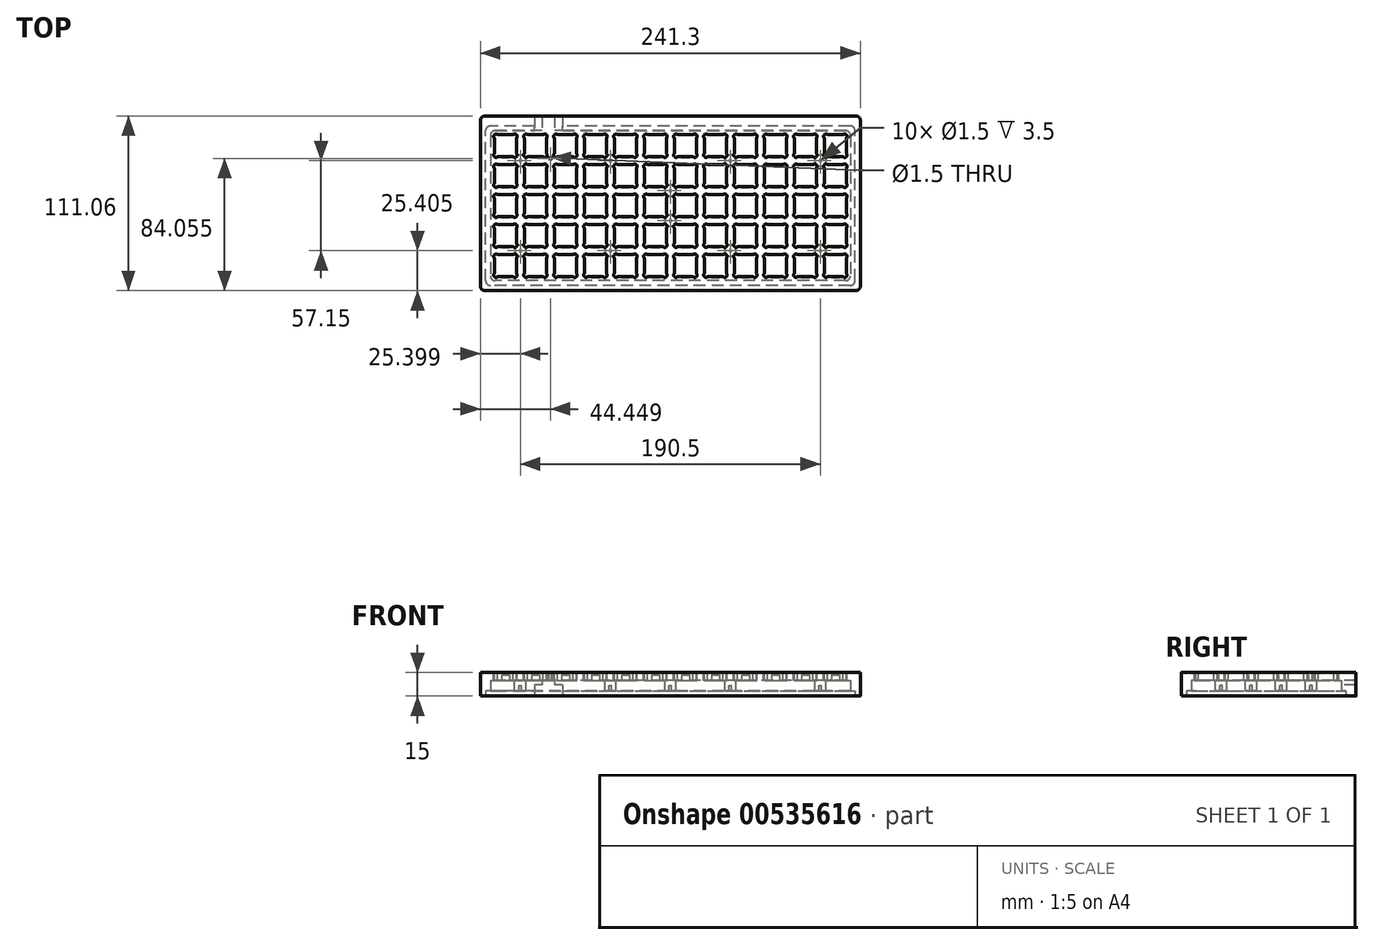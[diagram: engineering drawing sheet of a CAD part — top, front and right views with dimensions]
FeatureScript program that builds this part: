
annotation { "Feature Type Name" : "Feature", "Feature Type Description" : "" }
export const myFeature = defineFeature(function(context is Context, id is Id, definition is map)
    precondition{}
    {
        {
            var Q0;
            Q0=qCreatedBy(makeId("Top.planeOp"),FACE);
            var sketch = newSketch(context, id + "F0", { "sketchPlane" : qUnion([Q0])});
            skLineSegment(sketch, "E0", {"start": v(-120.65, 55.53) * mm, "end": v(120.65, 55.53) * mm});
            skLineSegment(sketch, "E1", {"start": v(120.65, 55.53) * mm, "end": v(120.65, -55.53) * mm});
            skLineSegment(sketch, "E2", {"start": v(120.65, -55.53) * mm, "end": v(-120.65, -55.53) * mm});
            skLineSegment(sketch, "E3", {"start": v(-120.65, -55.53) * mm, "end": v(-120.65, 55.53) * mm});
            skLineSegment(sketch, "E4", {"start": v(-111.78, -32.65) * mm, "end": v(-97.78, -32.65) * mm});
            skLineSegment(sketch, "E5", {"start": v(-97.78, -32.65) * mm, "end": v(-97.78, -46.65) * mm});
            skLineSegment(sketch, "E6", {"start": v(-97.78, -46.65) * mm, "end": v(-111.78, -46.65) * mm});
            skLineSegment(sketch, "E7", {"start": v(-111.78, -46.65) * mm, "end": v(-111.78, -32.65) * mm});
            skLineSegment(sketch, "E8", {"start": v(-92.73, -32.65) * mm, "end": v(-78.73, -32.65) * mm});
            skLineSegment(sketch, "E9", {"start": v(-78.73, -32.65) * mm, "end": v(-78.73, -46.65) * mm});
            skLineSegment(sketch, "E10", {"start": v(-78.73, -46.65) * mm, "end": v(-92.73, -46.65) * mm});
            skLineSegment(sketch, "E11", {"start": v(-92.73, -46.65) * mm, "end": v(-92.73, -32.65) * mm});
            skLineSegment(sketch, "E12", {"start": v(-73.68, -32.65) * mm, "end": v(-59.68, -32.65) * mm});
            skLineSegment(sketch, "E13", {"start": v(-59.68, -32.65) * mm, "end": v(-59.68, -46.65) * mm});
            skLineSegment(sketch, "E14", {"start": v(-59.68, -46.65) * mm, "end": v(-73.68, -46.65) * mm});
            skLineSegment(sketch, "E15", {"start": v(-73.68, -46.65) * mm, "end": v(-73.68, -32.65) * mm});
            skLineSegment(sketch, "E16", {"start": v(-54.63, -32.65) * mm, "end": v(-40.63, -32.65) * mm});
            skLineSegment(sketch, "E17", {"start": v(-40.63, -32.65) * mm, "end": v(-40.63, -46.65) * mm});
            skLineSegment(sketch, "E18", {"start": v(-40.63, -46.65) * mm, "end": v(-54.63, -46.65) * mm});
            skLineSegment(sketch, "E19", {"start": v(-54.63, -46.65) * mm, "end": v(-54.63, -32.65) * mm});
            skLineSegment(sketch, "E20", {"start": v(-35.58, -32.65) * mm, "end": v(-21.58, -32.65) * mm});
            skLineSegment(sketch, "E21", {"start": v(-21.58, -32.65) * mm, "end": v(-21.58, -46.65) * mm});
            skLineSegment(sketch, "E22", {"start": v(-21.58, -46.65) * mm, "end": v(-35.58, -46.65) * mm});
            skLineSegment(sketch, "E23", {"start": v(-35.58, -46.65) * mm, "end": v(-35.58, -32.65) * mm});
            skLineSegment(sketch, "E24", {"start": v(-16.53, -32.65) * mm, "end": v(-2.53, -32.65) * mm});
            skLineSegment(sketch, "E25", {"start": v(-2.53, -32.65) * mm, "end": v(-2.53, -46.65) * mm});
            skLineSegment(sketch, "E26", {"start": v(-2.53, -46.65) * mm, "end": v(-16.53, -46.65) * mm});
            skLineSegment(sketch, "E27", {"start": v(-16.53, -46.65) * mm, "end": v(-16.53, -32.65) * mm});
            skLineSegment(sketch, "E28", {"start": v(2.52, -32.65) * mm, "end": v(16.52, -32.65) * mm});
            skLineSegment(sketch, "E29", {"start": v(16.52, -32.65) * mm, "end": v(16.52, -46.65) * mm});
            skLineSegment(sketch, "E30", {"start": v(16.52, -46.65) * mm, "end": v(2.52, -46.65) * mm});
            skLineSegment(sketch, "E31", {"start": v(2.52, -46.65) * mm, "end": v(2.52, -32.65) * mm});
            skLineSegment(sketch, "E32", {"start": v(21.57, -32.65) * mm, "end": v(35.57, -32.65) * mm});
            skLineSegment(sketch, "E33", {"start": v(35.57, -32.65) * mm, "end": v(35.57, -46.65) * mm});
            skLineSegment(sketch, "E34", {"start": v(35.57, -46.65) * mm, "end": v(21.57, -46.65) * mm});
            skLineSegment(sketch, "E35", {"start": v(21.57, -46.65) * mm, "end": v(21.57, -32.65) * mm});
            skLineSegment(sketch, "E36", {"start": v(40.62, -32.65) * mm, "end": v(54.62, -32.65) * mm});
            skLineSegment(sketch, "E37", {"start": v(54.62, -32.65) * mm, "end": v(54.62, -46.65) * mm});
            skLineSegment(sketch, "E38", {"start": v(54.62, -46.65) * mm, "end": v(40.62, -46.65) * mm});
            skLineSegment(sketch, "E39", {"start": v(40.62, -46.65) * mm, "end": v(40.62, -32.65) * mm});
            skLineSegment(sketch, "E40", {"start": v(59.67, -32.65) * mm, "end": v(73.67, -32.65) * mm});
            skLineSegment(sketch, "E41", {"start": v(73.67, -32.65) * mm, "end": v(73.67, -46.65) * mm});
            skLineSegment(sketch, "E42", {"start": v(73.67, -46.65) * mm, "end": v(59.67, -46.65) * mm});
            skLineSegment(sketch, "E43", {"start": v(59.67, -46.65) * mm, "end": v(59.67, -32.65) * mm});
            skLineSegment(sketch, "E44", {"start": v(78.72, -32.65) * mm, "end": v(92.72, -32.65) * mm});
            skLineSegment(sketch, "E45", {"start": v(92.72, -32.65) * mm, "end": v(92.72, -46.65) * mm});
            skLineSegment(sketch, "E46", {"start": v(92.72, -46.65) * mm, "end": v(78.72, -46.65) * mm});
            skLineSegment(sketch, "E47", {"start": v(78.72, -46.65) * mm, "end": v(78.72, -32.65) * mm});
            skLineSegment(sketch, "E48", {"start": v(97.77, -32.65) * mm, "end": v(111.77, -32.65) * mm});
            skLineSegment(sketch, "E49", {"start": v(111.77, -32.65) * mm, "end": v(111.77, -46.65) * mm});
            skLineSegment(sketch, "E50", {"start": v(111.77, -46.65) * mm, "end": v(97.77, -46.65) * mm});
            skLineSegment(sketch, "E51", {"start": v(97.77, -46.65) * mm, "end": v(97.77, -32.65) * mm});
            skLineSegment(sketch, "E52", {"start": v(-111.78, -13.6) * mm, "end": v(-97.78, -13.6) * mm});
            skLineSegment(sketch, "E53", {"start": v(-97.78, -13.6) * mm, "end": v(-97.78, -27.6) * mm});
            skLineSegment(sketch, "E54", {"start": v(-97.78, -27.6) * mm, "end": v(-111.78, -27.6) * mm});
            skLineSegment(sketch, "E55", {"start": v(-111.78, -27.6) * mm, "end": v(-111.78, -13.6) * mm});
            skLineSegment(sketch, "E56", {"start": v(-92.73, -13.6) * mm, "end": v(-78.73, -13.6) * mm});
            skLineSegment(sketch, "E57", {"start": v(-78.73, -13.6) * mm, "end": v(-78.73, -27.6) * mm});
            skLineSegment(sketch, "E58", {"start": v(-78.73, -27.6) * mm, "end": v(-92.73, -27.6) * mm});
            skLineSegment(sketch, "E59", {"start": v(-92.73, -27.6) * mm, "end": v(-92.73, -13.6) * mm});
            skLineSegment(sketch, "E60", {"start": v(-73.68, -13.6) * mm, "end": v(-59.68, -13.6) * mm});
            skLineSegment(sketch, "E61", {"start": v(-59.68, -13.6) * mm, "end": v(-59.68, -27.6) * mm});
            skLineSegment(sketch, "E62", {"start": v(-59.68, -27.6) * mm, "end": v(-73.68, -27.6) * mm});
            skLineSegment(sketch, "E63", {"start": v(-73.68, -27.6) * mm, "end": v(-73.68, -13.6) * mm});
            skLineSegment(sketch, "E64", {"start": v(-54.63, -13.6) * mm, "end": v(-40.63, -13.6) * mm});
            skLineSegment(sketch, "E65", {"start": v(-40.63, -13.6) * mm, "end": v(-40.63, -27.6) * mm});
            skLineSegment(sketch, "E66", {"start": v(-40.63, -27.6) * mm, "end": v(-54.63, -27.6) * mm});
            skLineSegment(sketch, "E67", {"start": v(-54.63, -27.6) * mm, "end": v(-54.63, -13.6) * mm});
            skLineSegment(sketch, "E68", {"start": v(-35.58, -13.6) * mm, "end": v(-21.58, -13.6) * mm});
            skLineSegment(sketch, "E69", {"start": v(-21.58, -13.6) * mm, "end": v(-21.58, -27.6) * mm});
            skLineSegment(sketch, "E70", {"start": v(-21.58, -27.6) * mm, "end": v(-35.58, -27.6) * mm});
            skLineSegment(sketch, "E71", {"start": v(-35.58, -27.6) * mm, "end": v(-35.58, -13.6) * mm});
            skLineSegment(sketch, "E72", {"start": v(-16.53, -13.6) * mm, "end": v(-2.53, -13.6) * mm});
            skLineSegment(sketch, "E73", {"start": v(-2.53, -13.6) * mm, "end": v(-2.53, -27.6) * mm});
            skLineSegment(sketch, "E74", {"start": v(-2.53, -27.6) * mm, "end": v(-16.53, -27.6) * mm});
            skLineSegment(sketch, "E75", {"start": v(-16.53, -27.6) * mm, "end": v(-16.53, -13.6) * mm});
            skLineSegment(sketch, "E76", {"start": v(2.52, -13.6) * mm, "end": v(16.52, -13.6) * mm});
            skLineSegment(sketch, "E77", {"start": v(16.52, -13.6) * mm, "end": v(16.52, -27.6) * mm});
            skLineSegment(sketch, "E78", {"start": v(16.52, -27.6) * mm, "end": v(2.52, -27.6) * mm});
            skLineSegment(sketch, "E79", {"start": v(2.52, -27.6) * mm, "end": v(2.52, -13.6) * mm});
            skLineSegment(sketch, "E80", {"start": v(21.57, -13.6) * mm, "end": v(35.57, -13.6) * mm});
            skLineSegment(sketch, "E81", {"start": v(35.57, -13.6) * mm, "end": v(35.57, -27.6) * mm});
            skLineSegment(sketch, "E82", {"start": v(35.57, -27.6) * mm, "end": v(21.57, -27.6) * mm});
            skLineSegment(sketch, "E83", {"start": v(21.57, -27.6) * mm, "end": v(21.57, -13.6) * mm});
            skLineSegment(sketch, "E84", {"start": v(40.62, -13.6) * mm, "end": v(54.62, -13.6) * mm});
            skLineSegment(sketch, "E85", {"start": v(54.62, -13.6) * mm, "end": v(54.62, -27.6) * mm});
            skLineSegment(sketch, "E86", {"start": v(54.62, -27.6) * mm, "end": v(40.62, -27.6) * mm});
            skLineSegment(sketch, "E87", {"start": v(40.62, -27.6) * mm, "end": v(40.62, -13.6) * mm});
            skLineSegment(sketch, "E88", {"start": v(59.67, -13.6) * mm, "end": v(73.67, -13.6) * mm});
            skLineSegment(sketch, "E89", {"start": v(73.67, -13.6) * mm, "end": v(73.67, -27.6) * mm});
            skLineSegment(sketch, "E90", {"start": v(73.67, -27.6) * mm, "end": v(59.67, -27.6) * mm});
            skLineSegment(sketch, "E91", {"start": v(59.67, -27.6) * mm, "end": v(59.67, -13.6) * mm});
            skLineSegment(sketch, "E92", {"start": v(78.72, -13.6) * mm, "end": v(92.72, -13.6) * mm});
            skLineSegment(sketch, "E93", {"start": v(92.72, -13.6) * mm, "end": v(92.72, -27.6) * mm});
            skLineSegment(sketch, "E94", {"start": v(92.72, -27.6) * mm, "end": v(78.72, -27.6) * mm});
            skLineSegment(sketch, "E95", {"start": v(78.72, -27.6) * mm, "end": v(78.72, -13.6) * mm});
            skLineSegment(sketch, "E96", {"start": v(97.77, -13.6) * mm, "end": v(111.77, -13.6) * mm});
            skLineSegment(sketch, "E97", {"start": v(111.77, -13.6) * mm, "end": v(111.77, -27.6) * mm});
            skLineSegment(sketch, "E98", {"start": v(111.77, -27.6) * mm, "end": v(97.77, -27.6) * mm});
            skLineSegment(sketch, "E99", {"start": v(97.77, -27.6) * mm, "end": v(97.77, -13.6) * mm});
            skLineSegment(sketch, "E100", {"start": v(-111.78, 5.45) * mm, "end": v(-97.78, 5.45) * mm});
            skLineSegment(sketch, "E101", {"start": v(-97.78, 5.45) * mm, "end": v(-97.78, -8.55) * mm});
            skLineSegment(sketch, "E102", {"start": v(-97.78, -8.55) * mm, "end": v(-111.78, -8.55) * mm});
            skLineSegment(sketch, "E103", {"start": v(-111.78, -8.55) * mm, "end": v(-111.78, 5.45) * mm});
            skLineSegment(sketch, "E104", {"start": v(-92.73, 5.45) * mm, "end": v(-78.73, 5.45) * mm});
            skLineSegment(sketch, "E105", {"start": v(-78.73, 5.45) * mm, "end": v(-78.73, -8.55) * mm});
            skLineSegment(sketch, "E106", {"start": v(-78.73, -8.55) * mm, "end": v(-92.73, -8.55) * mm});
            skLineSegment(sketch, "E107", {"start": v(-92.73, -8.55) * mm, "end": v(-92.73, 5.45) * mm});
            skLineSegment(sketch, "E108", {"start": v(-73.68, 5.45) * mm, "end": v(-59.68, 5.45) * mm});
            skLineSegment(sketch, "E109", {"start": v(-59.68, 5.45) * mm, "end": v(-59.68, -8.55) * mm});
            skLineSegment(sketch, "E110", {"start": v(-59.68, -8.55) * mm, "end": v(-73.68, -8.55) * mm});
            skLineSegment(sketch, "E111", {"start": v(-73.68, -8.55) * mm, "end": v(-73.68, 5.45) * mm});
            skLineSegment(sketch, "E112", {"start": v(-54.63, 5.45) * mm, "end": v(-40.63, 5.45) * mm});
            skLineSegment(sketch, "E113", {"start": v(-40.63, 5.45) * mm, "end": v(-40.63, -8.55) * mm});
            skLineSegment(sketch, "E114", {"start": v(-40.63, -8.55) * mm, "end": v(-54.63, -8.55) * mm});
            skLineSegment(sketch, "E115", {"start": v(-54.63, -8.55) * mm, "end": v(-54.63, 5.45) * mm});
            skLineSegment(sketch, "E116", {"start": v(-35.58, 5.45) * mm, "end": v(-21.58, 5.45) * mm});
            skLineSegment(sketch, "E117", {"start": v(-21.58, 5.45) * mm, "end": v(-21.58, -8.55) * mm});
            skLineSegment(sketch, "E118", {"start": v(-21.58, -8.55) * mm, "end": v(-35.58, -8.55) * mm});
            skLineSegment(sketch, "E119", {"start": v(-35.58, -8.55) * mm, "end": v(-35.58, 5.45) * mm});
            skLineSegment(sketch, "E120", {"start": v(-16.53, 5.45) * mm, "end": v(-2.53, 5.45) * mm});
            skLineSegment(sketch, "E121", {"start": v(-2.53, 5.45) * mm, "end": v(-2.53, -8.55) * mm});
            skLineSegment(sketch, "E122", {"start": v(-2.53, -8.55) * mm, "end": v(-16.53, -8.55) * mm});
            skLineSegment(sketch, "E123", {"start": v(-16.53, -8.55) * mm, "end": v(-16.53, 5.45) * mm});
            skLineSegment(sketch, "E124", {"start": v(2.52, 5.45) * mm, "end": v(16.52, 5.45) * mm});
            skLineSegment(sketch, "E125", {"start": v(16.52, 5.45) * mm, "end": v(16.52, -8.55) * mm});
            skLineSegment(sketch, "E126", {"start": v(16.52, -8.55) * mm, "end": v(2.52, -8.55) * mm});
            skLineSegment(sketch, "E127", {"start": v(2.52, -8.55) * mm, "end": v(2.52, 5.45) * mm});
            skLineSegment(sketch, "E128", {"start": v(21.57, 5.45) * mm, "end": v(35.57, 5.45) * mm});
            skLineSegment(sketch, "E129", {"start": v(35.57, 5.45) * mm, "end": v(35.57, -8.55) * mm});
            skLineSegment(sketch, "E130", {"start": v(35.57, -8.55) * mm, "end": v(21.57, -8.55) * mm});
            skLineSegment(sketch, "E131", {"start": v(21.57, -8.55) * mm, "end": v(21.57, 5.45) * mm});
            skLineSegment(sketch, "E132", {"start": v(40.62, 5.45) * mm, "end": v(54.62, 5.45) * mm});
            skLineSegment(sketch, "E133", {"start": v(54.62, 5.45) * mm, "end": v(54.62, -8.55) * mm});
            skLineSegment(sketch, "E134", {"start": v(54.62, -8.55) * mm, "end": v(40.62, -8.55) * mm});
            skLineSegment(sketch, "E135", {"start": v(40.62, -8.55) * mm, "end": v(40.62, 5.45) * mm});
            skLineSegment(sketch, "E136", {"start": v(59.67, 5.45) * mm, "end": v(73.67, 5.45) * mm});
            skLineSegment(sketch, "E137", {"start": v(73.67, 5.45) * mm, "end": v(73.67, -8.55) * mm});
            skLineSegment(sketch, "E138", {"start": v(73.67, -8.55) * mm, "end": v(59.67, -8.55) * mm});
            skLineSegment(sketch, "E139", {"start": v(59.67, -8.55) * mm, "end": v(59.67, 5.45) * mm});
            skLineSegment(sketch, "E140", {"start": v(78.72, 5.45) * mm, "end": v(92.72, 5.45) * mm});
            skLineSegment(sketch, "E141", {"start": v(92.72, 5.45) * mm, "end": v(92.72, -8.55) * mm});
            skLineSegment(sketch, "E142", {"start": v(92.72, -8.55) * mm, "end": v(78.72, -8.55) * mm});
            skLineSegment(sketch, "E143", {"start": v(78.72, -8.55) * mm, "end": v(78.72, 5.45) * mm});
            skLineSegment(sketch, "E144", {"start": v(97.77, 5.45) * mm, "end": v(111.77, 5.45) * mm});
            skLineSegment(sketch, "E145", {"start": v(111.77, 5.45) * mm, "end": v(111.77, -8.55) * mm});
            skLineSegment(sketch, "E146", {"start": v(111.77, -8.55) * mm, "end": v(97.77, -8.55) * mm});
            skLineSegment(sketch, "E147", {"start": v(97.77, -8.55) * mm, "end": v(97.77, 5.45) * mm});
            skLineSegment(sketch, "E148", {"start": v(-111.78, 24.5) * mm, "end": v(-97.78, 24.5) * mm});
            skLineSegment(sketch, "E149", {"start": v(-97.78, 24.5) * mm, "end": v(-97.78, 10.5) * mm});
            skLineSegment(sketch, "E150", {"start": v(-97.78, 10.5) * mm, "end": v(-111.78, 10.5) * mm});
            skLineSegment(sketch, "E151", {"start": v(-111.78, 10.5) * mm, "end": v(-111.78, 24.5) * mm});
            skLineSegment(sketch, "E152", {"start": v(-92.73, 24.5) * mm, "end": v(-78.73, 24.5) * mm});
            skLineSegment(sketch, "E153", {"start": v(-78.73, 24.5) * mm, "end": v(-78.73, 10.5) * mm});
            skLineSegment(sketch, "E154", {"start": v(-78.73, 10.5) * mm, "end": v(-92.73, 10.5) * mm});
            skLineSegment(sketch, "E155", {"start": v(-92.73, 10.5) * mm, "end": v(-92.73, 24.5) * mm});
            skLineSegment(sketch, "E156", {"start": v(-73.68, 24.5) * mm, "end": v(-59.68, 24.5) * mm});
            skLineSegment(sketch, "E157", {"start": v(-59.68, 24.5) * mm, "end": v(-59.68, 10.5) * mm});
            skLineSegment(sketch, "E158", {"start": v(-59.68, 10.5) * mm, "end": v(-73.68, 10.5) * mm});
            skLineSegment(sketch, "E159", {"start": v(-73.68, 10.5) * mm, "end": v(-73.68, 24.5) * mm});
            skLineSegment(sketch, "E160", {"start": v(-54.63, 24.5) * mm, "end": v(-40.63, 24.5) * mm});
            skLineSegment(sketch, "E161", {"start": v(-40.63, 24.5) * mm, "end": v(-40.63, 10.5) * mm});
            skLineSegment(sketch, "E162", {"start": v(-40.63, 10.5) * mm, "end": v(-54.63, 10.5) * mm});
            skLineSegment(sketch, "E163", {"start": v(-54.63, 10.5) * mm, "end": v(-54.63, 24.5) * mm});
            skLineSegment(sketch, "E164", {"start": v(-35.58, 24.5) * mm, "end": v(-21.58, 24.5) * mm});
            skLineSegment(sketch, "E165", {"start": v(-21.58, 24.5) * mm, "end": v(-21.58, 10.5) * mm});
            skLineSegment(sketch, "E166", {"start": v(-21.58, 10.5) * mm, "end": v(-35.58, 10.5) * mm});
            skLineSegment(sketch, "E167", {"start": v(-35.58, 10.5) * mm, "end": v(-35.58, 24.5) * mm});
            skLineSegment(sketch, "E168", {"start": v(-16.53, 24.5) * mm, "end": v(-2.53, 24.5) * mm});
            skLineSegment(sketch, "E169", {"start": v(-2.53, 24.5) * mm, "end": v(-2.53, 10.5) * mm});
            skLineSegment(sketch, "E170", {"start": v(-2.53, 10.5) * mm, "end": v(-16.53, 10.5) * mm});
            skLineSegment(sketch, "E171", {"start": v(-16.53, 10.5) * mm, "end": v(-16.53, 24.5) * mm});
            skLineSegment(sketch, "E172", {"start": v(2.52, 24.5) * mm, "end": v(16.52, 24.5) * mm});
            skLineSegment(sketch, "E173", {"start": v(16.52, 24.5) * mm, "end": v(16.52, 10.5) * mm});
            skLineSegment(sketch, "E174", {"start": v(16.52, 10.5) * mm, "end": v(2.52, 10.5) * mm});
            skLineSegment(sketch, "E175", {"start": v(2.52, 10.5) * mm, "end": v(2.52, 24.5) * mm});
            skLineSegment(sketch, "E176", {"start": v(21.57, 24.5) * mm, "end": v(35.57, 24.5) * mm});
            skLineSegment(sketch, "E177", {"start": v(35.57, 24.5) * mm, "end": v(35.57, 10.5) * mm});
            skLineSegment(sketch, "E178", {"start": v(35.57, 10.5) * mm, "end": v(21.57, 10.5) * mm});
            skLineSegment(sketch, "E179", {"start": v(21.57, 10.5) * mm, "end": v(21.57, 24.5) * mm});
            skLineSegment(sketch, "E180", {"start": v(40.62, 24.5) * mm, "end": v(54.62, 24.5) * mm});
            skLineSegment(sketch, "E181", {"start": v(54.62, 24.5) * mm, "end": v(54.62, 10.5) * mm});
            skLineSegment(sketch, "E182", {"start": v(54.62, 10.5) * mm, "end": v(40.62, 10.5) * mm});
            skLineSegment(sketch, "E183", {"start": v(40.62, 10.5) * mm, "end": v(40.62, 24.5) * mm});
            skLineSegment(sketch, "E184", {"start": v(59.67, 24.5) * mm, "end": v(73.67, 24.5) * mm});
            skLineSegment(sketch, "E185", {"start": v(73.67, 24.5) * mm, "end": v(73.67, 10.5) * mm});
            skLineSegment(sketch, "E186", {"start": v(73.67, 10.5) * mm, "end": v(59.67, 10.5) * mm});
            skLineSegment(sketch, "E187", {"start": v(59.67, 10.5) * mm, "end": v(59.67, 24.5) * mm});
            skLineSegment(sketch, "E188", {"start": v(78.72, 24.5) * mm, "end": v(92.72, 24.5) * mm});
            skLineSegment(sketch, "E189", {"start": v(92.72, 24.5) * mm, "end": v(92.72, 10.5) * mm});
            skLineSegment(sketch, "E190", {"start": v(92.72, 10.5) * mm, "end": v(78.72, 10.5) * mm});
            skLineSegment(sketch, "E191", {"start": v(78.72, 10.5) * mm, "end": v(78.72, 24.5) * mm});
            skLineSegment(sketch, "E192", {"start": v(97.77, 24.5) * mm, "end": v(111.77, 24.5) * mm});
            skLineSegment(sketch, "E193", {"start": v(111.77, 24.5) * mm, "end": v(111.77, 10.5) * mm});
            skLineSegment(sketch, "E194", {"start": v(111.77, 10.5) * mm, "end": v(97.77, 10.5) * mm});
            skLineSegment(sketch, "E195", {"start": v(97.77, 10.5) * mm, "end": v(97.77, 24.5) * mm});
            skLineSegment(sketch, "E196", {"start": v(-111.78, 43.55) * mm, "end": v(-97.78, 43.55) * mm});
            skLineSegment(sketch, "E197", {"start": v(-97.78, 43.55) * mm, "end": v(-97.78, 29.55) * mm});
            skLineSegment(sketch, "E198", {"start": v(-97.78, 29.55) * mm, "end": v(-111.78, 29.55) * mm});
            skLineSegment(sketch, "E199", {"start": v(-111.78, 29.55) * mm, "end": v(-111.78, 43.55) * mm});
            skLineSegment(sketch, "E200", {"start": v(-92.73, 43.55) * mm, "end": v(-78.73, 43.55) * mm});
            skLineSegment(sketch, "E201", {"start": v(-78.73, 43.55) * mm, "end": v(-78.73, 29.55) * mm});
            skLineSegment(sketch, "E202", {"start": v(-78.73, 29.55) * mm, "end": v(-92.73, 29.55) * mm});
            skLineSegment(sketch, "E203", {"start": v(-92.73, 29.55) * mm, "end": v(-92.73, 43.55) * mm});
            skLineSegment(sketch, "E204", {"start": v(-73.68, 43.55) * mm, "end": v(-59.68, 43.55) * mm});
            skLineSegment(sketch, "E205", {"start": v(-59.68, 43.55) * mm, "end": v(-59.68, 29.55) * mm});
            skLineSegment(sketch, "E206", {"start": v(-59.68, 29.55) * mm, "end": v(-73.68, 29.55) * mm});
            skLineSegment(sketch, "E207", {"start": v(-73.68, 29.55) * mm, "end": v(-73.68, 43.55) * mm});
            skLineSegment(sketch, "E208", {"start": v(-54.63, 43.55) * mm, "end": v(-40.63, 43.55) * mm});
            skLineSegment(sketch, "E209", {"start": v(-40.63, 43.55) * mm, "end": v(-40.63, 29.55) * mm});
            skLineSegment(sketch, "E210", {"start": v(-40.63, 29.55) * mm, "end": v(-54.63, 29.55) * mm});
            skLineSegment(sketch, "E211", {"start": v(-54.63, 29.55) * mm, "end": v(-54.63, 43.55) * mm});
            skLineSegment(sketch, "E212", {"start": v(-35.58, 43.55) * mm, "end": v(-21.58, 43.55) * mm});
            skLineSegment(sketch, "E213", {"start": v(-21.58, 43.55) * mm, "end": v(-21.58, 29.55) * mm});
            skLineSegment(sketch, "E214", {"start": v(-21.58, 29.55) * mm, "end": v(-35.58, 29.55) * mm});
            skLineSegment(sketch, "E215", {"start": v(-35.58, 29.55) * mm, "end": v(-35.58, 43.55) * mm});
            skLineSegment(sketch, "E216", {"start": v(-16.53, 43.55) * mm, "end": v(-2.53, 43.55) * mm});
            skLineSegment(sketch, "E217", {"start": v(-2.53, 43.55) * mm, "end": v(-2.53, 29.55) * mm});
            skLineSegment(sketch, "E218", {"start": v(-2.53, 29.55) * mm, "end": v(-16.53, 29.55) * mm});
            skLineSegment(sketch, "E219", {"start": v(-16.53, 29.55) * mm, "end": v(-16.53, 43.55) * mm});
            skLineSegment(sketch, "E220", {"start": v(2.52, 43.55) * mm, "end": v(16.52, 43.55) * mm});
            skLineSegment(sketch, "E221", {"start": v(16.52, 43.55) * mm, "end": v(16.52, 29.55) * mm});
            skLineSegment(sketch, "E222", {"start": v(16.52, 29.55) * mm, "end": v(2.52, 29.55) * mm});
            skLineSegment(sketch, "E223", {"start": v(2.52, 29.55) * mm, "end": v(2.52, 43.55) * mm});
            skLineSegment(sketch, "E224", {"start": v(21.57, 43.55) * mm, "end": v(35.57, 43.55) * mm});
            skLineSegment(sketch, "E225", {"start": v(35.57, 43.55) * mm, "end": v(35.57, 29.55) * mm});
            skLineSegment(sketch, "E226", {"start": v(35.57, 29.55) * mm, "end": v(21.57, 29.55) * mm});
            skLineSegment(sketch, "E227", {"start": v(21.57, 29.55) * mm, "end": v(21.57, 43.55) * mm});
            skLineSegment(sketch, "E228", {"start": v(40.62, 43.55) * mm, "end": v(54.62, 43.55) * mm});
            skLineSegment(sketch, "E229", {"start": v(54.62, 43.55) * mm, "end": v(54.62, 29.55) * mm});
            skLineSegment(sketch, "E230", {"start": v(54.62, 29.55) * mm, "end": v(40.62, 29.55) * mm});
            skLineSegment(sketch, "E231", {"start": v(40.62, 29.55) * mm, "end": v(40.62, 43.55) * mm});
            skLineSegment(sketch, "E232", {"start": v(59.67, 43.55) * mm, "end": v(73.67, 43.55) * mm});
            skLineSegment(sketch, "E233", {"start": v(73.67, 43.55) * mm, "end": v(73.67, 29.55) * mm});
            skLineSegment(sketch, "E234", {"start": v(73.67, 29.55) * mm, "end": v(59.67, 29.55) * mm});
            skLineSegment(sketch, "E235", {"start": v(59.67, 29.55) * mm, "end": v(59.67, 43.55) * mm});
            skLineSegment(sketch, "E236", {"start": v(78.72, 43.55) * mm, "end": v(92.72, 43.55) * mm});
            skLineSegment(sketch, "E237", {"start": v(92.72, 43.55) * mm, "end": v(92.72, 29.55) * mm});
            skLineSegment(sketch, "E238", {"start": v(92.72, 29.55) * mm, "end": v(78.72, 29.55) * mm});
            skLineSegment(sketch, "E239", {"start": v(78.72, 29.55) * mm, "end": v(78.72, 43.55) * mm});
            skLineSegment(sketch, "E240", {"start": v(97.77, 43.55) * mm, "end": v(111.77, 43.55) * mm});
            skLineSegment(sketch, "E241", {"start": v(111.77, 43.55) * mm, "end": v(111.77, 29.55) * mm});
            skLineSegment(sketch, "E242", {"start": v(111.77, 29.55) * mm, "end": v(97.77, 29.55) * mm});
            skLineSegment(sketch, "E243", {"start": v(97.77, 29.55) * mm, "end": v(97.77, 43.55) * mm});
            skSolve(sketch);
        }
        {
            var Q0;
            Q0 = qSketchRegion(id + "F0", true);
            extrude(context, id + "F1", {"entities" : qUnion([Q0]), "oppositeDirection" : true, "depth" : 15 * mm, "offsetDistance" : 25 * mm});
        }
        {
            var Q0;
            Q0=makeQuery(id+"F1.opExtrude","SWEPT_EDGE",EDGE,{"disambiguationData":[OSD([sQuery(id+"F0.wireOp",EDGE,"E0"),sQuery(id+"F0.wireOp",EDGE,"E3")])]});
            var Q1;
            Q1=makeQuery(id+"F1.opExtrude","SWEPT_EDGE",EDGE,{"disambiguationData":[OSD([sQuery(id+"F0.wireOp",EDGE,"E2"),sQuery(id+"F0.wireOp",EDGE,"E3")])]});
            var Q2;
            Q2=makeQuery(id+"F1.opExtrude","SWEPT_EDGE",EDGE,{"disambiguationData":[OSD([sQuery(id+"F0.wireOp",EDGE,"E1"),sQuery(id+"F0.wireOp",EDGE,"E2")])]});
            var Q3;
            Q3=makeQuery(id+"F1.opExtrude","SWEPT_EDGE",EDGE,{"disambiguationData":[OSD([sQuery(id+"F0.wireOp",EDGE,"E0"),sQuery(id+"F0.wireOp",EDGE,"E1")])]});
            fillet(context, id + "F2", {"entities" : qUnion([Q0, Q1, Q2, Q3]), "radius" : 3 * mm, "tangentPropagation" : true, "allowEdgeOverflow" : false});
        }
        {
            var Q0;
            Q0=makeQuery(id+"F1.opExtrude","CAP_FACE",FACE,{"disambiguationData":[OSD([sQuery(id+"F0.wireOp",EDGE,"E0"),sQuery(id+"F0.wireOp",EDGE,"E1"),sQuery(id+"F0.wireOp",EDGE,"E2"),sQuery(id+"F0.wireOp",EDGE,"E3"),sQuery(id+"F0.wireOp",EDGE,"E4"),sQuery(id+"F0.wireOp",EDGE,"E5"),sQuery(id+"F0.wireOp",EDGE,"E6"),sQuery(id+"F0.wireOp",EDGE,"E7"),sQuery(id+"F0.wireOp",EDGE,"E8"),sQuery(id+"F0.wireOp",EDGE,"E9"),sQuery(id+"F0.wireOp",EDGE,"E10"),sQuery(id+"F0.wireOp",EDGE,"E11"),sQuery(id+"F0.wireOp",EDGE,"E12"),sQuery(id+"F0.wireOp",EDGE,"E13"),sQuery(id+"F0.wireOp",EDGE,"E14"),sQuery(id+"F0.wireOp",EDGE,"E15"),sQuery(id+"F0.wireOp",EDGE,"E16"),sQuery(id+"F0.wireOp",EDGE,"E17"),sQuery(id+"F0.wireOp",EDGE,"E18"),sQuery(id+"F0.wireOp",EDGE,"E19"),sQuery(id+"F0.wireOp",EDGE,"E20"),sQuery(id+"F0.wireOp",EDGE,"E21"),sQuery(id+"F0.wireOp",EDGE,"E22"),sQuery(id+"F0.wireOp",EDGE,"E23"),sQuery(id+"F0.wireOp",EDGE,"E24"),sQuery(id+"F0.wireOp",EDGE,"E25"),sQuery(id+"F0.wireOp",EDGE,"E26"),sQuery(id+"F0.wireOp",EDGE,"E27"),sQuery(id+"F0.wireOp",EDGE,"E28"),sQuery(id+"F0.wireOp",EDGE,"E29"),sQuery(id+"F0.wireOp",EDGE,"E30"),sQuery(id+"F0.wireOp",EDGE,"E31"),sQuery(id+"F0.wireOp",EDGE,"E32"),sQuery(id+"F0.wireOp",EDGE,"E33"),sQuery(id+"F0.wireOp",EDGE,"E34"),sQuery(id+"F0.wireOp",EDGE,"E35"),sQuery(id+"F0.wireOp",EDGE,"E36"),sQuery(id+"F0.wireOp",EDGE,"E37"),sQuery(id+"F0.wireOp",EDGE,"E38"),sQuery(id+"F0.wireOp",EDGE,"E39"),sQuery(id+"F0.wireOp",EDGE,"E40"),sQuery(id+"F0.wireOp",EDGE,"E41"),sQuery(id+"F0.wireOp",EDGE,"E42"),sQuery(id+"F0.wireOp",EDGE,"E43"),sQuery(id+"F0.wireOp",EDGE,"E44"),sQuery(id+"F0.wireOp",EDGE,"E45"),sQuery(id+"F0.wireOp",EDGE,"E46"),sQuery(id+"F0.wireOp",EDGE,"E47"),sQuery(id+"F0.wireOp",EDGE,"E48"),sQuery(id+"F0.wireOp",EDGE,"E49"),sQuery(id+"F0.wireOp",EDGE,"E50"),sQuery(id+"F0.wireOp",EDGE,"E51"),sQuery(id+"F0.wireOp",EDGE,"E52"),sQuery(id+"F0.wireOp",EDGE,"E53"),sQuery(id+"F0.wireOp",EDGE,"E54"),sQuery(id+"F0.wireOp",EDGE,"E55"),sQuery(id+"F0.wireOp",EDGE,"E56"),sQuery(id+"F0.wireOp",EDGE,"E57"),sQuery(id+"F0.wireOp",EDGE,"E58"),sQuery(id+"F0.wireOp",EDGE,"E59"),sQuery(id+"F0.wireOp",EDGE,"E60"),sQuery(id+"F0.wireOp",EDGE,"E61"),sQuery(id+"F0.wireOp",EDGE,"E62"),sQuery(id+"F0.wireOp",EDGE,"E63"),sQuery(id+"F0.wireOp",EDGE,"E64"),sQuery(id+"F0.wireOp",EDGE,"E65"),sQuery(id+"F0.wireOp",EDGE,"E66"),sQuery(id+"F0.wireOp",EDGE,"E67"),sQuery(id+"F0.wireOp",EDGE,"E68"),sQuery(id+"F0.wireOp",EDGE,"E69"),sQuery(id+"F0.wireOp",EDGE,"E70"),sQuery(id+"F0.wireOp",EDGE,"E71"),sQuery(id+"F0.wireOp",EDGE,"E72"),sQuery(id+"F0.wireOp",EDGE,"E73"),sQuery(id+"F0.wireOp",EDGE,"E74"),sQuery(id+"F0.wireOp",EDGE,"E75"),sQuery(id+"F0.wireOp",EDGE,"E76"),sQuery(id+"F0.wireOp",EDGE,"E77"),sQuery(id+"F0.wireOp",EDGE,"E78"),sQuery(id+"F0.wireOp",EDGE,"E79"),sQuery(id+"F0.wireOp",EDGE,"E80"),sQuery(id+"F0.wireOp",EDGE,"E81"),sQuery(id+"F0.wireOp",EDGE,"E82"),sQuery(id+"F0.wireOp",EDGE,"E83"),sQuery(id+"F0.wireOp",EDGE,"E84"),sQuery(id+"F0.wireOp",EDGE,"E85"),sQuery(id+"F0.wireOp",EDGE,"E86"),sQuery(id+"F0.wireOp",EDGE,"E87"),sQuery(id+"F0.wireOp",EDGE,"E88"),sQuery(id+"F0.wireOp",EDGE,"E89"),sQuery(id+"F0.wireOp",EDGE,"E90"),sQuery(id+"F0.wireOp",EDGE,"E91"),sQuery(id+"F0.wireOp",EDGE,"E92"),sQuery(id+"F0.wireOp",EDGE,"E93"),sQuery(id+"F0.wireOp",EDGE,"E94"),sQuery(id+"F0.wireOp",EDGE,"E95"),sQuery(id+"F0.wireOp",EDGE,"E96"),sQuery(id+"F0.wireOp",EDGE,"E97"),sQuery(id+"F0.wireOp",EDGE,"E98"),sQuery(id+"F0.wireOp",EDGE,"E99"),sQuery(id+"F0.wireOp",EDGE,"E100"),sQuery(id+"F0.wireOp",EDGE,"E101"),sQuery(id+"F0.wireOp",EDGE,"E102"),sQuery(id+"F0.wireOp",EDGE,"E103"),sQuery(id+"F0.wireOp",EDGE,"E104"),sQuery(id+"F0.wireOp",EDGE,"E105"),sQuery(id+"F0.wireOp",EDGE,"E106"),sQuery(id+"F0.wireOp",EDGE,"E107"),sQuery(id+"F0.wireOp",EDGE,"E108"),sQuery(id+"F0.wireOp",EDGE,"E109"),sQuery(id+"F0.wireOp",EDGE,"E110"),sQuery(id+"F0.wireOp",EDGE,"E111"),sQuery(id+"F0.wireOp",EDGE,"E112"),sQuery(id+"F0.wireOp",EDGE,"E113"),sQuery(id+"F0.wireOp",EDGE,"E114"),sQuery(id+"F0.wireOp",EDGE,"E115"),sQuery(id+"F0.wireOp",EDGE,"E116"),sQuery(id+"F0.wireOp",EDGE,"E117"),sQuery(id+"F0.wireOp",EDGE,"E118"),sQuery(id+"F0.wireOp",EDGE,"E119"),sQuery(id+"F0.wireOp",EDGE,"E120"),sQuery(id+"F0.wireOp",EDGE,"E121"),sQuery(id+"F0.wireOp",EDGE,"E122"),sQuery(id+"F0.wireOp",EDGE,"E123"),sQuery(id+"F0.wireOp",EDGE,"E124"),sQuery(id+"F0.wireOp",EDGE,"E125"),sQuery(id+"F0.wireOp",EDGE,"E126"),sQuery(id+"F0.wireOp",EDGE,"E127"),sQuery(id+"F0.wireOp",EDGE,"E128"),sQuery(id+"F0.wireOp",EDGE,"E129"),sQuery(id+"F0.wireOp",EDGE,"E130"),sQuery(id+"F0.wireOp",EDGE,"E131"),sQuery(id+"F0.wireOp",EDGE,"E132"),sQuery(id+"F0.wireOp",EDGE,"E133"),sQuery(id+"F0.wireOp",EDGE,"E134"),sQuery(id+"F0.wireOp",EDGE,"E135"),sQuery(id+"F0.wireOp",EDGE,"E136"),sQuery(id+"F0.wireOp",EDGE,"E137"),sQuery(id+"F0.wireOp",EDGE,"E138"),sQuery(id+"F0.wireOp",EDGE,"E139"),sQuery(id+"F0.wireOp",EDGE,"E140"),sQuery(id+"F0.wireOp",EDGE,"E141"),sQuery(id+"F0.wireOp",EDGE,"E142"),sQuery(id+"F0.wireOp",EDGE,"E143"),sQuery(id+"F0.wireOp",EDGE,"E144"),sQuery(id+"F0.wireOp",EDGE,"E145"),sQuery(id+"F0.wireOp",EDGE,"E146"),sQuery(id+"F0.wireOp",EDGE,"E147"),sQuery(id+"F0.wireOp",EDGE,"E148"),sQuery(id+"F0.wireOp",EDGE,"E149"),sQuery(id+"F0.wireOp",EDGE,"E150"),sQuery(id+"F0.wireOp",EDGE,"E151"),sQuery(id+"F0.wireOp",EDGE,"E152"),sQuery(id+"F0.wireOp",EDGE,"E153"),sQuery(id+"F0.wireOp",EDGE,"E154"),sQuery(id+"F0.wireOp",EDGE,"E155"),sQuery(id+"F0.wireOp",EDGE,"E156"),sQuery(id+"F0.wireOp",EDGE,"E157"),sQuery(id+"F0.wireOp",EDGE,"E158"),sQuery(id+"F0.wireOp",EDGE,"E159"),sQuery(id+"F0.wireOp",EDGE,"E160"),sQuery(id+"F0.wireOp",EDGE,"E161"),sQuery(id+"F0.wireOp",EDGE,"E162"),sQuery(id+"F0.wireOp",EDGE,"E163"),sQuery(id+"F0.wireOp",EDGE,"E164"),sQuery(id+"F0.wireOp",EDGE,"E165"),sQuery(id+"F0.wireOp",EDGE,"E166"),sQuery(id+"F0.wireOp",EDGE,"E167"),sQuery(id+"F0.wireOp",EDGE,"E168"),sQuery(id+"F0.wireOp",EDGE,"E169"),sQuery(id+"F0.wireOp",EDGE,"E170"),sQuery(id+"F0.wireOp",EDGE,"E171"),sQuery(id+"F0.wireOp",EDGE,"E172"),sQuery(id+"F0.wireOp",EDGE,"E173"),sQuery(id+"F0.wireOp",EDGE,"E174"),sQuery(id+"F0.wireOp",EDGE,"E175"),sQuery(id+"F0.wireOp",EDGE,"E176"),sQuery(id+"F0.wireOp",EDGE,"E177"),sQuery(id+"F0.wireOp",EDGE,"E178"),sQuery(id+"F0.wireOp",EDGE,"E179"),sQuery(id+"F0.wireOp",EDGE,"E180"),sQuery(id+"F0.wireOp",EDGE,"E181"),sQuery(id+"F0.wireOp",EDGE,"E182"),sQuery(id+"F0.wireOp",EDGE,"E183"),sQuery(id+"F0.wireOp",EDGE,"E184"),sQuery(id+"F0.wireOp",EDGE,"E185"),sQuery(id+"F0.wireOp",EDGE,"E186"),sQuery(id+"F0.wireOp",EDGE,"E187"),sQuery(id+"F0.wireOp",EDGE,"E188"),sQuery(id+"F0.wireOp",EDGE,"E189"),sQuery(id+"F0.wireOp",EDGE,"E190"),sQuery(id+"F0.wireOp",EDGE,"E191"),sQuery(id+"F0.wireOp",EDGE,"E192"),sQuery(id+"F0.wireOp",EDGE,"E193"),sQuery(id+"F0.wireOp",EDGE,"E194"),sQuery(id+"F0.wireOp",EDGE,"E195"),sQuery(id+"F0.wireOp",EDGE,"E196"),sQuery(id+"F0.wireOp",EDGE,"E197"),sQuery(id+"F0.wireOp",EDGE,"E198"),sQuery(id+"F0.wireOp",EDGE,"E199"),sQuery(id+"F0.wireOp",EDGE,"E200"),sQuery(id+"F0.wireOp",EDGE,"E201"),sQuery(id+"F0.wireOp",EDGE,"E202"),sQuery(id+"F0.wireOp",EDGE,"E203"),sQuery(id+"F0.wireOp",EDGE,"E204"),sQuery(id+"F0.wireOp",EDGE,"E205"),sQuery(id+"F0.wireOp",EDGE,"E206"),sQuery(id+"F0.wireOp",EDGE,"E207"),sQuery(id+"F0.wireOp",EDGE,"E208"),sQuery(id+"F0.wireOp",EDGE,"E209"),sQuery(id+"F0.wireOp",EDGE,"E210"),sQuery(id+"F0.wireOp",EDGE,"E211"),sQuery(id+"F0.wireOp",EDGE,"E212"),sQuery(id+"F0.wireOp",EDGE,"E213"),sQuery(id+"F0.wireOp",EDGE,"E214"),sQuery(id+"F0.wireOp",EDGE,"E215"),sQuery(id+"F0.wireOp",EDGE,"E216"),sQuery(id+"F0.wireOp",EDGE,"E217"),sQuery(id+"F0.wireOp",EDGE,"E218"),sQuery(id+"F0.wireOp",EDGE,"E219"),sQuery(id+"F0.wireOp",EDGE,"E220"),sQuery(id+"F0.wireOp",EDGE,"E221"),sQuery(id+"F0.wireOp",EDGE,"E222"),sQuery(id+"F0.wireOp",EDGE,"E223"),sQuery(id+"F0.wireOp",EDGE,"E224"),sQuery(id+"F0.wireOp",EDGE,"E225"),sQuery(id+"F0.wireOp",EDGE,"E226"),sQuery(id+"F0.wireOp",EDGE,"E227"),sQuery(id+"F0.wireOp",EDGE,"E228"),sQuery(id+"F0.wireOp",EDGE,"E229"),sQuery(id+"F0.wireOp",EDGE,"E230"),sQuery(id+"F0.wireOp",EDGE,"E231"),sQuery(id+"F0.wireOp",EDGE,"E232"),sQuery(id+"F0.wireOp",EDGE,"E233"),sQuery(id+"F0.wireOp",EDGE,"E234"),sQuery(id+"F0.wireOp",EDGE,"E235"),sQuery(id+"F0.wireOp",EDGE,"E236"),sQuery(id+"F0.wireOp",EDGE,"E237"),sQuery(id+"F0.wireOp",EDGE,"E238"),sQuery(id+"F0.wireOp",EDGE,"E239"),sQuery(id+"F0.wireOp",EDGE,"E240"),sQuery(id+"F0.wireOp",EDGE,"E241"),sQuery(id+"F0.wireOp",EDGE,"E242"),sQuery(id+"F0.wireOp",EDGE,"E243")])],"isStart":false});
            var sketch = newSketch(context, id + "F3", { "sketchPlane" : qUnion([Q0])});
            skLineSegment(sketch, "E244.bottom", {"start": v(111.3, -46.08) * mm, "end": v(-111.3, -46.08) * mm});
            skLineSegment(sketch, "E244.top", {"start": v(111.3, 49.18) * mm, "end": v(-111.3, 49.18) * mm});
            skLineSegment(sketch, "E244.left", {"start": v(114.3, -43.08) * mm, "end": v(114.3, 46.18) * mm});
            skLineSegment(sketch, "E244.right", {"start": v(-114.3, -43.08) * mm, "end": v(-114.3, 46.18) * mm});
            skPoint(sketch, "E245.visualSharp", {"position": v(114.3, -46.08) * mm});
            skArc(sketch, "E245.filletArc", {"start": v(111.3, -46.08) * mm, "mid": v(113.42, -45.2) * mm, "end": v(114.3, -43.08) * mm});
            skPoint(sketch, "E246.visualSharp", {"position": v(-114.3, -46.08) * mm});
            skArc(sketch, "E246.filletArc", {"start": v(-114.3, -43.08) * mm, "mid": v(-113.42, -45.2) * mm, "end": v(-111.3, -46.08) * mm});
            skPoint(sketch, "E247.visualSharp", {"position": v(-114.3, 49.18) * mm});
            skArc(sketch, "E247.filletArc", {"start": v(-111.3, 49.18) * mm, "mid": v(-113.42, 48.3) * mm, "end": v(-114.3, 46.18) * mm});
            skPoint(sketch, "E248.visualSharp", {"position": v(114.3, 49.18) * mm});
            skArc(sketch, "E248.filletArc", {"start": v(114.3, 46.18) * mm, "mid": v(113.42, 48.3) * mm, "end": v(111.3, 49.18) * mm});
            skSolve(sketch);
        }
        {
            var Q0;
            Q0=makeQuery(id+"F3.imprint","IMPRINT",FACE,{"disambiguationData":[TD([[makeQuery(id+"F3.imprint","IMPRINT",EDGE,{"derivedFrom":sQuery(id+"F3.wireOp",EDGE,"E244.bottom")}),-1.0]])]});
            extrude(context, id + "F4", {"entities" : qUnion([Q0]), "operationType" : NewBodyOperationType.REMOVE, "oppositeDirection" : true, "depth" : 10 * mm, "offsetDistance" : 25 * mm});
        }
        {
            var Q0;
            Q0=makeQuery(id+"F1.opExtrude","CAP_FACE",FACE,{"disambiguationData":[OSD([sQuery(id+"F0.wireOp",EDGE,"E0"),sQuery(id+"F0.wireOp",EDGE,"E1"),sQuery(id+"F0.wireOp",EDGE,"E2"),sQuery(id+"F0.wireOp",EDGE,"E3"),sQuery(id+"F0.wireOp",EDGE,"E4"),sQuery(id+"F0.wireOp",EDGE,"E5"),sQuery(id+"F0.wireOp",EDGE,"E6"),sQuery(id+"F0.wireOp",EDGE,"E7"),sQuery(id+"F0.wireOp",EDGE,"E8"),sQuery(id+"F0.wireOp",EDGE,"E9"),sQuery(id+"F0.wireOp",EDGE,"E10"),sQuery(id+"F0.wireOp",EDGE,"E11"),sQuery(id+"F0.wireOp",EDGE,"E12"),sQuery(id+"F0.wireOp",EDGE,"E13"),sQuery(id+"F0.wireOp",EDGE,"E14"),sQuery(id+"F0.wireOp",EDGE,"E15"),sQuery(id+"F0.wireOp",EDGE,"E16"),sQuery(id+"F0.wireOp",EDGE,"E17"),sQuery(id+"F0.wireOp",EDGE,"E18"),sQuery(id+"F0.wireOp",EDGE,"E19"),sQuery(id+"F0.wireOp",EDGE,"E20"),sQuery(id+"F0.wireOp",EDGE,"E21"),sQuery(id+"F0.wireOp",EDGE,"E22"),sQuery(id+"F0.wireOp",EDGE,"E23"),sQuery(id+"F0.wireOp",EDGE,"E24"),sQuery(id+"F0.wireOp",EDGE,"E25"),sQuery(id+"F0.wireOp",EDGE,"E26"),sQuery(id+"F0.wireOp",EDGE,"E27"),sQuery(id+"F0.wireOp",EDGE,"E28"),sQuery(id+"F0.wireOp",EDGE,"E29"),sQuery(id+"F0.wireOp",EDGE,"E30"),sQuery(id+"F0.wireOp",EDGE,"E31"),sQuery(id+"F0.wireOp",EDGE,"E32"),sQuery(id+"F0.wireOp",EDGE,"E33"),sQuery(id+"F0.wireOp",EDGE,"E34"),sQuery(id+"F0.wireOp",EDGE,"E35"),sQuery(id+"F0.wireOp",EDGE,"E36"),sQuery(id+"F0.wireOp",EDGE,"E37"),sQuery(id+"F0.wireOp",EDGE,"E38"),sQuery(id+"F0.wireOp",EDGE,"E39"),sQuery(id+"F0.wireOp",EDGE,"E40"),sQuery(id+"F0.wireOp",EDGE,"E41"),sQuery(id+"F0.wireOp",EDGE,"E42"),sQuery(id+"F0.wireOp",EDGE,"E43"),sQuery(id+"F0.wireOp",EDGE,"E44"),sQuery(id+"F0.wireOp",EDGE,"E45"),sQuery(id+"F0.wireOp",EDGE,"E46"),sQuery(id+"F0.wireOp",EDGE,"E47"),sQuery(id+"F0.wireOp",EDGE,"E48"),sQuery(id+"F0.wireOp",EDGE,"E49"),sQuery(id+"F0.wireOp",EDGE,"E50"),sQuery(id+"F0.wireOp",EDGE,"E51"),sQuery(id+"F0.wireOp",EDGE,"E52"),sQuery(id+"F0.wireOp",EDGE,"E53"),sQuery(id+"F0.wireOp",EDGE,"E54"),sQuery(id+"F0.wireOp",EDGE,"E55"),sQuery(id+"F0.wireOp",EDGE,"E56"),sQuery(id+"F0.wireOp",EDGE,"E57"),sQuery(id+"F0.wireOp",EDGE,"E58"),sQuery(id+"F0.wireOp",EDGE,"E59"),sQuery(id+"F0.wireOp",EDGE,"E60"),sQuery(id+"F0.wireOp",EDGE,"E61"),sQuery(id+"F0.wireOp",EDGE,"E62"),sQuery(id+"F0.wireOp",EDGE,"E63"),sQuery(id+"F0.wireOp",EDGE,"E64"),sQuery(id+"F0.wireOp",EDGE,"E65"),sQuery(id+"F0.wireOp",EDGE,"E66"),sQuery(id+"F0.wireOp",EDGE,"E67"),sQuery(id+"F0.wireOp",EDGE,"E68"),sQuery(id+"F0.wireOp",EDGE,"E69"),sQuery(id+"F0.wireOp",EDGE,"E70"),sQuery(id+"F0.wireOp",EDGE,"E71"),sQuery(id+"F0.wireOp",EDGE,"E72"),sQuery(id+"F0.wireOp",EDGE,"E73"),sQuery(id+"F0.wireOp",EDGE,"E74"),sQuery(id+"F0.wireOp",EDGE,"E75"),sQuery(id+"F0.wireOp",EDGE,"E76"),sQuery(id+"F0.wireOp",EDGE,"E77"),sQuery(id+"F0.wireOp",EDGE,"E78"),sQuery(id+"F0.wireOp",EDGE,"E79"),sQuery(id+"F0.wireOp",EDGE,"E80"),sQuery(id+"F0.wireOp",EDGE,"E81"),sQuery(id+"F0.wireOp",EDGE,"E82"),sQuery(id+"F0.wireOp",EDGE,"E83"),sQuery(id+"F0.wireOp",EDGE,"E84"),sQuery(id+"F0.wireOp",EDGE,"E85"),sQuery(id+"F0.wireOp",EDGE,"E86"),sQuery(id+"F0.wireOp",EDGE,"E87"),sQuery(id+"F0.wireOp",EDGE,"E88"),sQuery(id+"F0.wireOp",EDGE,"E89"),sQuery(id+"F0.wireOp",EDGE,"E90"),sQuery(id+"F0.wireOp",EDGE,"E91"),sQuery(id+"F0.wireOp",EDGE,"E92"),sQuery(id+"F0.wireOp",EDGE,"E93"),sQuery(id+"F0.wireOp",EDGE,"E94"),sQuery(id+"F0.wireOp",EDGE,"E95"),sQuery(id+"F0.wireOp",EDGE,"E96"),sQuery(id+"F0.wireOp",EDGE,"E97"),sQuery(id+"F0.wireOp",EDGE,"E98"),sQuery(id+"F0.wireOp",EDGE,"E99"),sQuery(id+"F0.wireOp",EDGE,"E100"),sQuery(id+"F0.wireOp",EDGE,"E101"),sQuery(id+"F0.wireOp",EDGE,"E102"),sQuery(id+"F0.wireOp",EDGE,"E103"),sQuery(id+"F0.wireOp",EDGE,"E104"),sQuery(id+"F0.wireOp",EDGE,"E105"),sQuery(id+"F0.wireOp",EDGE,"E106"),sQuery(id+"F0.wireOp",EDGE,"E107"),sQuery(id+"F0.wireOp",EDGE,"E108"),sQuery(id+"F0.wireOp",EDGE,"E109"),sQuery(id+"F0.wireOp",EDGE,"E110"),sQuery(id+"F0.wireOp",EDGE,"E111"),sQuery(id+"F0.wireOp",EDGE,"E112"),sQuery(id+"F0.wireOp",EDGE,"E113"),sQuery(id+"F0.wireOp",EDGE,"E114"),sQuery(id+"F0.wireOp",EDGE,"E115"),sQuery(id+"F0.wireOp",EDGE,"E116"),sQuery(id+"F0.wireOp",EDGE,"E117"),sQuery(id+"F0.wireOp",EDGE,"E118"),sQuery(id+"F0.wireOp",EDGE,"E119"),sQuery(id+"F0.wireOp",EDGE,"E120"),sQuery(id+"F0.wireOp",EDGE,"E121"),sQuery(id+"F0.wireOp",EDGE,"E122"),sQuery(id+"F0.wireOp",EDGE,"E123"),sQuery(id+"F0.wireOp",EDGE,"E124"),sQuery(id+"F0.wireOp",EDGE,"E125"),sQuery(id+"F0.wireOp",EDGE,"E126"),sQuery(id+"F0.wireOp",EDGE,"E127"),sQuery(id+"F0.wireOp",EDGE,"E128"),sQuery(id+"F0.wireOp",EDGE,"E129"),sQuery(id+"F0.wireOp",EDGE,"E130"),sQuery(id+"F0.wireOp",EDGE,"E131"),sQuery(id+"F0.wireOp",EDGE,"E132"),sQuery(id+"F0.wireOp",EDGE,"E133"),sQuery(id+"F0.wireOp",EDGE,"E134"),sQuery(id+"F0.wireOp",EDGE,"E135"),sQuery(id+"F0.wireOp",EDGE,"E136"),sQuery(id+"F0.wireOp",EDGE,"E137"),sQuery(id+"F0.wireOp",EDGE,"E138"),sQuery(id+"F0.wireOp",EDGE,"E139"),sQuery(id+"F0.wireOp",EDGE,"E140"),sQuery(id+"F0.wireOp",EDGE,"E141"),sQuery(id+"F0.wireOp",EDGE,"E142"),sQuery(id+"F0.wireOp",EDGE,"E143"),sQuery(id+"F0.wireOp",EDGE,"E144"),sQuery(id+"F0.wireOp",EDGE,"E145"),sQuery(id+"F0.wireOp",EDGE,"E146"),sQuery(id+"F0.wireOp",EDGE,"E147"),sQuery(id+"F0.wireOp",EDGE,"E148"),sQuery(id+"F0.wireOp",EDGE,"E149"),sQuery(id+"F0.wireOp",EDGE,"E150"),sQuery(id+"F0.wireOp",EDGE,"E151"),sQuery(id+"F0.wireOp",EDGE,"E152"),sQuery(id+"F0.wireOp",EDGE,"E153"),sQuery(id+"F0.wireOp",EDGE,"E154"),sQuery(id+"F0.wireOp",EDGE,"E155"),sQuery(id+"F0.wireOp",EDGE,"E156"),sQuery(id+"F0.wireOp",EDGE,"E157"),sQuery(id+"F0.wireOp",EDGE,"E158"),sQuery(id+"F0.wireOp",EDGE,"E159"),sQuery(id+"F0.wireOp",EDGE,"E160"),sQuery(id+"F0.wireOp",EDGE,"E161"),sQuery(id+"F0.wireOp",EDGE,"E162"),sQuery(id+"F0.wireOp",EDGE,"E163"),sQuery(id+"F0.wireOp",EDGE,"E164"),sQuery(id+"F0.wireOp",EDGE,"E165"),sQuery(id+"F0.wireOp",EDGE,"E166"),sQuery(id+"F0.wireOp",EDGE,"E167"),sQuery(id+"F0.wireOp",EDGE,"E168"),sQuery(id+"F0.wireOp",EDGE,"E169"),sQuery(id+"F0.wireOp",EDGE,"E170"),sQuery(id+"F0.wireOp",EDGE,"E171"),sQuery(id+"F0.wireOp",EDGE,"E172"),sQuery(id+"F0.wireOp",EDGE,"E173"),sQuery(id+"F0.wireOp",EDGE,"E174"),sQuery(id+"F0.wireOp",EDGE,"E175"),sQuery(id+"F0.wireOp",EDGE,"E176"),sQuery(id+"F0.wireOp",EDGE,"E177"),sQuery(id+"F0.wireOp",EDGE,"E178"),sQuery(id+"F0.wireOp",EDGE,"E179"),sQuery(id+"F0.wireOp",EDGE,"E180"),sQuery(id+"F0.wireOp",EDGE,"E181"),sQuery(id+"F0.wireOp",EDGE,"E182"),sQuery(id+"F0.wireOp",EDGE,"E183"),sQuery(id+"F0.wireOp",EDGE,"E184"),sQuery(id+"F0.wireOp",EDGE,"E185"),sQuery(id+"F0.wireOp",EDGE,"E186"),sQuery(id+"F0.wireOp",EDGE,"E187"),sQuery(id+"F0.wireOp",EDGE,"E188"),sQuery(id+"F0.wireOp",EDGE,"E189"),sQuery(id+"F0.wireOp",EDGE,"E190"),sQuery(id+"F0.wireOp",EDGE,"E191"),sQuery(id+"F0.wireOp",EDGE,"E192"),sQuery(id+"F0.wireOp",EDGE,"E193"),sQuery(id+"F0.wireOp",EDGE,"E194"),sQuery(id+"F0.wireOp",EDGE,"E195"),sQuery(id+"F0.wireOp",EDGE,"E196"),sQuery(id+"F0.wireOp",EDGE,"E197"),sQuery(id+"F0.wireOp",EDGE,"E198"),sQuery(id+"F0.wireOp",EDGE,"E199"),sQuery(id+"F0.wireOp",EDGE,"E200"),sQuery(id+"F0.wireOp",EDGE,"E201"),sQuery(id+"F0.wireOp",EDGE,"E202"),sQuery(id+"F0.wireOp",EDGE,"E203"),sQuery(id+"F0.wireOp",EDGE,"E204"),sQuery(id+"F0.wireOp",EDGE,"E205"),sQuery(id+"F0.wireOp",EDGE,"E206"),sQuery(id+"F0.wireOp",EDGE,"E207"),sQuery(id+"F0.wireOp",EDGE,"E208"),sQuery(id+"F0.wireOp",EDGE,"E209"),sQuery(id+"F0.wireOp",EDGE,"E210"),sQuery(id+"F0.wireOp",EDGE,"E211"),sQuery(id+"F0.wireOp",EDGE,"E212"),sQuery(id+"F0.wireOp",EDGE,"E213"),sQuery(id+"F0.wireOp",EDGE,"E214"),sQuery(id+"F0.wireOp",EDGE,"E215"),sQuery(id+"F0.wireOp",EDGE,"E216"),sQuery(id+"F0.wireOp",EDGE,"E217"),sQuery(id+"F0.wireOp",EDGE,"E218"),sQuery(id+"F0.wireOp",EDGE,"E219"),sQuery(id+"F0.wireOp",EDGE,"E220"),sQuery(id+"F0.wireOp",EDGE,"E221"),sQuery(id+"F0.wireOp",EDGE,"E222"),sQuery(id+"F0.wireOp",EDGE,"E223"),sQuery(id+"F0.wireOp",EDGE,"E224"),sQuery(id+"F0.wireOp",EDGE,"E225"),sQuery(id+"F0.wireOp",EDGE,"E226"),sQuery(id+"F0.wireOp",EDGE,"E227"),sQuery(id+"F0.wireOp",EDGE,"E228"),sQuery(id+"F0.wireOp",EDGE,"E229"),sQuery(id+"F0.wireOp",EDGE,"E230"),sQuery(id+"F0.wireOp",EDGE,"E231"),sQuery(id+"F0.wireOp",EDGE,"E232"),sQuery(id+"F0.wireOp",EDGE,"E233"),sQuery(id+"F0.wireOp",EDGE,"E234"),sQuery(id+"F0.wireOp",EDGE,"E235"),sQuery(id+"F0.wireOp",EDGE,"E236"),sQuery(id+"F0.wireOp",EDGE,"E237"),sQuery(id+"F0.wireOp",EDGE,"E238"),sQuery(id+"F0.wireOp",EDGE,"E239"),sQuery(id+"F0.wireOp",EDGE,"E240"),sQuery(id+"F0.wireOp",EDGE,"E241"),sQuery(id+"F0.wireOp",EDGE,"E242"),sQuery(id+"F0.wireOp",EDGE,"E243")])],"isStart":false});
            var sketch = newSketch(context, id + "F5", { "sketchPlane" : qUnion([Q0])});
            skLineSegment(sketch, "E249.bottom", {"start": v(-68.4, -55.53) * mm, "end": v(-86.44, -55.53) * mm});
            skLineSegment(sketch, "E249.top", {"start": v(-68.4, -46.08) * mm, "end": v(-86.44, -46.08) * mm});
            skLineSegment(sketch, "E249.left", {"start": v(-68.4, -55.53) * mm, "end": v(-68.4, -46.08) * mm});
            skLineSegment(sketch, "E249.right", {"start": v(-86.44, -55.53) * mm, "end": v(-86.44, -46.08) * mm});
            skSolve(sketch);
        }
        {
            var Q0;
            Q0 = qSketchRegion(id + "F5", true);
            extrude(context, id + "F6", {"entities" : qUnion([Q0]), "operationType" : NewBodyOperationType.REMOVE, "oppositeDirection" : true, "depth" : 7.02 * mm, "offsetDistance" : 25 * mm});
        }
        {
            var Q0;
            Q0=makeQuery(id+"F6.boolean.opBoolean","COPY",FACE,{"derivedFrom":makeQuery(id+"F6.opExtrude","CAP_FACE",FACE,{"disambiguationData":[OSD([sQuery(id+"F5.wireOp",EDGE,"E249.bottom"),sQuery(id+"F5.wireOp",EDGE,"E249.top"),sQuery(id+"F5.wireOp",EDGE,"E249.left"),sQuery(id+"F5.wireOp",EDGE,"E249.right")])],"isStart":false})});
            var sketch = newSketch(context, id + "F7", { "sketchPlane" : qUnion([Q0])});
            skLineSegment(sketch, "E250.bottom", {"start": v(-73.45, -55.53) * mm, "end": v(-81.4, -55.53) * mm});
            skLineSegment(sketch, "E250.top", {"start": v(-73.45, -46.08) * mm, "end": v(-81.4, -46.08) * mm});
            skLineSegment(sketch, "E250.left", {"start": v(-73.45, -55.53) * mm, "end": v(-73.45, -46.08) * mm});
            skLineSegment(sketch, "E250.right", {"start": v(-81.4, -55.53) * mm, "end": v(-81.4, -46.08) * mm});
            skPoint(sketch, "E251", {"position": v(-77.42, -55.53) * mm});
            skSolve(sketch);
        }
        {
            var Q0;
            Q0 = qSketchRegion(id + "F7", true);
            extrude(context, id + "F8", {"entities" : qUnion([Q0]), "operationType" : NewBodyOperationType.REMOVE, "oppositeDirection" : true, "depth" : 2.98 * mm, "offsetDistance" : 25 * mm});
        }
        {
            var Q0;
            Q0=makeQuery(id+"F1.opExtrude","CAP_FACE",FACE,{"disambiguationData":[OSD([sQuery(id+"F0.wireOp",EDGE,"E0"),sQuery(id+"F0.wireOp",EDGE,"E1"),sQuery(id+"F0.wireOp",EDGE,"E2"),sQuery(id+"F0.wireOp",EDGE,"E3"),sQuery(id+"F0.wireOp",EDGE,"E4"),sQuery(id+"F0.wireOp",EDGE,"E5"),sQuery(id+"F0.wireOp",EDGE,"E6"),sQuery(id+"F0.wireOp",EDGE,"E7"),sQuery(id+"F0.wireOp",EDGE,"E8"),sQuery(id+"F0.wireOp",EDGE,"E9"),sQuery(id+"F0.wireOp",EDGE,"E10"),sQuery(id+"F0.wireOp",EDGE,"E11"),sQuery(id+"F0.wireOp",EDGE,"E12"),sQuery(id+"F0.wireOp",EDGE,"E13"),sQuery(id+"F0.wireOp",EDGE,"E14"),sQuery(id+"F0.wireOp",EDGE,"E15"),sQuery(id+"F0.wireOp",EDGE,"E16"),sQuery(id+"F0.wireOp",EDGE,"E17"),sQuery(id+"F0.wireOp",EDGE,"E18"),sQuery(id+"F0.wireOp",EDGE,"E19"),sQuery(id+"F0.wireOp",EDGE,"E20"),sQuery(id+"F0.wireOp",EDGE,"E21"),sQuery(id+"F0.wireOp",EDGE,"E22"),sQuery(id+"F0.wireOp",EDGE,"E23"),sQuery(id+"F0.wireOp",EDGE,"E24"),sQuery(id+"F0.wireOp",EDGE,"E25"),sQuery(id+"F0.wireOp",EDGE,"E26"),sQuery(id+"F0.wireOp",EDGE,"E27"),sQuery(id+"F0.wireOp",EDGE,"E28"),sQuery(id+"F0.wireOp",EDGE,"E29"),sQuery(id+"F0.wireOp",EDGE,"E30"),sQuery(id+"F0.wireOp",EDGE,"E31"),sQuery(id+"F0.wireOp",EDGE,"E32"),sQuery(id+"F0.wireOp",EDGE,"E33"),sQuery(id+"F0.wireOp",EDGE,"E34"),sQuery(id+"F0.wireOp",EDGE,"E35"),sQuery(id+"F0.wireOp",EDGE,"E36"),sQuery(id+"F0.wireOp",EDGE,"E37"),sQuery(id+"F0.wireOp",EDGE,"E38"),sQuery(id+"F0.wireOp",EDGE,"E39"),sQuery(id+"F0.wireOp",EDGE,"E40"),sQuery(id+"F0.wireOp",EDGE,"E41"),sQuery(id+"F0.wireOp",EDGE,"E42"),sQuery(id+"F0.wireOp",EDGE,"E43"),sQuery(id+"F0.wireOp",EDGE,"E44"),sQuery(id+"F0.wireOp",EDGE,"E45"),sQuery(id+"F0.wireOp",EDGE,"E46"),sQuery(id+"F0.wireOp",EDGE,"E47"),sQuery(id+"F0.wireOp",EDGE,"E48"),sQuery(id+"F0.wireOp",EDGE,"E49"),sQuery(id+"F0.wireOp",EDGE,"E50"),sQuery(id+"F0.wireOp",EDGE,"E51"),sQuery(id+"F0.wireOp",EDGE,"E52"),sQuery(id+"F0.wireOp",EDGE,"E53"),sQuery(id+"F0.wireOp",EDGE,"E54"),sQuery(id+"F0.wireOp",EDGE,"E55"),sQuery(id+"F0.wireOp",EDGE,"E56"),sQuery(id+"F0.wireOp",EDGE,"E57"),sQuery(id+"F0.wireOp",EDGE,"E58"),sQuery(id+"F0.wireOp",EDGE,"E59"),sQuery(id+"F0.wireOp",EDGE,"E60"),sQuery(id+"F0.wireOp",EDGE,"E61"),sQuery(id+"F0.wireOp",EDGE,"E62"),sQuery(id+"F0.wireOp",EDGE,"E63"),sQuery(id+"F0.wireOp",EDGE,"E64"),sQuery(id+"F0.wireOp",EDGE,"E65"),sQuery(id+"F0.wireOp",EDGE,"E66"),sQuery(id+"F0.wireOp",EDGE,"E67"),sQuery(id+"F0.wireOp",EDGE,"E68"),sQuery(id+"F0.wireOp",EDGE,"E69"),sQuery(id+"F0.wireOp",EDGE,"E70"),sQuery(id+"F0.wireOp",EDGE,"E71"),sQuery(id+"F0.wireOp",EDGE,"E72"),sQuery(id+"F0.wireOp",EDGE,"E73"),sQuery(id+"F0.wireOp",EDGE,"E74"),sQuery(id+"F0.wireOp",EDGE,"E75"),sQuery(id+"F0.wireOp",EDGE,"E76"),sQuery(id+"F0.wireOp",EDGE,"E77"),sQuery(id+"F0.wireOp",EDGE,"E78"),sQuery(id+"F0.wireOp",EDGE,"E79"),sQuery(id+"F0.wireOp",EDGE,"E80"),sQuery(id+"F0.wireOp",EDGE,"E81"),sQuery(id+"F0.wireOp",EDGE,"E82"),sQuery(id+"F0.wireOp",EDGE,"E83"),sQuery(id+"F0.wireOp",EDGE,"E84"),sQuery(id+"F0.wireOp",EDGE,"E85"),sQuery(id+"F0.wireOp",EDGE,"E86"),sQuery(id+"F0.wireOp",EDGE,"E87"),sQuery(id+"F0.wireOp",EDGE,"E88"),sQuery(id+"F0.wireOp",EDGE,"E89"),sQuery(id+"F0.wireOp",EDGE,"E90"),sQuery(id+"F0.wireOp",EDGE,"E91"),sQuery(id+"F0.wireOp",EDGE,"E92"),sQuery(id+"F0.wireOp",EDGE,"E93"),sQuery(id+"F0.wireOp",EDGE,"E94"),sQuery(id+"F0.wireOp",EDGE,"E95"),sQuery(id+"F0.wireOp",EDGE,"E96"),sQuery(id+"F0.wireOp",EDGE,"E97"),sQuery(id+"F0.wireOp",EDGE,"E98"),sQuery(id+"F0.wireOp",EDGE,"E99"),sQuery(id+"F0.wireOp",EDGE,"E100"),sQuery(id+"F0.wireOp",EDGE,"E101"),sQuery(id+"F0.wireOp",EDGE,"E102"),sQuery(id+"F0.wireOp",EDGE,"E103"),sQuery(id+"F0.wireOp",EDGE,"E104"),sQuery(id+"F0.wireOp",EDGE,"E105"),sQuery(id+"F0.wireOp",EDGE,"E106"),sQuery(id+"F0.wireOp",EDGE,"E107"),sQuery(id+"F0.wireOp",EDGE,"E108"),sQuery(id+"F0.wireOp",EDGE,"E109"),sQuery(id+"F0.wireOp",EDGE,"E110"),sQuery(id+"F0.wireOp",EDGE,"E111"),sQuery(id+"F0.wireOp",EDGE,"E112"),sQuery(id+"F0.wireOp",EDGE,"E113"),sQuery(id+"F0.wireOp",EDGE,"E114"),sQuery(id+"F0.wireOp",EDGE,"E115"),sQuery(id+"F0.wireOp",EDGE,"E116"),sQuery(id+"F0.wireOp",EDGE,"E117"),sQuery(id+"F0.wireOp",EDGE,"E118"),sQuery(id+"F0.wireOp",EDGE,"E119"),sQuery(id+"F0.wireOp",EDGE,"E120"),sQuery(id+"F0.wireOp",EDGE,"E121"),sQuery(id+"F0.wireOp",EDGE,"E122"),sQuery(id+"F0.wireOp",EDGE,"E123"),sQuery(id+"F0.wireOp",EDGE,"E124"),sQuery(id+"F0.wireOp",EDGE,"E125"),sQuery(id+"F0.wireOp",EDGE,"E126"),sQuery(id+"F0.wireOp",EDGE,"E127"),sQuery(id+"F0.wireOp",EDGE,"E128"),sQuery(id+"F0.wireOp",EDGE,"E129"),sQuery(id+"F0.wireOp",EDGE,"E130"),sQuery(id+"F0.wireOp",EDGE,"E131"),sQuery(id+"F0.wireOp",EDGE,"E132"),sQuery(id+"F0.wireOp",EDGE,"E133"),sQuery(id+"F0.wireOp",EDGE,"E134"),sQuery(id+"F0.wireOp",EDGE,"E135"),sQuery(id+"F0.wireOp",EDGE,"E136"),sQuery(id+"F0.wireOp",EDGE,"E137"),sQuery(id+"F0.wireOp",EDGE,"E138"),sQuery(id+"F0.wireOp",EDGE,"E139"),sQuery(id+"F0.wireOp",EDGE,"E140"),sQuery(id+"F0.wireOp",EDGE,"E141"),sQuery(id+"F0.wireOp",EDGE,"E142"),sQuery(id+"F0.wireOp",EDGE,"E143"),sQuery(id+"F0.wireOp",EDGE,"E144"),sQuery(id+"F0.wireOp",EDGE,"E145"),sQuery(id+"F0.wireOp",EDGE,"E146"),sQuery(id+"F0.wireOp",EDGE,"E147"),sQuery(id+"F0.wireOp",EDGE,"E148"),sQuery(id+"F0.wireOp",EDGE,"E149"),sQuery(id+"F0.wireOp",EDGE,"E150"),sQuery(id+"F0.wireOp",EDGE,"E151"),sQuery(id+"F0.wireOp",EDGE,"E152"),sQuery(id+"F0.wireOp",EDGE,"E153"),sQuery(id+"F0.wireOp",EDGE,"E154"),sQuery(id+"F0.wireOp",EDGE,"E155"),sQuery(id+"F0.wireOp",EDGE,"E156"),sQuery(id+"F0.wireOp",EDGE,"E157"),sQuery(id+"F0.wireOp",EDGE,"E158"),sQuery(id+"F0.wireOp",EDGE,"E159"),sQuery(id+"F0.wireOp",EDGE,"E160"),sQuery(id+"F0.wireOp",EDGE,"E161"),sQuery(id+"F0.wireOp",EDGE,"E162"),sQuery(id+"F0.wireOp",EDGE,"E163"),sQuery(id+"F0.wireOp",EDGE,"E164"),sQuery(id+"F0.wireOp",EDGE,"E165"),sQuery(id+"F0.wireOp",EDGE,"E166"),sQuery(id+"F0.wireOp",EDGE,"E167"),sQuery(id+"F0.wireOp",EDGE,"E168"),sQuery(id+"F0.wireOp",EDGE,"E169"),sQuery(id+"F0.wireOp",EDGE,"E170"),sQuery(id+"F0.wireOp",EDGE,"E171"),sQuery(id+"F0.wireOp",EDGE,"E172"),sQuery(id+"F0.wireOp",EDGE,"E173"),sQuery(id+"F0.wireOp",EDGE,"E174"),sQuery(id+"F0.wireOp",EDGE,"E175"),sQuery(id+"F0.wireOp",EDGE,"E176"),sQuery(id+"F0.wireOp",EDGE,"E177"),sQuery(id+"F0.wireOp",EDGE,"E178"),sQuery(id+"F0.wireOp",EDGE,"E179"),sQuery(id+"F0.wireOp",EDGE,"E180"),sQuery(id+"F0.wireOp",EDGE,"E181"),sQuery(id+"F0.wireOp",EDGE,"E182"),sQuery(id+"F0.wireOp",EDGE,"E183"),sQuery(id+"F0.wireOp",EDGE,"E184"),sQuery(id+"F0.wireOp",EDGE,"E185"),sQuery(id+"F0.wireOp",EDGE,"E186"),sQuery(id+"F0.wireOp",EDGE,"E187"),sQuery(id+"F0.wireOp",EDGE,"E188"),sQuery(id+"F0.wireOp",EDGE,"E189"),sQuery(id+"F0.wireOp",EDGE,"E190"),sQuery(id+"F0.wireOp",EDGE,"E191"),sQuery(id+"F0.wireOp",EDGE,"E192"),sQuery(id+"F0.wireOp",EDGE,"E193"),sQuery(id+"F0.wireOp",EDGE,"E194"),sQuery(id+"F0.wireOp",EDGE,"E195"),sQuery(id+"F0.wireOp",EDGE,"E196"),sQuery(id+"F0.wireOp",EDGE,"E197"),sQuery(id+"F0.wireOp",EDGE,"E198"),sQuery(id+"F0.wireOp",EDGE,"E199"),sQuery(id+"F0.wireOp",EDGE,"E200"),sQuery(id+"F0.wireOp",EDGE,"E201"),sQuery(id+"F0.wireOp",EDGE,"E202"),sQuery(id+"F0.wireOp",EDGE,"E203"),sQuery(id+"F0.wireOp",EDGE,"E204"),sQuery(id+"F0.wireOp",EDGE,"E205"),sQuery(id+"F0.wireOp",EDGE,"E206"),sQuery(id+"F0.wireOp",EDGE,"E207"),sQuery(id+"F0.wireOp",EDGE,"E208"),sQuery(id+"F0.wireOp",EDGE,"E209"),sQuery(id+"F0.wireOp",EDGE,"E210"),sQuery(id+"F0.wireOp",EDGE,"E211"),sQuery(id+"F0.wireOp",EDGE,"E212"),sQuery(id+"F0.wireOp",EDGE,"E213"),sQuery(id+"F0.wireOp",EDGE,"E214"),sQuery(id+"F0.wireOp",EDGE,"E215"),sQuery(id+"F0.wireOp",EDGE,"E216"),sQuery(id+"F0.wireOp",EDGE,"E217"),sQuery(id+"F0.wireOp",EDGE,"E218"),sQuery(id+"F0.wireOp",EDGE,"E219"),sQuery(id+"F0.wireOp",EDGE,"E220"),sQuery(id+"F0.wireOp",EDGE,"E221"),sQuery(id+"F0.wireOp",EDGE,"E222"),sQuery(id+"F0.wireOp",EDGE,"E223"),sQuery(id+"F0.wireOp",EDGE,"E224"),sQuery(id+"F0.wireOp",EDGE,"E225"),sQuery(id+"F0.wireOp",EDGE,"E226"),sQuery(id+"F0.wireOp",EDGE,"E227"),sQuery(id+"F0.wireOp",EDGE,"E228"),sQuery(id+"F0.wireOp",EDGE,"E229"),sQuery(id+"F0.wireOp",EDGE,"E230"),sQuery(id+"F0.wireOp",EDGE,"E231"),sQuery(id+"F0.wireOp",EDGE,"E232"),sQuery(id+"F0.wireOp",EDGE,"E233"),sQuery(id+"F0.wireOp",EDGE,"E234"),sQuery(id+"F0.wireOp",EDGE,"E235"),sQuery(id+"F0.wireOp",EDGE,"E236"),sQuery(id+"F0.wireOp",EDGE,"E237"),sQuery(id+"F0.wireOp",EDGE,"E238"),sQuery(id+"F0.wireOp",EDGE,"E239"),sQuery(id+"F0.wireOp",EDGE,"E240"),sQuery(id+"F0.wireOp",EDGE,"E241"),sQuery(id+"F0.wireOp",EDGE,"E242"),sQuery(id+"F0.wireOp",EDGE,"E243")])],"isStart":false});
            var sketch = newSketch(context, id + "F9", { "sketchPlane" : qUnion([Q0])});
            skLineSegment(sketch, "E252.bottom", {"start": v(114.3, 52.18) * mm, "end": v(-114.3, 52.18) * mm});
            skLineSegment(sketch, "E252.top", {"start": v(114.3, -49.08) * mm, "end": v(-114.3, -49.08) * mm});
            skLineSegment(sketch, "E252.left", {"start": v(117.3, 49.18) * mm, "end": v(117.3, -46.08) * mm});
            skLineSegment(sketch, "E252.right", {"start": v(-117.3, 49.18) * mm, "end": v(-117.3, -46.08) * mm});
            skPoint(sketch, "E253.visualSharp", {"position": v(117.3, -49.08) * mm});
            skArc(sketch, "E253.filletArc", {"start": v(114.3, -49.08) * mm, "mid": v(116.42, -48.2) * mm, "end": v(117.3, -46.08) * mm});
            skPoint(sketch, "E254.visualSharp", {"position": v(-117.3, -49.08) * mm});
            skArc(sketch, "E254.filletArc", {"start": v(-117.3, -46.08) * mm, "mid": v(-116.42, -48.2) * mm, "end": v(-114.3, -49.08) * mm});
            skPoint(sketch, "E255.visualSharp", {"position": v(-117.3, 52.18) * mm});
            skArc(sketch, "E255.filletArc", {"start": v(-114.3, 52.18) * mm, "mid": v(-116.42, 51.3) * mm, "end": v(-117.3, 49.18) * mm});
            skPoint(sketch, "E256.visualSharp", {"position": v(117.3, 52.18) * mm});
            skArc(sketch, "E256.filletArc", {"start": v(117.3, 49.18) * mm, "mid": v(116.42, 51.3) * mm, "end": v(114.3, 52.18) * mm});
            skSolve(sketch);
        }
        {
            var Q0;
            Q0 = qSketchRegion(id + "F9", true);
            extrude(context, id + "F10", {"entities" : qUnion([Q0]), "operationType" : NewBodyOperationType.REMOVE, "oppositeDirection" : true, "depth" : 3.2 * mm, "offsetDistance" : 25 * mm});
        }
        {
            var Q0;
            Q0=makeQuery(id+"F4.boolean.opBoolean","COPY",FACE,{"derivedFrom":makeQuery(id+"F4.opExtrude","CAP_FACE",FACE,{"disambiguationData":[OSD([sQuery(id+"F0.wireOp",EDGE,"E4"),sQuery(id+"F0.wireOp",EDGE,"E5"),sQuery(id+"F0.wireOp",EDGE,"E6"),sQuery(id+"F0.wireOp",EDGE,"E7"),sQuery(id+"F0.wireOp",EDGE,"E8"),sQuery(id+"F0.wireOp",EDGE,"E9"),sQuery(id+"F0.wireOp",EDGE,"E10"),sQuery(id+"F0.wireOp",EDGE,"E11"),sQuery(id+"F0.wireOp",EDGE,"E12"),sQuery(id+"F0.wireOp",EDGE,"E13"),sQuery(id+"F0.wireOp",EDGE,"E14"),sQuery(id+"F0.wireOp",EDGE,"E15"),sQuery(id+"F0.wireOp",EDGE,"E16"),sQuery(id+"F0.wireOp",EDGE,"E17"),sQuery(id+"F0.wireOp",EDGE,"E18"),sQuery(id+"F0.wireOp",EDGE,"E19"),sQuery(id+"F0.wireOp",EDGE,"E20"),sQuery(id+"F0.wireOp",EDGE,"E21"),sQuery(id+"F0.wireOp",EDGE,"E22"),sQuery(id+"F0.wireOp",EDGE,"E23"),sQuery(id+"F0.wireOp",EDGE,"E24"),sQuery(id+"F0.wireOp",EDGE,"E25"),sQuery(id+"F0.wireOp",EDGE,"E26"),sQuery(id+"F0.wireOp",EDGE,"E27"),sQuery(id+"F0.wireOp",EDGE,"E28"),sQuery(id+"F0.wireOp",EDGE,"E29"),sQuery(id+"F0.wireOp",EDGE,"E30"),sQuery(id+"F0.wireOp",EDGE,"E31"),sQuery(id+"F0.wireOp",EDGE,"E32"),sQuery(id+"F0.wireOp",EDGE,"E33"),sQuery(id+"F0.wireOp",EDGE,"E34"),sQuery(id+"F0.wireOp",EDGE,"E35"),sQuery(id+"F0.wireOp",EDGE,"E36"),sQuery(id+"F0.wireOp",EDGE,"E37"),sQuery(id+"F0.wireOp",EDGE,"E38"),sQuery(id+"F0.wireOp",EDGE,"E39"),sQuery(id+"F0.wireOp",EDGE,"E40"),sQuery(id+"F0.wireOp",EDGE,"E41"),sQuery(id+"F0.wireOp",EDGE,"E42"),sQuery(id+"F0.wireOp",EDGE,"E43"),sQuery(id+"F0.wireOp",EDGE,"E44"),sQuery(id+"F0.wireOp",EDGE,"E45"),sQuery(id+"F0.wireOp",EDGE,"E46"),sQuery(id+"F0.wireOp",EDGE,"E47"),sQuery(id+"F0.wireOp",EDGE,"E48"),sQuery(id+"F0.wireOp",EDGE,"E49"),sQuery(id+"F0.wireOp",EDGE,"E50"),sQuery(id+"F0.wireOp",EDGE,"E51"),sQuery(id+"F0.wireOp",EDGE,"E52"),sQuery(id+"F0.wireOp",EDGE,"E53"),sQuery(id+"F0.wireOp",EDGE,"E54"),sQuery(id+"F0.wireOp",EDGE,"E55"),sQuery(id+"F0.wireOp",EDGE,"E56"),sQuery(id+"F0.wireOp",EDGE,"E57"),sQuery(id+"F0.wireOp",EDGE,"E58"),sQuery(id+"F0.wireOp",EDGE,"E59"),sQuery(id+"F0.wireOp",EDGE,"E60"),sQuery(id+"F0.wireOp",EDGE,"E61"),sQuery(id+"F0.wireOp",EDGE,"E62"),sQuery(id+"F0.wireOp",EDGE,"E63"),sQuery(id+"F0.wireOp",EDGE,"E64"),sQuery(id+"F0.wireOp",EDGE,"E65"),sQuery(id+"F0.wireOp",EDGE,"E66"),sQuery(id+"F0.wireOp",EDGE,"E67"),sQuery(id+"F0.wireOp",EDGE,"E68"),sQuery(id+"F0.wireOp",EDGE,"E69"),sQuery(id+"F0.wireOp",EDGE,"E70"),sQuery(id+"F0.wireOp",EDGE,"E71"),sQuery(id+"F0.wireOp",EDGE,"E72"),sQuery(id+"F0.wireOp",EDGE,"E73"),sQuery(id+"F0.wireOp",EDGE,"E74"),sQuery(id+"F0.wireOp",EDGE,"E75"),sQuery(id+"F0.wireOp",EDGE,"E76"),sQuery(id+"F0.wireOp",EDGE,"E77"),sQuery(id+"F0.wireOp",EDGE,"E78"),sQuery(id+"F0.wireOp",EDGE,"E79"),sQuery(id+"F0.wireOp",EDGE,"E80"),sQuery(id+"F0.wireOp",EDGE,"E81"),sQuery(id+"F0.wireOp",EDGE,"E82"),sQuery(id+"F0.wireOp",EDGE,"E83"),sQuery(id+"F0.wireOp",EDGE,"E84"),sQuery(id+"F0.wireOp",EDGE,"E85"),sQuery(id+"F0.wireOp",EDGE,"E86"),sQuery(id+"F0.wireOp",EDGE,"E87"),sQuery(id+"F0.wireOp",EDGE,"E88"),sQuery(id+"F0.wireOp",EDGE,"E89"),sQuery(id+"F0.wireOp",EDGE,"E90"),sQuery(id+"F0.wireOp",EDGE,"E91"),sQuery(id+"F0.wireOp",EDGE,"E92"),sQuery(id+"F0.wireOp",EDGE,"E93"),sQuery(id+"F0.wireOp",EDGE,"E94"),sQuery(id+"F0.wireOp",EDGE,"E95"),sQuery(id+"F0.wireOp",EDGE,"E96"),sQuery(id+"F0.wireOp",EDGE,"E97"),sQuery(id+"F0.wireOp",EDGE,"E98"),sQuery(id+"F0.wireOp",EDGE,"E99"),sQuery(id+"F0.wireOp",EDGE,"E100"),sQuery(id+"F0.wireOp",EDGE,"E101"),sQuery(id+"F0.wireOp",EDGE,"E102"),sQuery(id+"F0.wireOp",EDGE,"E103"),sQuery(id+"F0.wireOp",EDGE,"E104"),sQuery(id+"F0.wireOp",EDGE,"E105"),sQuery(id+"F0.wireOp",EDGE,"E106"),sQuery(id+"F0.wireOp",EDGE,"E107"),sQuery(id+"F0.wireOp",EDGE,"E108"),sQuery(id+"F0.wireOp",EDGE,"E109"),sQuery(id+"F0.wireOp",EDGE,"E110"),sQuery(id+"F0.wireOp",EDGE,"E111"),sQuery(id+"F0.wireOp",EDGE,"E112"),sQuery(id+"F0.wireOp",EDGE,"E113"),sQuery(id+"F0.wireOp",EDGE,"E114"),sQuery(id+"F0.wireOp",EDGE,"E115"),sQuery(id+"F0.wireOp",EDGE,"E116"),sQuery(id+"F0.wireOp",EDGE,"E117"),sQuery(id+"F0.wireOp",EDGE,"E118"),sQuery(id+"F0.wireOp",EDGE,"E119"),sQuery(id+"F0.wireOp",EDGE,"E120"),sQuery(id+"F0.wireOp",EDGE,"E121"),sQuery(id+"F0.wireOp",EDGE,"E122"),sQuery(id+"F0.wireOp",EDGE,"E123"),sQuery(id+"F0.wireOp",EDGE,"E124"),sQuery(id+"F0.wireOp",EDGE,"E125"),sQuery(id+"F0.wireOp",EDGE,"E126"),sQuery(id+"F0.wireOp",EDGE,"E127"),sQuery(id+"F0.wireOp",EDGE,"E128"),sQuery(id+"F0.wireOp",EDGE,"E129"),sQuery(id+"F0.wireOp",EDGE,"E130"),sQuery(id+"F0.wireOp",EDGE,"E131"),sQuery(id+"F0.wireOp",EDGE,"E132"),sQuery(id+"F0.wireOp",EDGE,"E133"),sQuery(id+"F0.wireOp",EDGE,"E134"),sQuery(id+"F0.wireOp",EDGE,"E135"),sQuery(id+"F0.wireOp",EDGE,"E136"),sQuery(id+"F0.wireOp",EDGE,"E137"),sQuery(id+"F0.wireOp",EDGE,"E138"),sQuery(id+"F0.wireOp",EDGE,"E139"),sQuery(id+"F0.wireOp",EDGE,"E140"),sQuery(id+"F0.wireOp",EDGE,"E141"),sQuery(id+"F0.wireOp",EDGE,"E142"),sQuery(id+"F0.wireOp",EDGE,"E143"),sQuery(id+"F0.wireOp",EDGE,"E144"),sQuery(id+"F0.wireOp",EDGE,"E145"),sQuery(id+"F0.wireOp",EDGE,"E146"),sQuery(id+"F0.wireOp",EDGE,"E147"),sQuery(id+"F0.wireOp",EDGE,"E148"),sQuery(id+"F0.wireOp",EDGE,"E149"),sQuery(id+"F0.wireOp",EDGE,"E150"),sQuery(id+"F0.wireOp",EDGE,"E151"),sQuery(id+"F0.wireOp",EDGE,"E152"),sQuery(id+"F0.wireOp",EDGE,"E153"),sQuery(id+"F0.wireOp",EDGE,"E154"),sQuery(id+"F0.wireOp",EDGE,"E155"),sQuery(id+"F0.wireOp",EDGE,"E156"),sQuery(id+"F0.wireOp",EDGE,"E157"),sQuery(id+"F0.wireOp",EDGE,"E158"),sQuery(id+"F0.wireOp",EDGE,"E159"),sQuery(id+"F0.wireOp",EDGE,"E160"),sQuery(id+"F0.wireOp",EDGE,"E161"),sQuery(id+"F0.wireOp",EDGE,"E162"),sQuery(id+"F0.wireOp",EDGE,"E163"),sQuery(id+"F0.wireOp",EDGE,"E164"),sQuery(id+"F0.wireOp",EDGE,"E165"),sQuery(id+"F0.wireOp",EDGE,"E166"),sQuery(id+"F0.wireOp",EDGE,"E167"),sQuery(id+"F0.wireOp",EDGE,"E168"),sQuery(id+"F0.wireOp",EDGE,"E169"),sQuery(id+"F0.wireOp",EDGE,"E170"),sQuery(id+"F0.wireOp",EDGE,"E171"),sQuery(id+"F0.wireOp",EDGE,"E172"),sQuery(id+"F0.wireOp",EDGE,"E173"),sQuery(id+"F0.wireOp",EDGE,"E174"),sQuery(id+"F0.wireOp",EDGE,"E175"),sQuery(id+"F0.wireOp",EDGE,"E176"),sQuery(id+"F0.wireOp",EDGE,"E177"),sQuery(id+"F0.wireOp",EDGE,"E178"),sQuery(id+"F0.wireOp",EDGE,"E179"),sQuery(id+"F0.wireOp",EDGE,"E180"),sQuery(id+"F0.wireOp",EDGE,"E181"),sQuery(id+"F0.wireOp",EDGE,"E182"),sQuery(id+"F0.wireOp",EDGE,"E183"),sQuery(id+"F0.wireOp",EDGE,"E184"),sQuery(id+"F0.wireOp",EDGE,"E185"),sQuery(id+"F0.wireOp",EDGE,"E186"),sQuery(id+"F0.wireOp",EDGE,"E187"),sQuery(id+"F0.wireOp",EDGE,"E188"),sQuery(id+"F0.wireOp",EDGE,"E189"),sQuery(id+"F0.wireOp",EDGE,"E190"),sQuery(id+"F0.wireOp",EDGE,"E191"),sQuery(id+"F0.wireOp",EDGE,"E192"),sQuery(id+"F0.wireOp",EDGE,"E193"),sQuery(id+"F0.wireOp",EDGE,"E194"),sQuery(id+"F0.wireOp",EDGE,"E195"),sQuery(id+"F0.wireOp",EDGE,"E196"),sQuery(id+"F0.wireOp",EDGE,"E197"),sQuery(id+"F0.wireOp",EDGE,"E198"),sQuery(id+"F0.wireOp",EDGE,"E199"),sQuery(id+"F0.wireOp",EDGE,"E200"),sQuery(id+"F0.wireOp",EDGE,"E201"),sQuery(id+"F0.wireOp",EDGE,"E202"),sQuery(id+"F0.wireOp",EDGE,"E203"),sQuery(id+"F0.wireOp",EDGE,"E204"),sQuery(id+"F0.wireOp",EDGE,"E205"),sQuery(id+"F0.wireOp",EDGE,"E206"),sQuery(id+"F0.wireOp",EDGE,"E207"),sQuery(id+"F0.wireOp",EDGE,"E208"),sQuery(id+"F0.wireOp",EDGE,"E209"),sQuery(id+"F0.wireOp",EDGE,"E210"),sQuery(id+"F0.wireOp",EDGE,"E211"),sQuery(id+"F0.wireOp",EDGE,"E212"),sQuery(id+"F0.wireOp",EDGE,"E213"),sQuery(id+"F0.wireOp",EDGE,"E214"),sQuery(id+"F0.wireOp",EDGE,"E215"),sQuery(id+"F0.wireOp",EDGE,"E216"),sQuery(id+"F0.wireOp",EDGE,"E217"),sQuery(id+"F0.wireOp",EDGE,"E218"),sQuery(id+"F0.wireOp",EDGE,"E219"),sQuery(id+"F0.wireOp",EDGE,"E220"),sQuery(id+"F0.wireOp",EDGE,"E221"),sQuery(id+"F0.wireOp",EDGE,"E222"),sQuery(id+"F0.wireOp",EDGE,"E223"),sQuery(id+"F0.wireOp",EDGE,"E224"),sQuery(id+"F0.wireOp",EDGE,"E225"),sQuery(id+"F0.wireOp",EDGE,"E226"),sQuery(id+"F0.wireOp",EDGE,"E227"),sQuery(id+"F0.wireOp",EDGE,"E228"),sQuery(id+"F0.wireOp",EDGE,"E229"),sQuery(id+"F0.wireOp",EDGE,"E230"),sQuery(id+"F0.wireOp",EDGE,"E231"),sQuery(id+"F0.wireOp",EDGE,"E232"),sQuery(id+"F0.wireOp",EDGE,"E233"),sQuery(id+"F0.wireOp",EDGE,"E234"),sQuery(id+"F0.wireOp",EDGE,"E235"),sQuery(id+"F0.wireOp",EDGE,"E236"),sQuery(id+"F0.wireOp",EDGE,"E237"),sQuery(id+"F0.wireOp",EDGE,"E238"),sQuery(id+"F0.wireOp",EDGE,"E239"),sQuery(id+"F0.wireOp",EDGE,"E240"),sQuery(id+"F0.wireOp",EDGE,"E241"),sQuery(id+"F0.wireOp",EDGE,"E242"),sQuery(id+"F0.wireOp",EDGE,"E243"),sQuery(id+"F3.wireOp",EDGE,"E244.bottom"),sQuery(id+"F3.wireOp",EDGE,"E244.top"),sQuery(id+"F3.wireOp",EDGE,"E244.left"),sQuery(id+"F3.wireOp",EDGE,"E244.right"),sQuery(id+"F3.wireOp",EDGE,"E245.filletArc"),sQuery(id+"F3.wireOp",EDGE,"E246.filletArc"),sQuery(id+"F3.wireOp",EDGE,"E247.filletArc"),sQuery(id+"F3.wireOp",EDGE,"E248.filletArc")])],"isStart":false})});
            var sketch = newSketch(context, id + "F11", { "sketchPlane" : qUnion([Q0])});
            skCircle(sketch, "E257", {"center": v(95.25, -27.03) * mm, "radius": 3.57 * mm});
            skPoint(sketch, "E257.first.point", {"position": v(97.77, -29.55) * mm});
            skPoint(sketch, "E257.second.point", {"position": v(92.72, -29.55) * mm});
            skPoint(sketch, "E257.third.point", {"position": v(92.72, -24.5) * mm});
            skCircle(sketch, "E258", {"center": v(95.25, 30.12) * mm, "radius": 3.57 * mm});
            skPoint(sketch, "E258.first.point", {"position": v(97.77, 27.6) * mm});
            skPoint(sketch, "E258.second.point", {"position": v(92.72, 27.6) * mm});
            skPoint(sketch, "E258.third.point", {"position": v(92.72, 32.65) * mm});
            skCircle(sketch, "E259", {"center": v(38.1, -27.03) * mm, "radius": 3.57 * mm});
            skPoint(sketch, "E259.first.point", {"position": v(40.62, -29.55) * mm});
            skPoint(sketch, "E259.second.point", {"position": v(35.57, -29.55) * mm});
            skPoint(sketch, "E259.third.point", {"position": v(35.57, -24.5) * mm});
            skCircle(sketch, "E260", {"center": v(38.1, 30.12) * mm, "radius": 3.57 * mm});
            skPoint(sketch, "E260.first.point", {"position": v(40.62, 27.6) * mm});
            skPoint(sketch, "E260.second.point", {"position": v(35.57, 27.6) * mm});
            skPoint(sketch, "E260.third.point", {"position": v(35.57, 32.65) * mm});
            skCircle(sketch, "E261", {"center": v(0, -7.98) * mm, "radius": 3.57 * mm});
            skPoint(sketch, "E261.first.point", {"position": v(2.52, -10.5) * mm});
            skPoint(sketch, "E261.second.point", {"position": v(-2.53, -10.5) * mm});
            skPoint(sketch, "E261.third.point", {"position": v(-2.53, -5.45) * mm});
            skCircle(sketch, "E262", {"center": v(0, 11.07) * mm, "radius": 3.57 * mm});
            skPoint(sketch, "E262.first.point", {"position": v(2.52, 8.55) * mm});
            skPoint(sketch, "E262.second.point", {"position": v(-2.53, 8.55) * mm});
            skPoint(sketch, "E262.third.point", {"position": v(-2.53, 13.6) * mm});
            skCircle(sketch, "E263", {"center": v(-38.1, -27.03) * mm, "radius": 3.57 * mm});
            skPoint(sketch, "E263.first.point", {"position": v(-35.58, -29.55) * mm});
            skPoint(sketch, "E263.second.point", {"position": v(-40.63, -29.55) * mm});
            skPoint(sketch, "E263.third.point", {"position": v(-40.63, -24.5) * mm});
            skCircle(sketch, "E264", {"center": v(-38.1, 30.12) * mm, "radius": 3.57 * mm});
            skPoint(sketch, "E264.first.point", {"position": v(-35.58, 27.6) * mm});
            skPoint(sketch, "E264.second.point", {"position": v(-40.63, 27.6) * mm});
            skPoint(sketch, "E264.third.point", {"position": v(-40.63, 32.65) * mm});
            skCircle(sketch, "E265", {"center": v(-95.25, -27.03) * mm, "radius": 3.57 * mm});
            skPoint(sketch, "E265.first.point", {"position": v(-92.73, -29.55) * mm});
            skPoint(sketch, "E265.second.point", {"position": v(-97.78, -29.55) * mm});
            skPoint(sketch, "E265.third.point", {"position": v(-97.78, -24.5) * mm});
            skCircle(sketch, "E266", {"center": v(-95.25, 30.12) * mm, "radius": 3.57 * mm});
            skPoint(sketch, "E266.first.point", {"position": v(-92.73, 27.6) * mm});
            skPoint(sketch, "E266.second.point", {"position": v(-97.78, 27.6) * mm});
            skPoint(sketch, "E266.third.point", {"position": v(-97.78, 32.65) * mm});
            skCircle(sketch, "E267", {"center": v(95.25, -27.03) * mm, "radius": 0.75 * mm});
            skCircle(sketch, "E268", {"center": v(95.25, 30.12) * mm, "radius": 0.75 * mm});
            skCircle(sketch, "E269", {"center": v(38.1, -27.03) * mm, "radius": 0.75 * mm});
            skCircle(sketch, "E270", {"center": v(38.1, 30.12) * mm, "radius": 0.75 * mm});
            skCircle(sketch, "E271", {"center": v(0, -7.98) * mm, "radius": 0.75 * mm});
            skCircle(sketch, "E272", {"center": v(0, 11.07) * mm, "radius": 0.75 * mm});
            skCircle(sketch, "E273", {"center": v(-38.1, 30.12) * mm, "radius": 0.75 * mm});
            skCircle(sketch, "E274", {"center": v(-38.1, -27.03) * mm, "radius": 0.75 * mm});
            skCircle(sketch, "E275", {"center": v(-95.25, -27.03) * mm, "radius": 0.75 * mm});
            skCircle(sketch, "E276", {"center": v(-95.25, 30.12) * mm, "radius": 0.75 * mm});
            skSolve(sketch);
        }
        {
            var Q0;
            Q0 = qSketchRegion(id + "F11", true);
            extrude(context, id + "F12", {"entities" : qUnion([Q0]), "operationType" : NewBodyOperationType.ADD, "depth" : 6.8 * mm, "offsetDistance" : 25 * mm});
        }
        {
            var Q0;
            Q0=makeQuery(id+"F12.boolean.opBoolean","SPLIT",FACE,{"disambiguationData":[TD([makeQuery(id+"F12.opExtrude","SWEPT_FACE",FACE,{"disambiguationData":[OSD([sQuery(id+"F11.wireOp",EDGE,"E267")])]})])],"derivedFrom":makeQuery(id+"F8.boolean.opBoolean","MERGE",FACE,{"derivedFrom":[makeQuery(id+"F4.boolean.opBoolean","COPY",FACE,{"derivedFrom":makeQuery(id+"F4.opExtrude","CAP_FACE",FACE,{"disambiguationData":[OSD([sQuery(id+"F0.wireOp",EDGE,"E4"),sQuery(id+"F0.wireOp",EDGE,"E5"),sQuery(id+"F0.wireOp",EDGE,"E6"),sQuery(id+"F0.wireOp",EDGE,"E7"),sQuery(id+"F0.wireOp",EDGE,"E8"),sQuery(id+"F0.wireOp",EDGE,"E9"),sQuery(id+"F0.wireOp",EDGE,"E10"),sQuery(id+"F0.wireOp",EDGE,"E11"),sQuery(id+"F0.wireOp",EDGE,"E12"),sQuery(id+"F0.wireOp",EDGE,"E13"),sQuery(id+"F0.wireOp",EDGE,"E14"),sQuery(id+"F0.wireOp",EDGE,"E15"),sQuery(id+"F0.wireOp",EDGE,"E16"),sQuery(id+"F0.wireOp",EDGE,"E17"),sQuery(id+"F0.wireOp",EDGE,"E18"),sQuery(id+"F0.wireOp",EDGE,"E19"),sQuery(id+"F0.wireOp",EDGE,"E20"),sQuery(id+"F0.wireOp",EDGE,"E21"),sQuery(id+"F0.wireOp",EDGE,"E22"),sQuery(id+"F0.wireOp",EDGE,"E23"),sQuery(id+"F0.wireOp",EDGE,"E24"),sQuery(id+"F0.wireOp",EDGE,"E25"),sQuery(id+"F0.wireOp",EDGE,"E26"),sQuery(id+"F0.wireOp",EDGE,"E27"),sQuery(id+"F0.wireOp",EDGE,"E28"),sQuery(id+"F0.wireOp",EDGE,"E29"),sQuery(id+"F0.wireOp",EDGE,"E30"),sQuery(id+"F0.wireOp",EDGE,"E31"),sQuery(id+"F0.wireOp",EDGE,"E32"),sQuery(id+"F0.wireOp",EDGE,"E33"),sQuery(id+"F0.wireOp",EDGE,"E34"),sQuery(id+"F0.wireOp",EDGE,"E35"),sQuery(id+"F0.wireOp",EDGE,"E36"),sQuery(id+"F0.wireOp",EDGE,"E37"),sQuery(id+"F0.wireOp",EDGE,"E38"),sQuery(id+"F0.wireOp",EDGE,"E39"),sQuery(id+"F0.wireOp",EDGE,"E40"),sQuery(id+"F0.wireOp",EDGE,"E41"),sQuery(id+"F0.wireOp",EDGE,"E42"),sQuery(id+"F0.wireOp",EDGE,"E43"),sQuery(id+"F0.wireOp",EDGE,"E44"),sQuery(id+"F0.wireOp",EDGE,"E45"),sQuery(id+"F0.wireOp",EDGE,"E46"),sQuery(id+"F0.wireOp",EDGE,"E47"),sQuery(id+"F0.wireOp",EDGE,"E48"),sQuery(id+"F0.wireOp",EDGE,"E49"),sQuery(id+"F0.wireOp",EDGE,"E50"),sQuery(id+"F0.wireOp",EDGE,"E51"),sQuery(id+"F0.wireOp",EDGE,"E52"),sQuery(id+"F0.wireOp",EDGE,"E53"),sQuery(id+"F0.wireOp",EDGE,"E54"),sQuery(id+"F0.wireOp",EDGE,"E55"),sQuery(id+"F0.wireOp",EDGE,"E56"),sQuery(id+"F0.wireOp",EDGE,"E57"),sQuery(id+"F0.wireOp",EDGE,"E58"),sQuery(id+"F0.wireOp",EDGE,"E59"),sQuery(id+"F0.wireOp",EDGE,"E60"),sQuery(id+"F0.wireOp",EDGE,"E61"),sQuery(id+"F0.wireOp",EDGE,"E62"),sQuery(id+"F0.wireOp",EDGE,"E63"),sQuery(id+"F0.wireOp",EDGE,"E64"),sQuery(id+"F0.wireOp",EDGE,"E65"),sQuery(id+"F0.wireOp",EDGE,"E66"),sQuery(id+"F0.wireOp",EDGE,"E67"),sQuery(id+"F0.wireOp",EDGE,"E68"),sQuery(id+"F0.wireOp",EDGE,"E69"),sQuery(id+"F0.wireOp",EDGE,"E70"),sQuery(id+"F0.wireOp",EDGE,"E71"),sQuery(id+"F0.wireOp",EDGE,"E72"),sQuery(id+"F0.wireOp",EDGE,"E73"),sQuery(id+"F0.wireOp",EDGE,"E74"),sQuery(id+"F0.wireOp",EDGE,"E75"),sQuery(id+"F0.wireOp",EDGE,"E76"),sQuery(id+"F0.wireOp",EDGE,"E77"),sQuery(id+"F0.wireOp",EDGE,"E78"),sQuery(id+"F0.wireOp",EDGE,"E79"),sQuery(id+"F0.wireOp",EDGE,"E80"),sQuery(id+"F0.wireOp",EDGE,"E81"),sQuery(id+"F0.wireOp",EDGE,"E82"),sQuery(id+"F0.wireOp",EDGE,"E83"),sQuery(id+"F0.wireOp",EDGE,"E84"),sQuery(id+"F0.wireOp",EDGE,"E85"),sQuery(id+"F0.wireOp",EDGE,"E86"),sQuery(id+"F0.wireOp",EDGE,"E87"),sQuery(id+"F0.wireOp",EDGE,"E88"),sQuery(id+"F0.wireOp",EDGE,"E89"),sQuery(id+"F0.wireOp",EDGE,"E90"),sQuery(id+"F0.wireOp",EDGE,"E91"),sQuery(id+"F0.wireOp",EDGE,"E92"),sQuery(id+"F0.wireOp",EDGE,"E93"),sQuery(id+"F0.wireOp",EDGE,"E94"),sQuery(id+"F0.wireOp",EDGE,"E95"),sQuery(id+"F0.wireOp",EDGE,"E96"),sQuery(id+"F0.wireOp",EDGE,"E97"),sQuery(id+"F0.wireOp",EDGE,"E98"),sQuery(id+"F0.wireOp",EDGE,"E99"),sQuery(id+"F0.wireOp",EDGE,"E100"),sQuery(id+"F0.wireOp",EDGE,"E101"),sQuery(id+"F0.wireOp",EDGE,"E102"),sQuery(id+"F0.wireOp",EDGE,"E103"),sQuery(id+"F0.wireOp",EDGE,"E104"),sQuery(id+"F0.wireOp",EDGE,"E105"),sQuery(id+"F0.wireOp",EDGE,"E106"),sQuery(id+"F0.wireOp",EDGE,"E107"),sQuery(id+"F0.wireOp",EDGE,"E108"),sQuery(id+"F0.wireOp",EDGE,"E109"),sQuery(id+"F0.wireOp",EDGE,"E110"),sQuery(id+"F0.wireOp",EDGE,"E111"),sQuery(id+"F0.wireOp",EDGE,"E112"),sQuery(id+"F0.wireOp",EDGE,"E113"),sQuery(id+"F0.wireOp",EDGE,"E114"),sQuery(id+"F0.wireOp",EDGE,"E115"),sQuery(id+"F0.wireOp",EDGE,"E116"),sQuery(id+"F0.wireOp",EDGE,"E117"),sQuery(id+"F0.wireOp",EDGE,"E118"),sQuery(id+"F0.wireOp",EDGE,"E119"),sQuery(id+"F0.wireOp",EDGE,"E120"),sQuery(id+"F0.wireOp",EDGE,"E121"),sQuery(id+"F0.wireOp",EDGE,"E122"),sQuery(id+"F0.wireOp",EDGE,"E123"),sQuery(id+"F0.wireOp",EDGE,"E124"),sQuery(id+"F0.wireOp",EDGE,"E125"),sQuery(id+"F0.wireOp",EDGE,"E126"),sQuery(id+"F0.wireOp",EDGE,"E127"),sQuery(id+"F0.wireOp",EDGE,"E128"),sQuery(id+"F0.wireOp",EDGE,"E129"),sQuery(id+"F0.wireOp",EDGE,"E130"),sQuery(id+"F0.wireOp",EDGE,"E131"),sQuery(id+"F0.wireOp",EDGE,"E132"),sQuery(id+"F0.wireOp",EDGE,"E133"),sQuery(id+"F0.wireOp",EDGE,"E134"),sQuery(id+"F0.wireOp",EDGE,"E135"),sQuery(id+"F0.wireOp",EDGE,"E136"),sQuery(id+"F0.wireOp",EDGE,"E137"),sQuery(id+"F0.wireOp",EDGE,"E138"),sQuery(id+"F0.wireOp",EDGE,"E139"),sQuery(id+"F0.wireOp",EDGE,"E140"),sQuery(id+"F0.wireOp",EDGE,"E141"),sQuery(id+"F0.wireOp",EDGE,"E142"),sQuery(id+"F0.wireOp",EDGE,"E143"),sQuery(id+"F0.wireOp",EDGE,"E144"),sQuery(id+"F0.wireOp",EDGE,"E145"),sQuery(id+"F0.wireOp",EDGE,"E146"),sQuery(id+"F0.wireOp",EDGE,"E147"),sQuery(id+"F0.wireOp",EDGE,"E148"),sQuery(id+"F0.wireOp",EDGE,"E149"),sQuery(id+"F0.wireOp",EDGE,"E150"),sQuery(id+"F0.wireOp",EDGE,"E151"),sQuery(id+"F0.wireOp",EDGE,"E152"),sQuery(id+"F0.wireOp",EDGE,"E153"),sQuery(id+"F0.wireOp",EDGE,"E154"),sQuery(id+"F0.wireOp",EDGE,"E155"),sQuery(id+"F0.wireOp",EDGE,"E156"),sQuery(id+"F0.wireOp",EDGE,"E157"),sQuery(id+"F0.wireOp",EDGE,"E158"),sQuery(id+"F0.wireOp",EDGE,"E159"),sQuery(id+"F0.wireOp",EDGE,"E160"),sQuery(id+"F0.wireOp",EDGE,"E161"),sQuery(id+"F0.wireOp",EDGE,"E162"),sQuery(id+"F0.wireOp",EDGE,"E163"),sQuery(id+"F0.wireOp",EDGE,"E164"),sQuery(id+"F0.wireOp",EDGE,"E165"),sQuery(id+"F0.wireOp",EDGE,"E166"),sQuery(id+"F0.wireOp",EDGE,"E167"),sQuery(id+"F0.wireOp",EDGE,"E168"),sQuery(id+"F0.wireOp",EDGE,"E169"),sQuery(id+"F0.wireOp",EDGE,"E170"),sQuery(id+"F0.wireOp",EDGE,"E171"),sQuery(id+"F0.wireOp",EDGE,"E172"),sQuery(id+"F0.wireOp",EDGE,"E173"),sQuery(id+"F0.wireOp",EDGE,"E174"),sQuery(id+"F0.wireOp",EDGE,"E175"),sQuery(id+"F0.wireOp",EDGE,"E176"),sQuery(id+"F0.wireOp",EDGE,"E177"),sQuery(id+"F0.wireOp",EDGE,"E178"),sQuery(id+"F0.wireOp",EDGE,"E179"),sQuery(id+"F0.wireOp",EDGE,"E180"),sQuery(id+"F0.wireOp",EDGE,"E181"),sQuery(id+"F0.wireOp",EDGE,"E182"),sQuery(id+"F0.wireOp",EDGE,"E183"),sQuery(id+"F0.wireOp",EDGE,"E184"),sQuery(id+"F0.wireOp",EDGE,"E185"),sQuery(id+"F0.wireOp",EDGE,"E186"),sQuery(id+"F0.wireOp",EDGE,"E187"),sQuery(id+"F0.wireOp",EDGE,"E188"),sQuery(id+"F0.wireOp",EDGE,"E189"),sQuery(id+"F0.wireOp",EDGE,"E190"),sQuery(id+"F0.wireOp",EDGE,"E191"),sQuery(id+"F0.wireOp",EDGE,"E192"),sQuery(id+"F0.wireOp",EDGE,"E193"),sQuery(id+"F0.wireOp",EDGE,"E194"),sQuery(id+"F0.wireOp",EDGE,"E195"),sQuery(id+"F0.wireOp",EDGE,"E196"),sQuery(id+"F0.wireOp",EDGE,"E197"),sQuery(id+"F0.wireOp",EDGE,"E198"),sQuery(id+"F0.wireOp",EDGE,"E199"),sQuery(id+"F0.wireOp",EDGE,"E200"),sQuery(id+"F0.wireOp",EDGE,"E201"),sQuery(id+"F0.wireOp",EDGE,"E202"),sQuery(id+"F0.wireOp",EDGE,"E203"),sQuery(id+"F0.wireOp",EDGE,"E204"),sQuery(id+"F0.wireOp",EDGE,"E205"),sQuery(id+"F0.wireOp",EDGE,"E206"),sQuery(id+"F0.wireOp",EDGE,"E207"),sQuery(id+"F0.wireOp",EDGE,"E208"),sQuery(id+"F0.wireOp",EDGE,"E209"),sQuery(id+"F0.wireOp",EDGE,"E210"),sQuery(id+"F0.wireOp",EDGE,"E211"),sQuery(id+"F0.wireOp",EDGE,"E212"),sQuery(id+"F0.wireOp",EDGE,"E213"),sQuery(id+"F0.wireOp",EDGE,"E214"),sQuery(id+"F0.wireOp",EDGE,"E215"),sQuery(id+"F0.wireOp",EDGE,"E216"),sQuery(id+"F0.wireOp",EDGE,"E217"),sQuery(id+"F0.wireOp",EDGE,"E218"),sQuery(id+"F0.wireOp",EDGE,"E219"),sQuery(id+"F0.wireOp",EDGE,"E220"),sQuery(id+"F0.wireOp",EDGE,"E221"),sQuery(id+"F0.wireOp",EDGE,"E222"),sQuery(id+"F0.wireOp",EDGE,"E223"),sQuery(id+"F0.wireOp",EDGE,"E224"),sQuery(id+"F0.wireOp",EDGE,"E225"),sQuery(id+"F0.wireOp",EDGE,"E226"),sQuery(id+"F0.wireOp",EDGE,"E227"),sQuery(id+"F0.wireOp",EDGE,"E228"),sQuery(id+"F0.wireOp",EDGE,"E229"),sQuery(id+"F0.wireOp",EDGE,"E230"),sQuery(id+"F0.wireOp",EDGE,"E231"),sQuery(id+"F0.wireOp",EDGE,"E232"),sQuery(id+"F0.wireOp",EDGE,"E233"),sQuery(id+"F0.wireOp",EDGE,"E234"),sQuery(id+"F0.wireOp",EDGE,"E235"),sQuery(id+"F0.wireOp",EDGE,"E236"),sQuery(id+"F0.wireOp",EDGE,"E237"),sQuery(id+"F0.wireOp",EDGE,"E238"),sQuery(id+"F0.wireOp",EDGE,"E239"),sQuery(id+"F0.wireOp",EDGE,"E240"),sQuery(id+"F0.wireOp",EDGE,"E241"),sQuery(id+"F0.wireOp",EDGE,"E242"),sQuery(id+"F0.wireOp",EDGE,"E243"),sQuery(id+"F3.wireOp",EDGE,"E244.bottom"),sQuery(id+"F3.wireOp",EDGE,"E244.top"),sQuery(id+"F3.wireOp",EDGE,"E244.left"),sQuery(id+"F3.wireOp",EDGE,"E244.right"),sQuery(id+"F3.wireOp",EDGE,"E245.filletArc"),sQuery(id+"F3.wireOp",EDGE,"E246.filletArc"),sQuery(id+"F3.wireOp",EDGE,"E247.filletArc"),sQuery(id+"F3.wireOp",EDGE,"E248.filletArc")])],"isStart":false})}),makeQuery(id+"F8.opExtrude","CAP_FACE",FACE,{"disambiguationData":[OSD([sQuery(id+"F7.wireOp",EDGE,"E250.bottom"),sQuery(id+"F7.wireOp",EDGE,"E250.top"),sQuery(id+"F7.wireOp",EDGE,"E250.left"),sQuery(id+"F7.wireOp",EDGE,"E250.right")])],"isStart":false})]})});
            var Q1;
            Q1=makeQuery(id+"F12.boolean.opBoolean","SPLIT",FACE,{"disambiguationData":[TD([makeQuery(id+"F12.opExtrude","SWEPT_FACE",FACE,{"disambiguationData":[OSD([sQuery(id+"F11.wireOp",EDGE,"E268")])]})])],"derivedFrom":makeQuery(id+"F8.boolean.opBoolean","MERGE",FACE,{"derivedFrom":[makeQuery(id+"F4.boolean.opBoolean","COPY",FACE,{"derivedFrom":makeQuery(id+"F4.opExtrude","CAP_FACE",FACE,{"disambiguationData":[OSD([sQuery(id+"F0.wireOp",EDGE,"E4"),sQuery(id+"F0.wireOp",EDGE,"E5"),sQuery(id+"F0.wireOp",EDGE,"E6"),sQuery(id+"F0.wireOp",EDGE,"E7"),sQuery(id+"F0.wireOp",EDGE,"E8"),sQuery(id+"F0.wireOp",EDGE,"E9"),sQuery(id+"F0.wireOp",EDGE,"E10"),sQuery(id+"F0.wireOp",EDGE,"E11"),sQuery(id+"F0.wireOp",EDGE,"E12"),sQuery(id+"F0.wireOp",EDGE,"E13"),sQuery(id+"F0.wireOp",EDGE,"E14"),sQuery(id+"F0.wireOp",EDGE,"E15"),sQuery(id+"F0.wireOp",EDGE,"E16"),sQuery(id+"F0.wireOp",EDGE,"E17"),sQuery(id+"F0.wireOp",EDGE,"E18"),sQuery(id+"F0.wireOp",EDGE,"E19"),sQuery(id+"F0.wireOp",EDGE,"E20"),sQuery(id+"F0.wireOp",EDGE,"E21"),sQuery(id+"F0.wireOp",EDGE,"E22"),sQuery(id+"F0.wireOp",EDGE,"E23"),sQuery(id+"F0.wireOp",EDGE,"E24"),sQuery(id+"F0.wireOp",EDGE,"E25"),sQuery(id+"F0.wireOp",EDGE,"E26"),sQuery(id+"F0.wireOp",EDGE,"E27"),sQuery(id+"F0.wireOp",EDGE,"E28"),sQuery(id+"F0.wireOp",EDGE,"E29"),sQuery(id+"F0.wireOp",EDGE,"E30"),sQuery(id+"F0.wireOp",EDGE,"E31"),sQuery(id+"F0.wireOp",EDGE,"E32"),sQuery(id+"F0.wireOp",EDGE,"E33"),sQuery(id+"F0.wireOp",EDGE,"E34"),sQuery(id+"F0.wireOp",EDGE,"E35"),sQuery(id+"F0.wireOp",EDGE,"E36"),sQuery(id+"F0.wireOp",EDGE,"E37"),sQuery(id+"F0.wireOp",EDGE,"E38"),sQuery(id+"F0.wireOp",EDGE,"E39"),sQuery(id+"F0.wireOp",EDGE,"E40"),sQuery(id+"F0.wireOp",EDGE,"E41"),sQuery(id+"F0.wireOp",EDGE,"E42"),sQuery(id+"F0.wireOp",EDGE,"E43"),sQuery(id+"F0.wireOp",EDGE,"E44"),sQuery(id+"F0.wireOp",EDGE,"E45"),sQuery(id+"F0.wireOp",EDGE,"E46"),sQuery(id+"F0.wireOp",EDGE,"E47"),sQuery(id+"F0.wireOp",EDGE,"E48"),sQuery(id+"F0.wireOp",EDGE,"E49"),sQuery(id+"F0.wireOp",EDGE,"E50"),sQuery(id+"F0.wireOp",EDGE,"E51"),sQuery(id+"F0.wireOp",EDGE,"E52"),sQuery(id+"F0.wireOp",EDGE,"E53"),sQuery(id+"F0.wireOp",EDGE,"E54"),sQuery(id+"F0.wireOp",EDGE,"E55"),sQuery(id+"F0.wireOp",EDGE,"E56"),sQuery(id+"F0.wireOp",EDGE,"E57"),sQuery(id+"F0.wireOp",EDGE,"E58"),sQuery(id+"F0.wireOp",EDGE,"E59"),sQuery(id+"F0.wireOp",EDGE,"E60"),sQuery(id+"F0.wireOp",EDGE,"E61"),sQuery(id+"F0.wireOp",EDGE,"E62"),sQuery(id+"F0.wireOp",EDGE,"E63"),sQuery(id+"F0.wireOp",EDGE,"E64"),sQuery(id+"F0.wireOp",EDGE,"E65"),sQuery(id+"F0.wireOp",EDGE,"E66"),sQuery(id+"F0.wireOp",EDGE,"E67"),sQuery(id+"F0.wireOp",EDGE,"E68"),sQuery(id+"F0.wireOp",EDGE,"E69"),sQuery(id+"F0.wireOp",EDGE,"E70"),sQuery(id+"F0.wireOp",EDGE,"E71"),sQuery(id+"F0.wireOp",EDGE,"E72"),sQuery(id+"F0.wireOp",EDGE,"E73"),sQuery(id+"F0.wireOp",EDGE,"E74"),sQuery(id+"F0.wireOp",EDGE,"E75"),sQuery(id+"F0.wireOp",EDGE,"E76"),sQuery(id+"F0.wireOp",EDGE,"E77"),sQuery(id+"F0.wireOp",EDGE,"E78"),sQuery(id+"F0.wireOp",EDGE,"E79"),sQuery(id+"F0.wireOp",EDGE,"E80"),sQuery(id+"F0.wireOp",EDGE,"E81"),sQuery(id+"F0.wireOp",EDGE,"E82"),sQuery(id+"F0.wireOp",EDGE,"E83"),sQuery(id+"F0.wireOp",EDGE,"E84"),sQuery(id+"F0.wireOp",EDGE,"E85"),sQuery(id+"F0.wireOp",EDGE,"E86"),sQuery(id+"F0.wireOp",EDGE,"E87"),sQuery(id+"F0.wireOp",EDGE,"E88"),sQuery(id+"F0.wireOp",EDGE,"E89"),sQuery(id+"F0.wireOp",EDGE,"E90"),sQuery(id+"F0.wireOp",EDGE,"E91"),sQuery(id+"F0.wireOp",EDGE,"E92"),sQuery(id+"F0.wireOp",EDGE,"E93"),sQuery(id+"F0.wireOp",EDGE,"E94"),sQuery(id+"F0.wireOp",EDGE,"E95"),sQuery(id+"F0.wireOp",EDGE,"E96"),sQuery(id+"F0.wireOp",EDGE,"E97"),sQuery(id+"F0.wireOp",EDGE,"E98"),sQuery(id+"F0.wireOp",EDGE,"E99"),sQuery(id+"F0.wireOp",EDGE,"E100"),sQuery(id+"F0.wireOp",EDGE,"E101"),sQuery(id+"F0.wireOp",EDGE,"E102"),sQuery(id+"F0.wireOp",EDGE,"E103"),sQuery(id+"F0.wireOp",EDGE,"E104"),sQuery(id+"F0.wireOp",EDGE,"E105"),sQuery(id+"F0.wireOp",EDGE,"E106"),sQuery(id+"F0.wireOp",EDGE,"E107"),sQuery(id+"F0.wireOp",EDGE,"E108"),sQuery(id+"F0.wireOp",EDGE,"E109"),sQuery(id+"F0.wireOp",EDGE,"E110"),sQuery(id+"F0.wireOp",EDGE,"E111"),sQuery(id+"F0.wireOp",EDGE,"E112"),sQuery(id+"F0.wireOp",EDGE,"E113"),sQuery(id+"F0.wireOp",EDGE,"E114"),sQuery(id+"F0.wireOp",EDGE,"E115"),sQuery(id+"F0.wireOp",EDGE,"E116"),sQuery(id+"F0.wireOp",EDGE,"E117"),sQuery(id+"F0.wireOp",EDGE,"E118"),sQuery(id+"F0.wireOp",EDGE,"E119"),sQuery(id+"F0.wireOp",EDGE,"E120"),sQuery(id+"F0.wireOp",EDGE,"E121"),sQuery(id+"F0.wireOp",EDGE,"E122"),sQuery(id+"F0.wireOp",EDGE,"E123"),sQuery(id+"F0.wireOp",EDGE,"E124"),sQuery(id+"F0.wireOp",EDGE,"E125"),sQuery(id+"F0.wireOp",EDGE,"E126"),sQuery(id+"F0.wireOp",EDGE,"E127"),sQuery(id+"F0.wireOp",EDGE,"E128"),sQuery(id+"F0.wireOp",EDGE,"E129"),sQuery(id+"F0.wireOp",EDGE,"E130"),sQuery(id+"F0.wireOp",EDGE,"E131"),sQuery(id+"F0.wireOp",EDGE,"E132"),sQuery(id+"F0.wireOp",EDGE,"E133"),sQuery(id+"F0.wireOp",EDGE,"E134"),sQuery(id+"F0.wireOp",EDGE,"E135"),sQuery(id+"F0.wireOp",EDGE,"E136"),sQuery(id+"F0.wireOp",EDGE,"E137"),sQuery(id+"F0.wireOp",EDGE,"E138"),sQuery(id+"F0.wireOp",EDGE,"E139"),sQuery(id+"F0.wireOp",EDGE,"E140"),sQuery(id+"F0.wireOp",EDGE,"E141"),sQuery(id+"F0.wireOp",EDGE,"E142"),sQuery(id+"F0.wireOp",EDGE,"E143"),sQuery(id+"F0.wireOp",EDGE,"E144"),sQuery(id+"F0.wireOp",EDGE,"E145"),sQuery(id+"F0.wireOp",EDGE,"E146"),sQuery(id+"F0.wireOp",EDGE,"E147"),sQuery(id+"F0.wireOp",EDGE,"E148"),sQuery(id+"F0.wireOp",EDGE,"E149"),sQuery(id+"F0.wireOp",EDGE,"E150"),sQuery(id+"F0.wireOp",EDGE,"E151"),sQuery(id+"F0.wireOp",EDGE,"E152"),sQuery(id+"F0.wireOp",EDGE,"E153"),sQuery(id+"F0.wireOp",EDGE,"E154"),sQuery(id+"F0.wireOp",EDGE,"E155"),sQuery(id+"F0.wireOp",EDGE,"E156"),sQuery(id+"F0.wireOp",EDGE,"E157"),sQuery(id+"F0.wireOp",EDGE,"E158"),sQuery(id+"F0.wireOp",EDGE,"E159"),sQuery(id+"F0.wireOp",EDGE,"E160"),sQuery(id+"F0.wireOp",EDGE,"E161"),sQuery(id+"F0.wireOp",EDGE,"E162"),sQuery(id+"F0.wireOp",EDGE,"E163"),sQuery(id+"F0.wireOp",EDGE,"E164"),sQuery(id+"F0.wireOp",EDGE,"E165"),sQuery(id+"F0.wireOp",EDGE,"E166"),sQuery(id+"F0.wireOp",EDGE,"E167"),sQuery(id+"F0.wireOp",EDGE,"E168"),sQuery(id+"F0.wireOp",EDGE,"E169"),sQuery(id+"F0.wireOp",EDGE,"E170"),sQuery(id+"F0.wireOp",EDGE,"E171"),sQuery(id+"F0.wireOp",EDGE,"E172"),sQuery(id+"F0.wireOp",EDGE,"E173"),sQuery(id+"F0.wireOp",EDGE,"E174"),sQuery(id+"F0.wireOp",EDGE,"E175"),sQuery(id+"F0.wireOp",EDGE,"E176"),sQuery(id+"F0.wireOp",EDGE,"E177"),sQuery(id+"F0.wireOp",EDGE,"E178"),sQuery(id+"F0.wireOp",EDGE,"E179"),sQuery(id+"F0.wireOp",EDGE,"E180"),sQuery(id+"F0.wireOp",EDGE,"E181"),sQuery(id+"F0.wireOp",EDGE,"E182"),sQuery(id+"F0.wireOp",EDGE,"E183"),sQuery(id+"F0.wireOp",EDGE,"E184"),sQuery(id+"F0.wireOp",EDGE,"E185"),sQuery(id+"F0.wireOp",EDGE,"E186"),sQuery(id+"F0.wireOp",EDGE,"E187"),sQuery(id+"F0.wireOp",EDGE,"E188"),sQuery(id+"F0.wireOp",EDGE,"E189"),sQuery(id+"F0.wireOp",EDGE,"E190"),sQuery(id+"F0.wireOp",EDGE,"E191"),sQuery(id+"F0.wireOp",EDGE,"E192"),sQuery(id+"F0.wireOp",EDGE,"E193"),sQuery(id+"F0.wireOp",EDGE,"E194"),sQuery(id+"F0.wireOp",EDGE,"E195"),sQuery(id+"F0.wireOp",EDGE,"E196"),sQuery(id+"F0.wireOp",EDGE,"E197"),sQuery(id+"F0.wireOp",EDGE,"E198"),sQuery(id+"F0.wireOp",EDGE,"E199"),sQuery(id+"F0.wireOp",EDGE,"E200"),sQuery(id+"F0.wireOp",EDGE,"E201"),sQuery(id+"F0.wireOp",EDGE,"E202"),sQuery(id+"F0.wireOp",EDGE,"E203"),sQuery(id+"F0.wireOp",EDGE,"E204"),sQuery(id+"F0.wireOp",EDGE,"E205"),sQuery(id+"F0.wireOp",EDGE,"E206"),sQuery(id+"F0.wireOp",EDGE,"E207"),sQuery(id+"F0.wireOp",EDGE,"E208"),sQuery(id+"F0.wireOp",EDGE,"E209"),sQuery(id+"F0.wireOp",EDGE,"E210"),sQuery(id+"F0.wireOp",EDGE,"E211"),sQuery(id+"F0.wireOp",EDGE,"E212"),sQuery(id+"F0.wireOp",EDGE,"E213"),sQuery(id+"F0.wireOp",EDGE,"E214"),sQuery(id+"F0.wireOp",EDGE,"E215"),sQuery(id+"F0.wireOp",EDGE,"E216"),sQuery(id+"F0.wireOp",EDGE,"E217"),sQuery(id+"F0.wireOp",EDGE,"E218"),sQuery(id+"F0.wireOp",EDGE,"E219"),sQuery(id+"F0.wireOp",EDGE,"E220"),sQuery(id+"F0.wireOp",EDGE,"E221"),sQuery(id+"F0.wireOp",EDGE,"E222"),sQuery(id+"F0.wireOp",EDGE,"E223"),sQuery(id+"F0.wireOp",EDGE,"E224"),sQuery(id+"F0.wireOp",EDGE,"E225"),sQuery(id+"F0.wireOp",EDGE,"E226"),sQuery(id+"F0.wireOp",EDGE,"E227"),sQuery(id+"F0.wireOp",EDGE,"E228"),sQuery(id+"F0.wireOp",EDGE,"E229"),sQuery(id+"F0.wireOp",EDGE,"E230"),sQuery(id+"F0.wireOp",EDGE,"E231"),sQuery(id+"F0.wireOp",EDGE,"E232"),sQuery(id+"F0.wireOp",EDGE,"E233"),sQuery(id+"F0.wireOp",EDGE,"E234"),sQuery(id+"F0.wireOp",EDGE,"E235"),sQuery(id+"F0.wireOp",EDGE,"E236"),sQuery(id+"F0.wireOp",EDGE,"E237"),sQuery(id+"F0.wireOp",EDGE,"E238"),sQuery(id+"F0.wireOp",EDGE,"E239"),sQuery(id+"F0.wireOp",EDGE,"E240"),sQuery(id+"F0.wireOp",EDGE,"E241"),sQuery(id+"F0.wireOp",EDGE,"E242"),sQuery(id+"F0.wireOp",EDGE,"E243"),sQuery(id+"F3.wireOp",EDGE,"E244.bottom"),sQuery(id+"F3.wireOp",EDGE,"E244.top"),sQuery(id+"F3.wireOp",EDGE,"E244.left"),sQuery(id+"F3.wireOp",EDGE,"E244.right"),sQuery(id+"F3.wireOp",EDGE,"E245.filletArc"),sQuery(id+"F3.wireOp",EDGE,"E246.filletArc"),sQuery(id+"F3.wireOp",EDGE,"E247.filletArc"),sQuery(id+"F3.wireOp",EDGE,"E248.filletArc")])],"isStart":false})}),makeQuery(id+"F8.opExtrude","CAP_FACE",FACE,{"disambiguationData":[OSD([sQuery(id+"F7.wireOp",EDGE,"E250.bottom"),sQuery(id+"F7.wireOp",EDGE,"E250.top"),sQuery(id+"F7.wireOp",EDGE,"E250.left"),sQuery(id+"F7.wireOp",EDGE,"E250.right")])],"isStart":false})]})});
            var Q2;
            Q2=makeQuery(id+"F12.boolean.opBoolean","SPLIT",FACE,{"disambiguationData":[TD([makeQuery(id+"F12.opExtrude","SWEPT_FACE",FACE,{"disambiguationData":[OSD([sQuery(id+"F11.wireOp",EDGE,"E270")])]})])],"derivedFrom":makeQuery(id+"F8.boolean.opBoolean","MERGE",FACE,{"derivedFrom":[makeQuery(id+"F4.boolean.opBoolean","COPY",FACE,{"derivedFrom":makeQuery(id+"F4.opExtrude","CAP_FACE",FACE,{"disambiguationData":[OSD([sQuery(id+"F0.wireOp",EDGE,"E4"),sQuery(id+"F0.wireOp",EDGE,"E5"),sQuery(id+"F0.wireOp",EDGE,"E6"),sQuery(id+"F0.wireOp",EDGE,"E7"),sQuery(id+"F0.wireOp",EDGE,"E8"),sQuery(id+"F0.wireOp",EDGE,"E9"),sQuery(id+"F0.wireOp",EDGE,"E10"),sQuery(id+"F0.wireOp",EDGE,"E11"),sQuery(id+"F0.wireOp",EDGE,"E12"),sQuery(id+"F0.wireOp",EDGE,"E13"),sQuery(id+"F0.wireOp",EDGE,"E14"),sQuery(id+"F0.wireOp",EDGE,"E15"),sQuery(id+"F0.wireOp",EDGE,"E16"),sQuery(id+"F0.wireOp",EDGE,"E17"),sQuery(id+"F0.wireOp",EDGE,"E18"),sQuery(id+"F0.wireOp",EDGE,"E19"),sQuery(id+"F0.wireOp",EDGE,"E20"),sQuery(id+"F0.wireOp",EDGE,"E21"),sQuery(id+"F0.wireOp",EDGE,"E22"),sQuery(id+"F0.wireOp",EDGE,"E23"),sQuery(id+"F0.wireOp",EDGE,"E24"),sQuery(id+"F0.wireOp",EDGE,"E25"),sQuery(id+"F0.wireOp",EDGE,"E26"),sQuery(id+"F0.wireOp",EDGE,"E27"),sQuery(id+"F0.wireOp",EDGE,"E28"),sQuery(id+"F0.wireOp",EDGE,"E29"),sQuery(id+"F0.wireOp",EDGE,"E30"),sQuery(id+"F0.wireOp",EDGE,"E31"),sQuery(id+"F0.wireOp",EDGE,"E32"),sQuery(id+"F0.wireOp",EDGE,"E33"),sQuery(id+"F0.wireOp",EDGE,"E34"),sQuery(id+"F0.wireOp",EDGE,"E35"),sQuery(id+"F0.wireOp",EDGE,"E36"),sQuery(id+"F0.wireOp",EDGE,"E37"),sQuery(id+"F0.wireOp",EDGE,"E38"),sQuery(id+"F0.wireOp",EDGE,"E39"),sQuery(id+"F0.wireOp",EDGE,"E40"),sQuery(id+"F0.wireOp",EDGE,"E41"),sQuery(id+"F0.wireOp",EDGE,"E42"),sQuery(id+"F0.wireOp",EDGE,"E43"),sQuery(id+"F0.wireOp",EDGE,"E44"),sQuery(id+"F0.wireOp",EDGE,"E45"),sQuery(id+"F0.wireOp",EDGE,"E46"),sQuery(id+"F0.wireOp",EDGE,"E47"),sQuery(id+"F0.wireOp",EDGE,"E48"),sQuery(id+"F0.wireOp",EDGE,"E49"),sQuery(id+"F0.wireOp",EDGE,"E50"),sQuery(id+"F0.wireOp",EDGE,"E51"),sQuery(id+"F0.wireOp",EDGE,"E52"),sQuery(id+"F0.wireOp",EDGE,"E53"),sQuery(id+"F0.wireOp",EDGE,"E54"),sQuery(id+"F0.wireOp",EDGE,"E55"),sQuery(id+"F0.wireOp",EDGE,"E56"),sQuery(id+"F0.wireOp",EDGE,"E57"),sQuery(id+"F0.wireOp",EDGE,"E58"),sQuery(id+"F0.wireOp",EDGE,"E59"),sQuery(id+"F0.wireOp",EDGE,"E60"),sQuery(id+"F0.wireOp",EDGE,"E61"),sQuery(id+"F0.wireOp",EDGE,"E62"),sQuery(id+"F0.wireOp",EDGE,"E63"),sQuery(id+"F0.wireOp",EDGE,"E64"),sQuery(id+"F0.wireOp",EDGE,"E65"),sQuery(id+"F0.wireOp",EDGE,"E66"),sQuery(id+"F0.wireOp",EDGE,"E67"),sQuery(id+"F0.wireOp",EDGE,"E68"),sQuery(id+"F0.wireOp",EDGE,"E69"),sQuery(id+"F0.wireOp",EDGE,"E70"),sQuery(id+"F0.wireOp",EDGE,"E71"),sQuery(id+"F0.wireOp",EDGE,"E72"),sQuery(id+"F0.wireOp",EDGE,"E73"),sQuery(id+"F0.wireOp",EDGE,"E74"),sQuery(id+"F0.wireOp",EDGE,"E75"),sQuery(id+"F0.wireOp",EDGE,"E76"),sQuery(id+"F0.wireOp",EDGE,"E77"),sQuery(id+"F0.wireOp",EDGE,"E78"),sQuery(id+"F0.wireOp",EDGE,"E79"),sQuery(id+"F0.wireOp",EDGE,"E80"),sQuery(id+"F0.wireOp",EDGE,"E81"),sQuery(id+"F0.wireOp",EDGE,"E82"),sQuery(id+"F0.wireOp",EDGE,"E83"),sQuery(id+"F0.wireOp",EDGE,"E84"),sQuery(id+"F0.wireOp",EDGE,"E85"),sQuery(id+"F0.wireOp",EDGE,"E86"),sQuery(id+"F0.wireOp",EDGE,"E87"),sQuery(id+"F0.wireOp",EDGE,"E88"),sQuery(id+"F0.wireOp",EDGE,"E89"),sQuery(id+"F0.wireOp",EDGE,"E90"),sQuery(id+"F0.wireOp",EDGE,"E91"),sQuery(id+"F0.wireOp",EDGE,"E92"),sQuery(id+"F0.wireOp",EDGE,"E93"),sQuery(id+"F0.wireOp",EDGE,"E94"),sQuery(id+"F0.wireOp",EDGE,"E95"),sQuery(id+"F0.wireOp",EDGE,"E96"),sQuery(id+"F0.wireOp",EDGE,"E97"),sQuery(id+"F0.wireOp",EDGE,"E98"),sQuery(id+"F0.wireOp",EDGE,"E99"),sQuery(id+"F0.wireOp",EDGE,"E100"),sQuery(id+"F0.wireOp",EDGE,"E101"),sQuery(id+"F0.wireOp",EDGE,"E102"),sQuery(id+"F0.wireOp",EDGE,"E103"),sQuery(id+"F0.wireOp",EDGE,"E104"),sQuery(id+"F0.wireOp",EDGE,"E105"),sQuery(id+"F0.wireOp",EDGE,"E106"),sQuery(id+"F0.wireOp",EDGE,"E107"),sQuery(id+"F0.wireOp",EDGE,"E108"),sQuery(id+"F0.wireOp",EDGE,"E109"),sQuery(id+"F0.wireOp",EDGE,"E110"),sQuery(id+"F0.wireOp",EDGE,"E111"),sQuery(id+"F0.wireOp",EDGE,"E112"),sQuery(id+"F0.wireOp",EDGE,"E113"),sQuery(id+"F0.wireOp",EDGE,"E114"),sQuery(id+"F0.wireOp",EDGE,"E115"),sQuery(id+"F0.wireOp",EDGE,"E116"),sQuery(id+"F0.wireOp",EDGE,"E117"),sQuery(id+"F0.wireOp",EDGE,"E118"),sQuery(id+"F0.wireOp",EDGE,"E119"),sQuery(id+"F0.wireOp",EDGE,"E120"),sQuery(id+"F0.wireOp",EDGE,"E121"),sQuery(id+"F0.wireOp",EDGE,"E122"),sQuery(id+"F0.wireOp",EDGE,"E123"),sQuery(id+"F0.wireOp",EDGE,"E124"),sQuery(id+"F0.wireOp",EDGE,"E125"),sQuery(id+"F0.wireOp",EDGE,"E126"),sQuery(id+"F0.wireOp",EDGE,"E127"),sQuery(id+"F0.wireOp",EDGE,"E128"),sQuery(id+"F0.wireOp",EDGE,"E129"),sQuery(id+"F0.wireOp",EDGE,"E130"),sQuery(id+"F0.wireOp",EDGE,"E131"),sQuery(id+"F0.wireOp",EDGE,"E132"),sQuery(id+"F0.wireOp",EDGE,"E133"),sQuery(id+"F0.wireOp",EDGE,"E134"),sQuery(id+"F0.wireOp",EDGE,"E135"),sQuery(id+"F0.wireOp",EDGE,"E136"),sQuery(id+"F0.wireOp",EDGE,"E137"),sQuery(id+"F0.wireOp",EDGE,"E138"),sQuery(id+"F0.wireOp",EDGE,"E139"),sQuery(id+"F0.wireOp",EDGE,"E140"),sQuery(id+"F0.wireOp",EDGE,"E141"),sQuery(id+"F0.wireOp",EDGE,"E142"),sQuery(id+"F0.wireOp",EDGE,"E143"),sQuery(id+"F0.wireOp",EDGE,"E144"),sQuery(id+"F0.wireOp",EDGE,"E145"),sQuery(id+"F0.wireOp",EDGE,"E146"),sQuery(id+"F0.wireOp",EDGE,"E147"),sQuery(id+"F0.wireOp",EDGE,"E148"),sQuery(id+"F0.wireOp",EDGE,"E149"),sQuery(id+"F0.wireOp",EDGE,"E150"),sQuery(id+"F0.wireOp",EDGE,"E151"),sQuery(id+"F0.wireOp",EDGE,"E152"),sQuery(id+"F0.wireOp",EDGE,"E153"),sQuery(id+"F0.wireOp",EDGE,"E154"),sQuery(id+"F0.wireOp",EDGE,"E155"),sQuery(id+"F0.wireOp",EDGE,"E156"),sQuery(id+"F0.wireOp",EDGE,"E157"),sQuery(id+"F0.wireOp",EDGE,"E158"),sQuery(id+"F0.wireOp",EDGE,"E159"),sQuery(id+"F0.wireOp",EDGE,"E160"),sQuery(id+"F0.wireOp",EDGE,"E161"),sQuery(id+"F0.wireOp",EDGE,"E162"),sQuery(id+"F0.wireOp",EDGE,"E163"),sQuery(id+"F0.wireOp",EDGE,"E164"),sQuery(id+"F0.wireOp",EDGE,"E165"),sQuery(id+"F0.wireOp",EDGE,"E166"),sQuery(id+"F0.wireOp",EDGE,"E167"),sQuery(id+"F0.wireOp",EDGE,"E168"),sQuery(id+"F0.wireOp",EDGE,"E169"),sQuery(id+"F0.wireOp",EDGE,"E170"),sQuery(id+"F0.wireOp",EDGE,"E171"),sQuery(id+"F0.wireOp",EDGE,"E172"),sQuery(id+"F0.wireOp",EDGE,"E173"),sQuery(id+"F0.wireOp",EDGE,"E174"),sQuery(id+"F0.wireOp",EDGE,"E175"),sQuery(id+"F0.wireOp",EDGE,"E176"),sQuery(id+"F0.wireOp",EDGE,"E177"),sQuery(id+"F0.wireOp",EDGE,"E178"),sQuery(id+"F0.wireOp",EDGE,"E179"),sQuery(id+"F0.wireOp",EDGE,"E180"),sQuery(id+"F0.wireOp",EDGE,"E181"),sQuery(id+"F0.wireOp",EDGE,"E182"),sQuery(id+"F0.wireOp",EDGE,"E183"),sQuery(id+"F0.wireOp",EDGE,"E184"),sQuery(id+"F0.wireOp",EDGE,"E185"),sQuery(id+"F0.wireOp",EDGE,"E186"),sQuery(id+"F0.wireOp",EDGE,"E187"),sQuery(id+"F0.wireOp",EDGE,"E188"),sQuery(id+"F0.wireOp",EDGE,"E189"),sQuery(id+"F0.wireOp",EDGE,"E190"),sQuery(id+"F0.wireOp",EDGE,"E191"),sQuery(id+"F0.wireOp",EDGE,"E192"),sQuery(id+"F0.wireOp",EDGE,"E193"),sQuery(id+"F0.wireOp",EDGE,"E194"),sQuery(id+"F0.wireOp",EDGE,"E195"),sQuery(id+"F0.wireOp",EDGE,"E196"),sQuery(id+"F0.wireOp",EDGE,"E197"),sQuery(id+"F0.wireOp",EDGE,"E198"),sQuery(id+"F0.wireOp",EDGE,"E199"),sQuery(id+"F0.wireOp",EDGE,"E200"),sQuery(id+"F0.wireOp",EDGE,"E201"),sQuery(id+"F0.wireOp",EDGE,"E202"),sQuery(id+"F0.wireOp",EDGE,"E203"),sQuery(id+"F0.wireOp",EDGE,"E204"),sQuery(id+"F0.wireOp",EDGE,"E205"),sQuery(id+"F0.wireOp",EDGE,"E206"),sQuery(id+"F0.wireOp",EDGE,"E207"),sQuery(id+"F0.wireOp",EDGE,"E208"),sQuery(id+"F0.wireOp",EDGE,"E209"),sQuery(id+"F0.wireOp",EDGE,"E210"),sQuery(id+"F0.wireOp",EDGE,"E211"),sQuery(id+"F0.wireOp",EDGE,"E212"),sQuery(id+"F0.wireOp",EDGE,"E213"),sQuery(id+"F0.wireOp",EDGE,"E214"),sQuery(id+"F0.wireOp",EDGE,"E215"),sQuery(id+"F0.wireOp",EDGE,"E216"),sQuery(id+"F0.wireOp",EDGE,"E217"),sQuery(id+"F0.wireOp",EDGE,"E218"),sQuery(id+"F0.wireOp",EDGE,"E219"),sQuery(id+"F0.wireOp",EDGE,"E220"),sQuery(id+"F0.wireOp",EDGE,"E221"),sQuery(id+"F0.wireOp",EDGE,"E222"),sQuery(id+"F0.wireOp",EDGE,"E223"),sQuery(id+"F0.wireOp",EDGE,"E224"),sQuery(id+"F0.wireOp",EDGE,"E225"),sQuery(id+"F0.wireOp",EDGE,"E226"),sQuery(id+"F0.wireOp",EDGE,"E227"),sQuery(id+"F0.wireOp",EDGE,"E228"),sQuery(id+"F0.wireOp",EDGE,"E229"),sQuery(id+"F0.wireOp",EDGE,"E230"),sQuery(id+"F0.wireOp",EDGE,"E231"),sQuery(id+"F0.wireOp",EDGE,"E232"),sQuery(id+"F0.wireOp",EDGE,"E233"),sQuery(id+"F0.wireOp",EDGE,"E234"),sQuery(id+"F0.wireOp",EDGE,"E235"),sQuery(id+"F0.wireOp",EDGE,"E236"),sQuery(id+"F0.wireOp",EDGE,"E237"),sQuery(id+"F0.wireOp",EDGE,"E238"),sQuery(id+"F0.wireOp",EDGE,"E239"),sQuery(id+"F0.wireOp",EDGE,"E240"),sQuery(id+"F0.wireOp",EDGE,"E241"),sQuery(id+"F0.wireOp",EDGE,"E242"),sQuery(id+"F0.wireOp",EDGE,"E243"),sQuery(id+"F3.wireOp",EDGE,"E244.bottom"),sQuery(id+"F3.wireOp",EDGE,"E244.top"),sQuery(id+"F3.wireOp",EDGE,"E244.left"),sQuery(id+"F3.wireOp",EDGE,"E244.right"),sQuery(id+"F3.wireOp",EDGE,"E245.filletArc"),sQuery(id+"F3.wireOp",EDGE,"E246.filletArc"),sQuery(id+"F3.wireOp",EDGE,"E247.filletArc"),sQuery(id+"F3.wireOp",EDGE,"E248.filletArc")])],"isStart":false})}),makeQuery(id+"F8.opExtrude","CAP_FACE",FACE,{"disambiguationData":[OSD([sQuery(id+"F7.wireOp",EDGE,"E250.bottom"),sQuery(id+"F7.wireOp",EDGE,"E250.top"),sQuery(id+"F7.wireOp",EDGE,"E250.left"),sQuery(id+"F7.wireOp",EDGE,"E250.right")])],"isStart":false})]})});
            var Q3;
            Q3=makeQuery(id+"F12.boolean.opBoolean","SPLIT",FACE,{"disambiguationData":[TD([makeQuery(id+"F12.opExtrude","SWEPT_FACE",FACE,{"disambiguationData":[OSD([sQuery(id+"F11.wireOp",EDGE,"E269")])]})])],"derivedFrom":makeQuery(id+"F8.boolean.opBoolean","MERGE",FACE,{"derivedFrom":[makeQuery(id+"F4.boolean.opBoolean","COPY",FACE,{"derivedFrom":makeQuery(id+"F4.opExtrude","CAP_FACE",FACE,{"disambiguationData":[OSD([sQuery(id+"F0.wireOp",EDGE,"E4"),sQuery(id+"F0.wireOp",EDGE,"E5"),sQuery(id+"F0.wireOp",EDGE,"E6"),sQuery(id+"F0.wireOp",EDGE,"E7"),sQuery(id+"F0.wireOp",EDGE,"E8"),sQuery(id+"F0.wireOp",EDGE,"E9"),sQuery(id+"F0.wireOp",EDGE,"E10"),sQuery(id+"F0.wireOp",EDGE,"E11"),sQuery(id+"F0.wireOp",EDGE,"E12"),sQuery(id+"F0.wireOp",EDGE,"E13"),sQuery(id+"F0.wireOp",EDGE,"E14"),sQuery(id+"F0.wireOp",EDGE,"E15"),sQuery(id+"F0.wireOp",EDGE,"E16"),sQuery(id+"F0.wireOp",EDGE,"E17"),sQuery(id+"F0.wireOp",EDGE,"E18"),sQuery(id+"F0.wireOp",EDGE,"E19"),sQuery(id+"F0.wireOp",EDGE,"E20"),sQuery(id+"F0.wireOp",EDGE,"E21"),sQuery(id+"F0.wireOp",EDGE,"E22"),sQuery(id+"F0.wireOp",EDGE,"E23"),sQuery(id+"F0.wireOp",EDGE,"E24"),sQuery(id+"F0.wireOp",EDGE,"E25"),sQuery(id+"F0.wireOp",EDGE,"E26"),sQuery(id+"F0.wireOp",EDGE,"E27"),sQuery(id+"F0.wireOp",EDGE,"E28"),sQuery(id+"F0.wireOp",EDGE,"E29"),sQuery(id+"F0.wireOp",EDGE,"E30"),sQuery(id+"F0.wireOp",EDGE,"E31"),sQuery(id+"F0.wireOp",EDGE,"E32"),sQuery(id+"F0.wireOp",EDGE,"E33"),sQuery(id+"F0.wireOp",EDGE,"E34"),sQuery(id+"F0.wireOp",EDGE,"E35"),sQuery(id+"F0.wireOp",EDGE,"E36"),sQuery(id+"F0.wireOp",EDGE,"E37"),sQuery(id+"F0.wireOp",EDGE,"E38"),sQuery(id+"F0.wireOp",EDGE,"E39"),sQuery(id+"F0.wireOp",EDGE,"E40"),sQuery(id+"F0.wireOp",EDGE,"E41"),sQuery(id+"F0.wireOp",EDGE,"E42"),sQuery(id+"F0.wireOp",EDGE,"E43"),sQuery(id+"F0.wireOp",EDGE,"E44"),sQuery(id+"F0.wireOp",EDGE,"E45"),sQuery(id+"F0.wireOp",EDGE,"E46"),sQuery(id+"F0.wireOp",EDGE,"E47"),sQuery(id+"F0.wireOp",EDGE,"E48"),sQuery(id+"F0.wireOp",EDGE,"E49"),sQuery(id+"F0.wireOp",EDGE,"E50"),sQuery(id+"F0.wireOp",EDGE,"E51"),sQuery(id+"F0.wireOp",EDGE,"E52"),sQuery(id+"F0.wireOp",EDGE,"E53"),sQuery(id+"F0.wireOp",EDGE,"E54"),sQuery(id+"F0.wireOp",EDGE,"E55"),sQuery(id+"F0.wireOp",EDGE,"E56"),sQuery(id+"F0.wireOp",EDGE,"E57"),sQuery(id+"F0.wireOp",EDGE,"E58"),sQuery(id+"F0.wireOp",EDGE,"E59"),sQuery(id+"F0.wireOp",EDGE,"E60"),sQuery(id+"F0.wireOp",EDGE,"E61"),sQuery(id+"F0.wireOp",EDGE,"E62"),sQuery(id+"F0.wireOp",EDGE,"E63"),sQuery(id+"F0.wireOp",EDGE,"E64"),sQuery(id+"F0.wireOp",EDGE,"E65"),sQuery(id+"F0.wireOp",EDGE,"E66"),sQuery(id+"F0.wireOp",EDGE,"E67"),sQuery(id+"F0.wireOp",EDGE,"E68"),sQuery(id+"F0.wireOp",EDGE,"E69"),sQuery(id+"F0.wireOp",EDGE,"E70"),sQuery(id+"F0.wireOp",EDGE,"E71"),sQuery(id+"F0.wireOp",EDGE,"E72"),sQuery(id+"F0.wireOp",EDGE,"E73"),sQuery(id+"F0.wireOp",EDGE,"E74"),sQuery(id+"F0.wireOp",EDGE,"E75"),sQuery(id+"F0.wireOp",EDGE,"E76"),sQuery(id+"F0.wireOp",EDGE,"E77"),sQuery(id+"F0.wireOp",EDGE,"E78"),sQuery(id+"F0.wireOp",EDGE,"E79"),sQuery(id+"F0.wireOp",EDGE,"E80"),sQuery(id+"F0.wireOp",EDGE,"E81"),sQuery(id+"F0.wireOp",EDGE,"E82"),sQuery(id+"F0.wireOp",EDGE,"E83"),sQuery(id+"F0.wireOp",EDGE,"E84"),sQuery(id+"F0.wireOp",EDGE,"E85"),sQuery(id+"F0.wireOp",EDGE,"E86"),sQuery(id+"F0.wireOp",EDGE,"E87"),sQuery(id+"F0.wireOp",EDGE,"E88"),sQuery(id+"F0.wireOp",EDGE,"E89"),sQuery(id+"F0.wireOp",EDGE,"E90"),sQuery(id+"F0.wireOp",EDGE,"E91"),sQuery(id+"F0.wireOp",EDGE,"E92"),sQuery(id+"F0.wireOp",EDGE,"E93"),sQuery(id+"F0.wireOp",EDGE,"E94"),sQuery(id+"F0.wireOp",EDGE,"E95"),sQuery(id+"F0.wireOp",EDGE,"E96"),sQuery(id+"F0.wireOp",EDGE,"E97"),sQuery(id+"F0.wireOp",EDGE,"E98"),sQuery(id+"F0.wireOp",EDGE,"E99"),sQuery(id+"F0.wireOp",EDGE,"E100"),sQuery(id+"F0.wireOp",EDGE,"E101"),sQuery(id+"F0.wireOp",EDGE,"E102"),sQuery(id+"F0.wireOp",EDGE,"E103"),sQuery(id+"F0.wireOp",EDGE,"E104"),sQuery(id+"F0.wireOp",EDGE,"E105"),sQuery(id+"F0.wireOp",EDGE,"E106"),sQuery(id+"F0.wireOp",EDGE,"E107"),sQuery(id+"F0.wireOp",EDGE,"E108"),sQuery(id+"F0.wireOp",EDGE,"E109"),sQuery(id+"F0.wireOp",EDGE,"E110"),sQuery(id+"F0.wireOp",EDGE,"E111"),sQuery(id+"F0.wireOp",EDGE,"E112"),sQuery(id+"F0.wireOp",EDGE,"E113"),sQuery(id+"F0.wireOp",EDGE,"E114"),sQuery(id+"F0.wireOp",EDGE,"E115"),sQuery(id+"F0.wireOp",EDGE,"E116"),sQuery(id+"F0.wireOp",EDGE,"E117"),sQuery(id+"F0.wireOp",EDGE,"E118"),sQuery(id+"F0.wireOp",EDGE,"E119"),sQuery(id+"F0.wireOp",EDGE,"E120"),sQuery(id+"F0.wireOp",EDGE,"E121"),sQuery(id+"F0.wireOp",EDGE,"E122"),sQuery(id+"F0.wireOp",EDGE,"E123"),sQuery(id+"F0.wireOp",EDGE,"E124"),sQuery(id+"F0.wireOp",EDGE,"E125"),sQuery(id+"F0.wireOp",EDGE,"E126"),sQuery(id+"F0.wireOp",EDGE,"E127"),sQuery(id+"F0.wireOp",EDGE,"E128"),sQuery(id+"F0.wireOp",EDGE,"E129"),sQuery(id+"F0.wireOp",EDGE,"E130"),sQuery(id+"F0.wireOp",EDGE,"E131"),sQuery(id+"F0.wireOp",EDGE,"E132"),sQuery(id+"F0.wireOp",EDGE,"E133"),sQuery(id+"F0.wireOp",EDGE,"E134"),sQuery(id+"F0.wireOp",EDGE,"E135"),sQuery(id+"F0.wireOp",EDGE,"E136"),sQuery(id+"F0.wireOp",EDGE,"E137"),sQuery(id+"F0.wireOp",EDGE,"E138"),sQuery(id+"F0.wireOp",EDGE,"E139"),sQuery(id+"F0.wireOp",EDGE,"E140"),sQuery(id+"F0.wireOp",EDGE,"E141"),sQuery(id+"F0.wireOp",EDGE,"E142"),sQuery(id+"F0.wireOp",EDGE,"E143"),sQuery(id+"F0.wireOp",EDGE,"E144"),sQuery(id+"F0.wireOp",EDGE,"E145"),sQuery(id+"F0.wireOp",EDGE,"E146"),sQuery(id+"F0.wireOp",EDGE,"E147"),sQuery(id+"F0.wireOp",EDGE,"E148"),sQuery(id+"F0.wireOp",EDGE,"E149"),sQuery(id+"F0.wireOp",EDGE,"E150"),sQuery(id+"F0.wireOp",EDGE,"E151"),sQuery(id+"F0.wireOp",EDGE,"E152"),sQuery(id+"F0.wireOp",EDGE,"E153"),sQuery(id+"F0.wireOp",EDGE,"E154"),sQuery(id+"F0.wireOp",EDGE,"E155"),sQuery(id+"F0.wireOp",EDGE,"E156"),sQuery(id+"F0.wireOp",EDGE,"E157"),sQuery(id+"F0.wireOp",EDGE,"E158"),sQuery(id+"F0.wireOp",EDGE,"E159"),sQuery(id+"F0.wireOp",EDGE,"E160"),sQuery(id+"F0.wireOp",EDGE,"E161"),sQuery(id+"F0.wireOp",EDGE,"E162"),sQuery(id+"F0.wireOp",EDGE,"E163"),sQuery(id+"F0.wireOp",EDGE,"E164"),sQuery(id+"F0.wireOp",EDGE,"E165"),sQuery(id+"F0.wireOp",EDGE,"E166"),sQuery(id+"F0.wireOp",EDGE,"E167"),sQuery(id+"F0.wireOp",EDGE,"E168"),sQuery(id+"F0.wireOp",EDGE,"E169"),sQuery(id+"F0.wireOp",EDGE,"E170"),sQuery(id+"F0.wireOp",EDGE,"E171"),sQuery(id+"F0.wireOp",EDGE,"E172"),sQuery(id+"F0.wireOp",EDGE,"E173"),sQuery(id+"F0.wireOp",EDGE,"E174"),sQuery(id+"F0.wireOp",EDGE,"E175"),sQuery(id+"F0.wireOp",EDGE,"E176"),sQuery(id+"F0.wireOp",EDGE,"E177"),sQuery(id+"F0.wireOp",EDGE,"E178"),sQuery(id+"F0.wireOp",EDGE,"E179"),sQuery(id+"F0.wireOp",EDGE,"E180"),sQuery(id+"F0.wireOp",EDGE,"E181"),sQuery(id+"F0.wireOp",EDGE,"E182"),sQuery(id+"F0.wireOp",EDGE,"E183"),sQuery(id+"F0.wireOp",EDGE,"E184"),sQuery(id+"F0.wireOp",EDGE,"E185"),sQuery(id+"F0.wireOp",EDGE,"E186"),sQuery(id+"F0.wireOp",EDGE,"E187"),sQuery(id+"F0.wireOp",EDGE,"E188"),sQuery(id+"F0.wireOp",EDGE,"E189"),sQuery(id+"F0.wireOp",EDGE,"E190"),sQuery(id+"F0.wireOp",EDGE,"E191"),sQuery(id+"F0.wireOp",EDGE,"E192"),sQuery(id+"F0.wireOp",EDGE,"E193"),sQuery(id+"F0.wireOp",EDGE,"E194"),sQuery(id+"F0.wireOp",EDGE,"E195"),sQuery(id+"F0.wireOp",EDGE,"E196"),sQuery(id+"F0.wireOp",EDGE,"E197"),sQuery(id+"F0.wireOp",EDGE,"E198"),sQuery(id+"F0.wireOp",EDGE,"E199"),sQuery(id+"F0.wireOp",EDGE,"E200"),sQuery(id+"F0.wireOp",EDGE,"E201"),sQuery(id+"F0.wireOp",EDGE,"E202"),sQuery(id+"F0.wireOp",EDGE,"E203"),sQuery(id+"F0.wireOp",EDGE,"E204"),sQuery(id+"F0.wireOp",EDGE,"E205"),sQuery(id+"F0.wireOp",EDGE,"E206"),sQuery(id+"F0.wireOp",EDGE,"E207"),sQuery(id+"F0.wireOp",EDGE,"E208"),sQuery(id+"F0.wireOp",EDGE,"E209"),sQuery(id+"F0.wireOp",EDGE,"E210"),sQuery(id+"F0.wireOp",EDGE,"E211"),sQuery(id+"F0.wireOp",EDGE,"E212"),sQuery(id+"F0.wireOp",EDGE,"E213"),sQuery(id+"F0.wireOp",EDGE,"E214"),sQuery(id+"F0.wireOp",EDGE,"E215"),sQuery(id+"F0.wireOp",EDGE,"E216"),sQuery(id+"F0.wireOp",EDGE,"E217"),sQuery(id+"F0.wireOp",EDGE,"E218"),sQuery(id+"F0.wireOp",EDGE,"E219"),sQuery(id+"F0.wireOp",EDGE,"E220"),sQuery(id+"F0.wireOp",EDGE,"E221"),sQuery(id+"F0.wireOp",EDGE,"E222"),sQuery(id+"F0.wireOp",EDGE,"E223"),sQuery(id+"F0.wireOp",EDGE,"E224"),sQuery(id+"F0.wireOp",EDGE,"E225"),sQuery(id+"F0.wireOp",EDGE,"E226"),sQuery(id+"F0.wireOp",EDGE,"E227"),sQuery(id+"F0.wireOp",EDGE,"E228"),sQuery(id+"F0.wireOp",EDGE,"E229"),sQuery(id+"F0.wireOp",EDGE,"E230"),sQuery(id+"F0.wireOp",EDGE,"E231"),sQuery(id+"F0.wireOp",EDGE,"E232"),sQuery(id+"F0.wireOp",EDGE,"E233"),sQuery(id+"F0.wireOp",EDGE,"E234"),sQuery(id+"F0.wireOp",EDGE,"E235"),sQuery(id+"F0.wireOp",EDGE,"E236"),sQuery(id+"F0.wireOp",EDGE,"E237"),sQuery(id+"F0.wireOp",EDGE,"E238"),sQuery(id+"F0.wireOp",EDGE,"E239"),sQuery(id+"F0.wireOp",EDGE,"E240"),sQuery(id+"F0.wireOp",EDGE,"E241"),sQuery(id+"F0.wireOp",EDGE,"E242"),sQuery(id+"F0.wireOp",EDGE,"E243"),sQuery(id+"F3.wireOp",EDGE,"E244.bottom"),sQuery(id+"F3.wireOp",EDGE,"E244.top"),sQuery(id+"F3.wireOp",EDGE,"E244.left"),sQuery(id+"F3.wireOp",EDGE,"E244.right"),sQuery(id+"F3.wireOp",EDGE,"E245.filletArc"),sQuery(id+"F3.wireOp",EDGE,"E246.filletArc"),sQuery(id+"F3.wireOp",EDGE,"E247.filletArc"),sQuery(id+"F3.wireOp",EDGE,"E248.filletArc")])],"isStart":false})}),makeQuery(id+"F8.opExtrude","CAP_FACE",FACE,{"disambiguationData":[OSD([sQuery(id+"F7.wireOp",EDGE,"E250.bottom"),sQuery(id+"F7.wireOp",EDGE,"E250.top"),sQuery(id+"F7.wireOp",EDGE,"E250.left"),sQuery(id+"F7.wireOp",EDGE,"E250.right")])],"isStart":false})]})});
            var Q4;
            Q4=makeQuery(id+"F12.boolean.opBoolean","SPLIT",FACE,{"disambiguationData":[TD([makeQuery(id+"F12.opExtrude","SWEPT_FACE",FACE,{"disambiguationData":[OSD([sQuery(id+"F11.wireOp",EDGE,"E271")])]})])],"derivedFrom":makeQuery(id+"F8.boolean.opBoolean","MERGE",FACE,{"derivedFrom":[makeQuery(id+"F4.boolean.opBoolean","COPY",FACE,{"derivedFrom":makeQuery(id+"F4.opExtrude","CAP_FACE",FACE,{"disambiguationData":[OSD([sQuery(id+"F0.wireOp",EDGE,"E4"),sQuery(id+"F0.wireOp",EDGE,"E5"),sQuery(id+"F0.wireOp",EDGE,"E6"),sQuery(id+"F0.wireOp",EDGE,"E7"),sQuery(id+"F0.wireOp",EDGE,"E8"),sQuery(id+"F0.wireOp",EDGE,"E9"),sQuery(id+"F0.wireOp",EDGE,"E10"),sQuery(id+"F0.wireOp",EDGE,"E11"),sQuery(id+"F0.wireOp",EDGE,"E12"),sQuery(id+"F0.wireOp",EDGE,"E13"),sQuery(id+"F0.wireOp",EDGE,"E14"),sQuery(id+"F0.wireOp",EDGE,"E15"),sQuery(id+"F0.wireOp",EDGE,"E16"),sQuery(id+"F0.wireOp",EDGE,"E17"),sQuery(id+"F0.wireOp",EDGE,"E18"),sQuery(id+"F0.wireOp",EDGE,"E19"),sQuery(id+"F0.wireOp",EDGE,"E20"),sQuery(id+"F0.wireOp",EDGE,"E21"),sQuery(id+"F0.wireOp",EDGE,"E22"),sQuery(id+"F0.wireOp",EDGE,"E23"),sQuery(id+"F0.wireOp",EDGE,"E24"),sQuery(id+"F0.wireOp",EDGE,"E25"),sQuery(id+"F0.wireOp",EDGE,"E26"),sQuery(id+"F0.wireOp",EDGE,"E27"),sQuery(id+"F0.wireOp",EDGE,"E28"),sQuery(id+"F0.wireOp",EDGE,"E29"),sQuery(id+"F0.wireOp",EDGE,"E30"),sQuery(id+"F0.wireOp",EDGE,"E31"),sQuery(id+"F0.wireOp",EDGE,"E32"),sQuery(id+"F0.wireOp",EDGE,"E33"),sQuery(id+"F0.wireOp",EDGE,"E34"),sQuery(id+"F0.wireOp",EDGE,"E35"),sQuery(id+"F0.wireOp",EDGE,"E36"),sQuery(id+"F0.wireOp",EDGE,"E37"),sQuery(id+"F0.wireOp",EDGE,"E38"),sQuery(id+"F0.wireOp",EDGE,"E39"),sQuery(id+"F0.wireOp",EDGE,"E40"),sQuery(id+"F0.wireOp",EDGE,"E41"),sQuery(id+"F0.wireOp",EDGE,"E42"),sQuery(id+"F0.wireOp",EDGE,"E43"),sQuery(id+"F0.wireOp",EDGE,"E44"),sQuery(id+"F0.wireOp",EDGE,"E45"),sQuery(id+"F0.wireOp",EDGE,"E46"),sQuery(id+"F0.wireOp",EDGE,"E47"),sQuery(id+"F0.wireOp",EDGE,"E48"),sQuery(id+"F0.wireOp",EDGE,"E49"),sQuery(id+"F0.wireOp",EDGE,"E50"),sQuery(id+"F0.wireOp",EDGE,"E51"),sQuery(id+"F0.wireOp",EDGE,"E52"),sQuery(id+"F0.wireOp",EDGE,"E53"),sQuery(id+"F0.wireOp",EDGE,"E54"),sQuery(id+"F0.wireOp",EDGE,"E55"),sQuery(id+"F0.wireOp",EDGE,"E56"),sQuery(id+"F0.wireOp",EDGE,"E57"),sQuery(id+"F0.wireOp",EDGE,"E58"),sQuery(id+"F0.wireOp",EDGE,"E59"),sQuery(id+"F0.wireOp",EDGE,"E60"),sQuery(id+"F0.wireOp",EDGE,"E61"),sQuery(id+"F0.wireOp",EDGE,"E62"),sQuery(id+"F0.wireOp",EDGE,"E63"),sQuery(id+"F0.wireOp",EDGE,"E64"),sQuery(id+"F0.wireOp",EDGE,"E65"),sQuery(id+"F0.wireOp",EDGE,"E66"),sQuery(id+"F0.wireOp",EDGE,"E67"),sQuery(id+"F0.wireOp",EDGE,"E68"),sQuery(id+"F0.wireOp",EDGE,"E69"),sQuery(id+"F0.wireOp",EDGE,"E70"),sQuery(id+"F0.wireOp",EDGE,"E71"),sQuery(id+"F0.wireOp",EDGE,"E72"),sQuery(id+"F0.wireOp",EDGE,"E73"),sQuery(id+"F0.wireOp",EDGE,"E74"),sQuery(id+"F0.wireOp",EDGE,"E75"),sQuery(id+"F0.wireOp",EDGE,"E76"),sQuery(id+"F0.wireOp",EDGE,"E77"),sQuery(id+"F0.wireOp",EDGE,"E78"),sQuery(id+"F0.wireOp",EDGE,"E79"),sQuery(id+"F0.wireOp",EDGE,"E80"),sQuery(id+"F0.wireOp",EDGE,"E81"),sQuery(id+"F0.wireOp",EDGE,"E82"),sQuery(id+"F0.wireOp",EDGE,"E83"),sQuery(id+"F0.wireOp",EDGE,"E84"),sQuery(id+"F0.wireOp",EDGE,"E85"),sQuery(id+"F0.wireOp",EDGE,"E86"),sQuery(id+"F0.wireOp",EDGE,"E87"),sQuery(id+"F0.wireOp",EDGE,"E88"),sQuery(id+"F0.wireOp",EDGE,"E89"),sQuery(id+"F0.wireOp",EDGE,"E90"),sQuery(id+"F0.wireOp",EDGE,"E91"),sQuery(id+"F0.wireOp",EDGE,"E92"),sQuery(id+"F0.wireOp",EDGE,"E93"),sQuery(id+"F0.wireOp",EDGE,"E94"),sQuery(id+"F0.wireOp",EDGE,"E95"),sQuery(id+"F0.wireOp",EDGE,"E96"),sQuery(id+"F0.wireOp",EDGE,"E97"),sQuery(id+"F0.wireOp",EDGE,"E98"),sQuery(id+"F0.wireOp",EDGE,"E99"),sQuery(id+"F0.wireOp",EDGE,"E100"),sQuery(id+"F0.wireOp",EDGE,"E101"),sQuery(id+"F0.wireOp",EDGE,"E102"),sQuery(id+"F0.wireOp",EDGE,"E103"),sQuery(id+"F0.wireOp",EDGE,"E104"),sQuery(id+"F0.wireOp",EDGE,"E105"),sQuery(id+"F0.wireOp",EDGE,"E106"),sQuery(id+"F0.wireOp",EDGE,"E107"),sQuery(id+"F0.wireOp",EDGE,"E108"),sQuery(id+"F0.wireOp",EDGE,"E109"),sQuery(id+"F0.wireOp",EDGE,"E110"),sQuery(id+"F0.wireOp",EDGE,"E111"),sQuery(id+"F0.wireOp",EDGE,"E112"),sQuery(id+"F0.wireOp",EDGE,"E113"),sQuery(id+"F0.wireOp",EDGE,"E114"),sQuery(id+"F0.wireOp",EDGE,"E115"),sQuery(id+"F0.wireOp",EDGE,"E116"),sQuery(id+"F0.wireOp",EDGE,"E117"),sQuery(id+"F0.wireOp",EDGE,"E118"),sQuery(id+"F0.wireOp",EDGE,"E119"),sQuery(id+"F0.wireOp",EDGE,"E120"),sQuery(id+"F0.wireOp",EDGE,"E121"),sQuery(id+"F0.wireOp",EDGE,"E122"),sQuery(id+"F0.wireOp",EDGE,"E123"),sQuery(id+"F0.wireOp",EDGE,"E124"),sQuery(id+"F0.wireOp",EDGE,"E125"),sQuery(id+"F0.wireOp",EDGE,"E126"),sQuery(id+"F0.wireOp",EDGE,"E127"),sQuery(id+"F0.wireOp",EDGE,"E128"),sQuery(id+"F0.wireOp",EDGE,"E129"),sQuery(id+"F0.wireOp",EDGE,"E130"),sQuery(id+"F0.wireOp",EDGE,"E131"),sQuery(id+"F0.wireOp",EDGE,"E132"),sQuery(id+"F0.wireOp",EDGE,"E133"),sQuery(id+"F0.wireOp",EDGE,"E134"),sQuery(id+"F0.wireOp",EDGE,"E135"),sQuery(id+"F0.wireOp",EDGE,"E136"),sQuery(id+"F0.wireOp",EDGE,"E137"),sQuery(id+"F0.wireOp",EDGE,"E138"),sQuery(id+"F0.wireOp",EDGE,"E139"),sQuery(id+"F0.wireOp",EDGE,"E140"),sQuery(id+"F0.wireOp",EDGE,"E141"),sQuery(id+"F0.wireOp",EDGE,"E142"),sQuery(id+"F0.wireOp",EDGE,"E143"),sQuery(id+"F0.wireOp",EDGE,"E144"),sQuery(id+"F0.wireOp",EDGE,"E145"),sQuery(id+"F0.wireOp",EDGE,"E146"),sQuery(id+"F0.wireOp",EDGE,"E147"),sQuery(id+"F0.wireOp",EDGE,"E148"),sQuery(id+"F0.wireOp",EDGE,"E149"),sQuery(id+"F0.wireOp",EDGE,"E150"),sQuery(id+"F0.wireOp",EDGE,"E151"),sQuery(id+"F0.wireOp",EDGE,"E152"),sQuery(id+"F0.wireOp",EDGE,"E153"),sQuery(id+"F0.wireOp",EDGE,"E154"),sQuery(id+"F0.wireOp",EDGE,"E155"),sQuery(id+"F0.wireOp",EDGE,"E156"),sQuery(id+"F0.wireOp",EDGE,"E157"),sQuery(id+"F0.wireOp",EDGE,"E158"),sQuery(id+"F0.wireOp",EDGE,"E159"),sQuery(id+"F0.wireOp",EDGE,"E160"),sQuery(id+"F0.wireOp",EDGE,"E161"),sQuery(id+"F0.wireOp",EDGE,"E162"),sQuery(id+"F0.wireOp",EDGE,"E163"),sQuery(id+"F0.wireOp",EDGE,"E164"),sQuery(id+"F0.wireOp",EDGE,"E165"),sQuery(id+"F0.wireOp",EDGE,"E166"),sQuery(id+"F0.wireOp",EDGE,"E167"),sQuery(id+"F0.wireOp",EDGE,"E168"),sQuery(id+"F0.wireOp",EDGE,"E169"),sQuery(id+"F0.wireOp",EDGE,"E170"),sQuery(id+"F0.wireOp",EDGE,"E171"),sQuery(id+"F0.wireOp",EDGE,"E172"),sQuery(id+"F0.wireOp",EDGE,"E173"),sQuery(id+"F0.wireOp",EDGE,"E174"),sQuery(id+"F0.wireOp",EDGE,"E175"),sQuery(id+"F0.wireOp",EDGE,"E176"),sQuery(id+"F0.wireOp",EDGE,"E177"),sQuery(id+"F0.wireOp",EDGE,"E178"),sQuery(id+"F0.wireOp",EDGE,"E179"),sQuery(id+"F0.wireOp",EDGE,"E180"),sQuery(id+"F0.wireOp",EDGE,"E181"),sQuery(id+"F0.wireOp",EDGE,"E182"),sQuery(id+"F0.wireOp",EDGE,"E183"),sQuery(id+"F0.wireOp",EDGE,"E184"),sQuery(id+"F0.wireOp",EDGE,"E185"),sQuery(id+"F0.wireOp",EDGE,"E186"),sQuery(id+"F0.wireOp",EDGE,"E187"),sQuery(id+"F0.wireOp",EDGE,"E188"),sQuery(id+"F0.wireOp",EDGE,"E189"),sQuery(id+"F0.wireOp",EDGE,"E190"),sQuery(id+"F0.wireOp",EDGE,"E191"),sQuery(id+"F0.wireOp",EDGE,"E192"),sQuery(id+"F0.wireOp",EDGE,"E193"),sQuery(id+"F0.wireOp",EDGE,"E194"),sQuery(id+"F0.wireOp",EDGE,"E195"),sQuery(id+"F0.wireOp",EDGE,"E196"),sQuery(id+"F0.wireOp",EDGE,"E197"),sQuery(id+"F0.wireOp",EDGE,"E198"),sQuery(id+"F0.wireOp",EDGE,"E199"),sQuery(id+"F0.wireOp",EDGE,"E200"),sQuery(id+"F0.wireOp",EDGE,"E201"),sQuery(id+"F0.wireOp",EDGE,"E202"),sQuery(id+"F0.wireOp",EDGE,"E203"),sQuery(id+"F0.wireOp",EDGE,"E204"),sQuery(id+"F0.wireOp",EDGE,"E205"),sQuery(id+"F0.wireOp",EDGE,"E206"),sQuery(id+"F0.wireOp",EDGE,"E207"),sQuery(id+"F0.wireOp",EDGE,"E208"),sQuery(id+"F0.wireOp",EDGE,"E209"),sQuery(id+"F0.wireOp",EDGE,"E210"),sQuery(id+"F0.wireOp",EDGE,"E211"),sQuery(id+"F0.wireOp",EDGE,"E212"),sQuery(id+"F0.wireOp",EDGE,"E213"),sQuery(id+"F0.wireOp",EDGE,"E214"),sQuery(id+"F0.wireOp",EDGE,"E215"),sQuery(id+"F0.wireOp",EDGE,"E216"),sQuery(id+"F0.wireOp",EDGE,"E217"),sQuery(id+"F0.wireOp",EDGE,"E218"),sQuery(id+"F0.wireOp",EDGE,"E219"),sQuery(id+"F0.wireOp",EDGE,"E220"),sQuery(id+"F0.wireOp",EDGE,"E221"),sQuery(id+"F0.wireOp",EDGE,"E222"),sQuery(id+"F0.wireOp",EDGE,"E223"),sQuery(id+"F0.wireOp",EDGE,"E224"),sQuery(id+"F0.wireOp",EDGE,"E225"),sQuery(id+"F0.wireOp",EDGE,"E226"),sQuery(id+"F0.wireOp",EDGE,"E227"),sQuery(id+"F0.wireOp",EDGE,"E228"),sQuery(id+"F0.wireOp",EDGE,"E229"),sQuery(id+"F0.wireOp",EDGE,"E230"),sQuery(id+"F0.wireOp",EDGE,"E231"),sQuery(id+"F0.wireOp",EDGE,"E232"),sQuery(id+"F0.wireOp",EDGE,"E233"),sQuery(id+"F0.wireOp",EDGE,"E234"),sQuery(id+"F0.wireOp",EDGE,"E235"),sQuery(id+"F0.wireOp",EDGE,"E236"),sQuery(id+"F0.wireOp",EDGE,"E237"),sQuery(id+"F0.wireOp",EDGE,"E238"),sQuery(id+"F0.wireOp",EDGE,"E239"),sQuery(id+"F0.wireOp",EDGE,"E240"),sQuery(id+"F0.wireOp",EDGE,"E241"),sQuery(id+"F0.wireOp",EDGE,"E242"),sQuery(id+"F0.wireOp",EDGE,"E243"),sQuery(id+"F3.wireOp",EDGE,"E244.bottom"),sQuery(id+"F3.wireOp",EDGE,"E244.top"),sQuery(id+"F3.wireOp",EDGE,"E244.left"),sQuery(id+"F3.wireOp",EDGE,"E244.right"),sQuery(id+"F3.wireOp",EDGE,"E245.filletArc"),sQuery(id+"F3.wireOp",EDGE,"E246.filletArc"),sQuery(id+"F3.wireOp",EDGE,"E247.filletArc"),sQuery(id+"F3.wireOp",EDGE,"E248.filletArc")])],"isStart":false})}),makeQuery(id+"F8.opExtrude","CAP_FACE",FACE,{"disambiguationData":[OSD([sQuery(id+"F7.wireOp",EDGE,"E250.bottom"),sQuery(id+"F7.wireOp",EDGE,"E250.top"),sQuery(id+"F7.wireOp",EDGE,"E250.left"),sQuery(id+"F7.wireOp",EDGE,"E250.right")])],"isStart":false})]})});
            var Q5;
            Q5=makeQuery(id+"F12.boolean.opBoolean","SPLIT",FACE,{"disambiguationData":[TD([makeQuery(id+"F12.opExtrude","SWEPT_FACE",FACE,{"disambiguationData":[OSD([sQuery(id+"F11.wireOp",EDGE,"E272")])]})])],"derivedFrom":makeQuery(id+"F8.boolean.opBoolean","MERGE",FACE,{"derivedFrom":[makeQuery(id+"F4.boolean.opBoolean","COPY",FACE,{"derivedFrom":makeQuery(id+"F4.opExtrude","CAP_FACE",FACE,{"disambiguationData":[OSD([sQuery(id+"F0.wireOp",EDGE,"E4"),sQuery(id+"F0.wireOp",EDGE,"E5"),sQuery(id+"F0.wireOp",EDGE,"E6"),sQuery(id+"F0.wireOp",EDGE,"E7"),sQuery(id+"F0.wireOp",EDGE,"E8"),sQuery(id+"F0.wireOp",EDGE,"E9"),sQuery(id+"F0.wireOp",EDGE,"E10"),sQuery(id+"F0.wireOp",EDGE,"E11"),sQuery(id+"F0.wireOp",EDGE,"E12"),sQuery(id+"F0.wireOp",EDGE,"E13"),sQuery(id+"F0.wireOp",EDGE,"E14"),sQuery(id+"F0.wireOp",EDGE,"E15"),sQuery(id+"F0.wireOp",EDGE,"E16"),sQuery(id+"F0.wireOp",EDGE,"E17"),sQuery(id+"F0.wireOp",EDGE,"E18"),sQuery(id+"F0.wireOp",EDGE,"E19"),sQuery(id+"F0.wireOp",EDGE,"E20"),sQuery(id+"F0.wireOp",EDGE,"E21"),sQuery(id+"F0.wireOp",EDGE,"E22"),sQuery(id+"F0.wireOp",EDGE,"E23"),sQuery(id+"F0.wireOp",EDGE,"E24"),sQuery(id+"F0.wireOp",EDGE,"E25"),sQuery(id+"F0.wireOp",EDGE,"E26"),sQuery(id+"F0.wireOp",EDGE,"E27"),sQuery(id+"F0.wireOp",EDGE,"E28"),sQuery(id+"F0.wireOp",EDGE,"E29"),sQuery(id+"F0.wireOp",EDGE,"E30"),sQuery(id+"F0.wireOp",EDGE,"E31"),sQuery(id+"F0.wireOp",EDGE,"E32"),sQuery(id+"F0.wireOp",EDGE,"E33"),sQuery(id+"F0.wireOp",EDGE,"E34"),sQuery(id+"F0.wireOp",EDGE,"E35"),sQuery(id+"F0.wireOp",EDGE,"E36"),sQuery(id+"F0.wireOp",EDGE,"E37"),sQuery(id+"F0.wireOp",EDGE,"E38"),sQuery(id+"F0.wireOp",EDGE,"E39"),sQuery(id+"F0.wireOp",EDGE,"E40"),sQuery(id+"F0.wireOp",EDGE,"E41"),sQuery(id+"F0.wireOp",EDGE,"E42"),sQuery(id+"F0.wireOp",EDGE,"E43"),sQuery(id+"F0.wireOp",EDGE,"E44"),sQuery(id+"F0.wireOp",EDGE,"E45"),sQuery(id+"F0.wireOp",EDGE,"E46"),sQuery(id+"F0.wireOp",EDGE,"E47"),sQuery(id+"F0.wireOp",EDGE,"E48"),sQuery(id+"F0.wireOp",EDGE,"E49"),sQuery(id+"F0.wireOp",EDGE,"E50"),sQuery(id+"F0.wireOp",EDGE,"E51"),sQuery(id+"F0.wireOp",EDGE,"E52"),sQuery(id+"F0.wireOp",EDGE,"E53"),sQuery(id+"F0.wireOp",EDGE,"E54"),sQuery(id+"F0.wireOp",EDGE,"E55"),sQuery(id+"F0.wireOp",EDGE,"E56"),sQuery(id+"F0.wireOp",EDGE,"E57"),sQuery(id+"F0.wireOp",EDGE,"E58"),sQuery(id+"F0.wireOp",EDGE,"E59"),sQuery(id+"F0.wireOp",EDGE,"E60"),sQuery(id+"F0.wireOp",EDGE,"E61"),sQuery(id+"F0.wireOp",EDGE,"E62"),sQuery(id+"F0.wireOp",EDGE,"E63"),sQuery(id+"F0.wireOp",EDGE,"E64"),sQuery(id+"F0.wireOp",EDGE,"E65"),sQuery(id+"F0.wireOp",EDGE,"E66"),sQuery(id+"F0.wireOp",EDGE,"E67"),sQuery(id+"F0.wireOp",EDGE,"E68"),sQuery(id+"F0.wireOp",EDGE,"E69"),sQuery(id+"F0.wireOp",EDGE,"E70"),sQuery(id+"F0.wireOp",EDGE,"E71"),sQuery(id+"F0.wireOp",EDGE,"E72"),sQuery(id+"F0.wireOp",EDGE,"E73"),sQuery(id+"F0.wireOp",EDGE,"E74"),sQuery(id+"F0.wireOp",EDGE,"E75"),sQuery(id+"F0.wireOp",EDGE,"E76"),sQuery(id+"F0.wireOp",EDGE,"E77"),sQuery(id+"F0.wireOp",EDGE,"E78"),sQuery(id+"F0.wireOp",EDGE,"E79"),sQuery(id+"F0.wireOp",EDGE,"E80"),sQuery(id+"F0.wireOp",EDGE,"E81"),sQuery(id+"F0.wireOp",EDGE,"E82"),sQuery(id+"F0.wireOp",EDGE,"E83"),sQuery(id+"F0.wireOp",EDGE,"E84"),sQuery(id+"F0.wireOp",EDGE,"E85"),sQuery(id+"F0.wireOp",EDGE,"E86"),sQuery(id+"F0.wireOp",EDGE,"E87"),sQuery(id+"F0.wireOp",EDGE,"E88"),sQuery(id+"F0.wireOp",EDGE,"E89"),sQuery(id+"F0.wireOp",EDGE,"E90"),sQuery(id+"F0.wireOp",EDGE,"E91"),sQuery(id+"F0.wireOp",EDGE,"E92"),sQuery(id+"F0.wireOp",EDGE,"E93"),sQuery(id+"F0.wireOp",EDGE,"E94"),sQuery(id+"F0.wireOp",EDGE,"E95"),sQuery(id+"F0.wireOp",EDGE,"E96"),sQuery(id+"F0.wireOp",EDGE,"E97"),sQuery(id+"F0.wireOp",EDGE,"E98"),sQuery(id+"F0.wireOp",EDGE,"E99"),sQuery(id+"F0.wireOp",EDGE,"E100"),sQuery(id+"F0.wireOp",EDGE,"E101"),sQuery(id+"F0.wireOp",EDGE,"E102"),sQuery(id+"F0.wireOp",EDGE,"E103"),sQuery(id+"F0.wireOp",EDGE,"E104"),sQuery(id+"F0.wireOp",EDGE,"E105"),sQuery(id+"F0.wireOp",EDGE,"E106"),sQuery(id+"F0.wireOp",EDGE,"E107"),sQuery(id+"F0.wireOp",EDGE,"E108"),sQuery(id+"F0.wireOp",EDGE,"E109"),sQuery(id+"F0.wireOp",EDGE,"E110"),sQuery(id+"F0.wireOp",EDGE,"E111"),sQuery(id+"F0.wireOp",EDGE,"E112"),sQuery(id+"F0.wireOp",EDGE,"E113"),sQuery(id+"F0.wireOp",EDGE,"E114"),sQuery(id+"F0.wireOp",EDGE,"E115"),sQuery(id+"F0.wireOp",EDGE,"E116"),sQuery(id+"F0.wireOp",EDGE,"E117"),sQuery(id+"F0.wireOp",EDGE,"E118"),sQuery(id+"F0.wireOp",EDGE,"E119"),sQuery(id+"F0.wireOp",EDGE,"E120"),sQuery(id+"F0.wireOp",EDGE,"E121"),sQuery(id+"F0.wireOp",EDGE,"E122"),sQuery(id+"F0.wireOp",EDGE,"E123"),sQuery(id+"F0.wireOp",EDGE,"E124"),sQuery(id+"F0.wireOp",EDGE,"E125"),sQuery(id+"F0.wireOp",EDGE,"E126"),sQuery(id+"F0.wireOp",EDGE,"E127"),sQuery(id+"F0.wireOp",EDGE,"E128"),sQuery(id+"F0.wireOp",EDGE,"E129"),sQuery(id+"F0.wireOp",EDGE,"E130"),sQuery(id+"F0.wireOp",EDGE,"E131"),sQuery(id+"F0.wireOp",EDGE,"E132"),sQuery(id+"F0.wireOp",EDGE,"E133"),sQuery(id+"F0.wireOp",EDGE,"E134"),sQuery(id+"F0.wireOp",EDGE,"E135"),sQuery(id+"F0.wireOp",EDGE,"E136"),sQuery(id+"F0.wireOp",EDGE,"E137"),sQuery(id+"F0.wireOp",EDGE,"E138"),sQuery(id+"F0.wireOp",EDGE,"E139"),sQuery(id+"F0.wireOp",EDGE,"E140"),sQuery(id+"F0.wireOp",EDGE,"E141"),sQuery(id+"F0.wireOp",EDGE,"E142"),sQuery(id+"F0.wireOp",EDGE,"E143"),sQuery(id+"F0.wireOp",EDGE,"E144"),sQuery(id+"F0.wireOp",EDGE,"E145"),sQuery(id+"F0.wireOp",EDGE,"E146"),sQuery(id+"F0.wireOp",EDGE,"E147"),sQuery(id+"F0.wireOp",EDGE,"E148"),sQuery(id+"F0.wireOp",EDGE,"E149"),sQuery(id+"F0.wireOp",EDGE,"E150"),sQuery(id+"F0.wireOp",EDGE,"E151"),sQuery(id+"F0.wireOp",EDGE,"E152"),sQuery(id+"F0.wireOp",EDGE,"E153"),sQuery(id+"F0.wireOp",EDGE,"E154"),sQuery(id+"F0.wireOp",EDGE,"E155"),sQuery(id+"F0.wireOp",EDGE,"E156"),sQuery(id+"F0.wireOp",EDGE,"E157"),sQuery(id+"F0.wireOp",EDGE,"E158"),sQuery(id+"F0.wireOp",EDGE,"E159"),sQuery(id+"F0.wireOp",EDGE,"E160"),sQuery(id+"F0.wireOp",EDGE,"E161"),sQuery(id+"F0.wireOp",EDGE,"E162"),sQuery(id+"F0.wireOp",EDGE,"E163"),sQuery(id+"F0.wireOp",EDGE,"E164"),sQuery(id+"F0.wireOp",EDGE,"E165"),sQuery(id+"F0.wireOp",EDGE,"E166"),sQuery(id+"F0.wireOp",EDGE,"E167"),sQuery(id+"F0.wireOp",EDGE,"E168"),sQuery(id+"F0.wireOp",EDGE,"E169"),sQuery(id+"F0.wireOp",EDGE,"E170"),sQuery(id+"F0.wireOp",EDGE,"E171"),sQuery(id+"F0.wireOp",EDGE,"E172"),sQuery(id+"F0.wireOp",EDGE,"E173"),sQuery(id+"F0.wireOp",EDGE,"E174"),sQuery(id+"F0.wireOp",EDGE,"E175"),sQuery(id+"F0.wireOp",EDGE,"E176"),sQuery(id+"F0.wireOp",EDGE,"E177"),sQuery(id+"F0.wireOp",EDGE,"E178"),sQuery(id+"F0.wireOp",EDGE,"E179"),sQuery(id+"F0.wireOp",EDGE,"E180"),sQuery(id+"F0.wireOp",EDGE,"E181"),sQuery(id+"F0.wireOp",EDGE,"E182"),sQuery(id+"F0.wireOp",EDGE,"E183"),sQuery(id+"F0.wireOp",EDGE,"E184"),sQuery(id+"F0.wireOp",EDGE,"E185"),sQuery(id+"F0.wireOp",EDGE,"E186"),sQuery(id+"F0.wireOp",EDGE,"E187"),sQuery(id+"F0.wireOp",EDGE,"E188"),sQuery(id+"F0.wireOp",EDGE,"E189"),sQuery(id+"F0.wireOp",EDGE,"E190"),sQuery(id+"F0.wireOp",EDGE,"E191"),sQuery(id+"F0.wireOp",EDGE,"E192"),sQuery(id+"F0.wireOp",EDGE,"E193"),sQuery(id+"F0.wireOp",EDGE,"E194"),sQuery(id+"F0.wireOp",EDGE,"E195"),sQuery(id+"F0.wireOp",EDGE,"E196"),sQuery(id+"F0.wireOp",EDGE,"E197"),sQuery(id+"F0.wireOp",EDGE,"E198"),sQuery(id+"F0.wireOp",EDGE,"E199"),sQuery(id+"F0.wireOp",EDGE,"E200"),sQuery(id+"F0.wireOp",EDGE,"E201"),sQuery(id+"F0.wireOp",EDGE,"E202"),sQuery(id+"F0.wireOp",EDGE,"E203"),sQuery(id+"F0.wireOp",EDGE,"E204"),sQuery(id+"F0.wireOp",EDGE,"E205"),sQuery(id+"F0.wireOp",EDGE,"E206"),sQuery(id+"F0.wireOp",EDGE,"E207"),sQuery(id+"F0.wireOp",EDGE,"E208"),sQuery(id+"F0.wireOp",EDGE,"E209"),sQuery(id+"F0.wireOp",EDGE,"E210"),sQuery(id+"F0.wireOp",EDGE,"E211"),sQuery(id+"F0.wireOp",EDGE,"E212"),sQuery(id+"F0.wireOp",EDGE,"E213"),sQuery(id+"F0.wireOp",EDGE,"E214"),sQuery(id+"F0.wireOp",EDGE,"E215"),sQuery(id+"F0.wireOp",EDGE,"E216"),sQuery(id+"F0.wireOp",EDGE,"E217"),sQuery(id+"F0.wireOp",EDGE,"E218"),sQuery(id+"F0.wireOp",EDGE,"E219"),sQuery(id+"F0.wireOp",EDGE,"E220"),sQuery(id+"F0.wireOp",EDGE,"E221"),sQuery(id+"F0.wireOp",EDGE,"E222"),sQuery(id+"F0.wireOp",EDGE,"E223"),sQuery(id+"F0.wireOp",EDGE,"E224"),sQuery(id+"F0.wireOp",EDGE,"E225"),sQuery(id+"F0.wireOp",EDGE,"E226"),sQuery(id+"F0.wireOp",EDGE,"E227"),sQuery(id+"F0.wireOp",EDGE,"E228"),sQuery(id+"F0.wireOp",EDGE,"E229"),sQuery(id+"F0.wireOp",EDGE,"E230"),sQuery(id+"F0.wireOp",EDGE,"E231"),sQuery(id+"F0.wireOp",EDGE,"E232"),sQuery(id+"F0.wireOp",EDGE,"E233"),sQuery(id+"F0.wireOp",EDGE,"E234"),sQuery(id+"F0.wireOp",EDGE,"E235"),sQuery(id+"F0.wireOp",EDGE,"E236"),sQuery(id+"F0.wireOp",EDGE,"E237"),sQuery(id+"F0.wireOp",EDGE,"E238"),sQuery(id+"F0.wireOp",EDGE,"E239"),sQuery(id+"F0.wireOp",EDGE,"E240"),sQuery(id+"F0.wireOp",EDGE,"E241"),sQuery(id+"F0.wireOp",EDGE,"E242"),sQuery(id+"F0.wireOp",EDGE,"E243"),sQuery(id+"F3.wireOp",EDGE,"E244.bottom"),sQuery(id+"F3.wireOp",EDGE,"E244.top"),sQuery(id+"F3.wireOp",EDGE,"E244.left"),sQuery(id+"F3.wireOp",EDGE,"E244.right"),sQuery(id+"F3.wireOp",EDGE,"E245.filletArc"),sQuery(id+"F3.wireOp",EDGE,"E246.filletArc"),sQuery(id+"F3.wireOp",EDGE,"E247.filletArc"),sQuery(id+"F3.wireOp",EDGE,"E248.filletArc")])],"isStart":false})}),makeQuery(id+"F8.opExtrude","CAP_FACE",FACE,{"disambiguationData":[OSD([sQuery(id+"F7.wireOp",EDGE,"E250.bottom"),sQuery(id+"F7.wireOp",EDGE,"E250.top"),sQuery(id+"F7.wireOp",EDGE,"E250.left"),sQuery(id+"F7.wireOp",EDGE,"E250.right")])],"isStart":false})]})});
            var Q6;
            Q6=makeQuery(id+"F12.boolean.opBoolean","SPLIT",FACE,{"disambiguationData":[TD([makeQuery(id+"F12.opExtrude","SWEPT_FACE",FACE,{"disambiguationData":[OSD([sQuery(id+"F11.wireOp",EDGE,"E274")])]})])],"derivedFrom":makeQuery(id+"F8.boolean.opBoolean","MERGE",FACE,{"derivedFrom":[makeQuery(id+"F4.boolean.opBoolean","COPY",FACE,{"derivedFrom":makeQuery(id+"F4.opExtrude","CAP_FACE",FACE,{"disambiguationData":[OSD([sQuery(id+"F0.wireOp",EDGE,"E4"),sQuery(id+"F0.wireOp",EDGE,"E5"),sQuery(id+"F0.wireOp",EDGE,"E6"),sQuery(id+"F0.wireOp",EDGE,"E7"),sQuery(id+"F0.wireOp",EDGE,"E8"),sQuery(id+"F0.wireOp",EDGE,"E9"),sQuery(id+"F0.wireOp",EDGE,"E10"),sQuery(id+"F0.wireOp",EDGE,"E11"),sQuery(id+"F0.wireOp",EDGE,"E12"),sQuery(id+"F0.wireOp",EDGE,"E13"),sQuery(id+"F0.wireOp",EDGE,"E14"),sQuery(id+"F0.wireOp",EDGE,"E15"),sQuery(id+"F0.wireOp",EDGE,"E16"),sQuery(id+"F0.wireOp",EDGE,"E17"),sQuery(id+"F0.wireOp",EDGE,"E18"),sQuery(id+"F0.wireOp",EDGE,"E19"),sQuery(id+"F0.wireOp",EDGE,"E20"),sQuery(id+"F0.wireOp",EDGE,"E21"),sQuery(id+"F0.wireOp",EDGE,"E22"),sQuery(id+"F0.wireOp",EDGE,"E23"),sQuery(id+"F0.wireOp",EDGE,"E24"),sQuery(id+"F0.wireOp",EDGE,"E25"),sQuery(id+"F0.wireOp",EDGE,"E26"),sQuery(id+"F0.wireOp",EDGE,"E27"),sQuery(id+"F0.wireOp",EDGE,"E28"),sQuery(id+"F0.wireOp",EDGE,"E29"),sQuery(id+"F0.wireOp",EDGE,"E30"),sQuery(id+"F0.wireOp",EDGE,"E31"),sQuery(id+"F0.wireOp",EDGE,"E32"),sQuery(id+"F0.wireOp",EDGE,"E33"),sQuery(id+"F0.wireOp",EDGE,"E34"),sQuery(id+"F0.wireOp",EDGE,"E35"),sQuery(id+"F0.wireOp",EDGE,"E36"),sQuery(id+"F0.wireOp",EDGE,"E37"),sQuery(id+"F0.wireOp",EDGE,"E38"),sQuery(id+"F0.wireOp",EDGE,"E39"),sQuery(id+"F0.wireOp",EDGE,"E40"),sQuery(id+"F0.wireOp",EDGE,"E41"),sQuery(id+"F0.wireOp",EDGE,"E42"),sQuery(id+"F0.wireOp",EDGE,"E43"),sQuery(id+"F0.wireOp",EDGE,"E44"),sQuery(id+"F0.wireOp",EDGE,"E45"),sQuery(id+"F0.wireOp",EDGE,"E46"),sQuery(id+"F0.wireOp",EDGE,"E47"),sQuery(id+"F0.wireOp",EDGE,"E48"),sQuery(id+"F0.wireOp",EDGE,"E49"),sQuery(id+"F0.wireOp",EDGE,"E50"),sQuery(id+"F0.wireOp",EDGE,"E51"),sQuery(id+"F0.wireOp",EDGE,"E52"),sQuery(id+"F0.wireOp",EDGE,"E53"),sQuery(id+"F0.wireOp",EDGE,"E54"),sQuery(id+"F0.wireOp",EDGE,"E55"),sQuery(id+"F0.wireOp",EDGE,"E56"),sQuery(id+"F0.wireOp",EDGE,"E57"),sQuery(id+"F0.wireOp",EDGE,"E58"),sQuery(id+"F0.wireOp",EDGE,"E59"),sQuery(id+"F0.wireOp",EDGE,"E60"),sQuery(id+"F0.wireOp",EDGE,"E61"),sQuery(id+"F0.wireOp",EDGE,"E62"),sQuery(id+"F0.wireOp",EDGE,"E63"),sQuery(id+"F0.wireOp",EDGE,"E64"),sQuery(id+"F0.wireOp",EDGE,"E65"),sQuery(id+"F0.wireOp",EDGE,"E66"),sQuery(id+"F0.wireOp",EDGE,"E67"),sQuery(id+"F0.wireOp",EDGE,"E68"),sQuery(id+"F0.wireOp",EDGE,"E69"),sQuery(id+"F0.wireOp",EDGE,"E70"),sQuery(id+"F0.wireOp",EDGE,"E71"),sQuery(id+"F0.wireOp",EDGE,"E72"),sQuery(id+"F0.wireOp",EDGE,"E73"),sQuery(id+"F0.wireOp",EDGE,"E74"),sQuery(id+"F0.wireOp",EDGE,"E75"),sQuery(id+"F0.wireOp",EDGE,"E76"),sQuery(id+"F0.wireOp",EDGE,"E77"),sQuery(id+"F0.wireOp",EDGE,"E78"),sQuery(id+"F0.wireOp",EDGE,"E79"),sQuery(id+"F0.wireOp",EDGE,"E80"),sQuery(id+"F0.wireOp",EDGE,"E81"),sQuery(id+"F0.wireOp",EDGE,"E82"),sQuery(id+"F0.wireOp",EDGE,"E83"),sQuery(id+"F0.wireOp",EDGE,"E84"),sQuery(id+"F0.wireOp",EDGE,"E85"),sQuery(id+"F0.wireOp",EDGE,"E86"),sQuery(id+"F0.wireOp",EDGE,"E87"),sQuery(id+"F0.wireOp",EDGE,"E88"),sQuery(id+"F0.wireOp",EDGE,"E89"),sQuery(id+"F0.wireOp",EDGE,"E90"),sQuery(id+"F0.wireOp",EDGE,"E91"),sQuery(id+"F0.wireOp",EDGE,"E92"),sQuery(id+"F0.wireOp",EDGE,"E93"),sQuery(id+"F0.wireOp",EDGE,"E94"),sQuery(id+"F0.wireOp",EDGE,"E95"),sQuery(id+"F0.wireOp",EDGE,"E96"),sQuery(id+"F0.wireOp",EDGE,"E97"),sQuery(id+"F0.wireOp",EDGE,"E98"),sQuery(id+"F0.wireOp",EDGE,"E99"),sQuery(id+"F0.wireOp",EDGE,"E100"),sQuery(id+"F0.wireOp",EDGE,"E101"),sQuery(id+"F0.wireOp",EDGE,"E102"),sQuery(id+"F0.wireOp",EDGE,"E103"),sQuery(id+"F0.wireOp",EDGE,"E104"),sQuery(id+"F0.wireOp",EDGE,"E105"),sQuery(id+"F0.wireOp",EDGE,"E106"),sQuery(id+"F0.wireOp",EDGE,"E107"),sQuery(id+"F0.wireOp",EDGE,"E108"),sQuery(id+"F0.wireOp",EDGE,"E109"),sQuery(id+"F0.wireOp",EDGE,"E110"),sQuery(id+"F0.wireOp",EDGE,"E111"),sQuery(id+"F0.wireOp",EDGE,"E112"),sQuery(id+"F0.wireOp",EDGE,"E113"),sQuery(id+"F0.wireOp",EDGE,"E114"),sQuery(id+"F0.wireOp",EDGE,"E115"),sQuery(id+"F0.wireOp",EDGE,"E116"),sQuery(id+"F0.wireOp",EDGE,"E117"),sQuery(id+"F0.wireOp",EDGE,"E118"),sQuery(id+"F0.wireOp",EDGE,"E119"),sQuery(id+"F0.wireOp",EDGE,"E120"),sQuery(id+"F0.wireOp",EDGE,"E121"),sQuery(id+"F0.wireOp",EDGE,"E122"),sQuery(id+"F0.wireOp",EDGE,"E123"),sQuery(id+"F0.wireOp",EDGE,"E124"),sQuery(id+"F0.wireOp",EDGE,"E125"),sQuery(id+"F0.wireOp",EDGE,"E126"),sQuery(id+"F0.wireOp",EDGE,"E127"),sQuery(id+"F0.wireOp",EDGE,"E128"),sQuery(id+"F0.wireOp",EDGE,"E129"),sQuery(id+"F0.wireOp",EDGE,"E130"),sQuery(id+"F0.wireOp",EDGE,"E131"),sQuery(id+"F0.wireOp",EDGE,"E132"),sQuery(id+"F0.wireOp",EDGE,"E133"),sQuery(id+"F0.wireOp",EDGE,"E134"),sQuery(id+"F0.wireOp",EDGE,"E135"),sQuery(id+"F0.wireOp",EDGE,"E136"),sQuery(id+"F0.wireOp",EDGE,"E137"),sQuery(id+"F0.wireOp",EDGE,"E138"),sQuery(id+"F0.wireOp",EDGE,"E139"),sQuery(id+"F0.wireOp",EDGE,"E140"),sQuery(id+"F0.wireOp",EDGE,"E141"),sQuery(id+"F0.wireOp",EDGE,"E142"),sQuery(id+"F0.wireOp",EDGE,"E143"),sQuery(id+"F0.wireOp",EDGE,"E144"),sQuery(id+"F0.wireOp",EDGE,"E145"),sQuery(id+"F0.wireOp",EDGE,"E146"),sQuery(id+"F0.wireOp",EDGE,"E147"),sQuery(id+"F0.wireOp",EDGE,"E148"),sQuery(id+"F0.wireOp",EDGE,"E149"),sQuery(id+"F0.wireOp",EDGE,"E150"),sQuery(id+"F0.wireOp",EDGE,"E151"),sQuery(id+"F0.wireOp",EDGE,"E152"),sQuery(id+"F0.wireOp",EDGE,"E153"),sQuery(id+"F0.wireOp",EDGE,"E154"),sQuery(id+"F0.wireOp",EDGE,"E155"),sQuery(id+"F0.wireOp",EDGE,"E156"),sQuery(id+"F0.wireOp",EDGE,"E157"),sQuery(id+"F0.wireOp",EDGE,"E158"),sQuery(id+"F0.wireOp",EDGE,"E159"),sQuery(id+"F0.wireOp",EDGE,"E160"),sQuery(id+"F0.wireOp",EDGE,"E161"),sQuery(id+"F0.wireOp",EDGE,"E162"),sQuery(id+"F0.wireOp",EDGE,"E163"),sQuery(id+"F0.wireOp",EDGE,"E164"),sQuery(id+"F0.wireOp",EDGE,"E165"),sQuery(id+"F0.wireOp",EDGE,"E166"),sQuery(id+"F0.wireOp",EDGE,"E167"),sQuery(id+"F0.wireOp",EDGE,"E168"),sQuery(id+"F0.wireOp",EDGE,"E169"),sQuery(id+"F0.wireOp",EDGE,"E170"),sQuery(id+"F0.wireOp",EDGE,"E171"),sQuery(id+"F0.wireOp",EDGE,"E172"),sQuery(id+"F0.wireOp",EDGE,"E173"),sQuery(id+"F0.wireOp",EDGE,"E174"),sQuery(id+"F0.wireOp",EDGE,"E175"),sQuery(id+"F0.wireOp",EDGE,"E176"),sQuery(id+"F0.wireOp",EDGE,"E177"),sQuery(id+"F0.wireOp",EDGE,"E178"),sQuery(id+"F0.wireOp",EDGE,"E179"),sQuery(id+"F0.wireOp",EDGE,"E180"),sQuery(id+"F0.wireOp",EDGE,"E181"),sQuery(id+"F0.wireOp",EDGE,"E182"),sQuery(id+"F0.wireOp",EDGE,"E183"),sQuery(id+"F0.wireOp",EDGE,"E184"),sQuery(id+"F0.wireOp",EDGE,"E185"),sQuery(id+"F0.wireOp",EDGE,"E186"),sQuery(id+"F0.wireOp",EDGE,"E187"),sQuery(id+"F0.wireOp",EDGE,"E188"),sQuery(id+"F0.wireOp",EDGE,"E189"),sQuery(id+"F0.wireOp",EDGE,"E190"),sQuery(id+"F0.wireOp",EDGE,"E191"),sQuery(id+"F0.wireOp",EDGE,"E192"),sQuery(id+"F0.wireOp",EDGE,"E193"),sQuery(id+"F0.wireOp",EDGE,"E194"),sQuery(id+"F0.wireOp",EDGE,"E195"),sQuery(id+"F0.wireOp",EDGE,"E196"),sQuery(id+"F0.wireOp",EDGE,"E197"),sQuery(id+"F0.wireOp",EDGE,"E198"),sQuery(id+"F0.wireOp",EDGE,"E199"),sQuery(id+"F0.wireOp",EDGE,"E200"),sQuery(id+"F0.wireOp",EDGE,"E201"),sQuery(id+"F0.wireOp",EDGE,"E202"),sQuery(id+"F0.wireOp",EDGE,"E203"),sQuery(id+"F0.wireOp",EDGE,"E204"),sQuery(id+"F0.wireOp",EDGE,"E205"),sQuery(id+"F0.wireOp",EDGE,"E206"),sQuery(id+"F0.wireOp",EDGE,"E207"),sQuery(id+"F0.wireOp",EDGE,"E208"),sQuery(id+"F0.wireOp",EDGE,"E209"),sQuery(id+"F0.wireOp",EDGE,"E210"),sQuery(id+"F0.wireOp",EDGE,"E211"),sQuery(id+"F0.wireOp",EDGE,"E212"),sQuery(id+"F0.wireOp",EDGE,"E213"),sQuery(id+"F0.wireOp",EDGE,"E214"),sQuery(id+"F0.wireOp",EDGE,"E215"),sQuery(id+"F0.wireOp",EDGE,"E216"),sQuery(id+"F0.wireOp",EDGE,"E217"),sQuery(id+"F0.wireOp",EDGE,"E218"),sQuery(id+"F0.wireOp",EDGE,"E219"),sQuery(id+"F0.wireOp",EDGE,"E220"),sQuery(id+"F0.wireOp",EDGE,"E221"),sQuery(id+"F0.wireOp",EDGE,"E222"),sQuery(id+"F0.wireOp",EDGE,"E223"),sQuery(id+"F0.wireOp",EDGE,"E224"),sQuery(id+"F0.wireOp",EDGE,"E225"),sQuery(id+"F0.wireOp",EDGE,"E226"),sQuery(id+"F0.wireOp",EDGE,"E227"),sQuery(id+"F0.wireOp",EDGE,"E228"),sQuery(id+"F0.wireOp",EDGE,"E229"),sQuery(id+"F0.wireOp",EDGE,"E230"),sQuery(id+"F0.wireOp",EDGE,"E231"),sQuery(id+"F0.wireOp",EDGE,"E232"),sQuery(id+"F0.wireOp",EDGE,"E233"),sQuery(id+"F0.wireOp",EDGE,"E234"),sQuery(id+"F0.wireOp",EDGE,"E235"),sQuery(id+"F0.wireOp",EDGE,"E236"),sQuery(id+"F0.wireOp",EDGE,"E237"),sQuery(id+"F0.wireOp",EDGE,"E238"),sQuery(id+"F0.wireOp",EDGE,"E239"),sQuery(id+"F0.wireOp",EDGE,"E240"),sQuery(id+"F0.wireOp",EDGE,"E241"),sQuery(id+"F0.wireOp",EDGE,"E242"),sQuery(id+"F0.wireOp",EDGE,"E243"),sQuery(id+"F3.wireOp",EDGE,"E244.bottom"),sQuery(id+"F3.wireOp",EDGE,"E244.top"),sQuery(id+"F3.wireOp",EDGE,"E244.left"),sQuery(id+"F3.wireOp",EDGE,"E244.right"),sQuery(id+"F3.wireOp",EDGE,"E245.filletArc"),sQuery(id+"F3.wireOp",EDGE,"E246.filletArc"),sQuery(id+"F3.wireOp",EDGE,"E247.filletArc"),sQuery(id+"F3.wireOp",EDGE,"E248.filletArc")])],"isStart":false})}),makeQuery(id+"F8.opExtrude","CAP_FACE",FACE,{"disambiguationData":[OSD([sQuery(id+"F7.wireOp",EDGE,"E250.bottom"),sQuery(id+"F7.wireOp",EDGE,"E250.top"),sQuery(id+"F7.wireOp",EDGE,"E250.left"),sQuery(id+"F7.wireOp",EDGE,"E250.right")])],"isStart":false})]})});
            var Q7;
            Q7=makeQuery(id+"F12.boolean.opBoolean","SPLIT",FACE,{"disambiguationData":[TD([makeQuery(id+"F12.opExtrude","SWEPT_FACE",FACE,{"disambiguationData":[OSD([sQuery(id+"F11.wireOp",EDGE,"E275")])]})])],"derivedFrom":makeQuery(id+"F8.boolean.opBoolean","MERGE",FACE,{"derivedFrom":[makeQuery(id+"F4.boolean.opBoolean","COPY",FACE,{"derivedFrom":makeQuery(id+"F4.opExtrude","CAP_FACE",FACE,{"disambiguationData":[OSD([sQuery(id+"F0.wireOp",EDGE,"E4"),sQuery(id+"F0.wireOp",EDGE,"E5"),sQuery(id+"F0.wireOp",EDGE,"E6"),sQuery(id+"F0.wireOp",EDGE,"E7"),sQuery(id+"F0.wireOp",EDGE,"E8"),sQuery(id+"F0.wireOp",EDGE,"E9"),sQuery(id+"F0.wireOp",EDGE,"E10"),sQuery(id+"F0.wireOp",EDGE,"E11"),sQuery(id+"F0.wireOp",EDGE,"E12"),sQuery(id+"F0.wireOp",EDGE,"E13"),sQuery(id+"F0.wireOp",EDGE,"E14"),sQuery(id+"F0.wireOp",EDGE,"E15"),sQuery(id+"F0.wireOp",EDGE,"E16"),sQuery(id+"F0.wireOp",EDGE,"E17"),sQuery(id+"F0.wireOp",EDGE,"E18"),sQuery(id+"F0.wireOp",EDGE,"E19"),sQuery(id+"F0.wireOp",EDGE,"E20"),sQuery(id+"F0.wireOp",EDGE,"E21"),sQuery(id+"F0.wireOp",EDGE,"E22"),sQuery(id+"F0.wireOp",EDGE,"E23"),sQuery(id+"F0.wireOp",EDGE,"E24"),sQuery(id+"F0.wireOp",EDGE,"E25"),sQuery(id+"F0.wireOp",EDGE,"E26"),sQuery(id+"F0.wireOp",EDGE,"E27"),sQuery(id+"F0.wireOp",EDGE,"E28"),sQuery(id+"F0.wireOp",EDGE,"E29"),sQuery(id+"F0.wireOp",EDGE,"E30"),sQuery(id+"F0.wireOp",EDGE,"E31"),sQuery(id+"F0.wireOp",EDGE,"E32"),sQuery(id+"F0.wireOp",EDGE,"E33"),sQuery(id+"F0.wireOp",EDGE,"E34"),sQuery(id+"F0.wireOp",EDGE,"E35"),sQuery(id+"F0.wireOp",EDGE,"E36"),sQuery(id+"F0.wireOp",EDGE,"E37"),sQuery(id+"F0.wireOp",EDGE,"E38"),sQuery(id+"F0.wireOp",EDGE,"E39"),sQuery(id+"F0.wireOp",EDGE,"E40"),sQuery(id+"F0.wireOp",EDGE,"E41"),sQuery(id+"F0.wireOp",EDGE,"E42"),sQuery(id+"F0.wireOp",EDGE,"E43"),sQuery(id+"F0.wireOp",EDGE,"E44"),sQuery(id+"F0.wireOp",EDGE,"E45"),sQuery(id+"F0.wireOp",EDGE,"E46"),sQuery(id+"F0.wireOp",EDGE,"E47"),sQuery(id+"F0.wireOp",EDGE,"E48"),sQuery(id+"F0.wireOp",EDGE,"E49"),sQuery(id+"F0.wireOp",EDGE,"E50"),sQuery(id+"F0.wireOp",EDGE,"E51"),sQuery(id+"F0.wireOp",EDGE,"E52"),sQuery(id+"F0.wireOp",EDGE,"E53"),sQuery(id+"F0.wireOp",EDGE,"E54"),sQuery(id+"F0.wireOp",EDGE,"E55"),sQuery(id+"F0.wireOp",EDGE,"E56"),sQuery(id+"F0.wireOp",EDGE,"E57"),sQuery(id+"F0.wireOp",EDGE,"E58"),sQuery(id+"F0.wireOp",EDGE,"E59"),sQuery(id+"F0.wireOp",EDGE,"E60"),sQuery(id+"F0.wireOp",EDGE,"E61"),sQuery(id+"F0.wireOp",EDGE,"E62"),sQuery(id+"F0.wireOp",EDGE,"E63"),sQuery(id+"F0.wireOp",EDGE,"E64"),sQuery(id+"F0.wireOp",EDGE,"E65"),sQuery(id+"F0.wireOp",EDGE,"E66"),sQuery(id+"F0.wireOp",EDGE,"E67"),sQuery(id+"F0.wireOp",EDGE,"E68"),sQuery(id+"F0.wireOp",EDGE,"E69"),sQuery(id+"F0.wireOp",EDGE,"E70"),sQuery(id+"F0.wireOp",EDGE,"E71"),sQuery(id+"F0.wireOp",EDGE,"E72"),sQuery(id+"F0.wireOp",EDGE,"E73"),sQuery(id+"F0.wireOp",EDGE,"E74"),sQuery(id+"F0.wireOp",EDGE,"E75"),sQuery(id+"F0.wireOp",EDGE,"E76"),sQuery(id+"F0.wireOp",EDGE,"E77"),sQuery(id+"F0.wireOp",EDGE,"E78"),sQuery(id+"F0.wireOp",EDGE,"E79"),sQuery(id+"F0.wireOp",EDGE,"E80"),sQuery(id+"F0.wireOp",EDGE,"E81"),sQuery(id+"F0.wireOp",EDGE,"E82"),sQuery(id+"F0.wireOp",EDGE,"E83"),sQuery(id+"F0.wireOp",EDGE,"E84"),sQuery(id+"F0.wireOp",EDGE,"E85"),sQuery(id+"F0.wireOp",EDGE,"E86"),sQuery(id+"F0.wireOp",EDGE,"E87"),sQuery(id+"F0.wireOp",EDGE,"E88"),sQuery(id+"F0.wireOp",EDGE,"E89"),sQuery(id+"F0.wireOp",EDGE,"E90"),sQuery(id+"F0.wireOp",EDGE,"E91"),sQuery(id+"F0.wireOp",EDGE,"E92"),sQuery(id+"F0.wireOp",EDGE,"E93"),sQuery(id+"F0.wireOp",EDGE,"E94"),sQuery(id+"F0.wireOp",EDGE,"E95"),sQuery(id+"F0.wireOp",EDGE,"E96"),sQuery(id+"F0.wireOp",EDGE,"E97"),sQuery(id+"F0.wireOp",EDGE,"E98"),sQuery(id+"F0.wireOp",EDGE,"E99"),sQuery(id+"F0.wireOp",EDGE,"E100"),sQuery(id+"F0.wireOp",EDGE,"E101"),sQuery(id+"F0.wireOp",EDGE,"E102"),sQuery(id+"F0.wireOp",EDGE,"E103"),sQuery(id+"F0.wireOp",EDGE,"E104"),sQuery(id+"F0.wireOp",EDGE,"E105"),sQuery(id+"F0.wireOp",EDGE,"E106"),sQuery(id+"F0.wireOp",EDGE,"E107"),sQuery(id+"F0.wireOp",EDGE,"E108"),sQuery(id+"F0.wireOp",EDGE,"E109"),sQuery(id+"F0.wireOp",EDGE,"E110"),sQuery(id+"F0.wireOp",EDGE,"E111"),sQuery(id+"F0.wireOp",EDGE,"E112"),sQuery(id+"F0.wireOp",EDGE,"E113"),sQuery(id+"F0.wireOp",EDGE,"E114"),sQuery(id+"F0.wireOp",EDGE,"E115"),sQuery(id+"F0.wireOp",EDGE,"E116"),sQuery(id+"F0.wireOp",EDGE,"E117"),sQuery(id+"F0.wireOp",EDGE,"E118"),sQuery(id+"F0.wireOp",EDGE,"E119"),sQuery(id+"F0.wireOp",EDGE,"E120"),sQuery(id+"F0.wireOp",EDGE,"E121"),sQuery(id+"F0.wireOp",EDGE,"E122"),sQuery(id+"F0.wireOp",EDGE,"E123"),sQuery(id+"F0.wireOp",EDGE,"E124"),sQuery(id+"F0.wireOp",EDGE,"E125"),sQuery(id+"F0.wireOp",EDGE,"E126"),sQuery(id+"F0.wireOp",EDGE,"E127"),sQuery(id+"F0.wireOp",EDGE,"E128"),sQuery(id+"F0.wireOp",EDGE,"E129"),sQuery(id+"F0.wireOp",EDGE,"E130"),sQuery(id+"F0.wireOp",EDGE,"E131"),sQuery(id+"F0.wireOp",EDGE,"E132"),sQuery(id+"F0.wireOp",EDGE,"E133"),sQuery(id+"F0.wireOp",EDGE,"E134"),sQuery(id+"F0.wireOp",EDGE,"E135"),sQuery(id+"F0.wireOp",EDGE,"E136"),sQuery(id+"F0.wireOp",EDGE,"E137"),sQuery(id+"F0.wireOp",EDGE,"E138"),sQuery(id+"F0.wireOp",EDGE,"E139"),sQuery(id+"F0.wireOp",EDGE,"E140"),sQuery(id+"F0.wireOp",EDGE,"E141"),sQuery(id+"F0.wireOp",EDGE,"E142"),sQuery(id+"F0.wireOp",EDGE,"E143"),sQuery(id+"F0.wireOp",EDGE,"E144"),sQuery(id+"F0.wireOp",EDGE,"E145"),sQuery(id+"F0.wireOp",EDGE,"E146"),sQuery(id+"F0.wireOp",EDGE,"E147"),sQuery(id+"F0.wireOp",EDGE,"E148"),sQuery(id+"F0.wireOp",EDGE,"E149"),sQuery(id+"F0.wireOp",EDGE,"E150"),sQuery(id+"F0.wireOp",EDGE,"E151"),sQuery(id+"F0.wireOp",EDGE,"E152"),sQuery(id+"F0.wireOp",EDGE,"E153"),sQuery(id+"F0.wireOp",EDGE,"E154"),sQuery(id+"F0.wireOp",EDGE,"E155"),sQuery(id+"F0.wireOp",EDGE,"E156"),sQuery(id+"F0.wireOp",EDGE,"E157"),sQuery(id+"F0.wireOp",EDGE,"E158"),sQuery(id+"F0.wireOp",EDGE,"E159"),sQuery(id+"F0.wireOp",EDGE,"E160"),sQuery(id+"F0.wireOp",EDGE,"E161"),sQuery(id+"F0.wireOp",EDGE,"E162"),sQuery(id+"F0.wireOp",EDGE,"E163"),sQuery(id+"F0.wireOp",EDGE,"E164"),sQuery(id+"F0.wireOp",EDGE,"E165"),sQuery(id+"F0.wireOp",EDGE,"E166"),sQuery(id+"F0.wireOp",EDGE,"E167"),sQuery(id+"F0.wireOp",EDGE,"E168"),sQuery(id+"F0.wireOp",EDGE,"E169"),sQuery(id+"F0.wireOp",EDGE,"E170"),sQuery(id+"F0.wireOp",EDGE,"E171"),sQuery(id+"F0.wireOp",EDGE,"E172"),sQuery(id+"F0.wireOp",EDGE,"E173"),sQuery(id+"F0.wireOp",EDGE,"E174"),sQuery(id+"F0.wireOp",EDGE,"E175"),sQuery(id+"F0.wireOp",EDGE,"E176"),sQuery(id+"F0.wireOp",EDGE,"E177"),sQuery(id+"F0.wireOp",EDGE,"E178"),sQuery(id+"F0.wireOp",EDGE,"E179"),sQuery(id+"F0.wireOp",EDGE,"E180"),sQuery(id+"F0.wireOp",EDGE,"E181"),sQuery(id+"F0.wireOp",EDGE,"E182"),sQuery(id+"F0.wireOp",EDGE,"E183"),sQuery(id+"F0.wireOp",EDGE,"E184"),sQuery(id+"F0.wireOp",EDGE,"E185"),sQuery(id+"F0.wireOp",EDGE,"E186"),sQuery(id+"F0.wireOp",EDGE,"E187"),sQuery(id+"F0.wireOp",EDGE,"E188"),sQuery(id+"F0.wireOp",EDGE,"E189"),sQuery(id+"F0.wireOp",EDGE,"E190"),sQuery(id+"F0.wireOp",EDGE,"E191"),sQuery(id+"F0.wireOp",EDGE,"E192"),sQuery(id+"F0.wireOp",EDGE,"E193"),sQuery(id+"F0.wireOp",EDGE,"E194"),sQuery(id+"F0.wireOp",EDGE,"E195"),sQuery(id+"F0.wireOp",EDGE,"E196"),sQuery(id+"F0.wireOp",EDGE,"E197"),sQuery(id+"F0.wireOp",EDGE,"E198"),sQuery(id+"F0.wireOp",EDGE,"E199"),sQuery(id+"F0.wireOp",EDGE,"E200"),sQuery(id+"F0.wireOp",EDGE,"E201"),sQuery(id+"F0.wireOp",EDGE,"E202"),sQuery(id+"F0.wireOp",EDGE,"E203"),sQuery(id+"F0.wireOp",EDGE,"E204"),sQuery(id+"F0.wireOp",EDGE,"E205"),sQuery(id+"F0.wireOp",EDGE,"E206"),sQuery(id+"F0.wireOp",EDGE,"E207"),sQuery(id+"F0.wireOp",EDGE,"E208"),sQuery(id+"F0.wireOp",EDGE,"E209"),sQuery(id+"F0.wireOp",EDGE,"E210"),sQuery(id+"F0.wireOp",EDGE,"E211"),sQuery(id+"F0.wireOp",EDGE,"E212"),sQuery(id+"F0.wireOp",EDGE,"E213"),sQuery(id+"F0.wireOp",EDGE,"E214"),sQuery(id+"F0.wireOp",EDGE,"E215"),sQuery(id+"F0.wireOp",EDGE,"E216"),sQuery(id+"F0.wireOp",EDGE,"E217"),sQuery(id+"F0.wireOp",EDGE,"E218"),sQuery(id+"F0.wireOp",EDGE,"E219"),sQuery(id+"F0.wireOp",EDGE,"E220"),sQuery(id+"F0.wireOp",EDGE,"E221"),sQuery(id+"F0.wireOp",EDGE,"E222"),sQuery(id+"F0.wireOp",EDGE,"E223"),sQuery(id+"F0.wireOp",EDGE,"E224"),sQuery(id+"F0.wireOp",EDGE,"E225"),sQuery(id+"F0.wireOp",EDGE,"E226"),sQuery(id+"F0.wireOp",EDGE,"E227"),sQuery(id+"F0.wireOp",EDGE,"E228"),sQuery(id+"F0.wireOp",EDGE,"E229"),sQuery(id+"F0.wireOp",EDGE,"E230"),sQuery(id+"F0.wireOp",EDGE,"E231"),sQuery(id+"F0.wireOp",EDGE,"E232"),sQuery(id+"F0.wireOp",EDGE,"E233"),sQuery(id+"F0.wireOp",EDGE,"E234"),sQuery(id+"F0.wireOp",EDGE,"E235"),sQuery(id+"F0.wireOp",EDGE,"E236"),sQuery(id+"F0.wireOp",EDGE,"E237"),sQuery(id+"F0.wireOp",EDGE,"E238"),sQuery(id+"F0.wireOp",EDGE,"E239"),sQuery(id+"F0.wireOp",EDGE,"E240"),sQuery(id+"F0.wireOp",EDGE,"E241"),sQuery(id+"F0.wireOp",EDGE,"E242"),sQuery(id+"F0.wireOp",EDGE,"E243"),sQuery(id+"F3.wireOp",EDGE,"E244.bottom"),sQuery(id+"F3.wireOp",EDGE,"E244.top"),sQuery(id+"F3.wireOp",EDGE,"E244.left"),sQuery(id+"F3.wireOp",EDGE,"E244.right"),sQuery(id+"F3.wireOp",EDGE,"E245.filletArc"),sQuery(id+"F3.wireOp",EDGE,"E246.filletArc"),sQuery(id+"F3.wireOp",EDGE,"E247.filletArc"),sQuery(id+"F3.wireOp",EDGE,"E248.filletArc")])],"isStart":false})}),makeQuery(id+"F8.opExtrude","CAP_FACE",FACE,{"disambiguationData":[OSD([sQuery(id+"F7.wireOp",EDGE,"E250.bottom"),sQuery(id+"F7.wireOp",EDGE,"E250.top"),sQuery(id+"F7.wireOp",EDGE,"E250.left"),sQuery(id+"F7.wireOp",EDGE,"E250.right")])],"isStart":false})]})});
            var Q8;
            Q8=makeQuery(id+"F12.boolean.opBoolean","SPLIT",FACE,{"disambiguationData":[TD([makeQuery(id+"F12.opExtrude","SWEPT_FACE",FACE,{"disambiguationData":[OSD([sQuery(id+"F11.wireOp",EDGE,"E273")])]})])],"derivedFrom":makeQuery(id+"F8.boolean.opBoolean","MERGE",FACE,{"derivedFrom":[makeQuery(id+"F4.boolean.opBoolean","COPY",FACE,{"derivedFrom":makeQuery(id+"F4.opExtrude","CAP_FACE",FACE,{"disambiguationData":[OSD([sQuery(id+"F0.wireOp",EDGE,"E4"),sQuery(id+"F0.wireOp",EDGE,"E5"),sQuery(id+"F0.wireOp",EDGE,"E6"),sQuery(id+"F0.wireOp",EDGE,"E7"),sQuery(id+"F0.wireOp",EDGE,"E8"),sQuery(id+"F0.wireOp",EDGE,"E9"),sQuery(id+"F0.wireOp",EDGE,"E10"),sQuery(id+"F0.wireOp",EDGE,"E11"),sQuery(id+"F0.wireOp",EDGE,"E12"),sQuery(id+"F0.wireOp",EDGE,"E13"),sQuery(id+"F0.wireOp",EDGE,"E14"),sQuery(id+"F0.wireOp",EDGE,"E15"),sQuery(id+"F0.wireOp",EDGE,"E16"),sQuery(id+"F0.wireOp",EDGE,"E17"),sQuery(id+"F0.wireOp",EDGE,"E18"),sQuery(id+"F0.wireOp",EDGE,"E19"),sQuery(id+"F0.wireOp",EDGE,"E20"),sQuery(id+"F0.wireOp",EDGE,"E21"),sQuery(id+"F0.wireOp",EDGE,"E22"),sQuery(id+"F0.wireOp",EDGE,"E23"),sQuery(id+"F0.wireOp",EDGE,"E24"),sQuery(id+"F0.wireOp",EDGE,"E25"),sQuery(id+"F0.wireOp",EDGE,"E26"),sQuery(id+"F0.wireOp",EDGE,"E27"),sQuery(id+"F0.wireOp",EDGE,"E28"),sQuery(id+"F0.wireOp",EDGE,"E29"),sQuery(id+"F0.wireOp",EDGE,"E30"),sQuery(id+"F0.wireOp",EDGE,"E31"),sQuery(id+"F0.wireOp",EDGE,"E32"),sQuery(id+"F0.wireOp",EDGE,"E33"),sQuery(id+"F0.wireOp",EDGE,"E34"),sQuery(id+"F0.wireOp",EDGE,"E35"),sQuery(id+"F0.wireOp",EDGE,"E36"),sQuery(id+"F0.wireOp",EDGE,"E37"),sQuery(id+"F0.wireOp",EDGE,"E38"),sQuery(id+"F0.wireOp",EDGE,"E39"),sQuery(id+"F0.wireOp",EDGE,"E40"),sQuery(id+"F0.wireOp",EDGE,"E41"),sQuery(id+"F0.wireOp",EDGE,"E42"),sQuery(id+"F0.wireOp",EDGE,"E43"),sQuery(id+"F0.wireOp",EDGE,"E44"),sQuery(id+"F0.wireOp",EDGE,"E45"),sQuery(id+"F0.wireOp",EDGE,"E46"),sQuery(id+"F0.wireOp",EDGE,"E47"),sQuery(id+"F0.wireOp",EDGE,"E48"),sQuery(id+"F0.wireOp",EDGE,"E49"),sQuery(id+"F0.wireOp",EDGE,"E50"),sQuery(id+"F0.wireOp",EDGE,"E51"),sQuery(id+"F0.wireOp",EDGE,"E52"),sQuery(id+"F0.wireOp",EDGE,"E53"),sQuery(id+"F0.wireOp",EDGE,"E54"),sQuery(id+"F0.wireOp",EDGE,"E55"),sQuery(id+"F0.wireOp",EDGE,"E56"),sQuery(id+"F0.wireOp",EDGE,"E57"),sQuery(id+"F0.wireOp",EDGE,"E58"),sQuery(id+"F0.wireOp",EDGE,"E59"),sQuery(id+"F0.wireOp",EDGE,"E60"),sQuery(id+"F0.wireOp",EDGE,"E61"),sQuery(id+"F0.wireOp",EDGE,"E62"),sQuery(id+"F0.wireOp",EDGE,"E63"),sQuery(id+"F0.wireOp",EDGE,"E64"),sQuery(id+"F0.wireOp",EDGE,"E65"),sQuery(id+"F0.wireOp",EDGE,"E66"),sQuery(id+"F0.wireOp",EDGE,"E67"),sQuery(id+"F0.wireOp",EDGE,"E68"),sQuery(id+"F0.wireOp",EDGE,"E69"),sQuery(id+"F0.wireOp",EDGE,"E70"),sQuery(id+"F0.wireOp",EDGE,"E71"),sQuery(id+"F0.wireOp",EDGE,"E72"),sQuery(id+"F0.wireOp",EDGE,"E73"),sQuery(id+"F0.wireOp",EDGE,"E74"),sQuery(id+"F0.wireOp",EDGE,"E75"),sQuery(id+"F0.wireOp",EDGE,"E76"),sQuery(id+"F0.wireOp",EDGE,"E77"),sQuery(id+"F0.wireOp",EDGE,"E78"),sQuery(id+"F0.wireOp",EDGE,"E79"),sQuery(id+"F0.wireOp",EDGE,"E80"),sQuery(id+"F0.wireOp",EDGE,"E81"),sQuery(id+"F0.wireOp",EDGE,"E82"),sQuery(id+"F0.wireOp",EDGE,"E83"),sQuery(id+"F0.wireOp",EDGE,"E84"),sQuery(id+"F0.wireOp",EDGE,"E85"),sQuery(id+"F0.wireOp",EDGE,"E86"),sQuery(id+"F0.wireOp",EDGE,"E87"),sQuery(id+"F0.wireOp",EDGE,"E88"),sQuery(id+"F0.wireOp",EDGE,"E89"),sQuery(id+"F0.wireOp",EDGE,"E90"),sQuery(id+"F0.wireOp",EDGE,"E91"),sQuery(id+"F0.wireOp",EDGE,"E92"),sQuery(id+"F0.wireOp",EDGE,"E93"),sQuery(id+"F0.wireOp",EDGE,"E94"),sQuery(id+"F0.wireOp",EDGE,"E95"),sQuery(id+"F0.wireOp",EDGE,"E96"),sQuery(id+"F0.wireOp",EDGE,"E97"),sQuery(id+"F0.wireOp",EDGE,"E98"),sQuery(id+"F0.wireOp",EDGE,"E99"),sQuery(id+"F0.wireOp",EDGE,"E100"),sQuery(id+"F0.wireOp",EDGE,"E101"),sQuery(id+"F0.wireOp",EDGE,"E102"),sQuery(id+"F0.wireOp",EDGE,"E103"),sQuery(id+"F0.wireOp",EDGE,"E104"),sQuery(id+"F0.wireOp",EDGE,"E105"),sQuery(id+"F0.wireOp",EDGE,"E106"),sQuery(id+"F0.wireOp",EDGE,"E107"),sQuery(id+"F0.wireOp",EDGE,"E108"),sQuery(id+"F0.wireOp",EDGE,"E109"),sQuery(id+"F0.wireOp",EDGE,"E110"),sQuery(id+"F0.wireOp",EDGE,"E111"),sQuery(id+"F0.wireOp",EDGE,"E112"),sQuery(id+"F0.wireOp",EDGE,"E113"),sQuery(id+"F0.wireOp",EDGE,"E114"),sQuery(id+"F0.wireOp",EDGE,"E115"),sQuery(id+"F0.wireOp",EDGE,"E116"),sQuery(id+"F0.wireOp",EDGE,"E117"),sQuery(id+"F0.wireOp",EDGE,"E118"),sQuery(id+"F0.wireOp",EDGE,"E119"),sQuery(id+"F0.wireOp",EDGE,"E120"),sQuery(id+"F0.wireOp",EDGE,"E121"),sQuery(id+"F0.wireOp",EDGE,"E122"),sQuery(id+"F0.wireOp",EDGE,"E123"),sQuery(id+"F0.wireOp",EDGE,"E124"),sQuery(id+"F0.wireOp",EDGE,"E125"),sQuery(id+"F0.wireOp",EDGE,"E126"),sQuery(id+"F0.wireOp",EDGE,"E127"),sQuery(id+"F0.wireOp",EDGE,"E128"),sQuery(id+"F0.wireOp",EDGE,"E129"),sQuery(id+"F0.wireOp",EDGE,"E130"),sQuery(id+"F0.wireOp",EDGE,"E131"),sQuery(id+"F0.wireOp",EDGE,"E132"),sQuery(id+"F0.wireOp",EDGE,"E133"),sQuery(id+"F0.wireOp",EDGE,"E134"),sQuery(id+"F0.wireOp",EDGE,"E135"),sQuery(id+"F0.wireOp",EDGE,"E136"),sQuery(id+"F0.wireOp",EDGE,"E137"),sQuery(id+"F0.wireOp",EDGE,"E138"),sQuery(id+"F0.wireOp",EDGE,"E139"),sQuery(id+"F0.wireOp",EDGE,"E140"),sQuery(id+"F0.wireOp",EDGE,"E141"),sQuery(id+"F0.wireOp",EDGE,"E142"),sQuery(id+"F0.wireOp",EDGE,"E143"),sQuery(id+"F0.wireOp",EDGE,"E144"),sQuery(id+"F0.wireOp",EDGE,"E145"),sQuery(id+"F0.wireOp",EDGE,"E146"),sQuery(id+"F0.wireOp",EDGE,"E147"),sQuery(id+"F0.wireOp",EDGE,"E148"),sQuery(id+"F0.wireOp",EDGE,"E149"),sQuery(id+"F0.wireOp",EDGE,"E150"),sQuery(id+"F0.wireOp",EDGE,"E151"),sQuery(id+"F0.wireOp",EDGE,"E152"),sQuery(id+"F0.wireOp",EDGE,"E153"),sQuery(id+"F0.wireOp",EDGE,"E154"),sQuery(id+"F0.wireOp",EDGE,"E155"),sQuery(id+"F0.wireOp",EDGE,"E156"),sQuery(id+"F0.wireOp",EDGE,"E157"),sQuery(id+"F0.wireOp",EDGE,"E158"),sQuery(id+"F0.wireOp",EDGE,"E159"),sQuery(id+"F0.wireOp",EDGE,"E160"),sQuery(id+"F0.wireOp",EDGE,"E161"),sQuery(id+"F0.wireOp",EDGE,"E162"),sQuery(id+"F0.wireOp",EDGE,"E163"),sQuery(id+"F0.wireOp",EDGE,"E164"),sQuery(id+"F0.wireOp",EDGE,"E165"),sQuery(id+"F0.wireOp",EDGE,"E166"),sQuery(id+"F0.wireOp",EDGE,"E167"),sQuery(id+"F0.wireOp",EDGE,"E168"),sQuery(id+"F0.wireOp",EDGE,"E169"),sQuery(id+"F0.wireOp",EDGE,"E170"),sQuery(id+"F0.wireOp",EDGE,"E171"),sQuery(id+"F0.wireOp",EDGE,"E172"),sQuery(id+"F0.wireOp",EDGE,"E173"),sQuery(id+"F0.wireOp",EDGE,"E174"),sQuery(id+"F0.wireOp",EDGE,"E175"),sQuery(id+"F0.wireOp",EDGE,"E176"),sQuery(id+"F0.wireOp",EDGE,"E177"),sQuery(id+"F0.wireOp",EDGE,"E178"),sQuery(id+"F0.wireOp",EDGE,"E179"),sQuery(id+"F0.wireOp",EDGE,"E180"),sQuery(id+"F0.wireOp",EDGE,"E181"),sQuery(id+"F0.wireOp",EDGE,"E182"),sQuery(id+"F0.wireOp",EDGE,"E183"),sQuery(id+"F0.wireOp",EDGE,"E184"),sQuery(id+"F0.wireOp",EDGE,"E185"),sQuery(id+"F0.wireOp",EDGE,"E186"),sQuery(id+"F0.wireOp",EDGE,"E187"),sQuery(id+"F0.wireOp",EDGE,"E188"),sQuery(id+"F0.wireOp",EDGE,"E189"),sQuery(id+"F0.wireOp",EDGE,"E190"),sQuery(id+"F0.wireOp",EDGE,"E191"),sQuery(id+"F0.wireOp",EDGE,"E192"),sQuery(id+"F0.wireOp",EDGE,"E193"),sQuery(id+"F0.wireOp",EDGE,"E194"),sQuery(id+"F0.wireOp",EDGE,"E195"),sQuery(id+"F0.wireOp",EDGE,"E196"),sQuery(id+"F0.wireOp",EDGE,"E197"),sQuery(id+"F0.wireOp",EDGE,"E198"),sQuery(id+"F0.wireOp",EDGE,"E199"),sQuery(id+"F0.wireOp",EDGE,"E200"),sQuery(id+"F0.wireOp",EDGE,"E201"),sQuery(id+"F0.wireOp",EDGE,"E202"),sQuery(id+"F0.wireOp",EDGE,"E203"),sQuery(id+"F0.wireOp",EDGE,"E204"),sQuery(id+"F0.wireOp",EDGE,"E205"),sQuery(id+"F0.wireOp",EDGE,"E206"),sQuery(id+"F0.wireOp",EDGE,"E207"),sQuery(id+"F0.wireOp",EDGE,"E208"),sQuery(id+"F0.wireOp",EDGE,"E209"),sQuery(id+"F0.wireOp",EDGE,"E210"),sQuery(id+"F0.wireOp",EDGE,"E211"),sQuery(id+"F0.wireOp",EDGE,"E212"),sQuery(id+"F0.wireOp",EDGE,"E213"),sQuery(id+"F0.wireOp",EDGE,"E214"),sQuery(id+"F0.wireOp",EDGE,"E215"),sQuery(id+"F0.wireOp",EDGE,"E216"),sQuery(id+"F0.wireOp",EDGE,"E217"),sQuery(id+"F0.wireOp",EDGE,"E218"),sQuery(id+"F0.wireOp",EDGE,"E219"),sQuery(id+"F0.wireOp",EDGE,"E220"),sQuery(id+"F0.wireOp",EDGE,"E221"),sQuery(id+"F0.wireOp",EDGE,"E222"),sQuery(id+"F0.wireOp",EDGE,"E223"),sQuery(id+"F0.wireOp",EDGE,"E224"),sQuery(id+"F0.wireOp",EDGE,"E225"),sQuery(id+"F0.wireOp",EDGE,"E226"),sQuery(id+"F0.wireOp",EDGE,"E227"),sQuery(id+"F0.wireOp",EDGE,"E228"),sQuery(id+"F0.wireOp",EDGE,"E229"),sQuery(id+"F0.wireOp",EDGE,"E230"),sQuery(id+"F0.wireOp",EDGE,"E231"),sQuery(id+"F0.wireOp",EDGE,"E232"),sQuery(id+"F0.wireOp",EDGE,"E233"),sQuery(id+"F0.wireOp",EDGE,"E234"),sQuery(id+"F0.wireOp",EDGE,"E235"),sQuery(id+"F0.wireOp",EDGE,"E236"),sQuery(id+"F0.wireOp",EDGE,"E237"),sQuery(id+"F0.wireOp",EDGE,"E238"),sQuery(id+"F0.wireOp",EDGE,"E239"),sQuery(id+"F0.wireOp",EDGE,"E240"),sQuery(id+"F0.wireOp",EDGE,"E241"),sQuery(id+"F0.wireOp",EDGE,"E242"),sQuery(id+"F0.wireOp",EDGE,"E243"),sQuery(id+"F3.wireOp",EDGE,"E244.bottom"),sQuery(id+"F3.wireOp",EDGE,"E244.top"),sQuery(id+"F3.wireOp",EDGE,"E244.left"),sQuery(id+"F3.wireOp",EDGE,"E244.right"),sQuery(id+"F3.wireOp",EDGE,"E245.filletArc"),sQuery(id+"F3.wireOp",EDGE,"E246.filletArc"),sQuery(id+"F3.wireOp",EDGE,"E247.filletArc"),sQuery(id+"F3.wireOp",EDGE,"E248.filletArc")])],"isStart":false})}),makeQuery(id+"F8.opExtrude","CAP_FACE",FACE,{"disambiguationData":[OSD([sQuery(id+"F7.wireOp",EDGE,"E250.bottom"),sQuery(id+"F7.wireOp",EDGE,"E250.top"),sQuery(id+"F7.wireOp",EDGE,"E250.left"),sQuery(id+"F7.wireOp",EDGE,"E250.right")])],"isStart":false})]})});
            var Q9;
            Q9=makeQuery(id+"F12.boolean.opBoolean","SPLIT",FACE,{"disambiguationData":[TD([makeQuery(id+"F12.opExtrude","SWEPT_FACE",FACE,{"disambiguationData":[OSD([sQuery(id+"F11.wireOp",EDGE,"E276")])]})])],"derivedFrom":makeQuery(id+"F8.boolean.opBoolean","MERGE",FACE,{"derivedFrom":[makeQuery(id+"F4.boolean.opBoolean","COPY",FACE,{"derivedFrom":makeQuery(id+"F4.opExtrude","CAP_FACE",FACE,{"disambiguationData":[OSD([sQuery(id+"F0.wireOp",EDGE,"E4"),sQuery(id+"F0.wireOp",EDGE,"E5"),sQuery(id+"F0.wireOp",EDGE,"E6"),sQuery(id+"F0.wireOp",EDGE,"E7"),sQuery(id+"F0.wireOp",EDGE,"E8"),sQuery(id+"F0.wireOp",EDGE,"E9"),sQuery(id+"F0.wireOp",EDGE,"E10"),sQuery(id+"F0.wireOp",EDGE,"E11"),sQuery(id+"F0.wireOp",EDGE,"E12"),sQuery(id+"F0.wireOp",EDGE,"E13"),sQuery(id+"F0.wireOp",EDGE,"E14"),sQuery(id+"F0.wireOp",EDGE,"E15"),sQuery(id+"F0.wireOp",EDGE,"E16"),sQuery(id+"F0.wireOp",EDGE,"E17"),sQuery(id+"F0.wireOp",EDGE,"E18"),sQuery(id+"F0.wireOp",EDGE,"E19"),sQuery(id+"F0.wireOp",EDGE,"E20"),sQuery(id+"F0.wireOp",EDGE,"E21"),sQuery(id+"F0.wireOp",EDGE,"E22"),sQuery(id+"F0.wireOp",EDGE,"E23"),sQuery(id+"F0.wireOp",EDGE,"E24"),sQuery(id+"F0.wireOp",EDGE,"E25"),sQuery(id+"F0.wireOp",EDGE,"E26"),sQuery(id+"F0.wireOp",EDGE,"E27"),sQuery(id+"F0.wireOp",EDGE,"E28"),sQuery(id+"F0.wireOp",EDGE,"E29"),sQuery(id+"F0.wireOp",EDGE,"E30"),sQuery(id+"F0.wireOp",EDGE,"E31"),sQuery(id+"F0.wireOp",EDGE,"E32"),sQuery(id+"F0.wireOp",EDGE,"E33"),sQuery(id+"F0.wireOp",EDGE,"E34"),sQuery(id+"F0.wireOp",EDGE,"E35"),sQuery(id+"F0.wireOp",EDGE,"E36"),sQuery(id+"F0.wireOp",EDGE,"E37"),sQuery(id+"F0.wireOp",EDGE,"E38"),sQuery(id+"F0.wireOp",EDGE,"E39"),sQuery(id+"F0.wireOp",EDGE,"E40"),sQuery(id+"F0.wireOp",EDGE,"E41"),sQuery(id+"F0.wireOp",EDGE,"E42"),sQuery(id+"F0.wireOp",EDGE,"E43"),sQuery(id+"F0.wireOp",EDGE,"E44"),sQuery(id+"F0.wireOp",EDGE,"E45"),sQuery(id+"F0.wireOp",EDGE,"E46"),sQuery(id+"F0.wireOp",EDGE,"E47"),sQuery(id+"F0.wireOp",EDGE,"E48"),sQuery(id+"F0.wireOp",EDGE,"E49"),sQuery(id+"F0.wireOp",EDGE,"E50"),sQuery(id+"F0.wireOp",EDGE,"E51"),sQuery(id+"F0.wireOp",EDGE,"E52"),sQuery(id+"F0.wireOp",EDGE,"E53"),sQuery(id+"F0.wireOp",EDGE,"E54"),sQuery(id+"F0.wireOp",EDGE,"E55"),sQuery(id+"F0.wireOp",EDGE,"E56"),sQuery(id+"F0.wireOp",EDGE,"E57"),sQuery(id+"F0.wireOp",EDGE,"E58"),sQuery(id+"F0.wireOp",EDGE,"E59"),sQuery(id+"F0.wireOp",EDGE,"E60"),sQuery(id+"F0.wireOp",EDGE,"E61"),sQuery(id+"F0.wireOp",EDGE,"E62"),sQuery(id+"F0.wireOp",EDGE,"E63"),sQuery(id+"F0.wireOp",EDGE,"E64"),sQuery(id+"F0.wireOp",EDGE,"E65"),sQuery(id+"F0.wireOp",EDGE,"E66"),sQuery(id+"F0.wireOp",EDGE,"E67"),sQuery(id+"F0.wireOp",EDGE,"E68"),sQuery(id+"F0.wireOp",EDGE,"E69"),sQuery(id+"F0.wireOp",EDGE,"E70"),sQuery(id+"F0.wireOp",EDGE,"E71"),sQuery(id+"F0.wireOp",EDGE,"E72"),sQuery(id+"F0.wireOp",EDGE,"E73"),sQuery(id+"F0.wireOp",EDGE,"E74"),sQuery(id+"F0.wireOp",EDGE,"E75"),sQuery(id+"F0.wireOp",EDGE,"E76"),sQuery(id+"F0.wireOp",EDGE,"E77"),sQuery(id+"F0.wireOp",EDGE,"E78"),sQuery(id+"F0.wireOp",EDGE,"E79"),sQuery(id+"F0.wireOp",EDGE,"E80"),sQuery(id+"F0.wireOp",EDGE,"E81"),sQuery(id+"F0.wireOp",EDGE,"E82"),sQuery(id+"F0.wireOp",EDGE,"E83"),sQuery(id+"F0.wireOp",EDGE,"E84"),sQuery(id+"F0.wireOp",EDGE,"E85"),sQuery(id+"F0.wireOp",EDGE,"E86"),sQuery(id+"F0.wireOp",EDGE,"E87"),sQuery(id+"F0.wireOp",EDGE,"E88"),sQuery(id+"F0.wireOp",EDGE,"E89"),sQuery(id+"F0.wireOp",EDGE,"E90"),sQuery(id+"F0.wireOp",EDGE,"E91"),sQuery(id+"F0.wireOp",EDGE,"E92"),sQuery(id+"F0.wireOp",EDGE,"E93"),sQuery(id+"F0.wireOp",EDGE,"E94"),sQuery(id+"F0.wireOp",EDGE,"E95"),sQuery(id+"F0.wireOp",EDGE,"E96"),sQuery(id+"F0.wireOp",EDGE,"E97"),sQuery(id+"F0.wireOp",EDGE,"E98"),sQuery(id+"F0.wireOp",EDGE,"E99"),sQuery(id+"F0.wireOp",EDGE,"E100"),sQuery(id+"F0.wireOp",EDGE,"E101"),sQuery(id+"F0.wireOp",EDGE,"E102"),sQuery(id+"F0.wireOp",EDGE,"E103"),sQuery(id+"F0.wireOp",EDGE,"E104"),sQuery(id+"F0.wireOp",EDGE,"E105"),sQuery(id+"F0.wireOp",EDGE,"E106"),sQuery(id+"F0.wireOp",EDGE,"E107"),sQuery(id+"F0.wireOp",EDGE,"E108"),sQuery(id+"F0.wireOp",EDGE,"E109"),sQuery(id+"F0.wireOp",EDGE,"E110"),sQuery(id+"F0.wireOp",EDGE,"E111"),sQuery(id+"F0.wireOp",EDGE,"E112"),sQuery(id+"F0.wireOp",EDGE,"E113"),sQuery(id+"F0.wireOp",EDGE,"E114"),sQuery(id+"F0.wireOp",EDGE,"E115"),sQuery(id+"F0.wireOp",EDGE,"E116"),sQuery(id+"F0.wireOp",EDGE,"E117"),sQuery(id+"F0.wireOp",EDGE,"E118"),sQuery(id+"F0.wireOp",EDGE,"E119"),sQuery(id+"F0.wireOp",EDGE,"E120"),sQuery(id+"F0.wireOp",EDGE,"E121"),sQuery(id+"F0.wireOp",EDGE,"E122"),sQuery(id+"F0.wireOp",EDGE,"E123"),sQuery(id+"F0.wireOp",EDGE,"E124"),sQuery(id+"F0.wireOp",EDGE,"E125"),sQuery(id+"F0.wireOp",EDGE,"E126"),sQuery(id+"F0.wireOp",EDGE,"E127"),sQuery(id+"F0.wireOp",EDGE,"E128"),sQuery(id+"F0.wireOp",EDGE,"E129"),sQuery(id+"F0.wireOp",EDGE,"E130"),sQuery(id+"F0.wireOp",EDGE,"E131"),sQuery(id+"F0.wireOp",EDGE,"E132"),sQuery(id+"F0.wireOp",EDGE,"E133"),sQuery(id+"F0.wireOp",EDGE,"E134"),sQuery(id+"F0.wireOp",EDGE,"E135"),sQuery(id+"F0.wireOp",EDGE,"E136"),sQuery(id+"F0.wireOp",EDGE,"E137"),sQuery(id+"F0.wireOp",EDGE,"E138"),sQuery(id+"F0.wireOp",EDGE,"E139"),sQuery(id+"F0.wireOp",EDGE,"E140"),sQuery(id+"F0.wireOp",EDGE,"E141"),sQuery(id+"F0.wireOp",EDGE,"E142"),sQuery(id+"F0.wireOp",EDGE,"E143"),sQuery(id+"F0.wireOp",EDGE,"E144"),sQuery(id+"F0.wireOp",EDGE,"E145"),sQuery(id+"F0.wireOp",EDGE,"E146"),sQuery(id+"F0.wireOp",EDGE,"E147"),sQuery(id+"F0.wireOp",EDGE,"E148"),sQuery(id+"F0.wireOp",EDGE,"E149"),sQuery(id+"F0.wireOp",EDGE,"E150"),sQuery(id+"F0.wireOp",EDGE,"E151"),sQuery(id+"F0.wireOp",EDGE,"E152"),sQuery(id+"F0.wireOp",EDGE,"E153"),sQuery(id+"F0.wireOp",EDGE,"E154"),sQuery(id+"F0.wireOp",EDGE,"E155"),sQuery(id+"F0.wireOp",EDGE,"E156"),sQuery(id+"F0.wireOp",EDGE,"E157"),sQuery(id+"F0.wireOp",EDGE,"E158"),sQuery(id+"F0.wireOp",EDGE,"E159"),sQuery(id+"F0.wireOp",EDGE,"E160"),sQuery(id+"F0.wireOp",EDGE,"E161"),sQuery(id+"F0.wireOp",EDGE,"E162"),sQuery(id+"F0.wireOp",EDGE,"E163"),sQuery(id+"F0.wireOp",EDGE,"E164"),sQuery(id+"F0.wireOp",EDGE,"E165"),sQuery(id+"F0.wireOp",EDGE,"E166"),sQuery(id+"F0.wireOp",EDGE,"E167"),sQuery(id+"F0.wireOp",EDGE,"E168"),sQuery(id+"F0.wireOp",EDGE,"E169"),sQuery(id+"F0.wireOp",EDGE,"E170"),sQuery(id+"F0.wireOp",EDGE,"E171"),sQuery(id+"F0.wireOp",EDGE,"E172"),sQuery(id+"F0.wireOp",EDGE,"E173"),sQuery(id+"F0.wireOp",EDGE,"E174"),sQuery(id+"F0.wireOp",EDGE,"E175"),sQuery(id+"F0.wireOp",EDGE,"E176"),sQuery(id+"F0.wireOp",EDGE,"E177"),sQuery(id+"F0.wireOp",EDGE,"E178"),sQuery(id+"F0.wireOp",EDGE,"E179"),sQuery(id+"F0.wireOp",EDGE,"E180"),sQuery(id+"F0.wireOp",EDGE,"E181"),sQuery(id+"F0.wireOp",EDGE,"E182"),sQuery(id+"F0.wireOp",EDGE,"E183"),sQuery(id+"F0.wireOp",EDGE,"E184"),sQuery(id+"F0.wireOp",EDGE,"E185"),sQuery(id+"F0.wireOp",EDGE,"E186"),sQuery(id+"F0.wireOp",EDGE,"E187"),sQuery(id+"F0.wireOp",EDGE,"E188"),sQuery(id+"F0.wireOp",EDGE,"E189"),sQuery(id+"F0.wireOp",EDGE,"E190"),sQuery(id+"F0.wireOp",EDGE,"E191"),sQuery(id+"F0.wireOp",EDGE,"E192"),sQuery(id+"F0.wireOp",EDGE,"E193"),sQuery(id+"F0.wireOp",EDGE,"E194"),sQuery(id+"F0.wireOp",EDGE,"E195"),sQuery(id+"F0.wireOp",EDGE,"E196"),sQuery(id+"F0.wireOp",EDGE,"E197"),sQuery(id+"F0.wireOp",EDGE,"E198"),sQuery(id+"F0.wireOp",EDGE,"E199"),sQuery(id+"F0.wireOp",EDGE,"E200"),sQuery(id+"F0.wireOp",EDGE,"E201"),sQuery(id+"F0.wireOp",EDGE,"E202"),sQuery(id+"F0.wireOp",EDGE,"E203"),sQuery(id+"F0.wireOp",EDGE,"E204"),sQuery(id+"F0.wireOp",EDGE,"E205"),sQuery(id+"F0.wireOp",EDGE,"E206"),sQuery(id+"F0.wireOp",EDGE,"E207"),sQuery(id+"F0.wireOp",EDGE,"E208"),sQuery(id+"F0.wireOp",EDGE,"E209"),sQuery(id+"F0.wireOp",EDGE,"E210"),sQuery(id+"F0.wireOp",EDGE,"E211"),sQuery(id+"F0.wireOp",EDGE,"E212"),sQuery(id+"F0.wireOp",EDGE,"E213"),sQuery(id+"F0.wireOp",EDGE,"E214"),sQuery(id+"F0.wireOp",EDGE,"E215"),sQuery(id+"F0.wireOp",EDGE,"E216"),sQuery(id+"F0.wireOp",EDGE,"E217"),sQuery(id+"F0.wireOp",EDGE,"E218"),sQuery(id+"F0.wireOp",EDGE,"E219"),sQuery(id+"F0.wireOp",EDGE,"E220"),sQuery(id+"F0.wireOp",EDGE,"E221"),sQuery(id+"F0.wireOp",EDGE,"E222"),sQuery(id+"F0.wireOp",EDGE,"E223"),sQuery(id+"F0.wireOp",EDGE,"E224"),sQuery(id+"F0.wireOp",EDGE,"E225"),sQuery(id+"F0.wireOp",EDGE,"E226"),sQuery(id+"F0.wireOp",EDGE,"E227"),sQuery(id+"F0.wireOp",EDGE,"E228"),sQuery(id+"F0.wireOp",EDGE,"E229"),sQuery(id+"F0.wireOp",EDGE,"E230"),sQuery(id+"F0.wireOp",EDGE,"E231"),sQuery(id+"F0.wireOp",EDGE,"E232"),sQuery(id+"F0.wireOp",EDGE,"E233"),sQuery(id+"F0.wireOp",EDGE,"E234"),sQuery(id+"F0.wireOp",EDGE,"E235"),sQuery(id+"F0.wireOp",EDGE,"E236"),sQuery(id+"F0.wireOp",EDGE,"E237"),sQuery(id+"F0.wireOp",EDGE,"E238"),sQuery(id+"F0.wireOp",EDGE,"E239"),sQuery(id+"F0.wireOp",EDGE,"E240"),sQuery(id+"F0.wireOp",EDGE,"E241"),sQuery(id+"F0.wireOp",EDGE,"E242"),sQuery(id+"F0.wireOp",EDGE,"E243"),sQuery(id+"F3.wireOp",EDGE,"E244.bottom"),sQuery(id+"F3.wireOp",EDGE,"E244.top"),sQuery(id+"F3.wireOp",EDGE,"E244.left"),sQuery(id+"F3.wireOp",EDGE,"E244.right"),sQuery(id+"F3.wireOp",EDGE,"E245.filletArc"),sQuery(id+"F3.wireOp",EDGE,"E246.filletArc"),sQuery(id+"F3.wireOp",EDGE,"E247.filletArc"),sQuery(id+"F3.wireOp",EDGE,"E248.filletArc")])],"isStart":false})}),makeQuery(id+"F8.opExtrude","CAP_FACE",FACE,{"disambiguationData":[OSD([sQuery(id+"F7.wireOp",EDGE,"E250.bottom"),sQuery(id+"F7.wireOp",EDGE,"E250.top"),sQuery(id+"F7.wireOp",EDGE,"E250.left"),sQuery(id+"F7.wireOp",EDGE,"E250.right")])],"isStart":false})]})});
            extrude(context, id + "F13", {"entities" : qUnion([Q0, Q1, Q2, Q3, Q4, Q5, Q6, Q7, Q8, Q9]), "operationType" : NewBodyOperationType.ADD, "depth" : 3.3 * mm, "offsetDistance" : 25 * mm});
        }
        {
            var Q0;
            Q0=makeQuery(id+"F1.opExtrude","CAP_FACE",FACE,{"disambiguationData":[OSD([sQuery(id+"F0.wireOp",EDGE,"E0"),sQuery(id+"F0.wireOp",EDGE,"E1"),sQuery(id+"F0.wireOp",EDGE,"E2"),sQuery(id+"F0.wireOp",EDGE,"E3"),sQuery(id+"F0.wireOp",EDGE,"E4"),sQuery(id+"F0.wireOp",EDGE,"E5"),sQuery(id+"F0.wireOp",EDGE,"E6"),sQuery(id+"F0.wireOp",EDGE,"E7"),sQuery(id+"F0.wireOp",EDGE,"E8"),sQuery(id+"F0.wireOp",EDGE,"E9"),sQuery(id+"F0.wireOp",EDGE,"E10"),sQuery(id+"F0.wireOp",EDGE,"E11"),sQuery(id+"F0.wireOp",EDGE,"E12"),sQuery(id+"F0.wireOp",EDGE,"E13"),sQuery(id+"F0.wireOp",EDGE,"E14"),sQuery(id+"F0.wireOp",EDGE,"E15"),sQuery(id+"F0.wireOp",EDGE,"E16"),sQuery(id+"F0.wireOp",EDGE,"E17"),sQuery(id+"F0.wireOp",EDGE,"E18"),sQuery(id+"F0.wireOp",EDGE,"E19"),sQuery(id+"F0.wireOp",EDGE,"E20"),sQuery(id+"F0.wireOp",EDGE,"E21"),sQuery(id+"F0.wireOp",EDGE,"E22"),sQuery(id+"F0.wireOp",EDGE,"E23"),sQuery(id+"F0.wireOp",EDGE,"E24"),sQuery(id+"F0.wireOp",EDGE,"E25"),sQuery(id+"F0.wireOp",EDGE,"E26"),sQuery(id+"F0.wireOp",EDGE,"E27"),sQuery(id+"F0.wireOp",EDGE,"E28"),sQuery(id+"F0.wireOp",EDGE,"E29"),sQuery(id+"F0.wireOp",EDGE,"E30"),sQuery(id+"F0.wireOp",EDGE,"E31"),sQuery(id+"F0.wireOp",EDGE,"E32"),sQuery(id+"F0.wireOp",EDGE,"E33"),sQuery(id+"F0.wireOp",EDGE,"E34"),sQuery(id+"F0.wireOp",EDGE,"E35"),sQuery(id+"F0.wireOp",EDGE,"E36"),sQuery(id+"F0.wireOp",EDGE,"E37"),sQuery(id+"F0.wireOp",EDGE,"E38"),sQuery(id+"F0.wireOp",EDGE,"E39"),sQuery(id+"F0.wireOp",EDGE,"E40"),sQuery(id+"F0.wireOp",EDGE,"E41"),sQuery(id+"F0.wireOp",EDGE,"E42"),sQuery(id+"F0.wireOp",EDGE,"E43"),sQuery(id+"F0.wireOp",EDGE,"E44"),sQuery(id+"F0.wireOp",EDGE,"E45"),sQuery(id+"F0.wireOp",EDGE,"E46"),sQuery(id+"F0.wireOp",EDGE,"E47"),sQuery(id+"F0.wireOp",EDGE,"E48"),sQuery(id+"F0.wireOp",EDGE,"E49"),sQuery(id+"F0.wireOp",EDGE,"E50"),sQuery(id+"F0.wireOp",EDGE,"E51"),sQuery(id+"F0.wireOp",EDGE,"E52"),sQuery(id+"F0.wireOp",EDGE,"E53"),sQuery(id+"F0.wireOp",EDGE,"E54"),sQuery(id+"F0.wireOp",EDGE,"E55"),sQuery(id+"F0.wireOp",EDGE,"E56"),sQuery(id+"F0.wireOp",EDGE,"E57"),sQuery(id+"F0.wireOp",EDGE,"E58"),sQuery(id+"F0.wireOp",EDGE,"E59"),sQuery(id+"F0.wireOp",EDGE,"E60"),sQuery(id+"F0.wireOp",EDGE,"E61"),sQuery(id+"F0.wireOp",EDGE,"E62"),sQuery(id+"F0.wireOp",EDGE,"E63"),sQuery(id+"F0.wireOp",EDGE,"E64"),sQuery(id+"F0.wireOp",EDGE,"E65"),sQuery(id+"F0.wireOp",EDGE,"E66"),sQuery(id+"F0.wireOp",EDGE,"E67"),sQuery(id+"F0.wireOp",EDGE,"E68"),sQuery(id+"F0.wireOp",EDGE,"E69"),sQuery(id+"F0.wireOp",EDGE,"E70"),sQuery(id+"F0.wireOp",EDGE,"E71"),sQuery(id+"F0.wireOp",EDGE,"E72"),sQuery(id+"F0.wireOp",EDGE,"E73"),sQuery(id+"F0.wireOp",EDGE,"E74"),sQuery(id+"F0.wireOp",EDGE,"E75"),sQuery(id+"F0.wireOp",EDGE,"E76"),sQuery(id+"F0.wireOp",EDGE,"E77"),sQuery(id+"F0.wireOp",EDGE,"E78"),sQuery(id+"F0.wireOp",EDGE,"E79"),sQuery(id+"F0.wireOp",EDGE,"E80"),sQuery(id+"F0.wireOp",EDGE,"E81"),sQuery(id+"F0.wireOp",EDGE,"E82"),sQuery(id+"F0.wireOp",EDGE,"E83"),sQuery(id+"F0.wireOp",EDGE,"E84"),sQuery(id+"F0.wireOp",EDGE,"E85"),sQuery(id+"F0.wireOp",EDGE,"E86"),sQuery(id+"F0.wireOp",EDGE,"E87"),sQuery(id+"F0.wireOp",EDGE,"E88"),sQuery(id+"F0.wireOp",EDGE,"E89"),sQuery(id+"F0.wireOp",EDGE,"E90"),sQuery(id+"F0.wireOp",EDGE,"E91"),sQuery(id+"F0.wireOp",EDGE,"E92"),sQuery(id+"F0.wireOp",EDGE,"E93"),sQuery(id+"F0.wireOp",EDGE,"E94"),sQuery(id+"F0.wireOp",EDGE,"E95"),sQuery(id+"F0.wireOp",EDGE,"E96"),sQuery(id+"F0.wireOp",EDGE,"E97"),sQuery(id+"F0.wireOp",EDGE,"E98"),sQuery(id+"F0.wireOp",EDGE,"E99"),sQuery(id+"F0.wireOp",EDGE,"E100"),sQuery(id+"F0.wireOp",EDGE,"E101"),sQuery(id+"F0.wireOp",EDGE,"E102"),sQuery(id+"F0.wireOp",EDGE,"E103"),sQuery(id+"F0.wireOp",EDGE,"E104"),sQuery(id+"F0.wireOp",EDGE,"E105"),sQuery(id+"F0.wireOp",EDGE,"E106"),sQuery(id+"F0.wireOp",EDGE,"E107"),sQuery(id+"F0.wireOp",EDGE,"E108"),sQuery(id+"F0.wireOp",EDGE,"E109"),sQuery(id+"F0.wireOp",EDGE,"E110"),sQuery(id+"F0.wireOp",EDGE,"E111"),sQuery(id+"F0.wireOp",EDGE,"E112"),sQuery(id+"F0.wireOp",EDGE,"E113"),sQuery(id+"F0.wireOp",EDGE,"E114"),sQuery(id+"F0.wireOp",EDGE,"E115"),sQuery(id+"F0.wireOp",EDGE,"E116"),sQuery(id+"F0.wireOp",EDGE,"E117"),sQuery(id+"F0.wireOp",EDGE,"E118"),sQuery(id+"F0.wireOp",EDGE,"E119"),sQuery(id+"F0.wireOp",EDGE,"E120"),sQuery(id+"F0.wireOp",EDGE,"E121"),sQuery(id+"F0.wireOp",EDGE,"E122"),sQuery(id+"F0.wireOp",EDGE,"E123"),sQuery(id+"F0.wireOp",EDGE,"E124"),sQuery(id+"F0.wireOp",EDGE,"E125"),sQuery(id+"F0.wireOp",EDGE,"E126"),sQuery(id+"F0.wireOp",EDGE,"E127"),sQuery(id+"F0.wireOp",EDGE,"E128"),sQuery(id+"F0.wireOp",EDGE,"E129"),sQuery(id+"F0.wireOp",EDGE,"E130"),sQuery(id+"F0.wireOp",EDGE,"E131"),sQuery(id+"F0.wireOp",EDGE,"E132"),sQuery(id+"F0.wireOp",EDGE,"E133"),sQuery(id+"F0.wireOp",EDGE,"E134"),sQuery(id+"F0.wireOp",EDGE,"E135"),sQuery(id+"F0.wireOp",EDGE,"E136"),sQuery(id+"F0.wireOp",EDGE,"E137"),sQuery(id+"F0.wireOp",EDGE,"E138"),sQuery(id+"F0.wireOp",EDGE,"E139"),sQuery(id+"F0.wireOp",EDGE,"E140"),sQuery(id+"F0.wireOp",EDGE,"E141"),sQuery(id+"F0.wireOp",EDGE,"E142"),sQuery(id+"F0.wireOp",EDGE,"E143"),sQuery(id+"F0.wireOp",EDGE,"E144"),sQuery(id+"F0.wireOp",EDGE,"E145"),sQuery(id+"F0.wireOp",EDGE,"E146"),sQuery(id+"F0.wireOp",EDGE,"E147"),sQuery(id+"F0.wireOp",EDGE,"E148"),sQuery(id+"F0.wireOp",EDGE,"E149"),sQuery(id+"F0.wireOp",EDGE,"E150"),sQuery(id+"F0.wireOp",EDGE,"E151"),sQuery(id+"F0.wireOp",EDGE,"E152"),sQuery(id+"F0.wireOp",EDGE,"E153"),sQuery(id+"F0.wireOp",EDGE,"E154"),sQuery(id+"F0.wireOp",EDGE,"E155"),sQuery(id+"F0.wireOp",EDGE,"E156"),sQuery(id+"F0.wireOp",EDGE,"E157"),sQuery(id+"F0.wireOp",EDGE,"E158"),sQuery(id+"F0.wireOp",EDGE,"E159"),sQuery(id+"F0.wireOp",EDGE,"E160"),sQuery(id+"F0.wireOp",EDGE,"E161"),sQuery(id+"F0.wireOp",EDGE,"E162"),sQuery(id+"F0.wireOp",EDGE,"E163"),sQuery(id+"F0.wireOp",EDGE,"E164"),sQuery(id+"F0.wireOp",EDGE,"E165"),sQuery(id+"F0.wireOp",EDGE,"E166"),sQuery(id+"F0.wireOp",EDGE,"E167"),sQuery(id+"F0.wireOp",EDGE,"E168"),sQuery(id+"F0.wireOp",EDGE,"E169"),sQuery(id+"F0.wireOp",EDGE,"E170"),sQuery(id+"F0.wireOp",EDGE,"E171"),sQuery(id+"F0.wireOp",EDGE,"E172"),sQuery(id+"F0.wireOp",EDGE,"E173"),sQuery(id+"F0.wireOp",EDGE,"E174"),sQuery(id+"F0.wireOp",EDGE,"E175"),sQuery(id+"F0.wireOp",EDGE,"E176"),sQuery(id+"F0.wireOp",EDGE,"E177"),sQuery(id+"F0.wireOp",EDGE,"E178"),sQuery(id+"F0.wireOp",EDGE,"E179"),sQuery(id+"F0.wireOp",EDGE,"E180"),sQuery(id+"F0.wireOp",EDGE,"E181"),sQuery(id+"F0.wireOp",EDGE,"E182"),sQuery(id+"F0.wireOp",EDGE,"E183"),sQuery(id+"F0.wireOp",EDGE,"E184"),sQuery(id+"F0.wireOp",EDGE,"E185"),sQuery(id+"F0.wireOp",EDGE,"E186"),sQuery(id+"F0.wireOp",EDGE,"E187"),sQuery(id+"F0.wireOp",EDGE,"E188"),sQuery(id+"F0.wireOp",EDGE,"E189"),sQuery(id+"F0.wireOp",EDGE,"E190"),sQuery(id+"F0.wireOp",EDGE,"E191"),sQuery(id+"F0.wireOp",EDGE,"E192"),sQuery(id+"F0.wireOp",EDGE,"E193"),sQuery(id+"F0.wireOp",EDGE,"E194"),sQuery(id+"F0.wireOp",EDGE,"E195"),sQuery(id+"F0.wireOp",EDGE,"E196"),sQuery(id+"F0.wireOp",EDGE,"E197"),sQuery(id+"F0.wireOp",EDGE,"E198"),sQuery(id+"F0.wireOp",EDGE,"E199"),sQuery(id+"F0.wireOp",EDGE,"E200"),sQuery(id+"F0.wireOp",EDGE,"E201"),sQuery(id+"F0.wireOp",EDGE,"E202"),sQuery(id+"F0.wireOp",EDGE,"E203"),sQuery(id+"F0.wireOp",EDGE,"E204"),sQuery(id+"F0.wireOp",EDGE,"E205"),sQuery(id+"F0.wireOp",EDGE,"E206"),sQuery(id+"F0.wireOp",EDGE,"E207"),sQuery(id+"F0.wireOp",EDGE,"E208"),sQuery(id+"F0.wireOp",EDGE,"E209"),sQuery(id+"F0.wireOp",EDGE,"E210"),sQuery(id+"F0.wireOp",EDGE,"E211"),sQuery(id+"F0.wireOp",EDGE,"E212"),sQuery(id+"F0.wireOp",EDGE,"E213"),sQuery(id+"F0.wireOp",EDGE,"E214"),sQuery(id+"F0.wireOp",EDGE,"E215"),sQuery(id+"F0.wireOp",EDGE,"E216"),sQuery(id+"F0.wireOp",EDGE,"E217"),sQuery(id+"F0.wireOp",EDGE,"E218"),sQuery(id+"F0.wireOp",EDGE,"E219"),sQuery(id+"F0.wireOp",EDGE,"E220"),sQuery(id+"F0.wireOp",EDGE,"E221"),sQuery(id+"F0.wireOp",EDGE,"E222"),sQuery(id+"F0.wireOp",EDGE,"E223"),sQuery(id+"F0.wireOp",EDGE,"E224"),sQuery(id+"F0.wireOp",EDGE,"E225"),sQuery(id+"F0.wireOp",EDGE,"E226"),sQuery(id+"F0.wireOp",EDGE,"E227"),sQuery(id+"F0.wireOp",EDGE,"E228"),sQuery(id+"F0.wireOp",EDGE,"E229"),sQuery(id+"F0.wireOp",EDGE,"E230"),sQuery(id+"F0.wireOp",EDGE,"E231"),sQuery(id+"F0.wireOp",EDGE,"E232"),sQuery(id+"F0.wireOp",EDGE,"E233"),sQuery(id+"F0.wireOp",EDGE,"E234"),sQuery(id+"F0.wireOp",EDGE,"E235"),sQuery(id+"F0.wireOp",EDGE,"E236"),sQuery(id+"F0.wireOp",EDGE,"E237"),sQuery(id+"F0.wireOp",EDGE,"E238"),sQuery(id+"F0.wireOp",EDGE,"E239"),sQuery(id+"F0.wireOp",EDGE,"E240"),sQuery(id+"F0.wireOp",EDGE,"E241"),sQuery(id+"F0.wireOp",EDGE,"E242"),sQuery(id+"F0.wireOp",EDGE,"E243")])],"isStart":true});
            var sketch = newSketch(context, id + "F14", { "sketchPlane" : qUnion([Q0])});
            skCircle(sketch, "E277", {"center": v(-110.72, 42.49) * mm, "radius": 1.5 * mm});
            skLineSegment(sketch, "E278", {"start": v(-110.72, 42.49) * mm, "end": v(-110.72, 43.55) * mm});
            skLineSegment(sketch, "E279", {"start": v(-110.72, 42.49) * mm, "end": v(-111.78, 42.49) * mm});
            skCircle(sketch, "E280.0.1.0", {"center": v(-110.72, 23.44) * mm, "radius": 1.5 * mm});
            skCircle(sketch, "E280.0.2.0", {"center": v(-110.72, 4.39) * mm, "radius": 1.5 * mm});
            skCircle(sketch, "E280.0.3.0", {"center": v(-110.72, -14.66) * mm, "radius": 1.5 * mm});
            skCircle(sketch, "E280.0.4.0", {"center": v(-110.72, -33.71) * mm, "radius": 1.5 * mm});
            skCircle(sketch, "E280.1.0.0", {"center": v(-91.67, 42.49) * mm, "radius": 1.5 * mm});
            skCircle(sketch, "E280.1.1.0", {"center": v(-91.67, 23.44) * mm, "radius": 1.5 * mm});
            skCircle(sketch, "E280.1.2.0", {"center": v(-91.67, 4.39) * mm, "radius": 1.5 * mm});
            skCircle(sketch, "E280.1.3.0", {"center": v(-91.67, -14.66) * mm, "radius": 1.5 * mm});
            skCircle(sketch, "E280.1.4.0", {"center": v(-91.67, -33.71) * mm, "radius": 1.5 * mm});
            skCircle(sketch, "E280.2.0.0", {"center": v(-72.62, 42.49) * mm, "radius": 1.5 * mm});
            skCircle(sketch, "E280.2.1.0", {"center": v(-72.62, 23.44) * mm, "radius": 1.5 * mm});
            skCircle(sketch, "E280.2.2.0", {"center": v(-72.62, 4.39) * mm, "radius": 1.5 * mm});
            skCircle(sketch, "E280.2.3.0", {"center": v(-72.62, -14.66) * mm, "radius": 1.5 * mm});
            skCircle(sketch, "E280.2.4.0", {"center": v(-72.62, -33.71) * mm, "radius": 1.5 * mm});
            skCircle(sketch, "E280.3.0.0", {"center": v(-53.57, 42.49) * mm, "radius": 1.5 * mm});
            skCircle(sketch, "E280.3.1.0", {"center": v(-53.57, 23.44) * mm, "radius": 1.5 * mm});
            skCircle(sketch, "E280.3.2.0", {"center": v(-53.57, 4.39) * mm, "radius": 1.5 * mm});
            skCircle(sketch, "E280.3.3.0", {"center": v(-53.57, -14.66) * mm, "radius": 1.5 * mm});
            skCircle(sketch, "E280.3.4.0", {"center": v(-53.57, -33.71) * mm, "radius": 1.5 * mm});
            skCircle(sketch, "E280.4.0.0", {"center": v(-34.52, 42.49) * mm, "radius": 1.5 * mm});
            skCircle(sketch, "E280.4.1.0", {"center": v(-34.52, 23.44) * mm, "radius": 1.5 * mm});
            skCircle(sketch, "E280.4.2.0", {"center": v(-34.52, 4.39) * mm, "radius": 1.5 * mm});
            skCircle(sketch, "E280.4.3.0", {"center": v(-34.52, -14.66) * mm, "radius": 1.5 * mm});
            skCircle(sketch, "E280.4.4.0", {"center": v(-34.52, -33.71) * mm, "radius": 1.5 * mm});
            skCircle(sketch, "E280.5.0.0", {"center": v(-15.47, 42.49) * mm, "radius": 1.5 * mm});
            skCircle(sketch, "E280.5.1.0", {"center": v(-15.47, 23.44) * mm, "radius": 1.5 * mm});
            skCircle(sketch, "E280.5.2.0", {"center": v(-15.47, 4.39) * mm, "radius": 1.5 * mm});
            skCircle(sketch, "E280.5.3.0", {"center": v(-15.47, -14.66) * mm, "radius": 1.5 * mm});
            skCircle(sketch, "E280.5.4.0", {"center": v(-15.47, -33.71) * mm, "radius": 1.5 * mm});
            skCircle(sketch, "E280.6.0.0", {"center": v(3.58, 42.49) * mm, "radius": 1.5 * mm});
            skCircle(sketch, "E280.6.1.0", {"center": v(3.58, 23.44) * mm, "radius": 1.5 * mm});
            skCircle(sketch, "E280.6.2.0", {"center": v(3.58, 4.39) * mm, "radius": 1.5 * mm});
            skCircle(sketch, "E280.6.3.0", {"center": v(3.58, -14.66) * mm, "radius": 1.5 * mm});
            skCircle(sketch, "E280.6.4.0", {"center": v(3.58, -33.71) * mm, "radius": 1.5 * mm});
            skCircle(sketch, "E280.7.0.0", {"center": v(22.63, 42.49) * mm, "radius": 1.5 * mm});
            skCircle(sketch, "E280.7.1.0", {"center": v(22.63, 23.44) * mm, "radius": 1.5 * mm});
            skCircle(sketch, "E280.7.2.0", {"center": v(22.63, 4.39) * mm, "radius": 1.5 * mm});
            skCircle(sketch, "E280.7.3.0", {"center": v(22.63, -14.66) * mm, "radius": 1.5 * mm});
            skCircle(sketch, "E280.7.4.0", {"center": v(22.63, -33.71) * mm, "radius": 1.5 * mm});
            skCircle(sketch, "E280.8.0.0", {"center": v(41.68, 42.49) * mm, "radius": 1.5 * mm});
            skCircle(sketch, "E280.8.1.0", {"center": v(41.68, 23.44) * mm, "radius": 1.5 * mm});
            skCircle(sketch, "E280.8.2.0", {"center": v(41.68, 4.39) * mm, "radius": 1.5 * mm});
            skCircle(sketch, "E280.8.3.0", {"center": v(41.68, -14.66) * mm, "radius": 1.5 * mm});
            skCircle(sketch, "E280.8.4.0", {"center": v(41.68, -33.71) * mm, "radius": 1.5 * mm});
            skCircle(sketch, "E280.9.0.0", {"center": v(60.73, 42.49) * mm, "radius": 1.5 * mm});
            skCircle(sketch, "E280.9.1.0", {"center": v(60.73, 23.44) * mm, "radius": 1.5 * mm});
            skCircle(sketch, "E280.9.2.0", {"center": v(60.73, 4.39) * mm, "radius": 1.5 * mm});
            skCircle(sketch, "E280.9.3.0", {"center": v(60.73, -14.66) * mm, "radius": 1.5 * mm});
            skCircle(sketch, "E280.9.4.0", {"center": v(60.73, -33.71) * mm, "radius": 1.5 * mm});
            skCircle(sketch, "E280.10.0.0", {"center": v(79.78, 42.49) * mm, "radius": 1.5 * mm});
            skCircle(sketch, "E280.10.1.0", {"center": v(79.78, 23.44) * mm, "radius": 1.5 * mm});
            skCircle(sketch, "E280.10.2.0", {"center": v(79.78, 4.39) * mm, "radius": 1.5 * mm});
            skCircle(sketch, "E280.10.3.0", {"center": v(79.78, -14.66) * mm, "radius": 1.5 * mm});
            skCircle(sketch, "E280.10.4.0", {"center": v(79.78, -33.71) * mm, "radius": 1.5 * mm});
            skCircle(sketch, "E280.11.0.0", {"center": v(98.83, 42.49) * mm, "radius": 1.5 * mm});
            skCircle(sketch, "E280.11.1.0", {"center": v(98.83, 23.44) * mm, "radius": 1.5 * mm});
            skCircle(sketch, "E280.11.2.0", {"center": v(98.83, 4.39) * mm, "radius": 1.5 * mm});
            skCircle(sketch, "E280.11.3.0", {"center": v(98.83, -14.66) * mm, "radius": 1.5 * mm});
            skCircle(sketch, "E280.11.4.0", {"center": v(98.83, -33.71) * mm, "radius": 1.5 * mm});
            skLineSegment(sketch, "E280.direction1", {"start": v(-110.72, 42.49) * mm, "end": v(-91.67, 42.49) * mm, "construction": true});
            skLineSegment(sketch, "E280.direction2", {"start": v(-110.72, 42.49) * mm, "end": v(-110.72, 23.44) * mm, "construction": true});
            skSolve(sketch);
        }
        {
            var Q0;
            Q0=makeQuery(id+"F1.opExtrude","CAP_FACE",FACE,{"disambiguationData":[OSD([sQuery(id+"F0.wireOp",EDGE,"E0"),sQuery(id+"F0.wireOp",EDGE,"E1"),sQuery(id+"F0.wireOp",EDGE,"E2"),sQuery(id+"F0.wireOp",EDGE,"E3"),sQuery(id+"F0.wireOp",EDGE,"E4"),sQuery(id+"F0.wireOp",EDGE,"E5"),sQuery(id+"F0.wireOp",EDGE,"E6"),sQuery(id+"F0.wireOp",EDGE,"E7"),sQuery(id+"F0.wireOp",EDGE,"E8"),sQuery(id+"F0.wireOp",EDGE,"E9"),sQuery(id+"F0.wireOp",EDGE,"E10"),sQuery(id+"F0.wireOp",EDGE,"E11"),sQuery(id+"F0.wireOp",EDGE,"E12"),sQuery(id+"F0.wireOp",EDGE,"E13"),sQuery(id+"F0.wireOp",EDGE,"E14"),sQuery(id+"F0.wireOp",EDGE,"E15"),sQuery(id+"F0.wireOp",EDGE,"E16"),sQuery(id+"F0.wireOp",EDGE,"E17"),sQuery(id+"F0.wireOp",EDGE,"E18"),sQuery(id+"F0.wireOp",EDGE,"E19"),sQuery(id+"F0.wireOp",EDGE,"E20"),sQuery(id+"F0.wireOp",EDGE,"E21"),sQuery(id+"F0.wireOp",EDGE,"E22"),sQuery(id+"F0.wireOp",EDGE,"E23"),sQuery(id+"F0.wireOp",EDGE,"E24"),sQuery(id+"F0.wireOp",EDGE,"E25"),sQuery(id+"F0.wireOp",EDGE,"E26"),sQuery(id+"F0.wireOp",EDGE,"E27"),sQuery(id+"F0.wireOp",EDGE,"E28"),sQuery(id+"F0.wireOp",EDGE,"E29"),sQuery(id+"F0.wireOp",EDGE,"E30"),sQuery(id+"F0.wireOp",EDGE,"E31"),sQuery(id+"F0.wireOp",EDGE,"E32"),sQuery(id+"F0.wireOp",EDGE,"E33"),sQuery(id+"F0.wireOp",EDGE,"E34"),sQuery(id+"F0.wireOp",EDGE,"E35"),sQuery(id+"F0.wireOp",EDGE,"E36"),sQuery(id+"F0.wireOp",EDGE,"E37"),sQuery(id+"F0.wireOp",EDGE,"E38"),sQuery(id+"F0.wireOp",EDGE,"E39"),sQuery(id+"F0.wireOp",EDGE,"E40"),sQuery(id+"F0.wireOp",EDGE,"E41"),sQuery(id+"F0.wireOp",EDGE,"E42"),sQuery(id+"F0.wireOp",EDGE,"E43"),sQuery(id+"F0.wireOp",EDGE,"E44"),sQuery(id+"F0.wireOp",EDGE,"E45"),sQuery(id+"F0.wireOp",EDGE,"E46"),sQuery(id+"F0.wireOp",EDGE,"E47"),sQuery(id+"F0.wireOp",EDGE,"E48"),sQuery(id+"F0.wireOp",EDGE,"E49"),sQuery(id+"F0.wireOp",EDGE,"E50"),sQuery(id+"F0.wireOp",EDGE,"E51"),sQuery(id+"F0.wireOp",EDGE,"E52"),sQuery(id+"F0.wireOp",EDGE,"E53"),sQuery(id+"F0.wireOp",EDGE,"E54"),sQuery(id+"F0.wireOp",EDGE,"E55"),sQuery(id+"F0.wireOp",EDGE,"E56"),sQuery(id+"F0.wireOp",EDGE,"E57"),sQuery(id+"F0.wireOp",EDGE,"E58"),sQuery(id+"F0.wireOp",EDGE,"E59"),sQuery(id+"F0.wireOp",EDGE,"E60"),sQuery(id+"F0.wireOp",EDGE,"E61"),sQuery(id+"F0.wireOp",EDGE,"E62"),sQuery(id+"F0.wireOp",EDGE,"E63"),sQuery(id+"F0.wireOp",EDGE,"E64"),sQuery(id+"F0.wireOp",EDGE,"E65"),sQuery(id+"F0.wireOp",EDGE,"E66"),sQuery(id+"F0.wireOp",EDGE,"E67"),sQuery(id+"F0.wireOp",EDGE,"E68"),sQuery(id+"F0.wireOp",EDGE,"E69"),sQuery(id+"F0.wireOp",EDGE,"E70"),sQuery(id+"F0.wireOp",EDGE,"E71"),sQuery(id+"F0.wireOp",EDGE,"E72"),sQuery(id+"F0.wireOp",EDGE,"E73"),sQuery(id+"F0.wireOp",EDGE,"E74"),sQuery(id+"F0.wireOp",EDGE,"E75"),sQuery(id+"F0.wireOp",EDGE,"E76"),sQuery(id+"F0.wireOp",EDGE,"E77"),sQuery(id+"F0.wireOp",EDGE,"E78"),sQuery(id+"F0.wireOp",EDGE,"E79"),sQuery(id+"F0.wireOp",EDGE,"E80"),sQuery(id+"F0.wireOp",EDGE,"E81"),sQuery(id+"F0.wireOp",EDGE,"E82"),sQuery(id+"F0.wireOp",EDGE,"E83"),sQuery(id+"F0.wireOp",EDGE,"E84"),sQuery(id+"F0.wireOp",EDGE,"E85"),sQuery(id+"F0.wireOp",EDGE,"E86"),sQuery(id+"F0.wireOp",EDGE,"E87"),sQuery(id+"F0.wireOp",EDGE,"E88"),sQuery(id+"F0.wireOp",EDGE,"E89"),sQuery(id+"F0.wireOp",EDGE,"E90"),sQuery(id+"F0.wireOp",EDGE,"E91"),sQuery(id+"F0.wireOp",EDGE,"E92"),sQuery(id+"F0.wireOp",EDGE,"E93"),sQuery(id+"F0.wireOp",EDGE,"E94"),sQuery(id+"F0.wireOp",EDGE,"E95"),sQuery(id+"F0.wireOp",EDGE,"E96"),sQuery(id+"F0.wireOp",EDGE,"E97"),sQuery(id+"F0.wireOp",EDGE,"E98"),sQuery(id+"F0.wireOp",EDGE,"E99"),sQuery(id+"F0.wireOp",EDGE,"E100"),sQuery(id+"F0.wireOp",EDGE,"E101"),sQuery(id+"F0.wireOp",EDGE,"E102"),sQuery(id+"F0.wireOp",EDGE,"E103"),sQuery(id+"F0.wireOp",EDGE,"E104"),sQuery(id+"F0.wireOp",EDGE,"E105"),sQuery(id+"F0.wireOp",EDGE,"E106"),sQuery(id+"F0.wireOp",EDGE,"E107"),sQuery(id+"F0.wireOp",EDGE,"E108"),sQuery(id+"F0.wireOp",EDGE,"E109"),sQuery(id+"F0.wireOp",EDGE,"E110"),sQuery(id+"F0.wireOp",EDGE,"E111"),sQuery(id+"F0.wireOp",EDGE,"E112"),sQuery(id+"F0.wireOp",EDGE,"E113"),sQuery(id+"F0.wireOp",EDGE,"E114"),sQuery(id+"F0.wireOp",EDGE,"E115"),sQuery(id+"F0.wireOp",EDGE,"E116"),sQuery(id+"F0.wireOp",EDGE,"E117"),sQuery(id+"F0.wireOp",EDGE,"E118"),sQuery(id+"F0.wireOp",EDGE,"E119"),sQuery(id+"F0.wireOp",EDGE,"E120"),sQuery(id+"F0.wireOp",EDGE,"E121"),sQuery(id+"F0.wireOp",EDGE,"E122"),sQuery(id+"F0.wireOp",EDGE,"E123"),sQuery(id+"F0.wireOp",EDGE,"E124"),sQuery(id+"F0.wireOp",EDGE,"E125"),sQuery(id+"F0.wireOp",EDGE,"E126"),sQuery(id+"F0.wireOp",EDGE,"E127"),sQuery(id+"F0.wireOp",EDGE,"E128"),sQuery(id+"F0.wireOp",EDGE,"E129"),sQuery(id+"F0.wireOp",EDGE,"E130"),sQuery(id+"F0.wireOp",EDGE,"E131"),sQuery(id+"F0.wireOp",EDGE,"E132"),sQuery(id+"F0.wireOp",EDGE,"E133"),sQuery(id+"F0.wireOp",EDGE,"E134"),sQuery(id+"F0.wireOp",EDGE,"E135"),sQuery(id+"F0.wireOp",EDGE,"E136"),sQuery(id+"F0.wireOp",EDGE,"E137"),sQuery(id+"F0.wireOp",EDGE,"E138"),sQuery(id+"F0.wireOp",EDGE,"E139"),sQuery(id+"F0.wireOp",EDGE,"E140"),sQuery(id+"F0.wireOp",EDGE,"E141"),sQuery(id+"F0.wireOp",EDGE,"E142"),sQuery(id+"F0.wireOp",EDGE,"E143"),sQuery(id+"F0.wireOp",EDGE,"E144"),sQuery(id+"F0.wireOp",EDGE,"E145"),sQuery(id+"F0.wireOp",EDGE,"E146"),sQuery(id+"F0.wireOp",EDGE,"E147"),sQuery(id+"F0.wireOp",EDGE,"E148"),sQuery(id+"F0.wireOp",EDGE,"E149"),sQuery(id+"F0.wireOp",EDGE,"E150"),sQuery(id+"F0.wireOp",EDGE,"E151"),sQuery(id+"F0.wireOp",EDGE,"E152"),sQuery(id+"F0.wireOp",EDGE,"E153"),sQuery(id+"F0.wireOp",EDGE,"E154"),sQuery(id+"F0.wireOp",EDGE,"E155"),sQuery(id+"F0.wireOp",EDGE,"E156"),sQuery(id+"F0.wireOp",EDGE,"E157"),sQuery(id+"F0.wireOp",EDGE,"E158"),sQuery(id+"F0.wireOp",EDGE,"E159"),sQuery(id+"F0.wireOp",EDGE,"E160"),sQuery(id+"F0.wireOp",EDGE,"E161"),sQuery(id+"F0.wireOp",EDGE,"E162"),sQuery(id+"F0.wireOp",EDGE,"E163"),sQuery(id+"F0.wireOp",EDGE,"E164"),sQuery(id+"F0.wireOp",EDGE,"E165"),sQuery(id+"F0.wireOp",EDGE,"E166"),sQuery(id+"F0.wireOp",EDGE,"E167"),sQuery(id+"F0.wireOp",EDGE,"E168"),sQuery(id+"F0.wireOp",EDGE,"E169"),sQuery(id+"F0.wireOp",EDGE,"E170"),sQuery(id+"F0.wireOp",EDGE,"E171"),sQuery(id+"F0.wireOp",EDGE,"E172"),sQuery(id+"F0.wireOp",EDGE,"E173"),sQuery(id+"F0.wireOp",EDGE,"E174"),sQuery(id+"F0.wireOp",EDGE,"E175"),sQuery(id+"F0.wireOp",EDGE,"E176"),sQuery(id+"F0.wireOp",EDGE,"E177"),sQuery(id+"F0.wireOp",EDGE,"E178"),sQuery(id+"F0.wireOp",EDGE,"E179"),sQuery(id+"F0.wireOp",EDGE,"E180"),sQuery(id+"F0.wireOp",EDGE,"E181"),sQuery(id+"F0.wireOp",EDGE,"E182"),sQuery(id+"F0.wireOp",EDGE,"E183"),sQuery(id+"F0.wireOp",EDGE,"E184"),sQuery(id+"F0.wireOp",EDGE,"E185"),sQuery(id+"F0.wireOp",EDGE,"E186"),sQuery(id+"F0.wireOp",EDGE,"E187"),sQuery(id+"F0.wireOp",EDGE,"E188"),sQuery(id+"F0.wireOp",EDGE,"E189"),sQuery(id+"F0.wireOp",EDGE,"E190"),sQuery(id+"F0.wireOp",EDGE,"E191"),sQuery(id+"F0.wireOp",EDGE,"E192"),sQuery(id+"F0.wireOp",EDGE,"E193"),sQuery(id+"F0.wireOp",EDGE,"E194"),sQuery(id+"F0.wireOp",EDGE,"E195"),sQuery(id+"F0.wireOp",EDGE,"E196"),sQuery(id+"F0.wireOp",EDGE,"E197"),sQuery(id+"F0.wireOp",EDGE,"E198"),sQuery(id+"F0.wireOp",EDGE,"E199"),sQuery(id+"F0.wireOp",EDGE,"E200"),sQuery(id+"F0.wireOp",EDGE,"E201"),sQuery(id+"F0.wireOp",EDGE,"E202"),sQuery(id+"F0.wireOp",EDGE,"E203"),sQuery(id+"F0.wireOp",EDGE,"E204"),sQuery(id+"F0.wireOp",EDGE,"E205"),sQuery(id+"F0.wireOp",EDGE,"E206"),sQuery(id+"F0.wireOp",EDGE,"E207"),sQuery(id+"F0.wireOp",EDGE,"E208"),sQuery(id+"F0.wireOp",EDGE,"E209"),sQuery(id+"F0.wireOp",EDGE,"E210"),sQuery(id+"F0.wireOp",EDGE,"E211"),sQuery(id+"F0.wireOp",EDGE,"E212"),sQuery(id+"F0.wireOp",EDGE,"E213"),sQuery(id+"F0.wireOp",EDGE,"E214"),sQuery(id+"F0.wireOp",EDGE,"E215"),sQuery(id+"F0.wireOp",EDGE,"E216"),sQuery(id+"F0.wireOp",EDGE,"E217"),sQuery(id+"F0.wireOp",EDGE,"E218"),sQuery(id+"F0.wireOp",EDGE,"E219"),sQuery(id+"F0.wireOp",EDGE,"E220"),sQuery(id+"F0.wireOp",EDGE,"E221"),sQuery(id+"F0.wireOp",EDGE,"E222"),sQuery(id+"F0.wireOp",EDGE,"E223"),sQuery(id+"F0.wireOp",EDGE,"E224"),sQuery(id+"F0.wireOp",EDGE,"E225"),sQuery(id+"F0.wireOp",EDGE,"E226"),sQuery(id+"F0.wireOp",EDGE,"E227"),sQuery(id+"F0.wireOp",EDGE,"E228"),sQuery(id+"F0.wireOp",EDGE,"E229"),sQuery(id+"F0.wireOp",EDGE,"E230"),sQuery(id+"F0.wireOp",EDGE,"E231"),sQuery(id+"F0.wireOp",EDGE,"E232"),sQuery(id+"F0.wireOp",EDGE,"E233"),sQuery(id+"F0.wireOp",EDGE,"E234"),sQuery(id+"F0.wireOp",EDGE,"E235"),sQuery(id+"F0.wireOp",EDGE,"E236"),sQuery(id+"F0.wireOp",EDGE,"E237"),sQuery(id+"F0.wireOp",EDGE,"E238"),sQuery(id+"F0.wireOp",EDGE,"E239"),sQuery(id+"F0.wireOp",EDGE,"E240"),sQuery(id+"F0.wireOp",EDGE,"E241"),sQuery(id+"F0.wireOp",EDGE,"E242"),sQuery(id+"F0.wireOp",EDGE,"E243")])],"isStart":true});
            var sketch = newSketch(context, id + "F15", { "sketchPlane" : qUnion([Q0])});
            skCircle(sketch, "E281", {"center": v(-98.84, 42.49) * mm, "radius": 1.5 * mm});
            skLineSegment(sketch, "E282", {"start": v(-98.84, 42.49) * mm, "end": v(-98.84, 43.55) * mm});
            skLineSegment(sketch, "E283", {"start": v(-98.84, 42.49) * mm, "end": v(-97.78, 42.49) * mm});
            skCircle(sketch, "E284.0.1.0", {"center": v(-98.84, 23.44) * mm, "radius": 1.5 * mm});
            skCircle(sketch, "E284.0.2.0", {"center": v(-98.84, 4.39) * mm, "radius": 1.5 * mm});
            skCircle(sketch, "E284.0.3.0", {"center": v(-98.84, -14.66) * mm, "radius": 1.5 * mm});
            skCircle(sketch, "E284.0.4.0", {"center": v(-98.84, -33.71) * mm, "radius": 1.5 * mm});
            skCircle(sketch, "E284.1.0.0", {"center": v(-79.79, 42.49) * mm, "radius": 1.5 * mm});
            skCircle(sketch, "E284.1.1.0", {"center": v(-79.79, 23.44) * mm, "radius": 1.5 * mm});
            skCircle(sketch, "E284.1.2.0", {"center": v(-79.79, 4.39) * mm, "radius": 1.5 * mm});
            skCircle(sketch, "E284.1.3.0", {"center": v(-79.79, -14.66) * mm, "radius": 1.5 * mm});
            skCircle(sketch, "E284.1.4.0", {"center": v(-79.79, -33.71) * mm, "radius": 1.5 * mm});
            skCircle(sketch, "E284.2.0.0", {"center": v(-60.74, 42.49) * mm, "radius": 1.5 * mm});
            skCircle(sketch, "E284.2.1.0", {"center": v(-60.74, 23.44) * mm, "radius": 1.5 * mm});
            skCircle(sketch, "E284.2.2.0", {"center": v(-60.74, 4.39) * mm, "radius": 1.5 * mm});
            skCircle(sketch, "E284.2.3.0", {"center": v(-60.74, -14.66) * mm, "radius": 1.5 * mm});
            skCircle(sketch, "E284.2.4.0", {"center": v(-60.74, -33.71) * mm, "radius": 1.5 * mm});
            skCircle(sketch, "E284.3.0.0", {"center": v(-41.69, 42.49) * mm, "radius": 1.5 * mm});
            skCircle(sketch, "E284.3.1.0", {"center": v(-41.69, 23.44) * mm, "radius": 1.5 * mm});
            skCircle(sketch, "E284.3.2.0", {"center": v(-41.69, 4.39) * mm, "radius": 1.5 * mm});
            skCircle(sketch, "E284.3.3.0", {"center": v(-41.69, -14.66) * mm, "radius": 1.5 * mm});
            skCircle(sketch, "E284.3.4.0", {"center": v(-41.69, -33.71) * mm, "radius": 1.5 * mm});
            skCircle(sketch, "E284.4.0.0", {"center": v(-22.64, 42.49) * mm, "radius": 1.5 * mm});
            skCircle(sketch, "E284.4.1.0", {"center": v(-22.64, 23.44) * mm, "radius": 1.5 * mm});
            skCircle(sketch, "E284.4.2.0", {"center": v(-22.64, 4.39) * mm, "radius": 1.5 * mm});
            skCircle(sketch, "E284.4.3.0", {"center": v(-22.64, -14.66) * mm, "radius": 1.5 * mm});
            skCircle(sketch, "E284.4.4.0", {"center": v(-22.64, -33.71) * mm, "radius": 1.5 * mm});
            skCircle(sketch, "E284.5.0.0", {"center": v(-3.59, 42.49) * mm, "radius": 1.5 * mm});
            skCircle(sketch, "E284.5.1.0", {"center": v(-3.59, 23.44) * mm, "radius": 1.5 * mm});
            skCircle(sketch, "E284.5.2.0", {"center": v(-3.59, 4.39) * mm, "radius": 1.5 * mm});
            skCircle(sketch, "E284.5.3.0", {"center": v(-3.59, -14.66) * mm, "radius": 1.5 * mm});
            skCircle(sketch, "E284.5.4.0", {"center": v(-3.59, -33.71) * mm, "radius": 1.5 * mm});
            skCircle(sketch, "E284.6.0.0", {"center": v(15.46, 42.49) * mm, "radius": 1.5 * mm});
            skCircle(sketch, "E284.6.1.0", {"center": v(15.46, 23.44) * mm, "radius": 1.5 * mm});
            skCircle(sketch, "E284.6.2.0", {"center": v(15.46, 4.39) * mm, "radius": 1.5 * mm});
            skCircle(sketch, "E284.6.3.0", {"center": v(15.46, -14.66) * mm, "radius": 1.5 * mm});
            skCircle(sketch, "E284.6.4.0", {"center": v(15.46, -33.71) * mm, "radius": 1.5 * mm});
            skCircle(sketch, "E284.7.0.0", {"center": v(34.51, 42.49) * mm, "radius": 1.5 * mm});
            skCircle(sketch, "E284.7.1.0", {"center": v(34.51, 23.44) * mm, "radius": 1.5 * mm});
            skCircle(sketch, "E284.7.2.0", {"center": v(34.51, 4.39) * mm, "radius": 1.5 * mm});
            skCircle(sketch, "E284.7.3.0", {"center": v(34.51, -14.66) * mm, "radius": 1.5 * mm});
            skCircle(sketch, "E284.7.4.0", {"center": v(34.51, -33.71) * mm, "radius": 1.5 * mm});
            skCircle(sketch, "E284.8.0.0", {"center": v(53.56, 42.49) * mm, "radius": 1.5 * mm});
            skCircle(sketch, "E284.8.1.0", {"center": v(53.56, 23.44) * mm, "radius": 1.5 * mm});
            skCircle(sketch, "E284.8.2.0", {"center": v(53.56, 4.39) * mm, "radius": 1.5 * mm});
            skCircle(sketch, "E284.8.3.0", {"center": v(53.56, -14.66) * mm, "radius": 1.5 * mm});
            skCircle(sketch, "E284.8.4.0", {"center": v(53.56, -33.71) * mm, "radius": 1.5 * mm});
            skCircle(sketch, "E284.9.0.0", {"center": v(72.61, 42.49) * mm, "radius": 1.5 * mm});
            skCircle(sketch, "E284.9.1.0", {"center": v(72.61, 23.44) * mm, "radius": 1.5 * mm});
            skCircle(sketch, "E284.9.2.0", {"center": v(72.61, 4.39) * mm, "radius": 1.5 * mm});
            skCircle(sketch, "E284.9.3.0", {"center": v(72.61, -14.66) * mm, "radius": 1.5 * mm});
            skCircle(sketch, "E284.9.4.0", {"center": v(72.61, -33.71) * mm, "radius": 1.5 * mm});
            skCircle(sketch, "E284.10.0.0", {"center": v(91.66, 42.49) * mm, "radius": 1.5 * mm});
            skCircle(sketch, "E284.10.1.0", {"center": v(91.66, 23.44) * mm, "radius": 1.5 * mm});
            skCircle(sketch, "E284.10.2.0", {"center": v(91.66, 4.39) * mm, "radius": 1.5 * mm});
            skCircle(sketch, "E284.10.3.0", {"center": v(91.66, -14.66) * mm, "radius": 1.5 * mm});
            skCircle(sketch, "E284.10.4.0", {"center": v(91.66, -33.71) * mm, "radius": 1.5 * mm});
            skCircle(sketch, "E284.11.0.0", {"center": v(110.71, 42.49) * mm, "radius": 1.5 * mm});
            skCircle(sketch, "E284.11.1.0", {"center": v(110.71, 23.44) * mm, "radius": 1.5 * mm});
            skCircle(sketch, "E284.11.2.0", {"center": v(110.71, 4.39) * mm, "radius": 1.5 * mm});
            skCircle(sketch, "E284.11.3.0", {"center": v(110.71, -14.66) * mm, "radius": 1.5 * mm});
            skCircle(sketch, "E284.11.4.0", {"center": v(110.71, -33.71) * mm, "radius": 1.5 * mm});
            skLineSegment(sketch, "E284.direction1", {"start": v(-98.84, 42.49) * mm, "end": v(-79.79, 42.49) * mm, "construction": true});
            skLineSegment(sketch, "E284.direction2", {"start": v(-98.84, 42.49) * mm, "end": v(-98.84, 23.44) * mm, "construction": true});
            skSolve(sketch);
        }
        {
            var Q0;
            Q0=makeQuery(id+"F1.opExtrude","CAP_FACE",FACE,{"disambiguationData":[OSD([sQuery(id+"F0.wireOp",EDGE,"E0"),sQuery(id+"F0.wireOp",EDGE,"E1"),sQuery(id+"F0.wireOp",EDGE,"E2"),sQuery(id+"F0.wireOp",EDGE,"E3"),sQuery(id+"F0.wireOp",EDGE,"E4"),sQuery(id+"F0.wireOp",EDGE,"E5"),sQuery(id+"F0.wireOp",EDGE,"E6"),sQuery(id+"F0.wireOp",EDGE,"E7"),sQuery(id+"F0.wireOp",EDGE,"E8"),sQuery(id+"F0.wireOp",EDGE,"E9"),sQuery(id+"F0.wireOp",EDGE,"E10"),sQuery(id+"F0.wireOp",EDGE,"E11"),sQuery(id+"F0.wireOp",EDGE,"E12"),sQuery(id+"F0.wireOp",EDGE,"E13"),sQuery(id+"F0.wireOp",EDGE,"E14"),sQuery(id+"F0.wireOp",EDGE,"E15"),sQuery(id+"F0.wireOp",EDGE,"E16"),sQuery(id+"F0.wireOp",EDGE,"E17"),sQuery(id+"F0.wireOp",EDGE,"E18"),sQuery(id+"F0.wireOp",EDGE,"E19"),sQuery(id+"F0.wireOp",EDGE,"E20"),sQuery(id+"F0.wireOp",EDGE,"E21"),sQuery(id+"F0.wireOp",EDGE,"E22"),sQuery(id+"F0.wireOp",EDGE,"E23"),sQuery(id+"F0.wireOp",EDGE,"E24"),sQuery(id+"F0.wireOp",EDGE,"E25"),sQuery(id+"F0.wireOp",EDGE,"E26"),sQuery(id+"F0.wireOp",EDGE,"E27"),sQuery(id+"F0.wireOp",EDGE,"E28"),sQuery(id+"F0.wireOp",EDGE,"E29"),sQuery(id+"F0.wireOp",EDGE,"E30"),sQuery(id+"F0.wireOp",EDGE,"E31"),sQuery(id+"F0.wireOp",EDGE,"E32"),sQuery(id+"F0.wireOp",EDGE,"E33"),sQuery(id+"F0.wireOp",EDGE,"E34"),sQuery(id+"F0.wireOp",EDGE,"E35"),sQuery(id+"F0.wireOp",EDGE,"E36"),sQuery(id+"F0.wireOp",EDGE,"E37"),sQuery(id+"F0.wireOp",EDGE,"E38"),sQuery(id+"F0.wireOp",EDGE,"E39"),sQuery(id+"F0.wireOp",EDGE,"E40"),sQuery(id+"F0.wireOp",EDGE,"E41"),sQuery(id+"F0.wireOp",EDGE,"E42"),sQuery(id+"F0.wireOp",EDGE,"E43"),sQuery(id+"F0.wireOp",EDGE,"E44"),sQuery(id+"F0.wireOp",EDGE,"E45"),sQuery(id+"F0.wireOp",EDGE,"E46"),sQuery(id+"F0.wireOp",EDGE,"E47"),sQuery(id+"F0.wireOp",EDGE,"E48"),sQuery(id+"F0.wireOp",EDGE,"E49"),sQuery(id+"F0.wireOp",EDGE,"E50"),sQuery(id+"F0.wireOp",EDGE,"E51"),sQuery(id+"F0.wireOp",EDGE,"E52"),sQuery(id+"F0.wireOp",EDGE,"E53"),sQuery(id+"F0.wireOp",EDGE,"E54"),sQuery(id+"F0.wireOp",EDGE,"E55"),sQuery(id+"F0.wireOp",EDGE,"E56"),sQuery(id+"F0.wireOp",EDGE,"E57"),sQuery(id+"F0.wireOp",EDGE,"E58"),sQuery(id+"F0.wireOp",EDGE,"E59"),sQuery(id+"F0.wireOp",EDGE,"E60"),sQuery(id+"F0.wireOp",EDGE,"E61"),sQuery(id+"F0.wireOp",EDGE,"E62"),sQuery(id+"F0.wireOp",EDGE,"E63"),sQuery(id+"F0.wireOp",EDGE,"E64"),sQuery(id+"F0.wireOp",EDGE,"E65"),sQuery(id+"F0.wireOp",EDGE,"E66"),sQuery(id+"F0.wireOp",EDGE,"E67"),sQuery(id+"F0.wireOp",EDGE,"E68"),sQuery(id+"F0.wireOp",EDGE,"E69"),sQuery(id+"F0.wireOp",EDGE,"E70"),sQuery(id+"F0.wireOp",EDGE,"E71"),sQuery(id+"F0.wireOp",EDGE,"E72"),sQuery(id+"F0.wireOp",EDGE,"E73"),sQuery(id+"F0.wireOp",EDGE,"E74"),sQuery(id+"F0.wireOp",EDGE,"E75"),sQuery(id+"F0.wireOp",EDGE,"E76"),sQuery(id+"F0.wireOp",EDGE,"E77"),sQuery(id+"F0.wireOp",EDGE,"E78"),sQuery(id+"F0.wireOp",EDGE,"E79"),sQuery(id+"F0.wireOp",EDGE,"E80"),sQuery(id+"F0.wireOp",EDGE,"E81"),sQuery(id+"F0.wireOp",EDGE,"E82"),sQuery(id+"F0.wireOp",EDGE,"E83"),sQuery(id+"F0.wireOp",EDGE,"E84"),sQuery(id+"F0.wireOp",EDGE,"E85"),sQuery(id+"F0.wireOp",EDGE,"E86"),sQuery(id+"F0.wireOp",EDGE,"E87"),sQuery(id+"F0.wireOp",EDGE,"E88"),sQuery(id+"F0.wireOp",EDGE,"E89"),sQuery(id+"F0.wireOp",EDGE,"E90"),sQuery(id+"F0.wireOp",EDGE,"E91"),sQuery(id+"F0.wireOp",EDGE,"E92"),sQuery(id+"F0.wireOp",EDGE,"E93"),sQuery(id+"F0.wireOp",EDGE,"E94"),sQuery(id+"F0.wireOp",EDGE,"E95"),sQuery(id+"F0.wireOp",EDGE,"E96"),sQuery(id+"F0.wireOp",EDGE,"E97"),sQuery(id+"F0.wireOp",EDGE,"E98"),sQuery(id+"F0.wireOp",EDGE,"E99"),sQuery(id+"F0.wireOp",EDGE,"E100"),sQuery(id+"F0.wireOp",EDGE,"E101"),sQuery(id+"F0.wireOp",EDGE,"E102"),sQuery(id+"F0.wireOp",EDGE,"E103"),sQuery(id+"F0.wireOp",EDGE,"E104"),sQuery(id+"F0.wireOp",EDGE,"E105"),sQuery(id+"F0.wireOp",EDGE,"E106"),sQuery(id+"F0.wireOp",EDGE,"E107"),sQuery(id+"F0.wireOp",EDGE,"E108"),sQuery(id+"F0.wireOp",EDGE,"E109"),sQuery(id+"F0.wireOp",EDGE,"E110"),sQuery(id+"F0.wireOp",EDGE,"E111"),sQuery(id+"F0.wireOp",EDGE,"E112"),sQuery(id+"F0.wireOp",EDGE,"E113"),sQuery(id+"F0.wireOp",EDGE,"E114"),sQuery(id+"F0.wireOp",EDGE,"E115"),sQuery(id+"F0.wireOp",EDGE,"E116"),sQuery(id+"F0.wireOp",EDGE,"E117"),sQuery(id+"F0.wireOp",EDGE,"E118"),sQuery(id+"F0.wireOp",EDGE,"E119"),sQuery(id+"F0.wireOp",EDGE,"E120"),sQuery(id+"F0.wireOp",EDGE,"E121"),sQuery(id+"F0.wireOp",EDGE,"E122"),sQuery(id+"F0.wireOp",EDGE,"E123"),sQuery(id+"F0.wireOp",EDGE,"E124"),sQuery(id+"F0.wireOp",EDGE,"E125"),sQuery(id+"F0.wireOp",EDGE,"E126"),sQuery(id+"F0.wireOp",EDGE,"E127"),sQuery(id+"F0.wireOp",EDGE,"E128"),sQuery(id+"F0.wireOp",EDGE,"E129"),sQuery(id+"F0.wireOp",EDGE,"E130"),sQuery(id+"F0.wireOp",EDGE,"E131"),sQuery(id+"F0.wireOp",EDGE,"E132"),sQuery(id+"F0.wireOp",EDGE,"E133"),sQuery(id+"F0.wireOp",EDGE,"E134"),sQuery(id+"F0.wireOp",EDGE,"E135"),sQuery(id+"F0.wireOp",EDGE,"E136"),sQuery(id+"F0.wireOp",EDGE,"E137"),sQuery(id+"F0.wireOp",EDGE,"E138"),sQuery(id+"F0.wireOp",EDGE,"E139"),sQuery(id+"F0.wireOp",EDGE,"E140"),sQuery(id+"F0.wireOp",EDGE,"E141"),sQuery(id+"F0.wireOp",EDGE,"E142"),sQuery(id+"F0.wireOp",EDGE,"E143"),sQuery(id+"F0.wireOp",EDGE,"E144"),sQuery(id+"F0.wireOp",EDGE,"E145"),sQuery(id+"F0.wireOp",EDGE,"E146"),sQuery(id+"F0.wireOp",EDGE,"E147"),sQuery(id+"F0.wireOp",EDGE,"E148"),sQuery(id+"F0.wireOp",EDGE,"E149"),sQuery(id+"F0.wireOp",EDGE,"E150"),sQuery(id+"F0.wireOp",EDGE,"E151"),sQuery(id+"F0.wireOp",EDGE,"E152"),sQuery(id+"F0.wireOp",EDGE,"E153"),sQuery(id+"F0.wireOp",EDGE,"E154"),sQuery(id+"F0.wireOp",EDGE,"E155"),sQuery(id+"F0.wireOp",EDGE,"E156"),sQuery(id+"F0.wireOp",EDGE,"E157"),sQuery(id+"F0.wireOp",EDGE,"E158"),sQuery(id+"F0.wireOp",EDGE,"E159"),sQuery(id+"F0.wireOp",EDGE,"E160"),sQuery(id+"F0.wireOp",EDGE,"E161"),sQuery(id+"F0.wireOp",EDGE,"E162"),sQuery(id+"F0.wireOp",EDGE,"E163"),sQuery(id+"F0.wireOp",EDGE,"E164"),sQuery(id+"F0.wireOp",EDGE,"E165"),sQuery(id+"F0.wireOp",EDGE,"E166"),sQuery(id+"F0.wireOp",EDGE,"E167"),sQuery(id+"F0.wireOp",EDGE,"E168"),sQuery(id+"F0.wireOp",EDGE,"E169"),sQuery(id+"F0.wireOp",EDGE,"E170"),sQuery(id+"F0.wireOp",EDGE,"E171"),sQuery(id+"F0.wireOp",EDGE,"E172"),sQuery(id+"F0.wireOp",EDGE,"E173"),sQuery(id+"F0.wireOp",EDGE,"E174"),sQuery(id+"F0.wireOp",EDGE,"E175"),sQuery(id+"F0.wireOp",EDGE,"E176"),sQuery(id+"F0.wireOp",EDGE,"E177"),sQuery(id+"F0.wireOp",EDGE,"E178"),sQuery(id+"F0.wireOp",EDGE,"E179"),sQuery(id+"F0.wireOp",EDGE,"E180"),sQuery(id+"F0.wireOp",EDGE,"E181"),sQuery(id+"F0.wireOp",EDGE,"E182"),sQuery(id+"F0.wireOp",EDGE,"E183"),sQuery(id+"F0.wireOp",EDGE,"E184"),sQuery(id+"F0.wireOp",EDGE,"E185"),sQuery(id+"F0.wireOp",EDGE,"E186"),sQuery(id+"F0.wireOp",EDGE,"E187"),sQuery(id+"F0.wireOp",EDGE,"E188"),sQuery(id+"F0.wireOp",EDGE,"E189"),sQuery(id+"F0.wireOp",EDGE,"E190"),sQuery(id+"F0.wireOp",EDGE,"E191"),sQuery(id+"F0.wireOp",EDGE,"E192"),sQuery(id+"F0.wireOp",EDGE,"E193"),sQuery(id+"F0.wireOp",EDGE,"E194"),sQuery(id+"F0.wireOp",EDGE,"E195"),sQuery(id+"F0.wireOp",EDGE,"E196"),sQuery(id+"F0.wireOp",EDGE,"E197"),sQuery(id+"F0.wireOp",EDGE,"E198"),sQuery(id+"F0.wireOp",EDGE,"E199"),sQuery(id+"F0.wireOp",EDGE,"E200"),sQuery(id+"F0.wireOp",EDGE,"E201"),sQuery(id+"F0.wireOp",EDGE,"E202"),sQuery(id+"F0.wireOp",EDGE,"E203"),sQuery(id+"F0.wireOp",EDGE,"E204"),sQuery(id+"F0.wireOp",EDGE,"E205"),sQuery(id+"F0.wireOp",EDGE,"E206"),sQuery(id+"F0.wireOp",EDGE,"E207"),sQuery(id+"F0.wireOp",EDGE,"E208"),sQuery(id+"F0.wireOp",EDGE,"E209"),sQuery(id+"F0.wireOp",EDGE,"E210"),sQuery(id+"F0.wireOp",EDGE,"E211"),sQuery(id+"F0.wireOp",EDGE,"E212"),sQuery(id+"F0.wireOp",EDGE,"E213"),sQuery(id+"F0.wireOp",EDGE,"E214"),sQuery(id+"F0.wireOp",EDGE,"E215"),sQuery(id+"F0.wireOp",EDGE,"E216"),sQuery(id+"F0.wireOp",EDGE,"E217"),sQuery(id+"F0.wireOp",EDGE,"E218"),sQuery(id+"F0.wireOp",EDGE,"E219"),sQuery(id+"F0.wireOp",EDGE,"E220"),sQuery(id+"F0.wireOp",EDGE,"E221"),sQuery(id+"F0.wireOp",EDGE,"E222"),sQuery(id+"F0.wireOp",EDGE,"E223"),sQuery(id+"F0.wireOp",EDGE,"E224"),sQuery(id+"F0.wireOp",EDGE,"E225"),sQuery(id+"F0.wireOp",EDGE,"E226"),sQuery(id+"F0.wireOp",EDGE,"E227"),sQuery(id+"F0.wireOp",EDGE,"E228"),sQuery(id+"F0.wireOp",EDGE,"E229"),sQuery(id+"F0.wireOp",EDGE,"E230"),sQuery(id+"F0.wireOp",EDGE,"E231"),sQuery(id+"F0.wireOp",EDGE,"E232"),sQuery(id+"F0.wireOp",EDGE,"E233"),sQuery(id+"F0.wireOp",EDGE,"E234"),sQuery(id+"F0.wireOp",EDGE,"E235"),sQuery(id+"F0.wireOp",EDGE,"E236"),sQuery(id+"F0.wireOp",EDGE,"E237"),sQuery(id+"F0.wireOp",EDGE,"E238"),sQuery(id+"F0.wireOp",EDGE,"E239"),sQuery(id+"F0.wireOp",EDGE,"E240"),sQuery(id+"F0.wireOp",EDGE,"E241"),sQuery(id+"F0.wireOp",EDGE,"E242"),sQuery(id+"F0.wireOp",EDGE,"E243")])],"isStart":true});
            var sketch = newSketch(context, id + "F16", { "sketchPlane" : qUnion([Q0])});
            skCircle(sketch, "E285", {"center": v(-110.72, 30.61) * mm, "radius": 1.5 * mm});
            skLineSegment(sketch, "E286", {"start": v(-110.72, 30.61) * mm, "end": v(-111.78, 30.61) * mm});
            skLineSegment(sketch, "E287", {"start": v(-110.72, 30.61) * mm, "end": v(-110.72, 29.55) * mm});
            skCircle(sketch, "E288.0.1.0", {"center": v(-110.72, 11.56) * mm, "radius": 1.5 * mm});
            skCircle(sketch, "E288.0.2.0", {"center": v(-110.72, -7.49) * mm, "radius": 1.5 * mm});
            skCircle(sketch, "E288.0.3.0", {"center": v(-110.72, -26.54) * mm, "radius": 1.5 * mm});
            skCircle(sketch, "E288.0.4.0", {"center": v(-110.72, -45.59) * mm, "radius": 1.5 * mm});
            skCircle(sketch, "E288.1.0.0", {"center": v(-91.67, 30.61) * mm, "radius": 1.5 * mm});
            skCircle(sketch, "E288.1.1.0", {"center": v(-91.67, 11.56) * mm, "radius": 1.5 * mm});
            skCircle(sketch, "E288.1.2.0", {"center": v(-91.67, -7.49) * mm, "radius": 1.5 * mm});
            skCircle(sketch, "E288.1.3.0", {"center": v(-91.67, -26.54) * mm, "radius": 1.5 * mm});
            skCircle(sketch, "E288.1.4.0", {"center": v(-91.67, -45.59) * mm, "radius": 1.5 * mm});
            skCircle(sketch, "E288.2.0.0", {"center": v(-72.62, 30.61) * mm, "radius": 1.5 * mm});
            skCircle(sketch, "E288.2.1.0", {"center": v(-72.62, 11.56) * mm, "radius": 1.5 * mm});
            skCircle(sketch, "E288.2.2.0", {"center": v(-72.62, -7.49) * mm, "radius": 1.5 * mm});
            skCircle(sketch, "E288.2.3.0", {"center": v(-72.62, -26.54) * mm, "radius": 1.5 * mm});
            skCircle(sketch, "E288.2.4.0", {"center": v(-72.62, -45.59) * mm, "radius": 1.5 * mm});
            skCircle(sketch, "E288.3.0.0", {"center": v(-53.57, 30.61) * mm, "radius": 1.5 * mm});
            skCircle(sketch, "E288.3.1.0", {"center": v(-53.57, 11.56) * mm, "radius": 1.5 * mm});
            skCircle(sketch, "E288.3.2.0", {"center": v(-53.57, -7.49) * mm, "radius": 1.5 * mm});
            skCircle(sketch, "E288.3.3.0", {"center": v(-53.57, -26.54) * mm, "radius": 1.5 * mm});
            skCircle(sketch, "E288.3.4.0", {"center": v(-53.57, -45.59) * mm, "radius": 1.5 * mm});
            skCircle(sketch, "E288.4.0.0", {"center": v(-34.52, 30.61) * mm, "radius": 1.5 * mm});
            skCircle(sketch, "E288.4.1.0", {"center": v(-34.52, 11.56) * mm, "radius": 1.5 * mm});
            skCircle(sketch, "E288.4.2.0", {"center": v(-34.52, -7.49) * mm, "radius": 1.5 * mm});
            skCircle(sketch, "E288.4.3.0", {"center": v(-34.52, -26.54) * mm, "radius": 1.5 * mm});
            skCircle(sketch, "E288.4.4.0", {"center": v(-34.52, -45.59) * mm, "radius": 1.5 * mm});
            skCircle(sketch, "E288.5.0.0", {"center": v(-15.47, 30.61) * mm, "radius": 1.5 * mm});
            skCircle(sketch, "E288.5.1.0", {"center": v(-15.47, 11.56) * mm, "radius": 1.5 * mm});
            skCircle(sketch, "E288.5.2.0", {"center": v(-15.47, -7.49) * mm, "radius": 1.5 * mm});
            skCircle(sketch, "E288.5.3.0", {"center": v(-15.47, -26.54) * mm, "radius": 1.5 * mm});
            skCircle(sketch, "E288.5.4.0", {"center": v(-15.47, -45.59) * mm, "radius": 1.5 * mm});
            skCircle(sketch, "E288.6.0.0", {"center": v(3.58, 30.61) * mm, "radius": 1.5 * mm});
            skCircle(sketch, "E288.6.1.0", {"center": v(3.58, 11.56) * mm, "radius": 1.5 * mm});
            skCircle(sketch, "E288.6.2.0", {"center": v(3.58, -7.49) * mm, "radius": 1.5 * mm});
            skCircle(sketch, "E288.6.3.0", {"center": v(3.58, -26.54) * mm, "radius": 1.5 * mm});
            skCircle(sketch, "E288.6.4.0", {"center": v(3.58, -45.59) * mm, "radius": 1.5 * mm});
            skCircle(sketch, "E288.7.0.0", {"center": v(22.63, 30.61) * mm, "radius": 1.5 * mm});
            skCircle(sketch, "E288.7.1.0", {"center": v(22.63, 11.56) * mm, "radius": 1.5 * mm});
            skCircle(sketch, "E288.7.2.0", {"center": v(22.63, -7.49) * mm, "radius": 1.5 * mm});
            skCircle(sketch, "E288.7.3.0", {"center": v(22.63, -26.54) * mm, "radius": 1.5 * mm});
            skCircle(sketch, "E288.7.4.0", {"center": v(22.63, -45.59) * mm, "radius": 1.5 * mm});
            skCircle(sketch, "E288.8.0.0", {"center": v(41.68, 30.61) * mm, "radius": 1.5 * mm});
            skCircle(sketch, "E288.8.1.0", {"center": v(41.68, 11.56) * mm, "radius": 1.5 * mm});
            skCircle(sketch, "E288.8.2.0", {"center": v(41.68, -7.49) * mm, "radius": 1.5 * mm});
            skCircle(sketch, "E288.8.3.0", {"center": v(41.68, -26.54) * mm, "radius": 1.5 * mm});
            skCircle(sketch, "E288.8.4.0", {"center": v(41.68, -45.59) * mm, "radius": 1.5 * mm});
            skCircle(sketch, "E288.9.0.0", {"center": v(60.73, 30.61) * mm, "radius": 1.5 * mm});
            skCircle(sketch, "E288.9.1.0", {"center": v(60.73, 11.56) * mm, "radius": 1.5 * mm});
            skCircle(sketch, "E288.9.2.0", {"center": v(60.73, -7.49) * mm, "radius": 1.5 * mm});
            skCircle(sketch, "E288.9.3.0", {"center": v(60.73, -26.54) * mm, "radius": 1.5 * mm});
            skCircle(sketch, "E288.9.4.0", {"center": v(60.73, -45.59) * mm, "radius": 1.5 * mm});
            skCircle(sketch, "E288.10.0.0", {"center": v(79.78, 30.61) * mm, "radius": 1.5 * mm});
            skCircle(sketch, "E288.10.1.0", {"center": v(79.78, 11.56) * mm, "radius": 1.5 * mm});
            skCircle(sketch, "E288.10.2.0", {"center": v(79.78, -7.49) * mm, "radius": 1.5 * mm});
            skCircle(sketch, "E288.10.3.0", {"center": v(79.78, -26.54) * mm, "radius": 1.5 * mm});
            skCircle(sketch, "E288.10.4.0", {"center": v(79.78, -45.59) * mm, "radius": 1.5 * mm});
            skCircle(sketch, "E288.11.0.0", {"center": v(98.83, 30.61) * mm, "radius": 1.5 * mm});
            skCircle(sketch, "E288.11.1.0", {"center": v(98.83, 11.56) * mm, "radius": 1.5 * mm});
            skCircle(sketch, "E288.11.2.0", {"center": v(98.83, -7.49) * mm, "radius": 1.5 * mm});
            skCircle(sketch, "E288.11.3.0", {"center": v(98.83, -26.54) * mm, "radius": 1.5 * mm});
            skCircle(sketch, "E288.11.4.0", {"center": v(98.83, -45.59) * mm, "radius": 1.5 * mm});
            skLineSegment(sketch, "E288.direction1", {"start": v(-110.72, 30.61) * mm, "end": v(-91.67, 30.61) * mm, "construction": true});
            skLineSegment(sketch, "E288.direction2", {"start": v(-110.72, 30.61) * mm, "end": v(-110.72, 11.56) * mm, "construction": true});
            skSolve(sketch);
        }
        {
            var Q0;
            Q0=makeQuery(id+"F1.opExtrude","CAP_FACE",FACE,{"disambiguationData":[OSD([sQuery(id+"F0.wireOp",EDGE,"E0"),sQuery(id+"F0.wireOp",EDGE,"E1"),sQuery(id+"F0.wireOp",EDGE,"E2"),sQuery(id+"F0.wireOp",EDGE,"E3"),sQuery(id+"F0.wireOp",EDGE,"E4"),sQuery(id+"F0.wireOp",EDGE,"E5"),sQuery(id+"F0.wireOp",EDGE,"E6"),sQuery(id+"F0.wireOp",EDGE,"E7"),sQuery(id+"F0.wireOp",EDGE,"E8"),sQuery(id+"F0.wireOp",EDGE,"E9"),sQuery(id+"F0.wireOp",EDGE,"E10"),sQuery(id+"F0.wireOp",EDGE,"E11"),sQuery(id+"F0.wireOp",EDGE,"E12"),sQuery(id+"F0.wireOp",EDGE,"E13"),sQuery(id+"F0.wireOp",EDGE,"E14"),sQuery(id+"F0.wireOp",EDGE,"E15"),sQuery(id+"F0.wireOp",EDGE,"E16"),sQuery(id+"F0.wireOp",EDGE,"E17"),sQuery(id+"F0.wireOp",EDGE,"E18"),sQuery(id+"F0.wireOp",EDGE,"E19"),sQuery(id+"F0.wireOp",EDGE,"E20"),sQuery(id+"F0.wireOp",EDGE,"E21"),sQuery(id+"F0.wireOp",EDGE,"E22"),sQuery(id+"F0.wireOp",EDGE,"E23"),sQuery(id+"F0.wireOp",EDGE,"E24"),sQuery(id+"F0.wireOp",EDGE,"E25"),sQuery(id+"F0.wireOp",EDGE,"E26"),sQuery(id+"F0.wireOp",EDGE,"E27"),sQuery(id+"F0.wireOp",EDGE,"E28"),sQuery(id+"F0.wireOp",EDGE,"E29"),sQuery(id+"F0.wireOp",EDGE,"E30"),sQuery(id+"F0.wireOp",EDGE,"E31"),sQuery(id+"F0.wireOp",EDGE,"E32"),sQuery(id+"F0.wireOp",EDGE,"E33"),sQuery(id+"F0.wireOp",EDGE,"E34"),sQuery(id+"F0.wireOp",EDGE,"E35"),sQuery(id+"F0.wireOp",EDGE,"E36"),sQuery(id+"F0.wireOp",EDGE,"E37"),sQuery(id+"F0.wireOp",EDGE,"E38"),sQuery(id+"F0.wireOp",EDGE,"E39"),sQuery(id+"F0.wireOp",EDGE,"E40"),sQuery(id+"F0.wireOp",EDGE,"E41"),sQuery(id+"F0.wireOp",EDGE,"E42"),sQuery(id+"F0.wireOp",EDGE,"E43"),sQuery(id+"F0.wireOp",EDGE,"E44"),sQuery(id+"F0.wireOp",EDGE,"E45"),sQuery(id+"F0.wireOp",EDGE,"E46"),sQuery(id+"F0.wireOp",EDGE,"E47"),sQuery(id+"F0.wireOp",EDGE,"E48"),sQuery(id+"F0.wireOp",EDGE,"E49"),sQuery(id+"F0.wireOp",EDGE,"E50"),sQuery(id+"F0.wireOp",EDGE,"E51"),sQuery(id+"F0.wireOp",EDGE,"E52"),sQuery(id+"F0.wireOp",EDGE,"E53"),sQuery(id+"F0.wireOp",EDGE,"E54"),sQuery(id+"F0.wireOp",EDGE,"E55"),sQuery(id+"F0.wireOp",EDGE,"E56"),sQuery(id+"F0.wireOp",EDGE,"E57"),sQuery(id+"F0.wireOp",EDGE,"E58"),sQuery(id+"F0.wireOp",EDGE,"E59"),sQuery(id+"F0.wireOp",EDGE,"E60"),sQuery(id+"F0.wireOp",EDGE,"E61"),sQuery(id+"F0.wireOp",EDGE,"E62"),sQuery(id+"F0.wireOp",EDGE,"E63"),sQuery(id+"F0.wireOp",EDGE,"E64"),sQuery(id+"F0.wireOp",EDGE,"E65"),sQuery(id+"F0.wireOp",EDGE,"E66"),sQuery(id+"F0.wireOp",EDGE,"E67"),sQuery(id+"F0.wireOp",EDGE,"E68"),sQuery(id+"F0.wireOp",EDGE,"E69"),sQuery(id+"F0.wireOp",EDGE,"E70"),sQuery(id+"F0.wireOp",EDGE,"E71"),sQuery(id+"F0.wireOp",EDGE,"E72"),sQuery(id+"F0.wireOp",EDGE,"E73"),sQuery(id+"F0.wireOp",EDGE,"E74"),sQuery(id+"F0.wireOp",EDGE,"E75"),sQuery(id+"F0.wireOp",EDGE,"E76"),sQuery(id+"F0.wireOp",EDGE,"E77"),sQuery(id+"F0.wireOp",EDGE,"E78"),sQuery(id+"F0.wireOp",EDGE,"E79"),sQuery(id+"F0.wireOp",EDGE,"E80"),sQuery(id+"F0.wireOp",EDGE,"E81"),sQuery(id+"F0.wireOp",EDGE,"E82"),sQuery(id+"F0.wireOp",EDGE,"E83"),sQuery(id+"F0.wireOp",EDGE,"E84"),sQuery(id+"F0.wireOp",EDGE,"E85"),sQuery(id+"F0.wireOp",EDGE,"E86"),sQuery(id+"F0.wireOp",EDGE,"E87"),sQuery(id+"F0.wireOp",EDGE,"E88"),sQuery(id+"F0.wireOp",EDGE,"E89"),sQuery(id+"F0.wireOp",EDGE,"E90"),sQuery(id+"F0.wireOp",EDGE,"E91"),sQuery(id+"F0.wireOp",EDGE,"E92"),sQuery(id+"F0.wireOp",EDGE,"E93"),sQuery(id+"F0.wireOp",EDGE,"E94"),sQuery(id+"F0.wireOp",EDGE,"E95"),sQuery(id+"F0.wireOp",EDGE,"E96"),sQuery(id+"F0.wireOp",EDGE,"E97"),sQuery(id+"F0.wireOp",EDGE,"E98"),sQuery(id+"F0.wireOp",EDGE,"E99"),sQuery(id+"F0.wireOp",EDGE,"E100"),sQuery(id+"F0.wireOp",EDGE,"E101"),sQuery(id+"F0.wireOp",EDGE,"E102"),sQuery(id+"F0.wireOp",EDGE,"E103"),sQuery(id+"F0.wireOp",EDGE,"E104"),sQuery(id+"F0.wireOp",EDGE,"E105"),sQuery(id+"F0.wireOp",EDGE,"E106"),sQuery(id+"F0.wireOp",EDGE,"E107"),sQuery(id+"F0.wireOp",EDGE,"E108"),sQuery(id+"F0.wireOp",EDGE,"E109"),sQuery(id+"F0.wireOp",EDGE,"E110"),sQuery(id+"F0.wireOp",EDGE,"E111"),sQuery(id+"F0.wireOp",EDGE,"E112"),sQuery(id+"F0.wireOp",EDGE,"E113"),sQuery(id+"F0.wireOp",EDGE,"E114"),sQuery(id+"F0.wireOp",EDGE,"E115"),sQuery(id+"F0.wireOp",EDGE,"E116"),sQuery(id+"F0.wireOp",EDGE,"E117"),sQuery(id+"F0.wireOp",EDGE,"E118"),sQuery(id+"F0.wireOp",EDGE,"E119"),sQuery(id+"F0.wireOp",EDGE,"E120"),sQuery(id+"F0.wireOp",EDGE,"E121"),sQuery(id+"F0.wireOp",EDGE,"E122"),sQuery(id+"F0.wireOp",EDGE,"E123"),sQuery(id+"F0.wireOp",EDGE,"E124"),sQuery(id+"F0.wireOp",EDGE,"E125"),sQuery(id+"F0.wireOp",EDGE,"E126"),sQuery(id+"F0.wireOp",EDGE,"E127"),sQuery(id+"F0.wireOp",EDGE,"E128"),sQuery(id+"F0.wireOp",EDGE,"E129"),sQuery(id+"F0.wireOp",EDGE,"E130"),sQuery(id+"F0.wireOp",EDGE,"E131"),sQuery(id+"F0.wireOp",EDGE,"E132"),sQuery(id+"F0.wireOp",EDGE,"E133"),sQuery(id+"F0.wireOp",EDGE,"E134"),sQuery(id+"F0.wireOp",EDGE,"E135"),sQuery(id+"F0.wireOp",EDGE,"E136"),sQuery(id+"F0.wireOp",EDGE,"E137"),sQuery(id+"F0.wireOp",EDGE,"E138"),sQuery(id+"F0.wireOp",EDGE,"E139"),sQuery(id+"F0.wireOp",EDGE,"E140"),sQuery(id+"F0.wireOp",EDGE,"E141"),sQuery(id+"F0.wireOp",EDGE,"E142"),sQuery(id+"F0.wireOp",EDGE,"E143"),sQuery(id+"F0.wireOp",EDGE,"E144"),sQuery(id+"F0.wireOp",EDGE,"E145"),sQuery(id+"F0.wireOp",EDGE,"E146"),sQuery(id+"F0.wireOp",EDGE,"E147"),sQuery(id+"F0.wireOp",EDGE,"E148"),sQuery(id+"F0.wireOp",EDGE,"E149"),sQuery(id+"F0.wireOp",EDGE,"E150"),sQuery(id+"F0.wireOp",EDGE,"E151"),sQuery(id+"F0.wireOp",EDGE,"E152"),sQuery(id+"F0.wireOp",EDGE,"E153"),sQuery(id+"F0.wireOp",EDGE,"E154"),sQuery(id+"F0.wireOp",EDGE,"E155"),sQuery(id+"F0.wireOp",EDGE,"E156"),sQuery(id+"F0.wireOp",EDGE,"E157"),sQuery(id+"F0.wireOp",EDGE,"E158"),sQuery(id+"F0.wireOp",EDGE,"E159"),sQuery(id+"F0.wireOp",EDGE,"E160"),sQuery(id+"F0.wireOp",EDGE,"E161"),sQuery(id+"F0.wireOp",EDGE,"E162"),sQuery(id+"F0.wireOp",EDGE,"E163"),sQuery(id+"F0.wireOp",EDGE,"E164"),sQuery(id+"F0.wireOp",EDGE,"E165"),sQuery(id+"F0.wireOp",EDGE,"E166"),sQuery(id+"F0.wireOp",EDGE,"E167"),sQuery(id+"F0.wireOp",EDGE,"E168"),sQuery(id+"F0.wireOp",EDGE,"E169"),sQuery(id+"F0.wireOp",EDGE,"E170"),sQuery(id+"F0.wireOp",EDGE,"E171"),sQuery(id+"F0.wireOp",EDGE,"E172"),sQuery(id+"F0.wireOp",EDGE,"E173"),sQuery(id+"F0.wireOp",EDGE,"E174"),sQuery(id+"F0.wireOp",EDGE,"E175"),sQuery(id+"F0.wireOp",EDGE,"E176"),sQuery(id+"F0.wireOp",EDGE,"E177"),sQuery(id+"F0.wireOp",EDGE,"E178"),sQuery(id+"F0.wireOp",EDGE,"E179"),sQuery(id+"F0.wireOp",EDGE,"E180"),sQuery(id+"F0.wireOp",EDGE,"E181"),sQuery(id+"F0.wireOp",EDGE,"E182"),sQuery(id+"F0.wireOp",EDGE,"E183"),sQuery(id+"F0.wireOp",EDGE,"E184"),sQuery(id+"F0.wireOp",EDGE,"E185"),sQuery(id+"F0.wireOp",EDGE,"E186"),sQuery(id+"F0.wireOp",EDGE,"E187"),sQuery(id+"F0.wireOp",EDGE,"E188"),sQuery(id+"F0.wireOp",EDGE,"E189"),sQuery(id+"F0.wireOp",EDGE,"E190"),sQuery(id+"F0.wireOp",EDGE,"E191"),sQuery(id+"F0.wireOp",EDGE,"E192"),sQuery(id+"F0.wireOp",EDGE,"E193"),sQuery(id+"F0.wireOp",EDGE,"E194"),sQuery(id+"F0.wireOp",EDGE,"E195"),sQuery(id+"F0.wireOp",EDGE,"E196"),sQuery(id+"F0.wireOp",EDGE,"E197"),sQuery(id+"F0.wireOp",EDGE,"E198"),sQuery(id+"F0.wireOp",EDGE,"E199"),sQuery(id+"F0.wireOp",EDGE,"E200"),sQuery(id+"F0.wireOp",EDGE,"E201"),sQuery(id+"F0.wireOp",EDGE,"E202"),sQuery(id+"F0.wireOp",EDGE,"E203"),sQuery(id+"F0.wireOp",EDGE,"E204"),sQuery(id+"F0.wireOp",EDGE,"E205"),sQuery(id+"F0.wireOp",EDGE,"E206"),sQuery(id+"F0.wireOp",EDGE,"E207"),sQuery(id+"F0.wireOp",EDGE,"E208"),sQuery(id+"F0.wireOp",EDGE,"E209"),sQuery(id+"F0.wireOp",EDGE,"E210"),sQuery(id+"F0.wireOp",EDGE,"E211"),sQuery(id+"F0.wireOp",EDGE,"E212"),sQuery(id+"F0.wireOp",EDGE,"E213"),sQuery(id+"F0.wireOp",EDGE,"E214"),sQuery(id+"F0.wireOp",EDGE,"E215"),sQuery(id+"F0.wireOp",EDGE,"E216"),sQuery(id+"F0.wireOp",EDGE,"E217"),sQuery(id+"F0.wireOp",EDGE,"E218"),sQuery(id+"F0.wireOp",EDGE,"E219"),sQuery(id+"F0.wireOp",EDGE,"E220"),sQuery(id+"F0.wireOp",EDGE,"E221"),sQuery(id+"F0.wireOp",EDGE,"E222"),sQuery(id+"F0.wireOp",EDGE,"E223"),sQuery(id+"F0.wireOp",EDGE,"E224"),sQuery(id+"F0.wireOp",EDGE,"E225"),sQuery(id+"F0.wireOp",EDGE,"E226"),sQuery(id+"F0.wireOp",EDGE,"E227"),sQuery(id+"F0.wireOp",EDGE,"E228"),sQuery(id+"F0.wireOp",EDGE,"E229"),sQuery(id+"F0.wireOp",EDGE,"E230"),sQuery(id+"F0.wireOp",EDGE,"E231"),sQuery(id+"F0.wireOp",EDGE,"E232"),sQuery(id+"F0.wireOp",EDGE,"E233"),sQuery(id+"F0.wireOp",EDGE,"E234"),sQuery(id+"F0.wireOp",EDGE,"E235"),sQuery(id+"F0.wireOp",EDGE,"E236"),sQuery(id+"F0.wireOp",EDGE,"E237"),sQuery(id+"F0.wireOp",EDGE,"E238"),sQuery(id+"F0.wireOp",EDGE,"E239"),sQuery(id+"F0.wireOp",EDGE,"E240"),sQuery(id+"F0.wireOp",EDGE,"E241"),sQuery(id+"F0.wireOp",EDGE,"E242"),sQuery(id+"F0.wireOp",EDGE,"E243")])],"isStart":true});
            var sketch = newSketch(context, id + "F17", { "sketchPlane" : qUnion([Q0])});
            skCircle(sketch, "E289", {"center": v(-98.84, 30.61) * mm, "radius": 1.5 * mm});
            skLineSegment(sketch, "E290", {"start": v(-98.84, 30.61) * mm, "end": v(-98.84, 29.55) * mm});
            skLineSegment(sketch, "E291", {"start": v(-98.84, 30.61) * mm, "end": v(-97.78, 30.61) * mm});
            skCircle(sketch, "E292.0.1.0", {"center": v(-98.84, 11.56) * mm, "radius": 1.5 * mm});
            skCircle(sketch, "E292.0.2.0", {"center": v(-98.84, -7.49) * mm, "radius": 1.5 * mm});
            skCircle(sketch, "E292.0.3.0", {"center": v(-98.84, -26.54) * mm, "radius": 1.5 * mm});
            skCircle(sketch, "E292.0.4.0", {"center": v(-98.84, -45.59) * mm, "radius": 1.5 * mm});
            skCircle(sketch, "E292.1.0.0", {"center": v(-79.79, 30.61) * mm, "radius": 1.5 * mm});
            skCircle(sketch, "E292.1.1.0", {"center": v(-79.79, 11.56) * mm, "radius": 1.5 * mm});
            skCircle(sketch, "E292.1.2.0", {"center": v(-79.79, -7.49) * mm, "radius": 1.5 * mm});
            skCircle(sketch, "E292.1.3.0", {"center": v(-79.79, -26.54) * mm, "radius": 1.5 * mm});
            skCircle(sketch, "E292.1.4.0", {"center": v(-79.79, -45.59) * mm, "radius": 1.5 * mm});
            skCircle(sketch, "E292.2.0.0", {"center": v(-60.74, 30.61) * mm, "radius": 1.5 * mm});
            skCircle(sketch, "E292.2.1.0", {"center": v(-60.74, 11.56) * mm, "radius": 1.5 * mm});
            skCircle(sketch, "E292.2.2.0", {"center": v(-60.74, -7.49) * mm, "radius": 1.5 * mm});
            skCircle(sketch, "E292.2.3.0", {"center": v(-60.74, -26.54) * mm, "radius": 1.5 * mm});
            skCircle(sketch, "E292.2.4.0", {"center": v(-60.74, -45.59) * mm, "radius": 1.5 * mm});
            skCircle(sketch, "E292.3.0.0", {"center": v(-41.69, 30.61) * mm, "radius": 1.5 * mm});
            skCircle(sketch, "E292.3.1.0", {"center": v(-41.69, 11.56) * mm, "radius": 1.5 * mm});
            skCircle(sketch, "E292.3.2.0", {"center": v(-41.69, -7.49) * mm, "radius": 1.5 * mm});
            skCircle(sketch, "E292.3.3.0", {"center": v(-41.69, -26.54) * mm, "radius": 1.5 * mm});
            skCircle(sketch, "E292.3.4.0", {"center": v(-41.69, -45.59) * mm, "radius": 1.5 * mm});
            skCircle(sketch, "E292.4.0.0", {"center": v(-22.64, 30.61) * mm, "radius": 1.5 * mm});
            skCircle(sketch, "E292.4.1.0", {"center": v(-22.64, 11.56) * mm, "radius": 1.5 * mm});
            skCircle(sketch, "E292.4.2.0", {"center": v(-22.64, -7.49) * mm, "radius": 1.5 * mm});
            skCircle(sketch, "E292.4.3.0", {"center": v(-22.64, -26.54) * mm, "radius": 1.5 * mm});
            skCircle(sketch, "E292.4.4.0", {"center": v(-22.64, -45.59) * mm, "radius": 1.5 * mm});
            skCircle(sketch, "E292.5.0.0", {"center": v(-3.59, 30.61) * mm, "radius": 1.5 * mm});
            skCircle(sketch, "E292.5.1.0", {"center": v(-3.59, 11.56) * mm, "radius": 1.5 * mm});
            skCircle(sketch, "E292.5.2.0", {"center": v(-3.59, -7.49) * mm, "radius": 1.5 * mm});
            skCircle(sketch, "E292.5.3.0", {"center": v(-3.59, -26.54) * mm, "radius": 1.5 * mm});
            skCircle(sketch, "E292.5.4.0", {"center": v(-3.59, -45.59) * mm, "radius": 1.5 * mm});
            skCircle(sketch, "E292.6.0.0", {"center": v(15.46, 30.61) * mm, "radius": 1.5 * mm});
            skCircle(sketch, "E292.6.1.0", {"center": v(15.46, 11.56) * mm, "radius": 1.5 * mm});
            skCircle(sketch, "E292.6.2.0", {"center": v(15.46, -7.49) * mm, "radius": 1.5 * mm});
            skCircle(sketch, "E292.6.3.0", {"center": v(15.46, -26.54) * mm, "radius": 1.5 * mm});
            skCircle(sketch, "E292.6.4.0", {"center": v(15.46, -45.59) * mm, "radius": 1.5 * mm});
            skCircle(sketch, "E292.7.0.0", {"center": v(34.51, 30.61) * mm, "radius": 1.5 * mm});
            skCircle(sketch, "E292.7.1.0", {"center": v(34.51, 11.56) * mm, "radius": 1.5 * mm});
            skCircle(sketch, "E292.7.2.0", {"center": v(34.51, -7.49) * mm, "radius": 1.5 * mm});
            skCircle(sketch, "E292.7.3.0", {"center": v(34.51, -26.54) * mm, "radius": 1.5 * mm});
            skCircle(sketch, "E292.7.4.0", {"center": v(34.51, -45.59) * mm, "radius": 1.5 * mm});
            skCircle(sketch, "E292.8.0.0", {"center": v(53.56, 30.61) * mm, "radius": 1.5 * mm});
            skCircle(sketch, "E292.8.1.0", {"center": v(53.56, 11.56) * mm, "radius": 1.5 * mm});
            skCircle(sketch, "E292.8.2.0", {"center": v(53.56, -7.49) * mm, "radius": 1.5 * mm});
            skCircle(sketch, "E292.8.3.0", {"center": v(53.56, -26.54) * mm, "radius": 1.5 * mm});
            skCircle(sketch, "E292.8.4.0", {"center": v(53.56, -45.59) * mm, "radius": 1.5 * mm});
            skCircle(sketch, "E292.9.0.0", {"center": v(72.61, 30.61) * mm, "radius": 1.5 * mm});
            skCircle(sketch, "E292.9.1.0", {"center": v(72.61, 11.56) * mm, "radius": 1.5 * mm});
            skCircle(sketch, "E292.9.2.0", {"center": v(72.61, -7.49) * mm, "radius": 1.5 * mm});
            skCircle(sketch, "E292.9.3.0", {"center": v(72.61, -26.54) * mm, "radius": 1.5 * mm});
            skCircle(sketch, "E292.9.4.0", {"center": v(72.61, -45.59) * mm, "radius": 1.5 * mm});
            skCircle(sketch, "E292.10.0.0", {"center": v(91.66, 30.61) * mm, "radius": 1.5 * mm});
            skCircle(sketch, "E292.10.1.0", {"center": v(91.66, 11.56) * mm, "radius": 1.5 * mm});
            skCircle(sketch, "E292.10.2.0", {"center": v(91.66, -7.49) * mm, "radius": 1.5 * mm});
            skCircle(sketch, "E292.10.3.0", {"center": v(91.66, -26.54) * mm, "radius": 1.5 * mm});
            skCircle(sketch, "E292.10.4.0", {"center": v(91.66, -45.59) * mm, "radius": 1.5 * mm});
            skCircle(sketch, "E292.11.0.0", {"center": v(110.71, 30.61) * mm, "radius": 1.5 * mm});
            skCircle(sketch, "E292.11.1.0", {"center": v(110.71, 11.56) * mm, "radius": 1.5 * mm});
            skCircle(sketch, "E292.11.2.0", {"center": v(110.71, -7.49) * mm, "radius": 1.5 * mm});
            skCircle(sketch, "E292.11.3.0", {"center": v(110.71, -26.54) * mm, "radius": 1.5 * mm});
            skCircle(sketch, "E292.11.4.0", {"center": v(110.71, -45.59) * mm, "radius": 1.5 * mm});
            skLineSegment(sketch, "E292.direction1", {"start": v(-98.84, 30.61) * mm, "end": v(-79.79, 30.61) * mm, "construction": true});
            skLineSegment(sketch, "E292.direction2", {"start": v(-98.84, 30.61) * mm, "end": v(-98.84, 11.56) * mm, "construction": true});
            skSolve(sketch);
        }
        {
            var Q0;
            Q0 = qSketchRegion(id + "F14", true);
            var Q1;
            Q1 = qSketchRegion(id + "F15", true);
            var Q2;
            Q2 = qSketchRegion(id + "F16", true);
            var Q3;
            Q3 = qSketchRegion(id + "F17", true);
            extrude(context, id + "F18", {"entities" : qUnion([Q0, Q1, Q2, Q3]), "operationType" : NewBodyOperationType.REMOVE, "oppositeDirection" : true, "depth" : 5 * mm, "offsetDistance" : 25 * mm});
        }
        {
            var Q0;
            Q0=makeQuery(id+"F1.opExtrude","CAP_FACE",FACE,{"disambiguationData":[OSD([sQuery(id+"F0.wireOp",EDGE,"E0"),sQuery(id+"F0.wireOp",EDGE,"E1"),sQuery(id+"F0.wireOp",EDGE,"E2"),sQuery(id+"F0.wireOp",EDGE,"E3"),sQuery(id+"F0.wireOp",EDGE,"E4"),sQuery(id+"F0.wireOp",EDGE,"E5"),sQuery(id+"F0.wireOp",EDGE,"E6"),sQuery(id+"F0.wireOp",EDGE,"E7"),sQuery(id+"F0.wireOp",EDGE,"E8"),sQuery(id+"F0.wireOp",EDGE,"E9"),sQuery(id+"F0.wireOp",EDGE,"E10"),sQuery(id+"F0.wireOp",EDGE,"E11"),sQuery(id+"F0.wireOp",EDGE,"E12"),sQuery(id+"F0.wireOp",EDGE,"E13"),sQuery(id+"F0.wireOp",EDGE,"E14"),sQuery(id+"F0.wireOp",EDGE,"E15"),sQuery(id+"F0.wireOp",EDGE,"E16"),sQuery(id+"F0.wireOp",EDGE,"E17"),sQuery(id+"F0.wireOp",EDGE,"E18"),sQuery(id+"F0.wireOp",EDGE,"E19"),sQuery(id+"F0.wireOp",EDGE,"E20"),sQuery(id+"F0.wireOp",EDGE,"E21"),sQuery(id+"F0.wireOp",EDGE,"E22"),sQuery(id+"F0.wireOp",EDGE,"E23"),sQuery(id+"F0.wireOp",EDGE,"E24"),sQuery(id+"F0.wireOp",EDGE,"E25"),sQuery(id+"F0.wireOp",EDGE,"E26"),sQuery(id+"F0.wireOp",EDGE,"E27"),sQuery(id+"F0.wireOp",EDGE,"E28"),sQuery(id+"F0.wireOp",EDGE,"E29"),sQuery(id+"F0.wireOp",EDGE,"E30"),sQuery(id+"F0.wireOp",EDGE,"E31"),sQuery(id+"F0.wireOp",EDGE,"E32"),sQuery(id+"F0.wireOp",EDGE,"E33"),sQuery(id+"F0.wireOp",EDGE,"E34"),sQuery(id+"F0.wireOp",EDGE,"E35"),sQuery(id+"F0.wireOp",EDGE,"E36"),sQuery(id+"F0.wireOp",EDGE,"E37"),sQuery(id+"F0.wireOp",EDGE,"E38"),sQuery(id+"F0.wireOp",EDGE,"E39"),sQuery(id+"F0.wireOp",EDGE,"E40"),sQuery(id+"F0.wireOp",EDGE,"E41"),sQuery(id+"F0.wireOp",EDGE,"E42"),sQuery(id+"F0.wireOp",EDGE,"E43"),sQuery(id+"F0.wireOp",EDGE,"E44"),sQuery(id+"F0.wireOp",EDGE,"E45"),sQuery(id+"F0.wireOp",EDGE,"E46"),sQuery(id+"F0.wireOp",EDGE,"E47"),sQuery(id+"F0.wireOp",EDGE,"E48"),sQuery(id+"F0.wireOp",EDGE,"E49"),sQuery(id+"F0.wireOp",EDGE,"E50"),sQuery(id+"F0.wireOp",EDGE,"E51"),sQuery(id+"F0.wireOp",EDGE,"E52"),sQuery(id+"F0.wireOp",EDGE,"E53"),sQuery(id+"F0.wireOp",EDGE,"E54"),sQuery(id+"F0.wireOp",EDGE,"E55"),sQuery(id+"F0.wireOp",EDGE,"E56"),sQuery(id+"F0.wireOp",EDGE,"E57"),sQuery(id+"F0.wireOp",EDGE,"E58"),sQuery(id+"F0.wireOp",EDGE,"E59"),sQuery(id+"F0.wireOp",EDGE,"E60"),sQuery(id+"F0.wireOp",EDGE,"E61"),sQuery(id+"F0.wireOp",EDGE,"E62"),sQuery(id+"F0.wireOp",EDGE,"E63"),sQuery(id+"F0.wireOp",EDGE,"E64"),sQuery(id+"F0.wireOp",EDGE,"E65"),sQuery(id+"F0.wireOp",EDGE,"E66"),sQuery(id+"F0.wireOp",EDGE,"E67"),sQuery(id+"F0.wireOp",EDGE,"E68"),sQuery(id+"F0.wireOp",EDGE,"E69"),sQuery(id+"F0.wireOp",EDGE,"E70"),sQuery(id+"F0.wireOp",EDGE,"E71"),sQuery(id+"F0.wireOp",EDGE,"E72"),sQuery(id+"F0.wireOp",EDGE,"E73"),sQuery(id+"F0.wireOp",EDGE,"E74"),sQuery(id+"F0.wireOp",EDGE,"E75"),sQuery(id+"F0.wireOp",EDGE,"E76"),sQuery(id+"F0.wireOp",EDGE,"E77"),sQuery(id+"F0.wireOp",EDGE,"E78"),sQuery(id+"F0.wireOp",EDGE,"E79"),sQuery(id+"F0.wireOp",EDGE,"E80"),sQuery(id+"F0.wireOp",EDGE,"E81"),sQuery(id+"F0.wireOp",EDGE,"E82"),sQuery(id+"F0.wireOp",EDGE,"E83"),sQuery(id+"F0.wireOp",EDGE,"E84"),sQuery(id+"F0.wireOp",EDGE,"E85"),sQuery(id+"F0.wireOp",EDGE,"E86"),sQuery(id+"F0.wireOp",EDGE,"E87"),sQuery(id+"F0.wireOp",EDGE,"E88"),sQuery(id+"F0.wireOp",EDGE,"E89"),sQuery(id+"F0.wireOp",EDGE,"E90"),sQuery(id+"F0.wireOp",EDGE,"E91"),sQuery(id+"F0.wireOp",EDGE,"E92"),sQuery(id+"F0.wireOp",EDGE,"E93"),sQuery(id+"F0.wireOp",EDGE,"E94"),sQuery(id+"F0.wireOp",EDGE,"E95"),sQuery(id+"F0.wireOp",EDGE,"E96"),sQuery(id+"F0.wireOp",EDGE,"E97"),sQuery(id+"F0.wireOp",EDGE,"E98"),sQuery(id+"F0.wireOp",EDGE,"E99"),sQuery(id+"F0.wireOp",EDGE,"E100"),sQuery(id+"F0.wireOp",EDGE,"E101"),sQuery(id+"F0.wireOp",EDGE,"E102"),sQuery(id+"F0.wireOp",EDGE,"E103"),sQuery(id+"F0.wireOp",EDGE,"E104"),sQuery(id+"F0.wireOp",EDGE,"E105"),sQuery(id+"F0.wireOp",EDGE,"E106"),sQuery(id+"F0.wireOp",EDGE,"E107"),sQuery(id+"F0.wireOp",EDGE,"E108"),sQuery(id+"F0.wireOp",EDGE,"E109"),sQuery(id+"F0.wireOp",EDGE,"E110"),sQuery(id+"F0.wireOp",EDGE,"E111"),sQuery(id+"F0.wireOp",EDGE,"E112"),sQuery(id+"F0.wireOp",EDGE,"E113"),sQuery(id+"F0.wireOp",EDGE,"E114"),sQuery(id+"F0.wireOp",EDGE,"E115"),sQuery(id+"F0.wireOp",EDGE,"E116"),sQuery(id+"F0.wireOp",EDGE,"E117"),sQuery(id+"F0.wireOp",EDGE,"E118"),sQuery(id+"F0.wireOp",EDGE,"E119"),sQuery(id+"F0.wireOp",EDGE,"E120"),sQuery(id+"F0.wireOp",EDGE,"E121"),sQuery(id+"F0.wireOp",EDGE,"E122"),sQuery(id+"F0.wireOp",EDGE,"E123"),sQuery(id+"F0.wireOp",EDGE,"E124"),sQuery(id+"F0.wireOp",EDGE,"E125"),sQuery(id+"F0.wireOp",EDGE,"E126"),sQuery(id+"F0.wireOp",EDGE,"E127"),sQuery(id+"F0.wireOp",EDGE,"E128"),sQuery(id+"F0.wireOp",EDGE,"E129"),sQuery(id+"F0.wireOp",EDGE,"E130"),sQuery(id+"F0.wireOp",EDGE,"E131"),sQuery(id+"F0.wireOp",EDGE,"E132"),sQuery(id+"F0.wireOp",EDGE,"E133"),sQuery(id+"F0.wireOp",EDGE,"E134"),sQuery(id+"F0.wireOp",EDGE,"E135"),sQuery(id+"F0.wireOp",EDGE,"E136"),sQuery(id+"F0.wireOp",EDGE,"E137"),sQuery(id+"F0.wireOp",EDGE,"E138"),sQuery(id+"F0.wireOp",EDGE,"E139"),sQuery(id+"F0.wireOp",EDGE,"E140"),sQuery(id+"F0.wireOp",EDGE,"E141"),sQuery(id+"F0.wireOp",EDGE,"E142"),sQuery(id+"F0.wireOp",EDGE,"E143"),sQuery(id+"F0.wireOp",EDGE,"E144"),sQuery(id+"F0.wireOp",EDGE,"E145"),sQuery(id+"F0.wireOp",EDGE,"E146"),sQuery(id+"F0.wireOp",EDGE,"E147"),sQuery(id+"F0.wireOp",EDGE,"E148"),sQuery(id+"F0.wireOp",EDGE,"E149"),sQuery(id+"F0.wireOp",EDGE,"E150"),sQuery(id+"F0.wireOp",EDGE,"E151"),sQuery(id+"F0.wireOp",EDGE,"E152"),sQuery(id+"F0.wireOp",EDGE,"E153"),sQuery(id+"F0.wireOp",EDGE,"E154"),sQuery(id+"F0.wireOp",EDGE,"E155"),sQuery(id+"F0.wireOp",EDGE,"E156"),sQuery(id+"F0.wireOp",EDGE,"E157"),sQuery(id+"F0.wireOp",EDGE,"E158"),sQuery(id+"F0.wireOp",EDGE,"E159"),sQuery(id+"F0.wireOp",EDGE,"E160"),sQuery(id+"F0.wireOp",EDGE,"E161"),sQuery(id+"F0.wireOp",EDGE,"E162"),sQuery(id+"F0.wireOp",EDGE,"E163"),sQuery(id+"F0.wireOp",EDGE,"E164"),sQuery(id+"F0.wireOp",EDGE,"E165"),sQuery(id+"F0.wireOp",EDGE,"E166"),sQuery(id+"F0.wireOp",EDGE,"E167"),sQuery(id+"F0.wireOp",EDGE,"E168"),sQuery(id+"F0.wireOp",EDGE,"E169"),sQuery(id+"F0.wireOp",EDGE,"E170"),sQuery(id+"F0.wireOp",EDGE,"E171"),sQuery(id+"F0.wireOp",EDGE,"E172"),sQuery(id+"F0.wireOp",EDGE,"E173"),sQuery(id+"F0.wireOp",EDGE,"E174"),sQuery(id+"F0.wireOp",EDGE,"E175"),sQuery(id+"F0.wireOp",EDGE,"E176"),sQuery(id+"F0.wireOp",EDGE,"E177"),sQuery(id+"F0.wireOp",EDGE,"E178"),sQuery(id+"F0.wireOp",EDGE,"E179"),sQuery(id+"F0.wireOp",EDGE,"E180"),sQuery(id+"F0.wireOp",EDGE,"E181"),sQuery(id+"F0.wireOp",EDGE,"E182"),sQuery(id+"F0.wireOp",EDGE,"E183"),sQuery(id+"F0.wireOp",EDGE,"E184"),sQuery(id+"F0.wireOp",EDGE,"E185"),sQuery(id+"F0.wireOp",EDGE,"E186"),sQuery(id+"F0.wireOp",EDGE,"E187"),sQuery(id+"F0.wireOp",EDGE,"E188"),sQuery(id+"F0.wireOp",EDGE,"E189"),sQuery(id+"F0.wireOp",EDGE,"E190"),sQuery(id+"F0.wireOp",EDGE,"E191"),sQuery(id+"F0.wireOp",EDGE,"E192"),sQuery(id+"F0.wireOp",EDGE,"E193"),sQuery(id+"F0.wireOp",EDGE,"E194"),sQuery(id+"F0.wireOp",EDGE,"E195"),sQuery(id+"F0.wireOp",EDGE,"E196"),sQuery(id+"F0.wireOp",EDGE,"E197"),sQuery(id+"F0.wireOp",EDGE,"E198"),sQuery(id+"F0.wireOp",EDGE,"E199"),sQuery(id+"F0.wireOp",EDGE,"E200"),sQuery(id+"F0.wireOp",EDGE,"E201"),sQuery(id+"F0.wireOp",EDGE,"E202"),sQuery(id+"F0.wireOp",EDGE,"E203"),sQuery(id+"F0.wireOp",EDGE,"E204"),sQuery(id+"F0.wireOp",EDGE,"E205"),sQuery(id+"F0.wireOp",EDGE,"E206"),sQuery(id+"F0.wireOp",EDGE,"E207"),sQuery(id+"F0.wireOp",EDGE,"E208"),sQuery(id+"F0.wireOp",EDGE,"E209"),sQuery(id+"F0.wireOp",EDGE,"E210"),sQuery(id+"F0.wireOp",EDGE,"E211"),sQuery(id+"F0.wireOp",EDGE,"E212"),sQuery(id+"F0.wireOp",EDGE,"E213"),sQuery(id+"F0.wireOp",EDGE,"E214"),sQuery(id+"F0.wireOp",EDGE,"E215"),sQuery(id+"F0.wireOp",EDGE,"E216"),sQuery(id+"F0.wireOp",EDGE,"E217"),sQuery(id+"F0.wireOp",EDGE,"E218"),sQuery(id+"F0.wireOp",EDGE,"E219"),sQuery(id+"F0.wireOp",EDGE,"E220"),sQuery(id+"F0.wireOp",EDGE,"E221"),sQuery(id+"F0.wireOp",EDGE,"E222"),sQuery(id+"F0.wireOp",EDGE,"E223"),sQuery(id+"F0.wireOp",EDGE,"E224"),sQuery(id+"F0.wireOp",EDGE,"E225"),sQuery(id+"F0.wireOp",EDGE,"E226"),sQuery(id+"F0.wireOp",EDGE,"E227"),sQuery(id+"F0.wireOp",EDGE,"E228"),sQuery(id+"F0.wireOp",EDGE,"E229"),sQuery(id+"F0.wireOp",EDGE,"E230"),sQuery(id+"F0.wireOp",EDGE,"E231"),sQuery(id+"F0.wireOp",EDGE,"E232"),sQuery(id+"F0.wireOp",EDGE,"E233"),sQuery(id+"F0.wireOp",EDGE,"E234"),sQuery(id+"F0.wireOp",EDGE,"E235"),sQuery(id+"F0.wireOp",EDGE,"E236"),sQuery(id+"F0.wireOp",EDGE,"E237"),sQuery(id+"F0.wireOp",EDGE,"E238"),sQuery(id+"F0.wireOp",EDGE,"E239"),sQuery(id+"F0.wireOp",EDGE,"E240"),sQuery(id+"F0.wireOp",EDGE,"E241"),sQuery(id+"F0.wireOp",EDGE,"E242"),sQuery(id+"F0.wireOp",EDGE,"E243")])],"isStart":true});
            var sketch = newSketch(context, id + "F19", { "sketchPlane" : qUnion([Q0])});
            skCircle(sketch, "E293", {"center": v(-76.2, 28.53) * mm, "radius": 0.75 * mm});
            skLineSegment(sketch, "E294", {"start": v(-78.73, 29.55) * mm, "end": v(-76.2, 28.53) * mm});
            skLineSegment(sketch, "E295", {"start": v(-73.68, 29.55) * mm, "end": v(-76.2, 28.53) * mm});
            skSolve(sketch);
        }
        {
            var Q0;
            Q0 = qSketchRegion(id + "F19", true);
            extrude(context, id + "F20", {"entities" : qUnion([Q0]), "operationType" : NewBodyOperationType.REMOVE, "oppositeDirection" : true, "depth" : 5 * mm, "offsetDistance" : 25 * mm});
        }
        {
            var Q0;
            {var subQ0=sQuery(id+"F0.wireOp",EDGE,"E200");var subQ1=sQuery(id+"F0.wireOp",EDGE,"E199");var subQ2=sQuery(id+"F0.wireOp",EDGE,"E198");var subQ3=sQuery(id+"F0.wireOp",EDGE,"E196");var subQ4=sQuery(id+"F7.wireOp",EDGE,"E250.right");var subQ5=sQuery(id+"F7.wireOp",EDGE,"E250.left");var subQ6=makeQuery(id+"F8.opExtrude","CAP_FACE",FACE,{"disambiguationData":[OSD([sQuery(id+"F7.wireOp",EDGE,"E250.bottom"),sQuery(id+"F7.wireOp",EDGE,"E250.top"),subQ5,subQ4])],"isStart":false});var subQ7=sQuery(id+"F0.wireOp",EDGE,"E195");var subQ8=sQuery(id+"F0.wireOp",EDGE,"E194");var subQ9=sQuery(id+"F0.wireOp",EDGE,"E193");var subQ10=sQuery(id+"F0.wireOp",EDGE,"E192");var subQ11=sQuery(id+"F0.wireOp",EDGE,"E191");var subQ12=sQuery(id+"F0.wireOp",EDGE,"E190");var subQ13=sQuery(id+"F0.wireOp",EDGE,"E189");var subQ14=sQuery(id+"F0.wireOp",EDGE,"E188");var subQ15=sQuery(id+"F0.wireOp",EDGE,"E187");var subQ16=sQuery(id+"F0.wireOp",EDGE,"E186");var subQ17=sQuery(id+"F0.wireOp",EDGE,"E185");var subQ18=sQuery(id+"F0.wireOp",EDGE,"E184");var subQ19=sQuery(id+"F0.wireOp",EDGE,"E183");var subQ20=sQuery(id+"F0.wireOp",EDGE,"E182");var subQ21=sQuery(id+"F0.wireOp",EDGE,"E181");var subQ22=sQuery(id+"F0.wireOp",EDGE,"E180");var subQ23=sQuery(id+"F0.wireOp",EDGE,"E179");var subQ24=sQuery(id+"F0.wireOp",EDGE,"E178");var subQ25=sQuery(id+"F0.wireOp",EDGE,"E177");var subQ26=sQuery(id+"F0.wireOp",EDGE,"E176");var subQ27=sQuery(id+"F0.wireOp",EDGE,"E175");var subQ28=sQuery(id+"F0.wireOp",EDGE,"E174");var subQ29=sQuery(id+"F0.wireOp",EDGE,"E173");var subQ30=sQuery(id+"F0.wireOp",EDGE,"E172");var subQ31=sQuery(id+"F0.wireOp",EDGE,"E171");var subQ32=sQuery(id+"F0.wireOp",EDGE,"E170");var subQ33=sQuery(id+"F0.wireOp",EDGE,"E169");var subQ34=sQuery(id+"F0.wireOp",EDGE,"E168");var subQ35=sQuery(id+"F0.wireOp",EDGE,"E167");var subQ36=sQuery(id+"F0.wireOp",EDGE,"E166");var subQ37=sQuery(id+"F0.wireOp",EDGE,"E165");var subQ38=sQuery(id+"F0.wireOp",EDGE,"E164");var subQ39=sQuery(id+"F0.wireOp",EDGE,"E163");var subQ40=sQuery(id+"F0.wireOp",EDGE,"E162");var subQ41=sQuery(id+"F0.wireOp",EDGE,"E161");var subQ42=sQuery(id+"F0.wireOp",EDGE,"E160");var subQ43=sQuery(id+"F0.wireOp",EDGE,"E159");var subQ44=sQuery(id+"F0.wireOp",EDGE,"E158");var subQ45=sQuery(id+"F0.wireOp",EDGE,"E157");var subQ46=sQuery(id+"F0.wireOp",EDGE,"E156");var subQ47=sQuery(id+"F0.wireOp",EDGE,"E155");var subQ48=sQuery(id+"F0.wireOp",EDGE,"E154");var subQ49=sQuery(id+"F0.wireOp",EDGE,"E153");var subQ50=sQuery(id+"F0.wireOp",EDGE,"E152");var subQ51=sQuery(id+"F0.wireOp",EDGE,"E151");var subQ52=sQuery(id+"F0.wireOp",EDGE,"E150");var subQ53=sQuery(id+"F0.wireOp",EDGE,"E149");var subQ54=sQuery(id+"F0.wireOp",EDGE,"E148");var subQ55=sQuery(id+"F0.wireOp",EDGE,"E147");var subQ56=sQuery(id+"F0.wireOp",EDGE,"E146");var subQ57=sQuery(id+"F0.wireOp",EDGE,"E145");var subQ58=sQuery(id+"F0.wireOp",EDGE,"E144");var subQ59=sQuery(id+"F0.wireOp",EDGE,"E143");var subQ60=sQuery(id+"F0.wireOp",EDGE,"E142");var subQ61=sQuery(id+"F0.wireOp",EDGE,"E141");var subQ62=sQuery(id+"F0.wireOp",EDGE,"E140");var subQ63=sQuery(id+"F0.wireOp",EDGE,"E139");var subQ64=sQuery(id+"F0.wireOp",EDGE,"E138");var subQ65=sQuery(id+"F0.wireOp",EDGE,"E137");var subQ66=sQuery(id+"F0.wireOp",EDGE,"E136");var subQ67=sQuery(id+"F0.wireOp",EDGE,"E135");var subQ68=sQuery(id+"F0.wireOp",EDGE,"E134");var subQ69=sQuery(id+"F0.wireOp",EDGE,"E133");var subQ70=sQuery(id+"F0.wireOp",EDGE,"E132");var subQ71=sQuery(id+"F0.wireOp",EDGE,"E131");var subQ72=sQuery(id+"F0.wireOp",EDGE,"E130");var subQ73=sQuery(id+"F0.wireOp",EDGE,"E129");var subQ74=sQuery(id+"F0.wireOp",EDGE,"E128");var subQ75=sQuery(id+"F0.wireOp",EDGE,"E127");var subQ76=sQuery(id+"F0.wireOp",EDGE,"E126");var subQ77=sQuery(id+"F0.wireOp",EDGE,"E125");var subQ78=sQuery(id+"F0.wireOp",EDGE,"E124");var subQ79=sQuery(id+"F0.wireOp",EDGE,"E123");var subQ80=sQuery(id+"F0.wireOp",EDGE,"E122");var subQ81=sQuery(id+"F0.wireOp",EDGE,"E121");var subQ82=sQuery(id+"F0.wireOp",EDGE,"E120");var subQ83=sQuery(id+"F0.wireOp",EDGE,"E119");var subQ84=sQuery(id+"F0.wireOp",EDGE,"E118");var subQ85=sQuery(id+"F0.wireOp",EDGE,"E117");var subQ86=sQuery(id+"F0.wireOp",EDGE,"E116");var subQ87=sQuery(id+"F0.wireOp",EDGE,"E115");var subQ88=sQuery(id+"F0.wireOp",EDGE,"E114");var subQ89=sQuery(id+"F0.wireOp",EDGE,"E113");var subQ90=sQuery(id+"F0.wireOp",EDGE,"E112");var subQ91=sQuery(id+"F0.wireOp",EDGE,"E111");var subQ92=sQuery(id+"F0.wireOp",EDGE,"E110");var subQ93=sQuery(id+"F0.wireOp",EDGE,"E109");var subQ94=sQuery(id+"F0.wireOp",EDGE,"E108");var subQ95=sQuery(id+"F0.wireOp",EDGE,"E107");var subQ96=sQuery(id+"F0.wireOp",EDGE,"E106");var subQ97=sQuery(id+"F0.wireOp",EDGE,"E105");var subQ98=sQuery(id+"F0.wireOp",EDGE,"E104");var subQ99=sQuery(id+"F0.wireOp",EDGE,"E103");var subQ100=sQuery(id+"F0.wireOp",EDGE,"E102");var subQ101=sQuery(id+"F0.wireOp",EDGE,"E101");var subQ102=sQuery(id+"F0.wireOp",EDGE,"E100");var subQ103=sQuery(id+"F0.wireOp",EDGE,"E99");var subQ104=sQuery(id+"F0.wireOp",EDGE,"E48");var subQ105=sQuery(id+"F0.wireOp",EDGE,"E47");var subQ106=sQuery(id+"F0.wireOp",EDGE,"E46");var subQ107=sQuery(id+"F0.wireOp",EDGE,"E44");var subQ108=sQuery(id+"F0.wireOp",EDGE,"E43");var subQ109=sQuery(id+"F0.wireOp",EDGE,"E42");var subQ110=sQuery(id+"F0.wireOp",EDGE,"E41");var subQ111=sQuery(id+"F0.wireOp",EDGE,"E40");var subQ112=sQuery(id+"F0.wireOp",EDGE,"E39");var subQ113=sQuery(id+"F0.wireOp",EDGE,"E38");var subQ114=sQuery(id+"F0.wireOp",EDGE,"E37");var subQ115=sQuery(id+"F0.wireOp",EDGE,"E36");var subQ116=sQuery(id+"F0.wireOp",EDGE,"E35");var subQ117=sQuery(id+"F0.wireOp",EDGE,"E34");var subQ118=sQuery(id+"F0.wireOp",EDGE,"E33");var subQ119=sQuery(id+"F0.wireOp",EDGE,"E32");var subQ120=sQuery(id+"F0.wireOp",EDGE,"E31");var subQ121=sQuery(id+"F0.wireOp",EDGE,"E30");var subQ122=sQuery(id+"F0.wireOp",EDGE,"E29");var subQ123=sQuery(id+"F0.wireOp",EDGE,"E28");var subQ124=sQuery(id+"F0.wireOp",EDGE,"E27");var subQ125=sQuery(id+"F0.wireOp",EDGE,"E26");var subQ126=sQuery(id+"F0.wireOp",EDGE,"E25");var subQ127=sQuery(id+"F0.wireOp",EDGE,"E12");var subQ128=sQuery(id+"F0.wireOp",EDGE,"E11");var subQ129=sQuery(id+"F0.wireOp",EDGE,"E10");var subQ130=sQuery(id+"F0.wireOp",EDGE,"E8");var subQ131=sQuery(id+"F0.wireOp",EDGE,"E7");var subQ132=sQuery(id+"F0.wireOp",EDGE,"E9");var subQ133=sQuery(id+"F0.wireOp",EDGE,"E45");var subQ134=sQuery(id+"F0.wireOp",EDGE,"E197");var subQ135=sQuery(id+"F0.wireOp",EDGE,"E95");var subQ136=sQuery(id+"F0.wireOp",EDGE,"E21");var subQ137=sQuery(id+"F0.wireOp",EDGE,"E4");var subQ138=sQuery(id+"F0.wireOp",EDGE,"E5");var subQ139=sQuery(id+"F0.wireOp",EDGE,"E6");var subQ140=sQuery(id+"F0.wireOp",EDGE,"E13");var subQ141=sQuery(id+"F0.wireOp",EDGE,"E14");var subQ142=sQuery(id+"F0.wireOp",EDGE,"E15");var subQ143=sQuery(id+"F0.wireOp",EDGE,"E16");var subQ144=sQuery(id+"F0.wireOp",EDGE,"E17");var subQ145=sQuery(id+"F0.wireOp",EDGE,"E18");var subQ146=sQuery(id+"F0.wireOp",EDGE,"E19");var subQ147=sQuery(id+"F0.wireOp",EDGE,"E20");var subQ148=sQuery(id+"F0.wireOp",EDGE,"E22");var subQ149=sQuery(id+"F0.wireOp",EDGE,"E23");var subQ150=sQuery(id+"F0.wireOp",EDGE,"E24");var subQ151=sQuery(id+"F0.wireOp",EDGE,"E49");var subQ152=sQuery(id+"F0.wireOp",EDGE,"E50");var subQ153=sQuery(id+"F0.wireOp",EDGE,"E51");var subQ154=sQuery(id+"F0.wireOp",EDGE,"E52");var subQ155=sQuery(id+"F0.wireOp",EDGE,"E53");var subQ156=sQuery(id+"F0.wireOp",EDGE,"E54");var subQ157=sQuery(id+"F0.wireOp",EDGE,"E55");var subQ158=sQuery(id+"F0.wireOp",EDGE,"E56");var subQ159=sQuery(id+"F0.wireOp",EDGE,"E57");var subQ160=sQuery(id+"F0.wireOp",EDGE,"E58");var subQ161=sQuery(id+"F0.wireOp",EDGE,"E59");var subQ162=sQuery(id+"F0.wireOp",EDGE,"E60");var subQ163=sQuery(id+"F0.wireOp",EDGE,"E61");var subQ164=sQuery(id+"F0.wireOp",EDGE,"E62");var subQ165=sQuery(id+"F0.wireOp",EDGE,"E63");var subQ166=sQuery(id+"F0.wireOp",EDGE,"E64");var subQ167=sQuery(id+"F0.wireOp",EDGE,"E65");var subQ168=sQuery(id+"F0.wireOp",EDGE,"E66");var subQ169=sQuery(id+"F0.wireOp",EDGE,"E67");var subQ170=sQuery(id+"F0.wireOp",EDGE,"E68");var subQ171=sQuery(id+"F0.wireOp",EDGE,"E69");var subQ172=sQuery(id+"F0.wireOp",EDGE,"E70");var subQ173=sQuery(id+"F0.wireOp",EDGE,"E71");var subQ174=sQuery(id+"F0.wireOp",EDGE,"E72");var subQ175=sQuery(id+"F0.wireOp",EDGE,"E73");var subQ176=sQuery(id+"F0.wireOp",EDGE,"E74");var subQ177=sQuery(id+"F0.wireOp",EDGE,"E75");var subQ178=sQuery(id+"F0.wireOp",EDGE,"E76");var subQ179=sQuery(id+"F0.wireOp",EDGE,"E77");var subQ180=sQuery(id+"F0.wireOp",EDGE,"E78");var subQ181=sQuery(id+"F0.wireOp",EDGE,"E79");var subQ182=sQuery(id+"F0.wireOp",EDGE,"E80");var subQ183=sQuery(id+"F0.wireOp",EDGE,"E81");var subQ184=sQuery(id+"F0.wireOp",EDGE,"E82");var subQ185=sQuery(id+"F0.wireOp",EDGE,"E83");var subQ186=sQuery(id+"F0.wireOp",EDGE,"E84");var subQ187=sQuery(id+"F0.wireOp",EDGE,"E85");var subQ188=sQuery(id+"F0.wireOp",EDGE,"E86");var subQ189=sQuery(id+"F0.wireOp",EDGE,"E87");var subQ190=sQuery(id+"F0.wireOp",EDGE,"E88");var subQ191=sQuery(id+"F0.wireOp",EDGE,"E89");var subQ192=sQuery(id+"F0.wireOp",EDGE,"E90");var subQ193=sQuery(id+"F0.wireOp",EDGE,"E91");var subQ194=sQuery(id+"F0.wireOp",EDGE,"E92");var subQ195=sQuery(id+"F0.wireOp",EDGE,"E93");var subQ196=sQuery(id+"F0.wireOp",EDGE,"E94");var subQ197=sQuery(id+"F0.wireOp",EDGE,"E96");var subQ198=sQuery(id+"F0.wireOp",EDGE,"E97");var subQ199=sQuery(id+"F0.wireOp",EDGE,"E98");var subQ200=sQuery(id+"F0.wireOp",EDGE,"E201");var subQ201=sQuery(id+"F0.wireOp",EDGE,"E202");var subQ202=sQuery(id+"F0.wireOp",EDGE,"E203");var subQ203=sQuery(id+"F0.wireOp",EDGE,"E204");var subQ204=sQuery(id+"F0.wireOp",EDGE,"E205");var subQ205=sQuery(id+"F0.wireOp",EDGE,"E206");var subQ206=sQuery(id+"F0.wireOp",EDGE,"E207");var subQ207=sQuery(id+"F0.wireOp",EDGE,"E208");var subQ208=sQuery(id+"F0.wireOp",EDGE,"E209");var subQ209=sQuery(id+"F0.wireOp",EDGE,"E210");var subQ210=sQuery(id+"F0.wireOp",EDGE,"E211");var subQ211=sQuery(id+"F0.wireOp",EDGE,"E212");var subQ212=sQuery(id+"F0.wireOp",EDGE,"E213");var subQ213=sQuery(id+"F0.wireOp",EDGE,"E214");var subQ214=sQuery(id+"F0.wireOp",EDGE,"E215");var subQ215=sQuery(id+"F0.wireOp",EDGE,"E216");var subQ216=sQuery(id+"F3.wireOp",EDGE,"E244.bottom");var subQ217=sQuery(id+"F0.wireOp",EDGE,"E217");var subQ218=sQuery(id+"F3.wireOp",EDGE,"E248.filletArc");var subQ219=sQuery(id+"F3.wireOp",EDGE,"E247.filletArc");var subQ220=sQuery(id+"F3.wireOp",EDGE,"E246.filletArc");var subQ221=sQuery(id+"F3.wireOp",EDGE,"E245.filletArc");var subQ222=sQuery(id+"F3.wireOp",EDGE,"E244.right");var subQ223=sQuery(id+"F3.wireOp",EDGE,"E244.left");var subQ224=sQuery(id+"F3.wireOp",EDGE,"E244.top");var subQ225=sQuery(id+"F0.wireOp",EDGE,"E243");var subQ226=sQuery(id+"F0.wireOp",EDGE,"E242");var subQ227=sQuery(id+"F0.wireOp",EDGE,"E241");var subQ228=sQuery(id+"F0.wireOp",EDGE,"E240");var subQ229=sQuery(id+"F0.wireOp",EDGE,"E239");var subQ230=sQuery(id+"F0.wireOp",EDGE,"E238");var subQ231=sQuery(id+"F0.wireOp",EDGE,"E237");var subQ232=sQuery(id+"F0.wireOp",EDGE,"E236");var subQ233=sQuery(id+"F0.wireOp",EDGE,"E235");var subQ234=sQuery(id+"F0.wireOp",EDGE,"E234");var subQ235=sQuery(id+"F0.wireOp",EDGE,"E233");var subQ236=sQuery(id+"F0.wireOp",EDGE,"E232");var subQ237=sQuery(id+"F0.wireOp",EDGE,"E231");var subQ238=sQuery(id+"F0.wireOp",EDGE,"E230");var subQ239=sQuery(id+"F0.wireOp",EDGE,"E229");var subQ240=sQuery(id+"F0.wireOp",EDGE,"E228");var subQ241=sQuery(id+"F0.wireOp",EDGE,"E227");var subQ242=sQuery(id+"F0.wireOp",EDGE,"E226");var subQ243=sQuery(id+"F0.wireOp",EDGE,"E225");var subQ244=sQuery(id+"F0.wireOp",EDGE,"E224");var subQ245=sQuery(id+"F0.wireOp",EDGE,"E223");var subQ246=sQuery(id+"F0.wireOp",EDGE,"E222");var subQ247=sQuery(id+"F0.wireOp",EDGE,"E221");var subQ248=sQuery(id+"F0.wireOp",EDGE,"E220");var subQ249=sQuery(id+"F0.wireOp",EDGE,"E219");var subQ250=sQuery(id+"F0.wireOp",EDGE,"E218");var subQ251=makeQuery(id+"F4.boolean.opBoolean","COPY",FACE,{"derivedFrom":makeQuery(id+"F4.opExtrude","CAP_FACE",FACE,{"disambiguationData":[OSD([subQ137,subQ138,subQ139,subQ131,subQ130,subQ132,subQ129,subQ128,subQ127,subQ140,subQ141,subQ142,subQ143,subQ144,subQ145,subQ146,subQ147,subQ136,subQ148,subQ149,subQ150,subQ126,subQ125,subQ124,subQ123,subQ122,subQ121,subQ120,subQ119,subQ118,subQ117,subQ116,subQ115,subQ114,subQ113,subQ112,subQ111,subQ110,subQ109,subQ108,subQ107,subQ133,subQ106,subQ105,subQ104,subQ151,subQ152,subQ153,subQ154,subQ155,subQ156,subQ157,subQ158,subQ159,subQ160,subQ161,subQ162,subQ163,subQ164,subQ165,subQ166,subQ167,subQ168,subQ169,subQ170,subQ171,subQ172,subQ173,subQ174,subQ175,subQ176,subQ177,subQ178,subQ179,subQ180,subQ181,subQ182,subQ183,subQ184,subQ185,subQ186,subQ187,subQ188,subQ189,subQ190,subQ191,subQ192,subQ193,subQ194,subQ195,subQ196,subQ135,subQ197,subQ198,subQ199,subQ103,subQ102,subQ101,subQ100,subQ99,subQ98,subQ97,subQ96,subQ95,subQ94,subQ93,subQ92,subQ91,subQ90,subQ89,subQ88,subQ87,subQ86,subQ85,subQ84,subQ83,subQ82,subQ81,subQ80,subQ79,subQ78,subQ77,subQ76,subQ75,subQ74,subQ73,subQ72,subQ71,subQ70,subQ69,subQ68,subQ67,subQ66,subQ65,subQ64,subQ63,subQ62,subQ61,subQ60,subQ59,subQ58,subQ57,subQ56,subQ55,subQ54,subQ53,subQ52,subQ51,subQ50,subQ49,subQ48,subQ47,subQ46,subQ45,subQ44,subQ43,subQ42,subQ41,subQ40,subQ39,subQ38,subQ37,subQ36,subQ35,subQ34,subQ33,subQ32,subQ31,subQ30,subQ29,subQ28,subQ27,subQ26,subQ25,subQ24,subQ23,subQ22,subQ21,subQ20,subQ19,subQ18,subQ17,subQ16,subQ15,subQ14,subQ13,subQ12,subQ11,subQ10,subQ9,subQ8,subQ7,subQ3,subQ134,subQ2,subQ1,subQ0,subQ200,subQ201,subQ202,subQ203,subQ204,subQ205,subQ206,subQ207,subQ208,subQ209,subQ210,subQ211,subQ212,subQ213,subQ214,subQ215,subQ217,subQ250,subQ249,subQ248,subQ247,subQ246,subQ245,subQ244,subQ243,subQ242,subQ241,subQ240,subQ239,subQ238,subQ237,subQ236,subQ235,subQ234,subQ233,subQ232,subQ231,subQ230,subQ229,subQ228,subQ227,subQ226,subQ225,subQ216,subQ224,subQ223,subQ222,subQ221,subQ220,subQ219,subQ218])],"isStart":false})});Q0=makeQuery(id+"F12.boolean.opBoolean","SPLIT",FACE,{"disambiguationData":[TD([makeQuery(id+"F1.opExtrude","SWEPT_FACE",FACE,{"disambiguationData":[OSD([sQuery(id+"F0.wireOp",EDGE,"E0")])]}),makeQuery(id+"F1.opExtrude","SWEPT_FACE",FACE,{"disambiguationData":[OSD([subQ137])]}),makeQuery(id+"F1.opExtrude","SWEPT_FACE",FACE,{"disambiguationData":[OSD([subQ138])]}),makeQuery(id+"F1.opExtrude","SWEPT_FACE",FACE,{"disambiguationData":[OSD([subQ139])]}),makeQuery(id+"F1.opExtrude","SWEPT_FACE",FACE,{"disambiguationData":[OSD([subQ131])]}),makeQuery(id+"F1.opExtrude","SWEPT_FACE",FACE,{"disambiguationData":[OSD([subQ130])]}),makeQuery(id+"F1.opExtrude","SWEPT_FACE",FACE,{"disambiguationData":[OSD([subQ132])]}),makeQuery(id+"F1.opExtrude","SWEPT_FACE",FACE,{"disambiguationData":[OSD([subQ129])]}),makeQuery(id+"F1.opExtrude","SWEPT_FACE",FACE,{"disambiguationData":[OSD([subQ128])]}),makeQuery(id+"F1.opExtrude","SWEPT_FACE",FACE,{"disambiguationData":[OSD([subQ127])]}),makeQuery(id+"F1.opExtrude","SWEPT_FACE",FACE,{"disambiguationData":[OSD([subQ140])]}),makeQuery(id+"F1.opExtrude","SWEPT_FACE",FACE,{"disambiguationData":[OSD([subQ141])]}),makeQuery(id+"F1.opExtrude","SWEPT_FACE",FACE,{"disambiguationData":[OSD([subQ142])]}),makeQuery(id+"F1.opExtrude","SWEPT_FACE",FACE,{"disambiguationData":[OSD([subQ143])]}),makeQuery(id+"F1.opExtrude","SWEPT_FACE",FACE,{"disambiguationData":[OSD([subQ144])]}),makeQuery(id+"F1.opExtrude","SWEPT_FACE",FACE,{"disambiguationData":[OSD([subQ145])]}),makeQuery(id+"F1.opExtrude","SWEPT_FACE",FACE,{"disambiguationData":[OSD([subQ146])]}),makeQuery(id+"F1.opExtrude","SWEPT_FACE",FACE,{"disambiguationData":[OSD([subQ147])]}),makeQuery(id+"F1.opExtrude","SWEPT_FACE",FACE,{"disambiguationData":[OSD([subQ136])]}),makeQuery(id+"F1.opExtrude","SWEPT_FACE",FACE,{"disambiguationData":[OSD([subQ148])]}),makeQuery(id+"F1.opExtrude","SWEPT_FACE",FACE,{"disambiguationData":[OSD([subQ149])]}),makeQuery(id+"F1.opExtrude","SWEPT_FACE",FACE,{"disambiguationData":[OSD([subQ150])]}),makeQuery(id+"F1.opExtrude","SWEPT_FACE",FACE,{"disambiguationData":[OSD([subQ126])]}),makeQuery(id+"F1.opExtrude","SWEPT_FACE",FACE,{"disambiguationData":[OSD([subQ125])]}),makeQuery(id+"F1.opExtrude","SWEPT_FACE",FACE,{"disambiguationData":[OSD([subQ124])]}),makeQuery(id+"F1.opExtrude","SWEPT_FACE",FACE,{"disambiguationData":[OSD([subQ123])]}),makeQuery(id+"F1.opExtrude","SWEPT_FACE",FACE,{"disambiguationData":[OSD([subQ122])]}),makeQuery(id+"F1.opExtrude","SWEPT_FACE",FACE,{"disambiguationData":[OSD([subQ121])]}),makeQuery(id+"F1.opExtrude","SWEPT_FACE",FACE,{"disambiguationData":[OSD([subQ120])]}),makeQuery(id+"F1.opExtrude","SWEPT_FACE",FACE,{"disambiguationData":[OSD([subQ119])]}),makeQuery(id+"F1.opExtrude","SWEPT_FACE",FACE,{"disambiguationData":[OSD([subQ118])]}),makeQuery(id+"F1.opExtrude","SWEPT_FACE",FACE,{"disambiguationData":[OSD([subQ117])]}),makeQuery(id+"F1.opExtrude","SWEPT_FACE",FACE,{"disambiguationData":[OSD([subQ116])]}),makeQuery(id+"F1.opExtrude","SWEPT_FACE",FACE,{"disambiguationData":[OSD([subQ115])]}),makeQuery(id+"F1.opExtrude","SWEPT_FACE",FACE,{"disambiguationData":[OSD([subQ114])]}),makeQuery(id+"F1.opExtrude","SWEPT_FACE",FACE,{"disambiguationData":[OSD([subQ113])]}),makeQuery(id+"F1.opExtrude","SWEPT_FACE",FACE,{"disambiguationData":[OSD([subQ112])]}),makeQuery(id+"F1.opExtrude","SWEPT_FACE",FACE,{"disambiguationData":[OSD([subQ111])]}),makeQuery(id+"F1.opExtrude","SWEPT_FACE",FACE,{"disambiguationData":[OSD([subQ110])]}),makeQuery(id+"F1.opExtrude","SWEPT_FACE",FACE,{"disambiguationData":[OSD([subQ109])]}),makeQuery(id+"F1.opExtrude","SWEPT_FACE",FACE,{"disambiguationData":[OSD([subQ108])]}),makeQuery(id+"F1.opExtrude","SWEPT_FACE",FACE,{"disambiguationData":[OSD([subQ107])]}),makeQuery(id+"F1.opExtrude","SWEPT_FACE",FACE,{"disambiguationData":[OSD([subQ133])]}),makeQuery(id+"F1.opExtrude","SWEPT_FACE",FACE,{"disambiguationData":[OSD([subQ106])]}),makeQuery(id+"F1.opExtrude","SWEPT_FACE",FACE,{"disambiguationData":[OSD([subQ105])]}),makeQuery(id+"F1.opExtrude","SWEPT_FACE",FACE,{"disambiguationData":[OSD([subQ104])]}),makeQuery(id+"F1.opExtrude","SWEPT_FACE",FACE,{"disambiguationData":[OSD([subQ151])]}),makeQuery(id+"F1.opExtrude","SWEPT_FACE",FACE,{"disambiguationData":[OSD([subQ152])]}),makeQuery(id+"F1.opExtrude","SWEPT_FACE",FACE,{"disambiguationData":[OSD([subQ153])]}),makeQuery(id+"F1.opExtrude","SWEPT_FACE",FACE,{"disambiguationData":[OSD([subQ154])]}),makeQuery(id+"F1.opExtrude","SWEPT_FACE",FACE,{"disambiguationData":[OSD([subQ155])]}),makeQuery(id+"F1.opExtrude","SWEPT_FACE",FACE,{"disambiguationData":[OSD([subQ156])]}),makeQuery(id+"F1.opExtrude","SWEPT_FACE",FACE,{"disambiguationData":[OSD([subQ157])]}),makeQuery(id+"F1.opExtrude","SWEPT_FACE",FACE,{"disambiguationData":[OSD([subQ158])]}),makeQuery(id+"F1.opExtrude","SWEPT_FACE",FACE,{"disambiguationData":[OSD([subQ159])]}),makeQuery(id+"F1.opExtrude","SWEPT_FACE",FACE,{"disambiguationData":[OSD([subQ160])]}),makeQuery(id+"F1.opExtrude","SWEPT_FACE",FACE,{"disambiguationData":[OSD([subQ161])]}),makeQuery(id+"F1.opExtrude","SWEPT_FACE",FACE,{"disambiguationData":[OSD([subQ162])]}),makeQuery(id+"F1.opExtrude","SWEPT_FACE",FACE,{"disambiguationData":[OSD([subQ163])]}),makeQuery(id+"F1.opExtrude","SWEPT_FACE",FACE,{"disambiguationData":[OSD([subQ164])]}),makeQuery(id+"F1.opExtrude","SWEPT_FACE",FACE,{"disambiguationData":[OSD([subQ165])]}),makeQuery(id+"F1.opExtrude","SWEPT_FACE",FACE,{"disambiguationData":[OSD([subQ166])]}),makeQuery(id+"F1.opExtrude","SWEPT_FACE",FACE,{"disambiguationData":[OSD([subQ167])]}),makeQuery(id+"F1.opExtrude","SWEPT_FACE",FACE,{"disambiguationData":[OSD([subQ168])]}),makeQuery(id+"F1.opExtrude","SWEPT_FACE",FACE,{"disambiguationData":[OSD([subQ169])]}),makeQuery(id+"F1.opExtrude","SWEPT_FACE",FACE,{"disambiguationData":[OSD([subQ170])]}),makeQuery(id+"F1.opExtrude","SWEPT_FACE",FACE,{"disambiguationData":[OSD([subQ171])]}),makeQuery(id+"F1.opExtrude","SWEPT_FACE",FACE,{"disambiguationData":[OSD([subQ172])]}),makeQuery(id+"F1.opExtrude","SWEPT_FACE",FACE,{"disambiguationData":[OSD([subQ173])]}),makeQuery(id+"F1.opExtrude","SWEPT_FACE",FACE,{"disambiguationData":[OSD([subQ174])]}),makeQuery(id+"F1.opExtrude","SWEPT_FACE",FACE,{"disambiguationData":[OSD([subQ175])]}),makeQuery(id+"F1.opExtrude","SWEPT_FACE",FACE,{"disambiguationData":[OSD([subQ176])]}),makeQuery(id+"F1.opExtrude","SWEPT_FACE",FACE,{"disambiguationData":[OSD([subQ177])]}),makeQuery(id+"F1.opExtrude","SWEPT_FACE",FACE,{"disambiguationData":[OSD([subQ178])]}),makeQuery(id+"F1.opExtrude","SWEPT_FACE",FACE,{"disambiguationData":[OSD([subQ179])]}),makeQuery(id+"F1.opExtrude","SWEPT_FACE",FACE,{"disambiguationData":[OSD([subQ180])]}),makeQuery(id+"F1.opExtrude","SWEPT_FACE",FACE,{"disambiguationData":[OSD([subQ181])]}),makeQuery(id+"F1.opExtrude","SWEPT_FACE",FACE,{"disambiguationData":[OSD([subQ182])]}),makeQuery(id+"F1.opExtrude","SWEPT_FACE",FACE,{"disambiguationData":[OSD([subQ183])]}),makeQuery(id+"F1.opExtrude","SWEPT_FACE",FACE,{"disambiguationData":[OSD([subQ184])]}),makeQuery(id+"F1.opExtrude","SWEPT_FACE",FACE,{"disambiguationData":[OSD([subQ185])]}),makeQuery(id+"F1.opExtrude","SWEPT_FACE",FACE,{"disambiguationData":[OSD([subQ186])]}),makeQuery(id+"F1.opExtrude","SWEPT_FACE",FACE,{"disambiguationData":[OSD([subQ187])]}),makeQuery(id+"F1.opExtrude","SWEPT_FACE",FACE,{"disambiguationData":[OSD([subQ188])]}),makeQuery(id+"F1.opExtrude","SWEPT_FACE",FACE,{"disambiguationData":[OSD([subQ189])]}),makeQuery(id+"F1.opExtrude","SWEPT_FACE",FACE,{"disambiguationData":[OSD([subQ190])]}),makeQuery(id+"F1.opExtrude","SWEPT_FACE",FACE,{"disambiguationData":[OSD([subQ191])]}),makeQuery(id+"F1.opExtrude","SWEPT_FACE",FACE,{"disambiguationData":[OSD([subQ192])]}),makeQuery(id+"F1.opExtrude","SWEPT_FACE",FACE,{"disambiguationData":[OSD([subQ193])]}),makeQuery(id+"F1.opExtrude","SWEPT_FACE",FACE,{"disambiguationData":[OSD([subQ194])]}),makeQuery(id+"F1.opExtrude","SWEPT_FACE",FACE,{"disambiguationData":[OSD([subQ195])]}),makeQuery(id+"F1.opExtrude","SWEPT_FACE",FACE,{"disambiguationData":[OSD([subQ196])]}),makeQuery(id+"F1.opExtrude","SWEPT_FACE",FACE,{"disambiguationData":[OSD([subQ135])]}),makeQuery(id+"F1.opExtrude","SWEPT_FACE",FACE,{"disambiguationData":[OSD([subQ197])]}),makeQuery(id+"F1.opExtrude","SWEPT_FACE",FACE,{"disambiguationData":[OSD([subQ198])]}),makeQuery(id+"F1.opExtrude","SWEPT_FACE",FACE,{"disambiguationData":[OSD([subQ199])]}),makeQuery(id+"F1.opExtrude","SWEPT_FACE",FACE,{"disambiguationData":[OSD([subQ103])]}),makeQuery(id+"F1.opExtrude","SWEPT_FACE",FACE,{"disambiguationData":[OSD([subQ102])]}),makeQuery(id+"F1.opExtrude","SWEPT_FACE",FACE,{"disambiguationData":[OSD([subQ101])]}),makeQuery(id+"F1.opExtrude","SWEPT_FACE",FACE,{"disambiguationData":[OSD([subQ100])]}),makeQuery(id+"F1.opExtrude","SWEPT_FACE",FACE,{"disambiguationData":[OSD([subQ99])]}),makeQuery(id+"F1.opExtrude","SWEPT_FACE",FACE,{"disambiguationData":[OSD([subQ98])]}),makeQuery(id+"F1.opExtrude","SWEPT_FACE",FACE,{"disambiguationData":[OSD([subQ97])]}),makeQuery(id+"F1.opExtrude","SWEPT_FACE",FACE,{"disambiguationData":[OSD([subQ96])]}),makeQuery(id+"F1.opExtrude","SWEPT_FACE",FACE,{"disambiguationData":[OSD([subQ95])]}),makeQuery(id+"F1.opExtrude","SWEPT_FACE",FACE,{"disambiguationData":[OSD([subQ94])]}),makeQuery(id+"F1.opExtrude","SWEPT_FACE",FACE,{"disambiguationData":[OSD([subQ93])]}),makeQuery(id+"F1.opExtrude","SWEPT_FACE",FACE,{"disambiguationData":[OSD([subQ92])]}),makeQuery(id+"F1.opExtrude","SWEPT_FACE",FACE,{"disambiguationData":[OSD([subQ91])]}),makeQuery(id+"F1.opExtrude","SWEPT_FACE",FACE,{"disambiguationData":[OSD([subQ90])]}),makeQuery(id+"F1.opExtrude","SWEPT_FACE",FACE,{"disambiguationData":[OSD([subQ89])]}),makeQuery(id+"F1.opExtrude","SWEPT_FACE",FACE,{"disambiguationData":[OSD([subQ88])]}),makeQuery(id+"F1.opExtrude","SWEPT_FACE",FACE,{"disambiguationData":[OSD([subQ87])]}),makeQuery(id+"F1.opExtrude","SWEPT_FACE",FACE,{"disambiguationData":[OSD([subQ86])]}),makeQuery(id+"F1.opExtrude","SWEPT_FACE",FACE,{"disambiguationData":[OSD([subQ85])]}),makeQuery(id+"F1.opExtrude","SWEPT_FACE",FACE,{"disambiguationData":[OSD([subQ84])]}),makeQuery(id+"F1.opExtrude","SWEPT_FACE",FACE,{"disambiguationData":[OSD([subQ83])]}),makeQuery(id+"F1.opExtrude","SWEPT_FACE",FACE,{"disambiguationData":[OSD([subQ82])]}),makeQuery(id+"F1.opExtrude","SWEPT_FACE",FACE,{"disambiguationData":[OSD([subQ81])]}),makeQuery(id+"F1.opExtrude","SWEPT_FACE",FACE,{"disambiguationData":[OSD([subQ80])]}),makeQuery(id+"F1.opExtrude","SWEPT_FACE",FACE,{"disambiguationData":[OSD([subQ79])]}),makeQuery(id+"F1.opExtrude","SWEPT_FACE",FACE,{"disambiguationData":[OSD([subQ78])]}),makeQuery(id+"F1.opExtrude","SWEPT_FACE",FACE,{"disambiguationData":[OSD([subQ77])]}),makeQuery(id+"F1.opExtrude","SWEPT_FACE",FACE,{"disambiguationData":[OSD([subQ76])]}),makeQuery(id+"F1.opExtrude","SWEPT_FACE",FACE,{"disambiguationData":[OSD([subQ75])]}),makeQuery(id+"F1.opExtrude","SWEPT_FACE",FACE,{"disambiguationData":[OSD([subQ74])]}),makeQuery(id+"F1.opExtrude","SWEPT_FACE",FACE,{"disambiguationData":[OSD([subQ73])]}),makeQuery(id+"F1.opExtrude","SWEPT_FACE",FACE,{"disambiguationData":[OSD([subQ72])]}),makeQuery(id+"F1.opExtrude","SWEPT_FACE",FACE,{"disambiguationData":[OSD([subQ71])]}),makeQuery(id+"F1.opExtrude","SWEPT_FACE",FACE,{"disambiguationData":[OSD([subQ70])]}),makeQuery(id+"F1.opExtrude","SWEPT_FACE",FACE,{"disambiguationData":[OSD([subQ69])]}),makeQuery(id+"F1.opExtrude","SWEPT_FACE",FACE,{"disambiguationData":[OSD([subQ68])]}),makeQuery(id+"F1.opExtrude","SWEPT_FACE",FACE,{"disambiguationData":[OSD([subQ67])]}),makeQuery(id+"F1.opExtrude","SWEPT_FACE",FACE,{"disambiguationData":[OSD([subQ66])]}),makeQuery(id+"F1.opExtrude","SWEPT_FACE",FACE,{"disambiguationData":[OSD([subQ65])]}),makeQuery(id+"F1.opExtrude","SWEPT_FACE",FACE,{"disambiguationData":[OSD([subQ64])]}),makeQuery(id+"F1.opExtrude","SWEPT_FACE",FACE,{"disambiguationData":[OSD([subQ63])]}),makeQuery(id+"F1.opExtrude","SWEPT_FACE",FACE,{"disambiguationData":[OSD([subQ62])]}),makeQuery(id+"F1.opExtrude","SWEPT_FACE",FACE,{"disambiguationData":[OSD([subQ61])]}),makeQuery(id+"F1.opExtrude","SWEPT_FACE",FACE,{"disambiguationData":[OSD([subQ60])]}),makeQuery(id+"F1.opExtrude","SWEPT_FACE",FACE,{"disambiguationData":[OSD([subQ59])]}),makeQuery(id+"F1.opExtrude","SWEPT_FACE",FACE,{"disambiguationData":[OSD([subQ58])]}),makeQuery(id+"F1.opExtrude","SWEPT_FACE",FACE,{"disambiguationData":[OSD([subQ57])]}),makeQuery(id+"F1.opExtrude","SWEPT_FACE",FACE,{"disambiguationData":[OSD([subQ56])]}),makeQuery(id+"F1.opExtrude","SWEPT_FACE",FACE,{"disambiguationData":[OSD([subQ55])]}),makeQuery(id+"F1.opExtrude","SWEPT_FACE",FACE,{"disambiguationData":[OSD([subQ54])]}),makeQuery(id+"F1.opExtrude","SWEPT_FACE",FACE,{"disambiguationData":[OSD([subQ53])]}),makeQuery(id+"F1.opExtrude","SWEPT_FACE",FACE,{"disambiguationData":[OSD([subQ52])]}),makeQuery(id+"F1.opExtrude","SWEPT_FACE",FACE,{"disambiguationData":[OSD([subQ51])]}),makeQuery(id+"F1.opExtrude","SWEPT_FACE",FACE,{"disambiguationData":[OSD([subQ50])]}),makeQuery(id+"F1.opExtrude","SWEPT_FACE",FACE,{"disambiguationData":[OSD([subQ49])]}),makeQuery(id+"F1.opExtrude","SWEPT_FACE",FACE,{"disambiguationData":[OSD([subQ48])]}),makeQuery(id+"F1.opExtrude","SWEPT_FACE",FACE,{"disambiguationData":[OSD([subQ47])]}),makeQuery(id+"F1.opExtrude","SWEPT_FACE",FACE,{"disambiguationData":[OSD([subQ46])]}),makeQuery(id+"F1.opExtrude","SWEPT_FACE",FACE,{"disambiguationData":[OSD([subQ45])]}),makeQuery(id+"F1.opExtrude","SWEPT_FACE",FACE,{"disambiguationData":[OSD([subQ44])]}),makeQuery(id+"F1.opExtrude","SWEPT_FACE",FACE,{"disambiguationData":[OSD([subQ43])]}),makeQuery(id+"F1.opExtrude","SWEPT_FACE",FACE,{"disambiguationData":[OSD([subQ42])]}),makeQuery(id+"F1.opExtrude","SWEPT_FACE",FACE,{"disambiguationData":[OSD([subQ41])]}),makeQuery(id+"F1.opExtrude","SWEPT_FACE",FACE,{"disambiguationData":[OSD([subQ40])]}),makeQuery(id+"F1.opExtrude","SWEPT_FACE",FACE,{"disambiguationData":[OSD([subQ39])]}),makeQuery(id+"F1.opExtrude","SWEPT_FACE",FACE,{"disambiguationData":[OSD([subQ38])]}),makeQuery(id+"F1.opExtrude","SWEPT_FACE",FACE,{"disambiguationData":[OSD([subQ37])]}),makeQuery(id+"F1.opExtrude","SWEPT_FACE",FACE,{"disambiguationData":[OSD([subQ36])]}),makeQuery(id+"F1.opExtrude","SWEPT_FACE",FACE,{"disambiguationData":[OSD([subQ35])]}),makeQuery(id+"F1.opExtrude","SWEPT_FACE",FACE,{"disambiguationData":[OSD([subQ34])]}),makeQuery(id+"F1.opExtrude","SWEPT_FACE",FACE,{"disambiguationData":[OSD([subQ33])]}),makeQuery(id+"F1.opExtrude","SWEPT_FACE",FACE,{"disambiguationData":[OSD([subQ32])]}),makeQuery(id+"F1.opExtrude","SWEPT_FACE",FACE,{"disambiguationData":[OSD([subQ31])]}),makeQuery(id+"F1.opExtrude","SWEPT_FACE",FACE,{"disambiguationData":[OSD([subQ30])]}),makeQuery(id+"F1.opExtrude","SWEPT_FACE",FACE,{"disambiguationData":[OSD([subQ29])]}),makeQuery(id+"F1.opExtrude","SWEPT_FACE",FACE,{"disambiguationData":[OSD([subQ28])]}),makeQuery(id+"F1.opExtrude","SWEPT_FACE",FACE,{"disambiguationData":[OSD([subQ27])]}),makeQuery(id+"F1.opExtrude","SWEPT_FACE",FACE,{"disambiguationData":[OSD([subQ26])]}),makeQuery(id+"F1.opExtrude","SWEPT_FACE",FACE,{"disambiguationData":[OSD([subQ25])]}),makeQuery(id+"F1.opExtrude","SWEPT_FACE",FACE,{"disambiguationData":[OSD([subQ24])]}),makeQuery(id+"F1.opExtrude","SWEPT_FACE",FACE,{"disambiguationData":[OSD([subQ23])]}),makeQuery(id+"F1.opExtrude","SWEPT_FACE",FACE,{"disambiguationData":[OSD([subQ22])]}),makeQuery(id+"F1.opExtrude","SWEPT_FACE",FACE,{"disambiguationData":[OSD([subQ21])]}),makeQuery(id+"F1.opExtrude","SWEPT_FACE",FACE,{"disambiguationData":[OSD([subQ20])]}),makeQuery(id+"F1.opExtrude","SWEPT_FACE",FACE,{"disambiguationData":[OSD([subQ19])]}),makeQuery(id+"F1.opExtrude","SWEPT_FACE",FACE,{"disambiguationData":[OSD([subQ18])]}),makeQuery(id+"F1.opExtrude","SWEPT_FACE",FACE,{"disambiguationData":[OSD([subQ17])]}),makeQuery(id+"F1.opExtrude","SWEPT_FACE",FACE,{"disambiguationData":[OSD([subQ16])]}),makeQuery(id+"F1.opExtrude","SWEPT_FACE",FACE,{"disambiguationData":[OSD([subQ15])]}),makeQuery(id+"F1.opExtrude","SWEPT_FACE",FACE,{"disambiguationData":[OSD([subQ14])]}),makeQuery(id+"F1.opExtrude","SWEPT_FACE",FACE,{"disambiguationData":[OSD([subQ13])]}),makeQuery(id+"F1.opExtrude","SWEPT_FACE",FACE,{"disambiguationData":[OSD([subQ12])]}),makeQuery(id+"F1.opExtrude","SWEPT_FACE",FACE,{"disambiguationData":[OSD([subQ11])]}),makeQuery(id+"F1.opExtrude","SWEPT_FACE",FACE,{"disambiguationData":[OSD([subQ10])]}),makeQuery(id+"F1.opExtrude","SWEPT_FACE",FACE,{"disambiguationData":[OSD([subQ9])]}),makeQuery(id+"F1.opExtrude","SWEPT_FACE",FACE,{"disambiguationData":[OSD([subQ8])]}),makeQuery(id+"F1.opExtrude","SWEPT_FACE",FACE,{"disambiguationData":[OSD([subQ7])]}),makeQuery(id+"F1.opExtrude","SWEPT_FACE",FACE,{"disambiguationData":[OSD([subQ3])]}),makeQuery(id+"F1.opExtrude","SWEPT_FACE",FACE,{"disambiguationData":[OSD([subQ134])]}),makeQuery(id+"F1.opExtrude","SWEPT_FACE",FACE,{"disambiguationData":[OSD([subQ2])]}),makeQuery(id+"F1.opExtrude","SWEPT_FACE",FACE,{"disambiguationData":[OSD([subQ1])]}),makeQuery(id+"F1.opExtrude","SWEPT_FACE",FACE,{"disambiguationData":[OSD([subQ0])]}),makeQuery(id+"F1.opExtrude","SWEPT_FACE",FACE,{"disambiguationData":[OSD([subQ200])]}),makeQuery(id+"F1.opExtrude","SWEPT_FACE",FACE,{"disambiguationData":[OSD([subQ201])]}),makeQuery(id+"F1.opExtrude","SWEPT_FACE",FACE,{"disambiguationData":[OSD([subQ202])]}),makeQuery(id+"F1.opExtrude","SWEPT_FACE",FACE,{"disambiguationData":[OSD([subQ203])]}),makeQuery(id+"F1.opExtrude","SWEPT_FACE",FACE,{"disambiguationData":[OSD([subQ204])]}),makeQuery(id+"F1.opExtrude","SWEPT_FACE",FACE,{"disambiguationData":[OSD([subQ205])]}),makeQuery(id+"F1.opExtrude","SWEPT_FACE",FACE,{"disambiguationData":[OSD([subQ206])]}),makeQuery(id+"F1.opExtrude","SWEPT_FACE",FACE,{"disambiguationData":[OSD([subQ207])]}),makeQuery(id+"F1.opExtrude","SWEPT_FACE",FACE,{"disambiguationData":[OSD([subQ208])]}),makeQuery(id+"F1.opExtrude","SWEPT_FACE",FACE,{"disambiguationData":[OSD([subQ209])]}),makeQuery(id+"F1.opExtrude","SWEPT_FACE",FACE,{"disambiguationData":[OSD([subQ210])]}),makeQuery(id+"F1.opExtrude","SWEPT_FACE",FACE,{"disambiguationData":[OSD([subQ211])]}),makeQuery(id+"F1.opExtrude","SWEPT_FACE",FACE,{"disambiguationData":[OSD([subQ212])]}),makeQuery(id+"F1.opExtrude","SWEPT_FACE",FACE,{"disambiguationData":[OSD([subQ213])]}),makeQuery(id+"F1.opExtrude","SWEPT_FACE",FACE,{"disambiguationData":[OSD([subQ214])]}),makeQuery(id+"F1.opExtrude","SWEPT_FACE",FACE,{"disambiguationData":[OSD([subQ215])]}),makeQuery(id+"F1.opExtrude","SWEPT_FACE",FACE,{"disambiguationData":[OSD([subQ217])]}),makeQuery(id+"F1.opExtrude","SWEPT_FACE",FACE,{"disambiguationData":[OSD([subQ250])]}),makeQuery(id+"F1.opExtrude","SWEPT_FACE",FACE,{"disambiguationData":[OSD([subQ249])]}),makeQuery(id+"F1.opExtrude","SWEPT_FACE",FACE,{"disambiguationData":[OSD([subQ248])]}),makeQuery(id+"F1.opExtrude","SWEPT_FACE",FACE,{"disambiguationData":[OSD([subQ247])]}),makeQuery(id+"F1.opExtrude","SWEPT_FACE",FACE,{"disambiguationData":[OSD([subQ246])]}),makeQuery(id+"F1.opExtrude","SWEPT_FACE",FACE,{"disambiguationData":[OSD([subQ245])]}),makeQuery(id+"F1.opExtrude","SWEPT_FACE",FACE,{"disambiguationData":[OSD([subQ244])]}),makeQuery(id+"F1.opExtrude","SWEPT_FACE",FACE,{"disambiguationData":[OSD([subQ243])]}),makeQuery(id+"F1.opExtrude","SWEPT_FACE",FACE,{"disambiguationData":[OSD([subQ242])]}),makeQuery(id+"F1.opExtrude","SWEPT_FACE",FACE,{"disambiguationData":[OSD([subQ241])]}),makeQuery(id+"F1.opExtrude","SWEPT_FACE",FACE,{"disambiguationData":[OSD([subQ240])]}),makeQuery(id+"F1.opExtrude","SWEPT_FACE",FACE,{"disambiguationData":[OSD([subQ239])]}),makeQuery(id+"F1.opExtrude","SWEPT_FACE",FACE,{"disambiguationData":[OSD([subQ238])]}),makeQuery(id+"F1.opExtrude","SWEPT_FACE",FACE,{"disambiguationData":[OSD([subQ237])]}),makeQuery(id+"F1.opExtrude","SWEPT_FACE",FACE,{"disambiguationData":[OSD([subQ236])]}),makeQuery(id+"F1.opExtrude","SWEPT_FACE",FACE,{"disambiguationData":[OSD([subQ235])]}),makeQuery(id+"F1.opExtrude","SWEPT_FACE",FACE,{"disambiguationData":[OSD([subQ234])]}),makeQuery(id+"F1.opExtrude","SWEPT_FACE",FACE,{"disambiguationData":[OSD([subQ233])]}),makeQuery(id+"F1.opExtrude","SWEPT_FACE",FACE,{"disambiguationData":[OSD([subQ232])]}),makeQuery(id+"F1.opExtrude","SWEPT_FACE",FACE,{"disambiguationData":[OSD([subQ231])]}),makeQuery(id+"F1.opExtrude","SWEPT_FACE",FACE,{"disambiguationData":[OSD([subQ230])]}),makeQuery(id+"F1.opExtrude","SWEPT_FACE",FACE,{"disambiguationData":[OSD([subQ229])]}),makeQuery(id+"F1.opExtrude","SWEPT_FACE",FACE,{"disambiguationData":[OSD([subQ228])]}),makeQuery(id+"F1.opExtrude","SWEPT_FACE",FACE,{"disambiguationData":[OSD([subQ227])]}),makeQuery(id+"F1.opExtrude","SWEPT_FACE",FACE,{"disambiguationData":[OSD([subQ226])]}),makeQuery(id+"F1.opExtrude","SWEPT_FACE",FACE,{"disambiguationData":[OSD([subQ225])]}),makeQuery(id+"F4.boolean.opBoolean","COPY",FACE,{"derivedFrom":makeQuery(id+"F4.opExtrude","SWEPT_FACE",FACE,{"disambiguationData":[OSD([subQ216])]})}),subQ251,makeQuery(id+"F4.boolean.opBoolean","COPY",FACE,{"derivedFrom":makeQuery(id+"F4.opExtrude","SWEPT_FACE",FACE,{"disambiguationData":[OSD([subQ224])]})}),makeQuery(id+"F4.boolean.opBoolean","COPY",FACE,{"derivedFrom":makeQuery(id+"F4.opExtrude","SWEPT_FACE",FACE,{"disambiguationData":[OSD([subQ223])]})}),makeQuery(id+"F4.boolean.opBoolean","COPY",FACE,{"derivedFrom":makeQuery(id+"F4.opExtrude","SWEPT_FACE",FACE,{"disambiguationData":[OSD([subQ222])]})}),makeQuery(id+"F4.boolean.opBoolean","COPY",FACE,{"derivedFrom":makeQuery(id+"F4.opExtrude","SWEPT_FACE",FACE,{"disambiguationData":[OSD([subQ221])]})}),makeQuery(id+"F4.boolean.opBoolean","COPY",FACE,{"derivedFrom":makeQuery(id+"F4.opExtrude","SWEPT_FACE",FACE,{"disambiguationData":[OSD([subQ220])]})}),makeQuery(id+"F4.boolean.opBoolean","COPY",FACE,{"derivedFrom":makeQuery(id+"F4.opExtrude","SWEPT_FACE",FACE,{"disambiguationData":[OSD([subQ219])]})}),makeQuery(id+"F4.boolean.opBoolean","COPY",FACE,{"derivedFrom":makeQuery(id+"F4.opExtrude","SWEPT_FACE",FACE,{"disambiguationData":[OSD([subQ218])]})}),subQ6,makeQuery(id+"F8.boolean.opBoolean","COPY",FACE,{"derivedFrom":makeQuery(id+"F8.opExtrude","SWEPT_FACE",FACE,{"disambiguationData":[OSD([subQ5])]})}),makeQuery(id+"F8.boolean.opBoolean","COPY",FACE,{"derivedFrom":makeQuery(id+"F8.opExtrude","SWEPT_FACE",FACE,{"disambiguationData":[OSD([subQ4])]})}),makeQuery(id+"F12.opExtrude","SWEPT_FACE",FACE,{"disambiguationData":[OSD([sQuery(id+"F11.wireOp",EDGE,"E257")])]}),makeQuery(id+"F12.opExtrude","SWEPT_FACE",FACE,{"disambiguationData":[OSD([sQuery(id+"F11.wireOp",EDGE,"E258")])]}),makeQuery(id+"F12.opExtrude","SWEPT_FACE",FACE,{"disambiguationData":[OSD([sQuery(id+"F11.wireOp",EDGE,"E259")])]}),makeQuery(id+"F12.opExtrude","SWEPT_FACE",FACE,{"disambiguationData":[OSD([sQuery(id+"F11.wireOp",EDGE,"E260")])]}),makeQuery(id+"F12.opExtrude","SWEPT_FACE",FACE,{"disambiguationData":[OSD([sQuery(id+"F11.wireOp",EDGE,"E261")])]}),makeQuery(id+"F12.opExtrude","SWEPT_FACE",FACE,{"disambiguationData":[OSD([sQuery(id+"F11.wireOp",EDGE,"E262")])]}),makeQuery(id+"F12.opExtrude","SWEPT_FACE",FACE,{"disambiguationData":[OSD([sQuery(id+"F11.wireOp",EDGE,"E263")])]}),makeQuery(id+"F12.opExtrude","SWEPT_FACE",FACE,{"disambiguationData":[OSD([sQuery(id+"F11.wireOp",EDGE,"E264")])]}),makeQuery(id+"F12.opExtrude","SWEPT_FACE",FACE,{"disambiguationData":[OSD([sQuery(id+"F11.wireOp",EDGE,"E265")])]}),makeQuery(id+"F12.opExtrude","SWEPT_FACE",FACE,{"disambiguationData":[OSD([sQuery(id+"F11.wireOp",EDGE,"E266")])]})])],"derivedFrom":makeQuery(id+"F8.boolean.opBoolean","MERGE",FACE,{"derivedFrom":[subQ251,subQ6]})});}
            var sketch = newSketch(context, id + "F21", { "sketchPlane" : qUnion([Q0])});
            skLineSegment(sketch, "E296.bottom", {"start": v(-107.28, 46.65) * mm, "end": v(-102.28, 46.65) * mm});
            skLineSegment(sketch, "E296.top", {"start": v(-107.28, 47.32) * mm, "end": v(-102.28, 47.32) * mm});
            skLineSegment(sketch, "E296.left", {"start": v(-107.28, 46.65) * mm, "end": v(-107.28, 47.32) * mm});
            skLineSegment(sketch, "E296.right", {"start": v(-102.28, 46.65) * mm, "end": v(-102.28, 47.32) * mm});
            skLineSegment(sketch, "E297.bottom", {"start": v(-107.28, 32.65) * mm, "end": v(-102.28, 32.65) * mm});
            skLineSegment(sketch, "E297.top", {"start": v(-107.28, 31.98) * mm, "end": v(-102.28, 31.98) * mm});
            skLineSegment(sketch, "E297.left", {"start": v(-107.28, 32.65) * mm, "end": v(-107.28, 31.98) * mm});
            skLineSegment(sketch, "E297.right", {"start": v(-102.28, 32.65) * mm, "end": v(-102.28, 31.98) * mm});
            skPoint(sketch, "E298", {"position": v(-104.78, 46.65) * mm});
            skPoint(sketch, "E299", {"position": v(-104.78, 32.65) * mm});
            skLineSegment(sketch, "E300.0.1.0", {"start": v(-107.28, 28.27) * mm, "end": v(-102.28, 28.27) * mm});
            skLineSegment(sketch, "E300.0.1.1", {"start": v(-102.28, 27.6) * mm, "end": v(-102.28, 28.27) * mm});
            skLineSegment(sketch, "E300.0.1.2", {"start": v(-107.28, 27.6) * mm, "end": v(-102.28, 27.6) * mm});
            skLineSegment(sketch, "E300.0.1.3", {"start": v(-107.28, 27.6) * mm, "end": v(-107.28, 28.27) * mm});
            skLineSegment(sketch, "E300.0.1.4", {"start": v(-107.28, 13.6) * mm, "end": v(-102.28, 13.6) * mm});
            skLineSegment(sketch, "E300.0.1.5", {"start": v(-102.28, 13.6) * mm, "end": v(-102.28, 12.93) * mm});
            skLineSegment(sketch, "E300.0.1.6", {"start": v(-107.28, 12.93) * mm, "end": v(-102.28, 12.93) * mm});
            skLineSegment(sketch, "E300.0.1.7", {"start": v(-107.28, 13.6) * mm, "end": v(-107.28, 12.93) * mm});
            skLineSegment(sketch, "E300.0.2.0", {"start": v(-107.28, 9.22) * mm, "end": v(-102.28, 9.22) * mm});
            skLineSegment(sketch, "E300.0.2.1", {"start": v(-102.28, 8.55) * mm, "end": v(-102.28, 9.22) * mm});
            skLineSegment(sketch, "E300.0.2.2", {"start": v(-107.28, 8.55) * mm, "end": v(-102.28, 8.55) * mm});
            skLineSegment(sketch, "E300.0.2.3", {"start": v(-107.28, 8.55) * mm, "end": v(-107.28, 9.22) * mm});
            skLineSegment(sketch, "E300.0.2.4", {"start": v(-107.28, -5.45) * mm, "end": v(-102.28, -5.45) * mm});
            skLineSegment(sketch, "E300.0.2.5", {"start": v(-102.28, -5.45) * mm, "end": v(-102.28, -6.12) * mm});
            skLineSegment(sketch, "E300.0.2.6", {"start": v(-107.28, -6.12) * mm, "end": v(-102.28, -6.12) * mm});
            skLineSegment(sketch, "E300.0.2.7", {"start": v(-107.28, -5.45) * mm, "end": v(-107.28, -6.12) * mm});
            skLineSegment(sketch, "E300.0.3.0", {"start": v(-107.28, -9.83) * mm, "end": v(-102.28, -9.83) * mm});
            skLineSegment(sketch, "E300.0.3.1", {"start": v(-102.28, -10.5) * mm, "end": v(-102.28, -9.83) * mm});
            skLineSegment(sketch, "E300.0.3.2", {"start": v(-107.28, -10.5) * mm, "end": v(-102.28, -10.5) * mm});
            skLineSegment(sketch, "E300.0.3.3", {"start": v(-107.28, -10.5) * mm, "end": v(-107.28, -9.83) * mm});
            skLineSegment(sketch, "E300.0.3.4", {"start": v(-107.28, -24.5) * mm, "end": v(-102.28, -24.5) * mm});
            skLineSegment(sketch, "E300.0.3.5", {"start": v(-102.28, -24.5) * mm, "end": v(-102.28, -25.17) * mm});
            skLineSegment(sketch, "E300.0.3.6", {"start": v(-107.28, -25.17) * mm, "end": v(-102.28, -25.17) * mm});
            skLineSegment(sketch, "E300.0.3.7", {"start": v(-107.28, -24.5) * mm, "end": v(-107.28, -25.17) * mm});
            skLineSegment(sketch, "E300.0.4.0", {"start": v(-107.28, -28.88) * mm, "end": v(-102.28, -28.88) * mm});
            skLineSegment(sketch, "E300.0.4.1", {"start": v(-102.28, -29.55) * mm, "end": v(-102.28, -28.88) * mm});
            skLineSegment(sketch, "E300.0.4.2", {"start": v(-107.28, -29.55) * mm, "end": v(-102.28, -29.55) * mm});
            skLineSegment(sketch, "E300.0.4.3", {"start": v(-107.28, -29.55) * mm, "end": v(-107.28, -28.88) * mm});
            skLineSegment(sketch, "E300.0.4.4", {"start": v(-107.28, -43.55) * mm, "end": v(-102.28, -43.55) * mm});
            skLineSegment(sketch, "E300.0.4.5", {"start": v(-102.28, -43.55) * mm, "end": v(-102.28, -44.22) * mm});
            skLineSegment(sketch, "E300.0.4.6", {"start": v(-107.28, -44.22) * mm, "end": v(-102.28, -44.22) * mm});
            skLineSegment(sketch, "E300.0.4.7", {"start": v(-107.28, -43.55) * mm, "end": v(-107.28, -44.22) * mm});
            skLineSegment(sketch, "E300.1.0.0", {"start": v(-88.23, 47.32) * mm, "end": v(-83.23, 47.32) * mm});
            skLineSegment(sketch, "E300.1.0.1", {"start": v(-83.23, 46.65) * mm, "end": v(-83.23, 47.32) * mm});
            skLineSegment(sketch, "E300.1.0.2", {"start": v(-88.23, 46.65) * mm, "end": v(-83.23, 46.65) * mm});
            skLineSegment(sketch, "E300.1.0.3", {"start": v(-88.23, 46.65) * mm, "end": v(-88.23, 47.32) * mm});
            skLineSegment(sketch, "E300.1.0.4", {"start": v(-88.23, 32.65) * mm, "end": v(-83.23, 32.65) * mm});
            skLineSegment(sketch, "E300.1.0.5", {"start": v(-83.23, 32.65) * mm, "end": v(-83.23, 31.98) * mm});
            skLineSegment(sketch, "E300.1.0.6", {"start": v(-88.23, 31.98) * mm, "end": v(-83.23, 31.98) * mm});
            skLineSegment(sketch, "E300.1.0.7", {"start": v(-88.23, 32.65) * mm, "end": v(-88.23, 31.98) * mm});
            skLineSegment(sketch, "E300.1.1.0", {"start": v(-88.23, 28.27) * mm, "end": v(-83.23, 28.27) * mm});
            skLineSegment(sketch, "E300.1.1.1", {"start": v(-83.23, 27.6) * mm, "end": v(-83.23, 28.27) * mm});
            skLineSegment(sketch, "E300.1.1.2", {"start": v(-88.23, 27.6) * mm, "end": v(-83.23, 27.6) * mm});
            skLineSegment(sketch, "E300.1.1.3", {"start": v(-88.23, 27.6) * mm, "end": v(-88.23, 28.27) * mm});
            skLineSegment(sketch, "E300.1.1.4", {"start": v(-88.23, 13.6) * mm, "end": v(-83.23, 13.6) * mm});
            skLineSegment(sketch, "E300.1.1.5", {"start": v(-83.23, 13.6) * mm, "end": v(-83.23, 12.93) * mm});
            skLineSegment(sketch, "E300.1.1.6", {"start": v(-88.23, 12.93) * mm, "end": v(-83.23, 12.93) * mm});
            skLineSegment(sketch, "E300.1.1.7", {"start": v(-88.23, 13.6) * mm, "end": v(-88.23, 12.93) * mm});
            skLineSegment(sketch, "E300.1.2.0", {"start": v(-88.23, 9.22) * mm, "end": v(-83.23, 9.22) * mm});
            skLineSegment(sketch, "E300.1.2.1", {"start": v(-83.23, 8.55) * mm, "end": v(-83.23, 9.22) * mm});
            skLineSegment(sketch, "E300.1.2.2", {"start": v(-88.23, 8.55) * mm, "end": v(-83.23, 8.55) * mm});
            skLineSegment(sketch, "E300.1.2.3", {"start": v(-88.23, 8.55) * mm, "end": v(-88.23, 9.22) * mm});
            skLineSegment(sketch, "E300.1.2.4", {"start": v(-88.23, -5.45) * mm, "end": v(-83.23, -5.45) * mm});
            skLineSegment(sketch, "E300.1.2.5", {"start": v(-83.23, -5.45) * mm, "end": v(-83.23, -6.12) * mm});
            skLineSegment(sketch, "E300.1.2.6", {"start": v(-88.23, -6.12) * mm, "end": v(-83.23, -6.12) * mm});
            skLineSegment(sketch, "E300.1.2.7", {"start": v(-88.23, -5.45) * mm, "end": v(-88.23, -6.12) * mm});
            skLineSegment(sketch, "E300.1.3.0", {"start": v(-88.23, -9.83) * mm, "end": v(-83.23, -9.83) * mm});
            skLineSegment(sketch, "E300.1.3.1", {"start": v(-83.23, -10.5) * mm, "end": v(-83.23, -9.83) * mm});
            skLineSegment(sketch, "E300.1.3.2", {"start": v(-88.23, -10.5) * mm, "end": v(-83.23, -10.5) * mm});
            skLineSegment(sketch, "E300.1.3.3", {"start": v(-88.23, -10.5) * mm, "end": v(-88.23, -9.83) * mm});
            skLineSegment(sketch, "E300.1.3.4", {"start": v(-88.23, -24.5) * mm, "end": v(-83.23, -24.5) * mm});
            skLineSegment(sketch, "E300.1.3.5", {"start": v(-83.23, -24.5) * mm, "end": v(-83.23, -25.17) * mm});
            skLineSegment(sketch, "E300.1.3.6", {"start": v(-88.23, -25.17) * mm, "end": v(-83.23, -25.17) * mm});
            skLineSegment(sketch, "E300.1.3.7", {"start": v(-88.23, -24.5) * mm, "end": v(-88.23, -25.17) * mm});
            skLineSegment(sketch, "E300.1.4.0", {"start": v(-88.23, -28.88) * mm, "end": v(-83.23, -28.88) * mm});
            skLineSegment(sketch, "E300.1.4.1", {"start": v(-83.23, -29.55) * mm, "end": v(-83.23, -28.88) * mm});
            skLineSegment(sketch, "E300.1.4.2", {"start": v(-88.23, -29.55) * mm, "end": v(-83.23, -29.55) * mm});
            skLineSegment(sketch, "E300.1.4.3", {"start": v(-88.23, -29.55) * mm, "end": v(-88.23, -28.88) * mm});
            skLineSegment(sketch, "E300.1.4.4", {"start": v(-88.23, -43.55) * mm, "end": v(-83.23, -43.55) * mm});
            skLineSegment(sketch, "E300.1.4.5", {"start": v(-83.23, -43.55) * mm, "end": v(-83.23, -44.22) * mm});
            skLineSegment(sketch, "E300.1.4.6", {"start": v(-88.23, -44.22) * mm, "end": v(-83.23, -44.22) * mm});
            skLineSegment(sketch, "E300.1.4.7", {"start": v(-88.23, -43.55) * mm, "end": v(-88.23, -44.22) * mm});
            skLineSegment(sketch, "E300.2.0.0", {"start": v(-69.18, 47.32) * mm, "end": v(-64.18, 47.32) * mm});
            skLineSegment(sketch, "E300.2.0.1", {"start": v(-64.18, 46.65) * mm, "end": v(-64.18, 47.32) * mm});
            skLineSegment(sketch, "E300.2.0.2", {"start": v(-69.18, 46.65) * mm, "end": v(-64.18, 46.65) * mm});
            skLineSegment(sketch, "E300.2.0.3", {"start": v(-69.18, 46.65) * mm, "end": v(-69.18, 47.32) * mm});
            skLineSegment(sketch, "E300.2.0.4", {"start": v(-69.18, 32.65) * mm, "end": v(-64.18, 32.65) * mm});
            skLineSegment(sketch, "E300.2.0.5", {"start": v(-64.18, 32.65) * mm, "end": v(-64.18, 31.98) * mm});
            skLineSegment(sketch, "E300.2.0.6", {"start": v(-69.18, 31.98) * mm, "end": v(-64.18, 31.98) * mm});
            skLineSegment(sketch, "E300.2.0.7", {"start": v(-69.18, 32.65) * mm, "end": v(-69.18, 31.98) * mm});
            skLineSegment(sketch, "E300.2.1.0", {"start": v(-69.18, 28.27) * mm, "end": v(-64.18, 28.27) * mm});
            skLineSegment(sketch, "E300.2.1.1", {"start": v(-64.18, 27.6) * mm, "end": v(-64.18, 28.27) * mm});
            skLineSegment(sketch, "E300.2.1.2", {"start": v(-69.18, 27.6) * mm, "end": v(-64.18, 27.6) * mm});
            skLineSegment(sketch, "E300.2.1.3", {"start": v(-69.18, 27.6) * mm, "end": v(-69.18, 28.27) * mm});
            skLineSegment(sketch, "E300.2.1.4", {"start": v(-69.18, 13.6) * mm, "end": v(-64.18, 13.6) * mm});
            skLineSegment(sketch, "E300.2.1.5", {"start": v(-64.18, 13.6) * mm, "end": v(-64.18, 12.93) * mm});
            skLineSegment(sketch, "E300.2.1.6", {"start": v(-69.18, 12.93) * mm, "end": v(-64.18, 12.93) * mm});
            skLineSegment(sketch, "E300.2.1.7", {"start": v(-69.18, 13.6) * mm, "end": v(-69.18, 12.93) * mm});
            skLineSegment(sketch, "E300.2.2.0", {"start": v(-69.18, 9.22) * mm, "end": v(-64.18, 9.22) * mm});
            skLineSegment(sketch, "E300.2.2.1", {"start": v(-64.18, 8.55) * mm, "end": v(-64.18, 9.22) * mm});
            skLineSegment(sketch, "E300.2.2.2", {"start": v(-69.18, 8.55) * mm, "end": v(-64.18, 8.55) * mm});
            skLineSegment(sketch, "E300.2.2.3", {"start": v(-69.18, 8.55) * mm, "end": v(-69.18, 9.22) * mm});
            skLineSegment(sketch, "E300.2.2.4", {"start": v(-69.18, -5.45) * mm, "end": v(-64.18, -5.45) * mm});
            skLineSegment(sketch, "E300.2.2.5", {"start": v(-64.18, -5.45) * mm, "end": v(-64.18, -6.12) * mm});
            skLineSegment(sketch, "E300.2.2.6", {"start": v(-69.18, -6.12) * mm, "end": v(-64.18, -6.12) * mm});
            skLineSegment(sketch, "E300.2.2.7", {"start": v(-69.18, -5.45) * mm, "end": v(-69.18, -6.12) * mm});
            skLineSegment(sketch, "E300.2.3.0", {"start": v(-69.18, -9.83) * mm, "end": v(-64.18, -9.83) * mm});
            skLineSegment(sketch, "E300.2.3.1", {"start": v(-64.18, -10.5) * mm, "end": v(-64.18, -9.83) * mm});
            skLineSegment(sketch, "E300.2.3.2", {"start": v(-69.18, -10.5) * mm, "end": v(-64.18, -10.5) * mm});
            skLineSegment(sketch, "E300.2.3.3", {"start": v(-69.18, -10.5) * mm, "end": v(-69.18, -9.83) * mm});
            skLineSegment(sketch, "E300.2.3.4", {"start": v(-69.18, -24.5) * mm, "end": v(-64.18, -24.5) * mm});
            skLineSegment(sketch, "E300.2.3.5", {"start": v(-64.18, -24.5) * mm, "end": v(-64.18, -25.17) * mm});
            skLineSegment(sketch, "E300.2.3.6", {"start": v(-69.18, -25.17) * mm, "end": v(-64.18, -25.17) * mm});
            skLineSegment(sketch, "E300.2.3.7", {"start": v(-69.18, -24.5) * mm, "end": v(-69.18, -25.17) * mm});
            skLineSegment(sketch, "E300.2.4.0", {"start": v(-69.18, -28.88) * mm, "end": v(-64.18, -28.88) * mm});
            skLineSegment(sketch, "E300.2.4.1", {"start": v(-64.18, -29.55) * mm, "end": v(-64.18, -28.88) * mm});
            skLineSegment(sketch, "E300.2.4.2", {"start": v(-69.18, -29.55) * mm, "end": v(-64.18, -29.55) * mm});
            skLineSegment(sketch, "E300.2.4.3", {"start": v(-69.18, -29.55) * mm, "end": v(-69.18, -28.88) * mm});
            skLineSegment(sketch, "E300.2.4.4", {"start": v(-69.18, -43.55) * mm, "end": v(-64.18, -43.55) * mm});
            skLineSegment(sketch, "E300.2.4.5", {"start": v(-64.18, -43.55) * mm, "end": v(-64.18, -44.22) * mm});
            skLineSegment(sketch, "E300.2.4.6", {"start": v(-69.18, -44.22) * mm, "end": v(-64.18, -44.22) * mm});
            skLineSegment(sketch, "E300.2.4.7", {"start": v(-69.18, -43.55) * mm, "end": v(-69.18, -44.22) * mm});
            skLineSegment(sketch, "E300.3.0.0", {"start": v(-50.13, 47.32) * mm, "end": v(-45.13, 47.32) * mm});
            skLineSegment(sketch, "E300.3.0.1", {"start": v(-45.13, 46.65) * mm, "end": v(-45.13, 47.32) * mm});
            skLineSegment(sketch, "E300.3.0.2", {"start": v(-50.13, 46.65) * mm, "end": v(-45.13, 46.65) * mm});
            skLineSegment(sketch, "E300.3.0.3", {"start": v(-50.13, 46.65) * mm, "end": v(-50.13, 47.32) * mm});
            skLineSegment(sketch, "E300.3.0.4", {"start": v(-50.13, 32.65) * mm, "end": v(-45.13, 32.65) * mm});
            skLineSegment(sketch, "E300.3.0.5", {"start": v(-45.13, 32.65) * mm, "end": v(-45.13, 31.98) * mm});
            skLineSegment(sketch, "E300.3.0.6", {"start": v(-50.13, 31.98) * mm, "end": v(-45.13, 31.98) * mm});
            skLineSegment(sketch, "E300.3.0.7", {"start": v(-50.13, 32.65) * mm, "end": v(-50.13, 31.98) * mm});
            skLineSegment(sketch, "E300.3.1.0", {"start": v(-50.13, 28.27) * mm, "end": v(-45.13, 28.27) * mm});
            skLineSegment(sketch, "E300.3.1.1", {"start": v(-45.13, 27.6) * mm, "end": v(-45.13, 28.27) * mm});
            skLineSegment(sketch, "E300.3.1.2", {"start": v(-50.13, 27.6) * mm, "end": v(-45.13, 27.6) * mm});
            skLineSegment(sketch, "E300.3.1.3", {"start": v(-50.13, 27.6) * mm, "end": v(-50.13, 28.27) * mm});
            skLineSegment(sketch, "E300.3.1.4", {"start": v(-50.13, 13.6) * mm, "end": v(-45.13, 13.6) * mm});
            skLineSegment(sketch, "E300.3.1.5", {"start": v(-45.13, 13.6) * mm, "end": v(-45.13, 12.93) * mm});
            skLineSegment(sketch, "E300.3.1.6", {"start": v(-50.13, 12.93) * mm, "end": v(-45.13, 12.93) * mm});
            skLineSegment(sketch, "E300.3.1.7", {"start": v(-50.13, 13.6) * mm, "end": v(-50.13, 12.93) * mm});
            skLineSegment(sketch, "E300.3.2.0", {"start": v(-50.13, 9.22) * mm, "end": v(-45.13, 9.22) * mm});
            skLineSegment(sketch, "E300.3.2.1", {"start": v(-45.13, 8.55) * mm, "end": v(-45.13, 9.22) * mm});
            skLineSegment(sketch, "E300.3.2.2", {"start": v(-50.13, 8.55) * mm, "end": v(-45.13, 8.55) * mm});
            skLineSegment(sketch, "E300.3.2.3", {"start": v(-50.13, 8.55) * mm, "end": v(-50.13, 9.22) * mm});
            skLineSegment(sketch, "E300.3.2.4", {"start": v(-50.13, -5.45) * mm, "end": v(-45.13, -5.45) * mm});
            skLineSegment(sketch, "E300.3.2.5", {"start": v(-45.13, -5.45) * mm, "end": v(-45.13, -6.12) * mm});
            skLineSegment(sketch, "E300.3.2.6", {"start": v(-50.13, -6.12) * mm, "end": v(-45.13, -6.12) * mm});
            skLineSegment(sketch, "E300.3.2.7", {"start": v(-50.13, -5.45) * mm, "end": v(-50.13, -6.12) * mm});
            skLineSegment(sketch, "E300.3.3.0", {"start": v(-50.13, -9.83) * mm, "end": v(-45.13, -9.83) * mm});
            skLineSegment(sketch, "E300.3.3.1", {"start": v(-45.13, -10.5) * mm, "end": v(-45.13, -9.83) * mm});
            skLineSegment(sketch, "E300.3.3.2", {"start": v(-50.13, -10.5) * mm, "end": v(-45.13, -10.5) * mm});
            skLineSegment(sketch, "E300.3.3.3", {"start": v(-50.13, -10.5) * mm, "end": v(-50.13, -9.83) * mm});
            skLineSegment(sketch, "E300.3.3.4", {"start": v(-50.13, -24.5) * mm, "end": v(-45.13, -24.5) * mm});
            skLineSegment(sketch, "E300.3.3.5", {"start": v(-45.13, -24.5) * mm, "end": v(-45.13, -25.17) * mm});
            skLineSegment(sketch, "E300.3.3.6", {"start": v(-50.13, -25.17) * mm, "end": v(-45.13, -25.17) * mm});
            skLineSegment(sketch, "E300.3.3.7", {"start": v(-50.13, -24.5) * mm, "end": v(-50.13, -25.17) * mm});
            skLineSegment(sketch, "E300.3.4.0", {"start": v(-50.13, -28.88) * mm, "end": v(-45.13, -28.88) * mm});
            skLineSegment(sketch, "E300.3.4.1", {"start": v(-45.13, -29.55) * mm, "end": v(-45.13, -28.88) * mm});
            skLineSegment(sketch, "E300.3.4.2", {"start": v(-50.13, -29.55) * mm, "end": v(-45.13, -29.55) * mm});
            skLineSegment(sketch, "E300.3.4.3", {"start": v(-50.13, -29.55) * mm, "end": v(-50.13, -28.88) * mm});
            skLineSegment(sketch, "E300.3.4.4", {"start": v(-50.13, -43.55) * mm, "end": v(-45.13, -43.55) * mm});
            skLineSegment(sketch, "E300.3.4.5", {"start": v(-45.13, -43.55) * mm, "end": v(-45.13, -44.22) * mm});
            skLineSegment(sketch, "E300.3.4.6", {"start": v(-50.13, -44.22) * mm, "end": v(-45.13, -44.22) * mm});
            skLineSegment(sketch, "E300.3.4.7", {"start": v(-50.13, -43.55) * mm, "end": v(-50.13, -44.22) * mm});
            skLineSegment(sketch, "E300.4.0.0", {"start": v(-31.08, 47.32) * mm, "end": v(-26.08, 47.32) * mm});
            skLineSegment(sketch, "E300.4.0.1", {"start": v(-26.08, 46.65) * mm, "end": v(-26.08, 47.32) * mm});
            skLineSegment(sketch, "E300.4.0.2", {"start": v(-31.08, 46.65) * mm, "end": v(-26.08, 46.65) * mm});
            skLineSegment(sketch, "E300.4.0.3", {"start": v(-31.08, 46.65) * mm, "end": v(-31.08, 47.32) * mm});
            skLineSegment(sketch, "E300.4.0.4", {"start": v(-31.08, 32.65) * mm, "end": v(-26.08, 32.65) * mm});
            skLineSegment(sketch, "E300.4.0.5", {"start": v(-26.08, 32.65) * mm, "end": v(-26.08, 31.98) * mm});
            skLineSegment(sketch, "E300.4.0.6", {"start": v(-31.08, 31.98) * mm, "end": v(-26.08, 31.98) * mm});
            skLineSegment(sketch, "E300.4.0.7", {"start": v(-31.08, 32.65) * mm, "end": v(-31.08, 31.98) * mm});
            skLineSegment(sketch, "E300.4.1.0", {"start": v(-31.08, 28.27) * mm, "end": v(-26.08, 28.27) * mm});
            skLineSegment(sketch, "E300.4.1.1", {"start": v(-26.08, 27.6) * mm, "end": v(-26.08, 28.27) * mm});
            skLineSegment(sketch, "E300.4.1.2", {"start": v(-31.08, 27.6) * mm, "end": v(-26.08, 27.6) * mm});
            skLineSegment(sketch, "E300.4.1.3", {"start": v(-31.08, 27.6) * mm, "end": v(-31.08, 28.27) * mm});
            skLineSegment(sketch, "E300.4.1.4", {"start": v(-31.08, 13.6) * mm, "end": v(-26.08, 13.6) * mm});
            skLineSegment(sketch, "E300.4.1.5", {"start": v(-26.08, 13.6) * mm, "end": v(-26.08, 12.93) * mm});
            skLineSegment(sketch, "E300.4.1.6", {"start": v(-31.08, 12.93) * mm, "end": v(-26.08, 12.93) * mm});
            skLineSegment(sketch, "E300.4.1.7", {"start": v(-31.08, 13.6) * mm, "end": v(-31.08, 12.93) * mm});
            skLineSegment(sketch, "E300.4.2.0", {"start": v(-31.08, 9.22) * mm, "end": v(-26.08, 9.22) * mm});
            skLineSegment(sketch, "E300.4.2.1", {"start": v(-26.08, 8.55) * mm, "end": v(-26.08, 9.22) * mm});
            skLineSegment(sketch, "E300.4.2.2", {"start": v(-31.08, 8.55) * mm, "end": v(-26.08, 8.55) * mm});
            skLineSegment(sketch, "E300.4.2.3", {"start": v(-31.08, 8.55) * mm, "end": v(-31.08, 9.22) * mm});
            skLineSegment(sketch, "E300.4.2.4", {"start": v(-31.08, -5.45) * mm, "end": v(-26.08, -5.45) * mm});
            skLineSegment(sketch, "E300.4.2.5", {"start": v(-26.08, -5.45) * mm, "end": v(-26.08, -6.12) * mm});
            skLineSegment(sketch, "E300.4.2.6", {"start": v(-31.08, -6.12) * mm, "end": v(-26.08, -6.12) * mm});
            skLineSegment(sketch, "E300.4.2.7", {"start": v(-31.08, -5.45) * mm, "end": v(-31.08, -6.12) * mm});
            skLineSegment(sketch, "E300.4.3.0", {"start": v(-31.08, -9.83) * mm, "end": v(-26.08, -9.83) * mm});
            skLineSegment(sketch, "E300.4.3.1", {"start": v(-26.08, -10.5) * mm, "end": v(-26.08, -9.83) * mm});
            skLineSegment(sketch, "E300.4.3.2", {"start": v(-31.08, -10.5) * mm, "end": v(-26.08, -10.5) * mm});
            skLineSegment(sketch, "E300.4.3.3", {"start": v(-31.08, -10.5) * mm, "end": v(-31.08, -9.83) * mm});
            skLineSegment(sketch, "E300.4.3.4", {"start": v(-31.08, -24.5) * mm, "end": v(-26.08, -24.5) * mm});
            skLineSegment(sketch, "E300.4.3.5", {"start": v(-26.08, -24.5) * mm, "end": v(-26.08, -25.17) * mm});
            skLineSegment(sketch, "E300.4.3.6", {"start": v(-31.08, -25.17) * mm, "end": v(-26.08, -25.17) * mm});
            skLineSegment(sketch, "E300.4.3.7", {"start": v(-31.08, -24.5) * mm, "end": v(-31.08, -25.17) * mm});
            skLineSegment(sketch, "E300.4.4.0", {"start": v(-31.08, -28.88) * mm, "end": v(-26.08, -28.88) * mm});
            skLineSegment(sketch, "E300.4.4.1", {"start": v(-26.08, -29.55) * mm, "end": v(-26.08, -28.88) * mm});
            skLineSegment(sketch, "E300.4.4.2", {"start": v(-31.08, -29.55) * mm, "end": v(-26.08, -29.55) * mm});
            skLineSegment(sketch, "E300.4.4.3", {"start": v(-31.08, -29.55) * mm, "end": v(-31.08, -28.88) * mm});
            skLineSegment(sketch, "E300.4.4.4", {"start": v(-31.08, -43.55) * mm, "end": v(-26.08, -43.55) * mm});
            skLineSegment(sketch, "E300.4.4.5", {"start": v(-26.08, -43.55) * mm, "end": v(-26.08, -44.22) * mm});
            skLineSegment(sketch, "E300.4.4.6", {"start": v(-31.08, -44.22) * mm, "end": v(-26.08, -44.22) * mm});
            skLineSegment(sketch, "E300.4.4.7", {"start": v(-31.08, -43.55) * mm, "end": v(-31.08, -44.22) * mm});
            skLineSegment(sketch, "E300.5.0.0", {"start": v(-12.03, 47.32) * mm, "end": v(-7.03, 47.32) * mm});
            skLineSegment(sketch, "E300.5.0.1", {"start": v(-7.03, 46.65) * mm, "end": v(-7.03, 47.32) * mm});
            skLineSegment(sketch, "E300.5.0.2", {"start": v(-12.03, 46.65) * mm, "end": v(-7.03, 46.65) * mm});
            skLineSegment(sketch, "E300.5.0.3", {"start": v(-12.03, 46.65) * mm, "end": v(-12.03, 47.32) * mm});
            skLineSegment(sketch, "E300.5.0.4", {"start": v(-12.03, 32.65) * mm, "end": v(-7.03, 32.65) * mm});
            skLineSegment(sketch, "E300.5.0.5", {"start": v(-7.03, 32.65) * mm, "end": v(-7.03, 31.98) * mm});
            skLineSegment(sketch, "E300.5.0.6", {"start": v(-12.03, 31.98) * mm, "end": v(-7.03, 31.98) * mm});
            skLineSegment(sketch, "E300.5.0.7", {"start": v(-12.03, 32.65) * mm, "end": v(-12.03, 31.98) * mm});
            skLineSegment(sketch, "E300.5.1.0", {"start": v(-12.03, 28.27) * mm, "end": v(-7.03, 28.27) * mm});
            skLineSegment(sketch, "E300.5.1.1", {"start": v(-7.03, 27.6) * mm, "end": v(-7.03, 28.27) * mm});
            skLineSegment(sketch, "E300.5.1.2", {"start": v(-12.03, 27.6) * mm, "end": v(-7.03, 27.6) * mm});
            skLineSegment(sketch, "E300.5.1.3", {"start": v(-12.03, 27.6) * mm, "end": v(-12.03, 28.27) * mm});
            skLineSegment(sketch, "E300.5.1.4", {"start": v(-12.03, 13.6) * mm, "end": v(-7.03, 13.6) * mm});
            skLineSegment(sketch, "E300.5.1.5", {"start": v(-7.03, 13.6) * mm, "end": v(-7.03, 12.93) * mm});
            skLineSegment(sketch, "E300.5.1.6", {"start": v(-12.03, 12.93) * mm, "end": v(-7.03, 12.93) * mm});
            skLineSegment(sketch, "E300.5.1.7", {"start": v(-12.03, 13.6) * mm, "end": v(-12.03, 12.93) * mm});
            skLineSegment(sketch, "E300.5.2.0", {"start": v(-12.03, 9.22) * mm, "end": v(-7.03, 9.22) * mm});
            skLineSegment(sketch, "E300.5.2.1", {"start": v(-7.03, 8.55) * mm, "end": v(-7.03, 9.22) * mm});
            skLineSegment(sketch, "E300.5.2.2", {"start": v(-12.03, 8.55) * mm, "end": v(-7.03, 8.55) * mm});
            skLineSegment(sketch, "E300.5.2.3", {"start": v(-12.03, 8.55) * mm, "end": v(-12.03, 9.22) * mm});
            skLineSegment(sketch, "E300.5.2.4", {"start": v(-12.03, -5.45) * mm, "end": v(-7.03, -5.45) * mm});
            skLineSegment(sketch, "E300.5.2.5", {"start": v(-7.03, -5.45) * mm, "end": v(-7.03, -6.12) * mm});
            skLineSegment(sketch, "E300.5.2.6", {"start": v(-12.03, -6.12) * mm, "end": v(-7.03, -6.12) * mm});
            skLineSegment(sketch, "E300.5.2.7", {"start": v(-12.03, -5.45) * mm, "end": v(-12.03, -6.12) * mm});
            skLineSegment(sketch, "E300.5.3.0", {"start": v(-12.03, -9.83) * mm, "end": v(-7.03, -9.83) * mm});
            skLineSegment(sketch, "E300.5.3.1", {"start": v(-7.03, -10.5) * mm, "end": v(-7.03, -9.83) * mm});
            skLineSegment(sketch, "E300.5.3.2", {"start": v(-12.03, -10.5) * mm, "end": v(-7.03, -10.5) * mm});
            skLineSegment(sketch, "E300.5.3.3", {"start": v(-12.03, -10.5) * mm, "end": v(-12.03, -9.83) * mm});
            skLineSegment(sketch, "E300.5.3.4", {"start": v(-12.03, -24.5) * mm, "end": v(-7.03, -24.5) * mm});
            skLineSegment(sketch, "E300.5.3.5", {"start": v(-7.03, -24.5) * mm, "end": v(-7.03, -25.17) * mm});
            skLineSegment(sketch, "E300.5.3.6", {"start": v(-12.03, -25.17) * mm, "end": v(-7.03, -25.17) * mm});
            skLineSegment(sketch, "E300.5.3.7", {"start": v(-12.03, -24.5) * mm, "end": v(-12.03, -25.17) * mm});
            skLineSegment(sketch, "E300.5.4.0", {"start": v(-12.03, -28.88) * mm, "end": v(-7.03, -28.88) * mm});
            skLineSegment(sketch, "E300.5.4.1", {"start": v(-7.03, -29.55) * mm, "end": v(-7.03, -28.88) * mm});
            skLineSegment(sketch, "E300.5.4.2", {"start": v(-12.03, -29.55) * mm, "end": v(-7.03, -29.55) * mm});
            skLineSegment(sketch, "E300.5.4.3", {"start": v(-12.03, -29.55) * mm, "end": v(-12.03, -28.88) * mm});
            skLineSegment(sketch, "E300.5.4.4", {"start": v(-12.03, -43.55) * mm, "end": v(-7.03, -43.55) * mm});
            skLineSegment(sketch, "E300.5.4.5", {"start": v(-7.03, -43.55) * mm, "end": v(-7.03, -44.22) * mm});
            skLineSegment(sketch, "E300.5.4.6", {"start": v(-12.03, -44.22) * mm, "end": v(-7.03, -44.22) * mm});
            skLineSegment(sketch, "E300.5.4.7", {"start": v(-12.03, -43.55) * mm, "end": v(-12.03, -44.22) * mm});
            skLineSegment(sketch, "E300.6.0.0", {"start": v(7.02, 47.32) * mm, "end": v(12.02, 47.32) * mm});
            skLineSegment(sketch, "E300.6.0.1", {"start": v(12.02, 46.65) * mm, "end": v(12.02, 47.32) * mm});
            skLineSegment(sketch, "E300.6.0.2", {"start": v(7.02, 46.65) * mm, "end": v(12.02, 46.65) * mm});
            skLineSegment(sketch, "E300.6.0.3", {"start": v(7.02, 46.65) * mm, "end": v(7.02, 47.32) * mm});
            skLineSegment(sketch, "E300.6.0.4", {"start": v(7.02, 32.65) * mm, "end": v(12.02, 32.65) * mm});
            skLineSegment(sketch, "E300.6.0.5", {"start": v(12.02, 32.65) * mm, "end": v(12.02, 31.98) * mm});
            skLineSegment(sketch, "E300.6.0.6", {"start": v(7.02, 31.98) * mm, "end": v(12.02, 31.98) * mm});
            skLineSegment(sketch, "E300.6.0.7", {"start": v(7.02, 32.65) * mm, "end": v(7.02, 31.98) * mm});
            skLineSegment(sketch, "E300.6.1.0", {"start": v(7.02, 28.27) * mm, "end": v(12.02, 28.27) * mm});
            skLineSegment(sketch, "E300.6.1.1", {"start": v(12.02, 27.6) * mm, "end": v(12.02, 28.27) * mm});
            skLineSegment(sketch, "E300.6.1.2", {"start": v(7.02, 27.6) * mm, "end": v(12.02, 27.6) * mm});
            skLineSegment(sketch, "E300.6.1.3", {"start": v(7.02, 27.6) * mm, "end": v(7.02, 28.27) * mm});
            skLineSegment(sketch, "E300.6.1.4", {"start": v(7.02, 13.6) * mm, "end": v(12.02, 13.6) * mm});
            skLineSegment(sketch, "E300.6.1.5", {"start": v(12.02, 13.6) * mm, "end": v(12.02, 12.93) * mm});
            skLineSegment(sketch, "E300.6.1.6", {"start": v(7.02, 12.93) * mm, "end": v(12.02, 12.93) * mm});
            skLineSegment(sketch, "E300.6.1.7", {"start": v(7.02, 13.6) * mm, "end": v(7.02, 12.93) * mm});
            skLineSegment(sketch, "E300.6.2.0", {"start": v(7.02, 9.22) * mm, "end": v(12.02, 9.22) * mm});
            skLineSegment(sketch, "E300.6.2.1", {"start": v(12.02, 8.55) * mm, "end": v(12.02, 9.22) * mm});
            skLineSegment(sketch, "E300.6.2.2", {"start": v(7.02, 8.55) * mm, "end": v(12.02, 8.55) * mm});
            skLineSegment(sketch, "E300.6.2.3", {"start": v(7.02, 8.55) * mm, "end": v(7.02, 9.22) * mm});
            skLineSegment(sketch, "E300.6.2.4", {"start": v(7.02, -5.45) * mm, "end": v(12.02, -5.45) * mm});
            skLineSegment(sketch, "E300.6.2.5", {"start": v(12.02, -5.45) * mm, "end": v(12.02, -6.12) * mm});
            skLineSegment(sketch, "E300.6.2.6", {"start": v(7.02, -6.12) * mm, "end": v(12.02, -6.12) * mm});
            skLineSegment(sketch, "E300.6.2.7", {"start": v(7.02, -5.45) * mm, "end": v(7.02, -6.12) * mm});
            skLineSegment(sketch, "E300.6.3.0", {"start": v(7.02, -9.83) * mm, "end": v(12.02, -9.83) * mm});
            skLineSegment(sketch, "E300.6.3.1", {"start": v(12.02, -10.5) * mm, "end": v(12.02, -9.83) * mm});
            skLineSegment(sketch, "E300.6.3.2", {"start": v(7.02, -10.5) * mm, "end": v(12.02, -10.5) * mm});
            skLineSegment(sketch, "E300.6.3.3", {"start": v(7.02, -10.5) * mm, "end": v(7.02, -9.83) * mm});
            skLineSegment(sketch, "E300.6.3.4", {"start": v(7.02, -24.5) * mm, "end": v(12.02, -24.5) * mm});
            skLineSegment(sketch, "E300.6.3.5", {"start": v(12.02, -24.5) * mm, "end": v(12.02, -25.17) * mm});
            skLineSegment(sketch, "E300.6.3.6", {"start": v(7.02, -25.17) * mm, "end": v(12.02, -25.17) * mm});
            skLineSegment(sketch, "E300.6.3.7", {"start": v(7.02, -24.5) * mm, "end": v(7.02, -25.17) * mm});
            skLineSegment(sketch, "E300.6.4.0", {"start": v(7.02, -28.88) * mm, "end": v(12.02, -28.88) * mm});
            skLineSegment(sketch, "E300.6.4.1", {"start": v(12.02, -29.55) * mm, "end": v(12.02, -28.88) * mm});
            skLineSegment(sketch, "E300.6.4.2", {"start": v(7.02, -29.55) * mm, "end": v(12.02, -29.55) * mm});
            skLineSegment(sketch, "E300.6.4.3", {"start": v(7.02, -29.55) * mm, "end": v(7.02, -28.88) * mm});
            skLineSegment(sketch, "E300.6.4.4", {"start": v(7.02, -43.55) * mm, "end": v(12.02, -43.55) * mm});
            skLineSegment(sketch, "E300.6.4.5", {"start": v(12.02, -43.55) * mm, "end": v(12.02, -44.22) * mm});
            skLineSegment(sketch, "E300.6.4.6", {"start": v(7.02, -44.22) * mm, "end": v(12.02, -44.22) * mm});
            skLineSegment(sketch, "E300.6.4.7", {"start": v(7.02, -43.55) * mm, "end": v(7.02, -44.22) * mm});
            skLineSegment(sketch, "E300.7.0.0", {"start": v(26.07, 47.32) * mm, "end": v(31.07, 47.32) * mm});
            skLineSegment(sketch, "E300.7.0.1", {"start": v(31.07, 46.65) * mm, "end": v(31.07, 47.32) * mm});
            skLineSegment(sketch, "E300.7.0.2", {"start": v(26.07, 46.65) * mm, "end": v(31.07, 46.65) * mm});
            skLineSegment(sketch, "E300.7.0.3", {"start": v(26.07, 46.65) * mm, "end": v(26.07, 47.32) * mm});
            skLineSegment(sketch, "E300.7.0.4", {"start": v(26.07, 32.65) * mm, "end": v(31.07, 32.65) * mm});
            skLineSegment(sketch, "E300.7.0.5", {"start": v(31.07, 32.65) * mm, "end": v(31.07, 31.98) * mm});
            skLineSegment(sketch, "E300.7.0.6", {"start": v(26.07, 31.98) * mm, "end": v(31.07, 31.98) * mm});
            skLineSegment(sketch, "E300.7.0.7", {"start": v(26.07, 32.65) * mm, "end": v(26.07, 31.98) * mm});
            skLineSegment(sketch, "E300.7.1.0", {"start": v(26.07, 28.27) * mm, "end": v(31.07, 28.27) * mm});
            skLineSegment(sketch, "E300.7.1.1", {"start": v(31.07, 27.6) * mm, "end": v(31.07, 28.27) * mm});
            skLineSegment(sketch, "E300.7.1.2", {"start": v(26.07, 27.6) * mm, "end": v(31.07, 27.6) * mm});
            skLineSegment(sketch, "E300.7.1.3", {"start": v(26.07, 27.6) * mm, "end": v(26.07, 28.27) * mm});
            skLineSegment(sketch, "E300.7.1.4", {"start": v(26.07, 13.6) * mm, "end": v(31.07, 13.6) * mm});
            skLineSegment(sketch, "E300.7.1.5", {"start": v(31.07, 13.6) * mm, "end": v(31.07, 12.93) * mm});
            skLineSegment(sketch, "E300.7.1.6", {"start": v(26.07, 12.93) * mm, "end": v(31.07, 12.93) * mm});
            skLineSegment(sketch, "E300.7.1.7", {"start": v(26.07, 13.6) * mm, "end": v(26.07, 12.93) * mm});
            skLineSegment(sketch, "E300.7.2.0", {"start": v(26.07, 9.22) * mm, "end": v(31.07, 9.22) * mm});
            skLineSegment(sketch, "E300.7.2.1", {"start": v(31.07, 8.55) * mm, "end": v(31.07, 9.22) * mm});
            skLineSegment(sketch, "E300.7.2.2", {"start": v(26.07, 8.55) * mm, "end": v(31.07, 8.55) * mm});
            skLineSegment(sketch, "E300.7.2.3", {"start": v(26.07, 8.55) * mm, "end": v(26.07, 9.22) * mm});
            skLineSegment(sketch, "E300.7.2.4", {"start": v(26.07, -5.45) * mm, "end": v(31.07, -5.45) * mm});
            skLineSegment(sketch, "E300.7.2.5", {"start": v(31.07, -5.45) * mm, "end": v(31.07, -6.12) * mm});
            skLineSegment(sketch, "E300.7.2.6", {"start": v(26.07, -6.12) * mm, "end": v(31.07, -6.12) * mm});
            skLineSegment(sketch, "E300.7.2.7", {"start": v(26.07, -5.45) * mm, "end": v(26.07, -6.12) * mm});
            skLineSegment(sketch, "E300.7.3.0", {"start": v(26.07, -9.83) * mm, "end": v(31.07, -9.83) * mm});
            skLineSegment(sketch, "E300.7.3.1", {"start": v(31.07, -10.5) * mm, "end": v(31.07, -9.83) * mm});
            skLineSegment(sketch, "E300.7.3.2", {"start": v(26.07, -10.5) * mm, "end": v(31.07, -10.5) * mm});
            skLineSegment(sketch, "E300.7.3.3", {"start": v(26.07, -10.5) * mm, "end": v(26.07, -9.83) * mm});
            skLineSegment(sketch, "E300.7.3.4", {"start": v(26.07, -24.5) * mm, "end": v(31.07, -24.5) * mm});
            skLineSegment(sketch, "E300.7.3.5", {"start": v(31.07, -24.5) * mm, "end": v(31.07, -25.17) * mm});
            skLineSegment(sketch, "E300.7.3.6", {"start": v(26.07, -25.17) * mm, "end": v(31.07, -25.17) * mm});
            skLineSegment(sketch, "E300.7.3.7", {"start": v(26.07, -24.5) * mm, "end": v(26.07, -25.17) * mm});
            skLineSegment(sketch, "E300.7.4.0", {"start": v(26.07, -28.88) * mm, "end": v(31.07, -28.88) * mm});
            skLineSegment(sketch, "E300.7.4.1", {"start": v(31.07, -29.55) * mm, "end": v(31.07, -28.88) * mm});
            skLineSegment(sketch, "E300.7.4.2", {"start": v(26.07, -29.55) * mm, "end": v(31.07, -29.55) * mm});
            skLineSegment(sketch, "E300.7.4.3", {"start": v(26.07, -29.55) * mm, "end": v(26.07, -28.88) * mm});
            skLineSegment(sketch, "E300.7.4.4", {"start": v(26.07, -43.55) * mm, "end": v(31.07, -43.55) * mm});
            skLineSegment(sketch, "E300.7.4.5", {"start": v(31.07, -43.55) * mm, "end": v(31.07, -44.22) * mm});
            skLineSegment(sketch, "E300.7.4.6", {"start": v(26.07, -44.22) * mm, "end": v(31.07, -44.22) * mm});
            skLineSegment(sketch, "E300.7.4.7", {"start": v(26.07, -43.55) * mm, "end": v(26.07, -44.22) * mm});
            skLineSegment(sketch, "E300.8.0.0", {"start": v(45.12, 47.32) * mm, "end": v(50.12, 47.32) * mm});
            skLineSegment(sketch, "E300.8.0.1", {"start": v(50.12, 46.65) * mm, "end": v(50.12, 47.32) * mm});
            skLineSegment(sketch, "E300.8.0.2", {"start": v(45.12, 46.65) * mm, "end": v(50.12, 46.65) * mm});
            skLineSegment(sketch, "E300.8.0.3", {"start": v(45.12, 46.65) * mm, "end": v(45.12, 47.32) * mm});
            skLineSegment(sketch, "E300.8.0.4", {"start": v(45.12, 32.65) * mm, "end": v(50.12, 32.65) * mm});
            skLineSegment(sketch, "E300.8.0.5", {"start": v(50.12, 32.65) * mm, "end": v(50.12, 31.98) * mm});
            skLineSegment(sketch, "E300.8.0.6", {"start": v(45.12, 31.98) * mm, "end": v(50.12, 31.98) * mm});
            skLineSegment(sketch, "E300.8.0.7", {"start": v(45.12, 32.65) * mm, "end": v(45.12, 31.98) * mm});
            skLineSegment(sketch, "E300.8.1.0", {"start": v(45.12, 28.27) * mm, "end": v(50.12, 28.27) * mm});
            skLineSegment(sketch, "E300.8.1.1", {"start": v(50.12, 27.6) * mm, "end": v(50.12, 28.27) * mm});
            skLineSegment(sketch, "E300.8.1.2", {"start": v(45.12, 27.6) * mm, "end": v(50.12, 27.6) * mm});
            skLineSegment(sketch, "E300.8.1.3", {"start": v(45.12, 27.6) * mm, "end": v(45.12, 28.27) * mm});
            skLineSegment(sketch, "E300.8.1.4", {"start": v(45.12, 13.6) * mm, "end": v(50.12, 13.6) * mm});
            skLineSegment(sketch, "E300.8.1.5", {"start": v(50.12, 13.6) * mm, "end": v(50.12, 12.93) * mm});
            skLineSegment(sketch, "E300.8.1.6", {"start": v(45.12, 12.93) * mm, "end": v(50.12, 12.93) * mm});
            skLineSegment(sketch, "E300.8.1.7", {"start": v(45.12, 13.6) * mm, "end": v(45.12, 12.93) * mm});
            skLineSegment(sketch, "E300.8.2.0", {"start": v(45.12, 9.22) * mm, "end": v(50.12, 9.22) * mm});
            skLineSegment(sketch, "E300.8.2.1", {"start": v(50.12, 8.55) * mm, "end": v(50.12, 9.22) * mm});
            skLineSegment(sketch, "E300.8.2.2", {"start": v(45.12, 8.55) * mm, "end": v(50.12, 8.55) * mm});
            skLineSegment(sketch, "E300.8.2.3", {"start": v(45.12, 8.55) * mm, "end": v(45.12, 9.22) * mm});
            skLineSegment(sketch, "E300.8.2.4", {"start": v(45.12, -5.45) * mm, "end": v(50.12, -5.45) * mm});
            skLineSegment(sketch, "E300.8.2.5", {"start": v(50.12, -5.45) * mm, "end": v(50.12, -6.12) * mm});
            skLineSegment(sketch, "E300.8.2.6", {"start": v(45.12, -6.12) * mm, "end": v(50.12, -6.12) * mm});
            skLineSegment(sketch, "E300.8.2.7", {"start": v(45.12, -5.45) * mm, "end": v(45.12, -6.12) * mm});
            skLineSegment(sketch, "E300.8.3.0", {"start": v(45.12, -9.83) * mm, "end": v(50.12, -9.83) * mm});
            skLineSegment(sketch, "E300.8.3.1", {"start": v(50.12, -10.5) * mm, "end": v(50.12, -9.83) * mm});
            skLineSegment(sketch, "E300.8.3.2", {"start": v(45.12, -10.5) * mm, "end": v(50.12, -10.5) * mm});
            skLineSegment(sketch, "E300.8.3.3", {"start": v(45.12, -10.5) * mm, "end": v(45.12, -9.83) * mm});
            skLineSegment(sketch, "E300.8.3.4", {"start": v(45.12, -24.5) * mm, "end": v(50.12, -24.5) * mm});
            skLineSegment(sketch, "E300.8.3.5", {"start": v(50.12, -24.5) * mm, "end": v(50.12, -25.17) * mm});
            skLineSegment(sketch, "E300.8.3.6", {"start": v(45.12, -25.17) * mm, "end": v(50.12, -25.17) * mm});
            skLineSegment(sketch, "E300.8.3.7", {"start": v(45.12, -24.5) * mm, "end": v(45.12, -25.17) * mm});
            skLineSegment(sketch, "E300.8.4.0", {"start": v(45.12, -28.88) * mm, "end": v(50.12, -28.88) * mm});
            skLineSegment(sketch, "E300.8.4.1", {"start": v(50.12, -29.55) * mm, "end": v(50.12, -28.88) * mm});
            skLineSegment(sketch, "E300.8.4.2", {"start": v(45.12, -29.55) * mm, "end": v(50.12, -29.55) * mm});
            skLineSegment(sketch, "E300.8.4.3", {"start": v(45.12, -29.55) * mm, "end": v(45.12, -28.88) * mm});
            skLineSegment(sketch, "E300.8.4.4", {"start": v(45.12, -43.55) * mm, "end": v(50.12, -43.55) * mm});
            skLineSegment(sketch, "E300.8.4.5", {"start": v(50.12, -43.55) * mm, "end": v(50.12, -44.22) * mm});
            skLineSegment(sketch, "E300.8.4.6", {"start": v(45.12, -44.22) * mm, "end": v(50.12, -44.22) * mm});
            skLineSegment(sketch, "E300.8.4.7", {"start": v(45.12, -43.55) * mm, "end": v(45.12, -44.22) * mm});
            skLineSegment(sketch, "E300.9.0.0", {"start": v(64.17, 47.32) * mm, "end": v(69.17, 47.32) * mm});
            skLineSegment(sketch, "E300.9.0.1", {"start": v(69.17, 46.65) * mm, "end": v(69.17, 47.32) * mm});
            skLineSegment(sketch, "E300.9.0.2", {"start": v(64.17, 46.65) * mm, "end": v(69.17, 46.65) * mm});
            skLineSegment(sketch, "E300.9.0.3", {"start": v(64.17, 46.65) * mm, "end": v(64.17, 47.32) * mm});
            skLineSegment(sketch, "E300.9.0.4", {"start": v(64.17, 32.65) * mm, "end": v(69.17, 32.65) * mm});
            skLineSegment(sketch, "E300.9.0.5", {"start": v(69.17, 32.65) * mm, "end": v(69.17, 31.98) * mm});
            skLineSegment(sketch, "E300.9.0.6", {"start": v(64.17, 31.98) * mm, "end": v(69.17, 31.98) * mm});
            skLineSegment(sketch, "E300.9.0.7", {"start": v(64.17, 32.65) * mm, "end": v(64.17, 31.98) * mm});
            skLineSegment(sketch, "E300.9.1.0", {"start": v(64.17, 28.27) * mm, "end": v(69.17, 28.27) * mm});
            skLineSegment(sketch, "E300.9.1.1", {"start": v(69.17, 27.6) * mm, "end": v(69.17, 28.27) * mm});
            skLineSegment(sketch, "E300.9.1.2", {"start": v(64.17, 27.6) * mm, "end": v(69.17, 27.6) * mm});
            skLineSegment(sketch, "E300.9.1.3", {"start": v(64.17, 27.6) * mm, "end": v(64.17, 28.27) * mm});
            skLineSegment(sketch, "E300.9.1.4", {"start": v(64.17, 13.6) * mm, "end": v(69.17, 13.6) * mm});
            skLineSegment(sketch, "E300.9.1.5", {"start": v(69.17, 13.6) * mm, "end": v(69.17, 12.93) * mm});
            skLineSegment(sketch, "E300.9.1.6", {"start": v(64.17, 12.93) * mm, "end": v(69.17, 12.93) * mm});
            skLineSegment(sketch, "E300.9.1.7", {"start": v(64.17, 13.6) * mm, "end": v(64.17, 12.93) * mm});
            skLineSegment(sketch, "E300.9.2.0", {"start": v(64.17, 9.22) * mm, "end": v(69.17, 9.22) * mm});
            skLineSegment(sketch, "E300.9.2.1", {"start": v(69.17, 8.55) * mm, "end": v(69.17, 9.22) * mm});
            skLineSegment(sketch, "E300.9.2.2", {"start": v(64.17, 8.55) * mm, "end": v(69.17, 8.55) * mm});
            skLineSegment(sketch, "E300.9.2.3", {"start": v(64.17, 8.55) * mm, "end": v(64.17, 9.22) * mm});
            skLineSegment(sketch, "E300.9.2.4", {"start": v(64.17, -5.45) * mm, "end": v(69.17, -5.45) * mm});
            skLineSegment(sketch, "E300.9.2.5", {"start": v(69.17, -5.45) * mm, "end": v(69.17, -6.12) * mm});
            skLineSegment(sketch, "E300.9.2.6", {"start": v(64.17, -6.12) * mm, "end": v(69.17, -6.12) * mm});
            skLineSegment(sketch, "E300.9.2.7", {"start": v(64.17, -5.45) * mm, "end": v(64.17, -6.12) * mm});
            skLineSegment(sketch, "E300.9.3.0", {"start": v(64.17, -9.83) * mm, "end": v(69.17, -9.83) * mm});
            skLineSegment(sketch, "E300.9.3.1", {"start": v(69.17, -10.5) * mm, "end": v(69.17, -9.83) * mm});
            skLineSegment(sketch, "E300.9.3.2", {"start": v(64.17, -10.5) * mm, "end": v(69.17, -10.5) * mm});
            skLineSegment(sketch, "E300.9.3.3", {"start": v(64.17, -10.5) * mm, "end": v(64.17, -9.83) * mm});
            skLineSegment(sketch, "E300.9.3.4", {"start": v(64.17, -24.5) * mm, "end": v(69.17, -24.5) * mm});
            skLineSegment(sketch, "E300.9.3.5", {"start": v(69.17, -24.5) * mm, "end": v(69.17, -25.17) * mm});
            skLineSegment(sketch, "E300.9.3.6", {"start": v(64.17, -25.17) * mm, "end": v(69.17, -25.17) * mm});
            skLineSegment(sketch, "E300.9.3.7", {"start": v(64.17, -24.5) * mm, "end": v(64.17, -25.17) * mm});
            skLineSegment(sketch, "E300.9.4.0", {"start": v(64.17, -28.88) * mm, "end": v(69.17, -28.88) * mm});
            skLineSegment(sketch, "E300.9.4.1", {"start": v(69.17, -29.55) * mm, "end": v(69.17, -28.88) * mm});
            skLineSegment(sketch, "E300.9.4.2", {"start": v(64.17, -29.55) * mm, "end": v(69.17, -29.55) * mm});
            skLineSegment(sketch, "E300.9.4.3", {"start": v(64.17, -29.55) * mm, "end": v(64.17, -28.88) * mm});
            skLineSegment(sketch, "E300.9.4.4", {"start": v(64.17, -43.55) * mm, "end": v(69.17, -43.55) * mm});
            skLineSegment(sketch, "E300.9.4.5", {"start": v(69.17, -43.55) * mm, "end": v(69.17, -44.22) * mm});
            skLineSegment(sketch, "E300.9.4.6", {"start": v(64.17, -44.22) * mm, "end": v(69.17, -44.22) * mm});
            skLineSegment(sketch, "E300.9.4.7", {"start": v(64.17, -43.55) * mm, "end": v(64.17, -44.22) * mm});
            skLineSegment(sketch, "E300.10.0.0", {"start": v(83.22, 47.32) * mm, "end": v(88.22, 47.32) * mm});
            skLineSegment(sketch, "E300.10.0.1", {"start": v(88.22, 46.65) * mm, "end": v(88.22, 47.32) * mm});
            skLineSegment(sketch, "E300.10.0.2", {"start": v(83.22, 46.65) * mm, "end": v(88.22, 46.65) * mm});
            skLineSegment(sketch, "E300.10.0.3", {"start": v(83.22, 46.65) * mm, "end": v(83.22, 47.32) * mm});
            skLineSegment(sketch, "E300.10.0.4", {"start": v(83.22, 32.65) * mm, "end": v(88.22, 32.65) * mm});
            skLineSegment(sketch, "E300.10.0.5", {"start": v(88.22, 32.65) * mm, "end": v(88.22, 31.98) * mm});
            skLineSegment(sketch, "E300.10.0.6", {"start": v(83.22, 31.98) * mm, "end": v(88.22, 31.98) * mm});
            skLineSegment(sketch, "E300.10.0.7", {"start": v(83.22, 32.65) * mm, "end": v(83.22, 31.98) * mm});
            skLineSegment(sketch, "E300.10.1.0", {"start": v(83.22, 28.27) * mm, "end": v(88.22, 28.27) * mm});
            skLineSegment(sketch, "E300.10.1.1", {"start": v(88.22, 27.6) * mm, "end": v(88.22, 28.27) * mm});
            skLineSegment(sketch, "E300.10.1.2", {"start": v(83.22, 27.6) * mm, "end": v(88.22, 27.6) * mm});
            skLineSegment(sketch, "E300.10.1.3", {"start": v(83.22, 27.6) * mm, "end": v(83.22, 28.27) * mm});
            skLineSegment(sketch, "E300.10.1.4", {"start": v(83.22, 13.6) * mm, "end": v(88.22, 13.6) * mm});
            skLineSegment(sketch, "E300.10.1.5", {"start": v(88.22, 13.6) * mm, "end": v(88.22, 12.93) * mm});
            skLineSegment(sketch, "E300.10.1.6", {"start": v(83.22, 12.93) * mm, "end": v(88.22, 12.93) * mm});
            skLineSegment(sketch, "E300.10.1.7", {"start": v(83.22, 13.6) * mm, "end": v(83.22, 12.93) * mm});
            skLineSegment(sketch, "E300.10.2.0", {"start": v(83.22, 9.22) * mm, "end": v(88.22, 9.22) * mm});
            skLineSegment(sketch, "E300.10.2.1", {"start": v(88.22, 8.55) * mm, "end": v(88.22, 9.22) * mm});
            skLineSegment(sketch, "E300.10.2.2", {"start": v(83.22, 8.55) * mm, "end": v(88.22, 8.55) * mm});
            skLineSegment(sketch, "E300.10.2.3", {"start": v(83.22, 8.55) * mm, "end": v(83.22, 9.22) * mm});
            skLineSegment(sketch, "E300.10.2.4", {"start": v(83.22, -5.45) * mm, "end": v(88.22, -5.45) * mm});
            skLineSegment(sketch, "E300.10.2.5", {"start": v(88.22, -5.45) * mm, "end": v(88.22, -6.12) * mm});
            skLineSegment(sketch, "E300.10.2.6", {"start": v(83.22, -6.12) * mm, "end": v(88.22, -6.12) * mm});
            skLineSegment(sketch, "E300.10.2.7", {"start": v(83.22, -5.45) * mm, "end": v(83.22, -6.12) * mm});
            skLineSegment(sketch, "E300.10.3.0", {"start": v(83.22, -9.83) * mm, "end": v(88.22, -9.83) * mm});
            skLineSegment(sketch, "E300.10.3.1", {"start": v(88.22, -10.5) * mm, "end": v(88.22, -9.83) * mm});
            skLineSegment(sketch, "E300.10.3.2", {"start": v(83.22, -10.5) * mm, "end": v(88.22, -10.5) * mm});
            skLineSegment(sketch, "E300.10.3.3", {"start": v(83.22, -10.5) * mm, "end": v(83.22, -9.83) * mm});
            skLineSegment(sketch, "E300.10.3.4", {"start": v(83.22, -24.5) * mm, "end": v(88.22, -24.5) * mm});
            skLineSegment(sketch, "E300.10.3.5", {"start": v(88.22, -24.5) * mm, "end": v(88.22, -25.17) * mm});
            skLineSegment(sketch, "E300.10.3.6", {"start": v(83.22, -25.17) * mm, "end": v(88.22, -25.17) * mm});
            skLineSegment(sketch, "E300.10.3.7", {"start": v(83.22, -24.5) * mm, "end": v(83.22, -25.17) * mm});
            skLineSegment(sketch, "E300.10.4.0", {"start": v(83.22, -28.88) * mm, "end": v(88.22, -28.88) * mm});
            skLineSegment(sketch, "E300.10.4.1", {"start": v(88.22, -29.55) * mm, "end": v(88.22, -28.88) * mm});
            skLineSegment(sketch, "E300.10.4.2", {"start": v(83.22, -29.55) * mm, "end": v(88.22, -29.55) * mm});
            skLineSegment(sketch, "E300.10.4.3", {"start": v(83.22, -29.55) * mm, "end": v(83.22, -28.88) * mm});
            skLineSegment(sketch, "E300.10.4.4", {"start": v(83.22, -43.55) * mm, "end": v(88.22, -43.55) * mm});
            skLineSegment(sketch, "E300.10.4.5", {"start": v(88.22, -43.55) * mm, "end": v(88.22, -44.22) * mm});
            skLineSegment(sketch, "E300.10.4.6", {"start": v(83.22, -44.22) * mm, "end": v(88.22, -44.22) * mm});
            skLineSegment(sketch, "E300.10.4.7", {"start": v(83.22, -43.55) * mm, "end": v(83.22, -44.22) * mm});
            skLineSegment(sketch, "E300.11.0.0", {"start": v(102.27, 47.32) * mm, "end": v(107.27, 47.32) * mm});
            skLineSegment(sketch, "E300.11.0.1", {"start": v(107.27, 46.65) * mm, "end": v(107.27, 47.32) * mm});
            skLineSegment(sketch, "E300.11.0.2", {"start": v(102.27, 46.65) * mm, "end": v(107.27, 46.65) * mm});
            skLineSegment(sketch, "E300.11.0.3", {"start": v(102.27, 46.65) * mm, "end": v(102.27, 47.32) * mm});
            skLineSegment(sketch, "E300.11.0.4", {"start": v(102.27, 32.65) * mm, "end": v(107.27, 32.65) * mm});
            skLineSegment(sketch, "E300.11.0.5", {"start": v(107.27, 32.65) * mm, "end": v(107.27, 31.98) * mm});
            skLineSegment(sketch, "E300.11.0.6", {"start": v(102.27, 31.98) * mm, "end": v(107.27, 31.98) * mm});
            skLineSegment(sketch, "E300.11.0.7", {"start": v(102.27, 32.65) * mm, "end": v(102.27, 31.98) * mm});
            skLineSegment(sketch, "E300.11.1.0", {"start": v(102.27, 28.27) * mm, "end": v(107.27, 28.27) * mm});
            skLineSegment(sketch, "E300.11.1.1", {"start": v(107.27, 27.6) * mm, "end": v(107.27, 28.27) * mm});
            skLineSegment(sketch, "E300.11.1.2", {"start": v(102.27, 27.6) * mm, "end": v(107.27, 27.6) * mm});
            skLineSegment(sketch, "E300.11.1.3", {"start": v(102.27, 27.6) * mm, "end": v(102.27, 28.27) * mm});
            skLineSegment(sketch, "E300.11.1.4", {"start": v(102.27, 13.6) * mm, "end": v(107.27, 13.6) * mm});
            skLineSegment(sketch, "E300.11.1.5", {"start": v(107.27, 13.6) * mm, "end": v(107.27, 12.93) * mm});
            skLineSegment(sketch, "E300.11.1.6", {"start": v(102.27, 12.93) * mm, "end": v(107.27, 12.93) * mm});
            skLineSegment(sketch, "E300.11.1.7", {"start": v(102.27, 13.6) * mm, "end": v(102.27, 12.93) * mm});
            skLineSegment(sketch, "E300.11.2.0", {"start": v(102.27, 9.22) * mm, "end": v(107.27, 9.22) * mm});
            skLineSegment(sketch, "E300.11.2.1", {"start": v(107.27, 8.55) * mm, "end": v(107.27, 9.22) * mm});
            skLineSegment(sketch, "E300.11.2.2", {"start": v(102.27, 8.55) * mm, "end": v(107.27, 8.55) * mm});
            skLineSegment(sketch, "E300.11.2.3", {"start": v(102.27, 8.55) * mm, "end": v(102.27, 9.22) * mm});
            skLineSegment(sketch, "E300.11.2.4", {"start": v(102.27, -5.45) * mm, "end": v(107.27, -5.45) * mm});
            skLineSegment(sketch, "E300.11.2.5", {"start": v(107.27, -5.45) * mm, "end": v(107.27, -6.12) * mm});
            skLineSegment(sketch, "E300.11.2.6", {"start": v(102.27, -6.12) * mm, "end": v(107.27, -6.12) * mm});
            skLineSegment(sketch, "E300.11.2.7", {"start": v(102.27, -5.45) * mm, "end": v(102.27, -6.12) * mm});
            skLineSegment(sketch, "E300.11.3.0", {"start": v(102.27, -9.83) * mm, "end": v(107.27, -9.83) * mm});
            skLineSegment(sketch, "E300.11.3.1", {"start": v(107.27, -10.5) * mm, "end": v(107.27, -9.83) * mm});
            skLineSegment(sketch, "E300.11.3.2", {"start": v(102.27, -10.5) * mm, "end": v(107.27, -10.5) * mm});
            skLineSegment(sketch, "E300.11.3.3", {"start": v(102.27, -10.5) * mm, "end": v(102.27, -9.83) * mm});
            skLineSegment(sketch, "E300.11.3.4", {"start": v(102.27, -24.5) * mm, "end": v(107.27, -24.5) * mm});
            skLineSegment(sketch, "E300.11.3.5", {"start": v(107.27, -24.5) * mm, "end": v(107.27, -25.17) * mm});
            skLineSegment(sketch, "E300.11.3.6", {"start": v(102.27, -25.17) * mm, "end": v(107.27, -25.17) * mm});
            skLineSegment(sketch, "E300.11.3.7", {"start": v(102.27, -24.5) * mm, "end": v(102.27, -25.17) * mm});
            skLineSegment(sketch, "E300.11.4.0", {"start": v(102.27, -28.88) * mm, "end": v(107.27, -28.88) * mm});
            skLineSegment(sketch, "E300.11.4.1", {"start": v(107.27, -29.55) * mm, "end": v(107.27, -28.88) * mm});
            skLineSegment(sketch, "E300.11.4.2", {"start": v(102.27, -29.55) * mm, "end": v(107.27, -29.55) * mm});
            skLineSegment(sketch, "E300.11.4.3", {"start": v(102.27, -29.55) * mm, "end": v(102.27, -28.88) * mm});
            skLineSegment(sketch, "E300.11.4.4", {"start": v(102.27, -43.55) * mm, "end": v(107.27, -43.55) * mm});
            skLineSegment(sketch, "E300.11.4.5", {"start": v(107.27, -43.55) * mm, "end": v(107.27, -44.22) * mm});
            skLineSegment(sketch, "E300.11.4.6", {"start": v(102.27, -44.22) * mm, "end": v(107.27, -44.22) * mm});
            skLineSegment(sketch, "E300.11.4.7", {"start": v(102.27, -43.55) * mm, "end": v(102.27, -44.22) * mm});
            skLineSegment(sketch, "E300.direction1", {"start": v(-107.28, 47.32) * mm, "end": v(-88.23, 47.32) * mm, "construction": true});
            skLineSegment(sketch, "E300.direction2", {"start": v(-107.28, 47.32) * mm, "end": v(-107.28, 28.27) * mm, "construction": true});
            skSolve(sketch);
        }
        {
            var Q0;
            Q0 = qSketchRegion(id + "F21", true);
            extrude(context, id + "F22", {"entities" : qUnion([Q0]), "operationType" : NewBodyOperationType.REMOVE, "oppositeDirection" : true, "depth" : 3.5 * mm, "offsetDistance" : 25 * mm});
        }
    });
